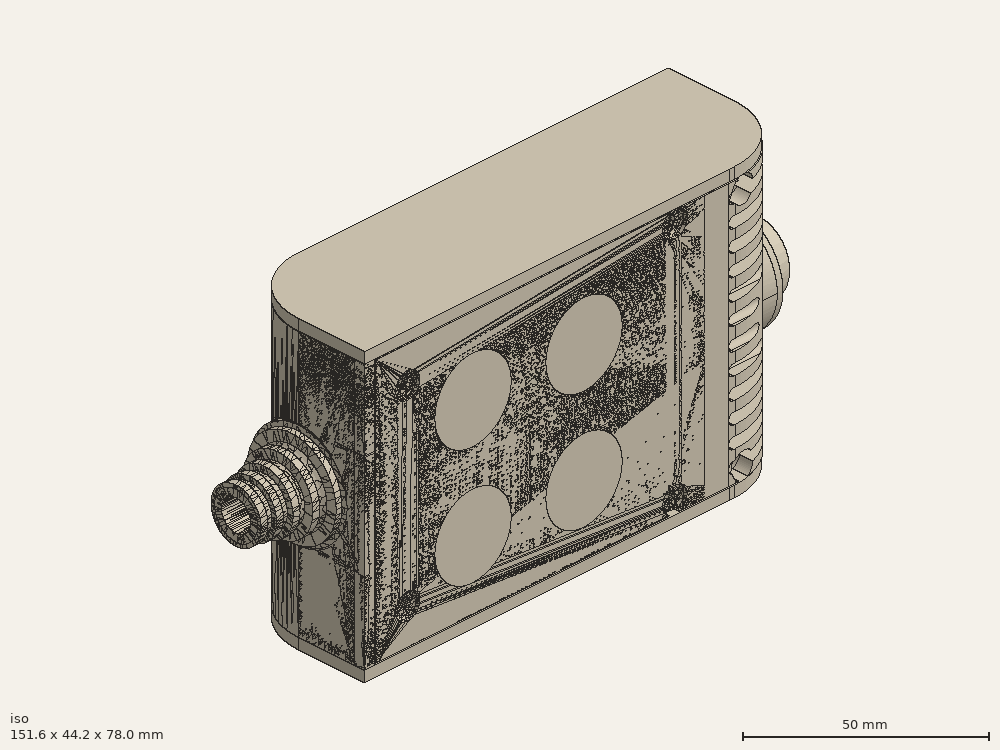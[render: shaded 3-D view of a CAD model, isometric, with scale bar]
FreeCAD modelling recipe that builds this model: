
FCSTD DOCUMENT  (FreeCAD 0.19R0.19.2)
Label: enclosure_201FCStd
License: All rights reserved
LicenseURL: http://en.wikipedia.org/wiki/All_rights_reserved
objects: Part::Revolution×152, Part::MultiFuse×146, Part::Feature×146, Sketcher::SketchObject×84, Part::Cut×70, Part::Cylinder×70, Part::Extrusion×67, Part::Fillet×58, Part::Box×36, App::MeasureDistance×4, PartDesign::Body×2, Image::ImagePlane×1
note: 831 computed .brp shape members not serialized (recipe doc carries the construction recipe); baked Part::Feature solids carry a one-line shape summary decoded from their .brp

FEATURE [Sketcher::SketchObject] Sketch  label="topSketch"
  FullyConstrained = true
  sketch-geometry (20):
    g0: LineSegment StartX=5.21097e-06 StartY=3 StartZ=0 EndX=5.21097e-06 EndY=19 EndZ=0
    g1: ArcOfCircle CenterX=19 CenterY=19 CenterZ=0 NormalX=0 NormalY=0 NormalZ=1 AngleXU=0 Radius=19 StartAngle=1.5708 EndAngle=3.14159
    g2: ArcOfCircle CenterX=19 CenterY=19 CenterZ=0 NormalX=0 NormalY=0 NormalZ=1 AngleXU=0 Radius=16 StartAngle=1.5708 EndAngle=3.14159
    g3: LineSegment StartX=114 StartY=35 StartZ=0 EndX=19 EndY=35 EndZ=0
    g4: LineSegment StartX=5.21097e-06 StartY=3 StartZ=0 EndX=5.21097e-06 EndY=0 EndZ=0
    g5: LineSegment StartX=3 StartY=0 StartZ=0 EndX=5.21097e-06 EndY=0 EndZ=0
    g6: LineSegment StartX=3 StartY=19 StartZ=0 EndX=3 EndY=0 EndZ=0
    g7: LineSegment StartX=19 StartY=38 StartZ=0 EndX=124 EndY=38 EndZ=0
    g8: Circle CenterX=119 CenterY=35 CenterZ=0 NormalX=0 NormalY=0 NormalZ=1 AngleXU=0 Radius=1
    g9: Circle CenterX=121 CenterY=35 CenterZ=0 NormalX=0 NormalY=0 NormalZ=1 AngleXU=0 Radius=1
    g10: Circle CenterX=121 CenterY=33 CenterZ=0 NormalX=0 NormalY=0 NormalZ=1 AngleXU=0 Radius=1
    g11: BSplineCurve PolesCount=3 KnotsCount=2 Degree=2 IsPeriodic=0
    g12: GeomPoint X=119 Y=35 Z=0
    g13: GeomPoint X=121 Y=33 Z=0
    g14: LineSegment StartX=119 StartY=35 StartZ=0 EndX=114 EndY=35 EndZ=0
    g15: ArcOfCircle CenterX=105 CenterY=19 CenterZ=0 NormalX=0 NormalY=0 NormalZ=1 AngleXU=0 Radius=19 StartAngle=5.7297 EndAngle=6.28319
    g16: ArcOfCircle CenterX=105 CenterY=19 CenterZ=0 NormalX=0 NormalY=0 NormalZ=1 AngleXU=0 Radius=16 StartAngle=5.60905 EndAngle=6.28319
    g17: LineSegment StartX=121 StartY=33 StartZ=0 EndX=121 EndY=19 EndZ=0
    g18: LineSegment StartX=124 StartY=38 StartZ=0 EndX=124 EndY=19 EndZ=0
    g19: LineSegment StartX=117.5 StartY=9.01251 StartZ=0 EndX=121.163 EndY=9.0125 EndZ=0
  constraints (46):
    c: Vertical(g0)
    c: Block(g0)
    c: Coincident(g1,g0)
    c: Block(g1)
    c: Coincident(g2,g1)
    c: Block(g2)
    c: Coincident(g3,g2)
    c: Horizontal(g3)
    c: Tangent(g3,g2)
    c: Coincident(g4,g0)
    c: Distance(g4) = 3
    c: Vertical(g4)
    c: Coincident(g5,g4)
    c: Horizontal(g5)
    c: Coincident(g6,g2)
    c: Coincident(g6,g5)
    c: Vertical(g6)
    c: Horizontal(g7)
    c: Distance(g7) = 105
    c: Coincident(g7,g1)
    c: Block(g3)
    c: Weight(g8) = 1
    c: Equal(g8,g9)
    c: Equal(g8,g10)
    c: InternalAlignment(g8,g11)
    c: InternalAlignment(g9,g11)
    c: InternalAlignment(g10,g11)
    c: InternalAlignment(g12,g11)
    c: InternalAlignment(g13,g11)
    c: Block(g11)
    c: Coincident(g14,g11)
    c: Coincident(g14,g3)
    c: Horizontal(g14)
    c: Block(g15)
    c: Coincident(g16,g15)
    c: Block(g16)
    c: Coincident(g17,g11)
    c: Coincident(g17,g16)
    c: Vertical(g17)
    c: Distance(g17) = 14
    c: Coincident(g18,g7)
    c: Coincident(g18,g15)
    c: Vertical(g18)
    c: Distance(g18) = 19
    c: Coincident(g19,g16)
    c: Coincident(g19,g15)
FEATURE [Sketcher::SketchObject] Sketch001  label="bottomSketch"
  FullyConstrained = true
  sketch-geometry (32):
    g0: LineSegment StartX=3.3 StartY=-6.03275e-07 StartZ=0 EndX=98 EndY=-6.03275e-07 EndZ=0
    g1: ArcOfCircle CenterX=98 CenterY=19 CenterZ=0 NormalX=0 NormalY=0 NormalZ=1 AngleXU=0 Radius=19 StartAngle=4.71239 EndAngle=5.71103
    g2: LineSegment StartX=6.3 StartY=8 StartZ=0 EndX=3.3 EndY=8 EndZ=0
    g3: LineSegment StartX=3.3 StartY=8 StartZ=0 EndX=3.3 EndY=-6.03275e-07 EndZ=0
    g4: ArcOfCircle CenterX=8.3 CenterY=5 CenterZ=0 NormalX=0 NormalY=0 NormalZ=1 AngleXU=0 Radius=2 StartAngle=3.14159 EndAngle=4.71239
    g5: LineSegment StartX=6.3 StartY=8 StartZ=0 EndX=6.3 EndY=5 EndZ=0
    g6: ArcOfCircle CenterX=98 CenterY=19 CenterZ=0 NormalX=0 NormalY=0 NormalZ=1 AngleXU=0 Radius=12.7 StartAngle=4.71239 EndAngle=6.28319
    g7: LineSegment StartX=94.7 StartY=3 StartZ=0 EndX=8.3 EndY=3 EndZ=0
    g8-g12: Circle x5 (B-spline internal-alignment scaffolding for g13; pole/knot coordinates omitted)
    g13: BSplineCurve PolesCount=5 KnotsCount=3 Degree=3 IsPeriodic=0
    g14: GeomPoint X=98 Y=6.3 Z=0
    g15: GeomPoint X=96.3938 Y=4.71946 Z=0
    g16: GeomPoint X=94.7 Y=3 Z=0
    g17-g23: Circle x7 (B-spline internal-alignment scaffolding for g24; pole/knot coordinates omitted)
    g24: BSplineCurve PolesCount=7 KnotsCount=5 Degree=3 IsPeriodic=0
    g25-g29: GeomPoint x5 (B-spline internal-alignment scaffolding for g24; pole/knot coordinates omitted)
    g30: ArcOfCircle CenterX=98 CenterY=19 CenterZ=0 NormalX=0 NormalY=0 NormalZ=1 AngleXU=0 Radius=15.7 StartAngle=5.81226 EndAngle=6.28319
    g31: LineSegment StartX=110.7 StartY=19 StartZ=0 EndX=113.7 EndY=19 EndZ=0
  constraints (41):
    c: Horizontal(g0)
    c: Coincident(g1,g0)
    c: Block(g1)
    c: Horizontal(g2)
    c: Distance(g2) = 3
    c: Coincident(g3,g2)
    c: Vertical(g3)
    c: Coincident(g3,g0)
    c: Block(g4)
    c: Block(g2)
    c: Coincident(g5,g2)
    c: Coincident(g5,g4)
    c: Vertical(g5)
    c: Coincident(g6,g1)
    c: Block(g6)
    c: Coincident(g7,g4)
    c: Horizontal(g7)
    c: Block(g0)
    c: Block(g7)
    c: Block(g3)
    c: Coincident(g13,g6)
    c: Weight(g8) = 1
    c: Equal(g8, g9-g12) x4
    c: Coincident(g13,g7)
    c: InternalAlignment(g8-g12 -> g13) x5
    c: InternalAlignment(g14,g13)
    c: InternalAlignment(g15,g13)
    c: InternalAlignment(g16,g13)
    c: Block(g13)
    c: Weight(g17) = 1
    c: Equal(g17, g18-g23) x6
    c: Coincident(g24,g1)
    c: InternalAlignment(g17-g23 -> g24) x7
    c: InternalAlignment(g25-g29 -> g24) x5
    c: Block(g24)
    c: Coincident(g30,g24)
    c: Coincident(g31,g6)
    c: Coincident(g31,g30)
    c: Horizontal(g31)
    c: Block(g31)
    c: Block(g30)
FEATURE [Part::Extrusion] Extrude  label="top"
  Base = -> Sketch
  Dir = (0,0,1)
  DirMode = 2
  FaceMakerClass = Part::FaceMakerBullseye
  LengthFwd = 72
  LengthRev = 0
  Solid = true
  Symmetric = false
FEATURE [Part::Extrusion] Extrude001  label="bottom"
  Base = -> Sketch001
  Dir = (0,0,1)
  DirMode = 2
  FaceMakerClass = Part::FaceMakerBullseye
  LengthFwd = 71.4
  LengthRev = 0
  Placement = pos=(0,0,0.3) rot=(0,0,1;0rad)
  Solid = true
  Symmetric = false
FEATURE [Sketcher::SketchObject] Sketch002  label="topSketch001"
  FullyConstrained = true
  sketch-geometry (8):
    g0: ArcOfCircle CenterX=19 CenterY=19.0975 CenterZ=0 NormalX=0 NormalY=0 NormalZ=1 AngleXU=0 Radius=18.9025 StartAngle=1.5708 EndAngle=3.14674
    g1: LineSegment StartX=0.0977805 StartY=19.0003 StartZ=0 EndX=0.0977805 EndY=0.000251602 EndZ=0
    g2: LineSegment StartX=19 StartY=38 StartZ=0 EndX=124 EndY=38 EndZ=0
    g3: LineSegment StartX=0.0977805 StartY=0.000251602 StartZ=0 EndX=105.098 EndY=0.000251602 EndZ=0
    g4: LineSegment StartX=124 StartY=38 StartZ=0 EndX=125.616 EndY=38 EndZ=0
    g5: LineSegment StartX=105.098 StartY=0.000251602 StartZ=0 EndX=106.713 EndY=0.000251602 EndZ=0
    g6: ArcOfCircle CenterX=106.616 CenterY=19 CenterZ=0 NormalX=0 NormalY=0 NormalZ=1 AngleXU=0 Radius=19 StartAngle=4.71754 EndAngle=6.28319
    g7: LineSegment StartX=125.616 StartY=38 StartZ=0 EndX=125.616 EndY=19 EndZ=0
  constraints (21):
    c: Block(g0)
    c: Coincident(g1,g0)
    c: Vertical(g1)
    c: Horizontal(g2)
    c: Distance(g2) = 105
    c: Coincident(g2,g0)
    c: Distance(g1) = 19
    c: Coincident(g3,g1)
    c: Horizontal(g3)
    c: Distance(g3) = 105
    c: Coincident(g4,g2)
    c: Horizontal(g4)
    c: Distance(g4) = 1.61553
    c: Horizontal(g5)
    c: Equal(g4,g5) = 1.61553
    c: Coincident(g5,g3)
    c: Block(g6)
    c: Coincident(g6,g5)
    c: Coincident(g7,g4)
    c: Coincident(g7,g6)
    c: Vertical(g7)
FEATURE [Part::Extrusion] Extrude002  label="sideA"
  Base = -> Sketch002
  Dir = (0,0,1)
  DirMode = 2
  FaceMakerClass = Part::FaceMakerBullseye
  LengthFwd = 3
  LengthRev = 0
  Placement = pos=(0,0,-3) rot=(0,0,1;0rad)
  Solid = true
  Symmetric = false
FEATURE [Sketcher::SketchObject] Sketch003  label="topSketch002"
  FullyConstrained = true
  sketch-geometry (6):
    g0: LineSegment StartX=19 StartY=38 StartZ=0 EndX=117 EndY=38 EndZ=0
    g1: ArcOfCircle CenterX=19 CenterY=19 CenterZ=0 NormalX=0 NormalY=0 NormalZ=1 AngleXU=0 Radius=19 StartAngle=1.5708 EndAngle=3.14159
    g2: LineSegment StartX=117 StartY=38 StartZ=0 EndX=117 EndY=19 EndZ=0
    g3: LineSegment StartX=98 StartY=1.0161e-12 StartZ=0 EndX=5.22862e-06 EndY=1.0161e-12 EndZ=0
    g4: LineSegment StartX=5.22862e-06 StartY=19 StartZ=0 EndX=5.22862e-06 EndY=1.0161e-12 EndZ=0
    g5: ArcOfCircle CenterX=98 CenterY=19 CenterZ=0 NormalX=0 NormalY=0 NormalZ=1 AngleXU=0 Radius=19 StartAngle=4.71239 EndAngle=6.28319
  constraints (16):
    c: Horizontal(g0)
    c: Distance(g0) = 98
    c: Coincident(g1,g0)
    c: Block(g1)
    c: Coincident(g2,g0)
    c: Vertical(g2)
    c: Distance(g2) = 19
    c: Horizontal(g3)
    c: Coincident(g4,g1)
    c: Vertical(g4)
    c: Coincident(g3,g4)
    c: Block(g3)
    c: Coincident(g5,g2)
    c: Coincident(g5,g3)
    c: Block(g0)
    c: Block(g5)
FEATURE [Sketcher::SketchObject] Sketch004
  FullyConstrained = true
  MapMode = 3
  Placement = pos=(0,0,0) rot=(1,0,0;1.5708rad)
  Support = -> [Extrude]
  sketch-geometry (8):
    g0: Circle CenterX=80.351 CenterY=-67.6202 CenterZ=0 NormalX=0 NormalY=0 NormalZ=1 AngleXU=0 Radius=2
    g1: Circle CenterX=80.351 CenterY=-67.6202 CenterZ=0 NormalX=0 NormalY=0 NormalZ=1 AngleXU=0 Radius=3
    g2: Circle CenterX=80.351 CenterY=-4.92017 CenterZ=0 NormalX=0 NormalY=0 NormalZ=1 AngleXU=0 Radius=2
    g3: Circle CenterX=80.351 CenterY=-4.92017 CenterZ=0 NormalX=0 NormalY=0 NormalZ=1 AngleXU=0 Radius=3
    g4: Circle CenterX=23.851 CenterY=-4.92017 CenterZ=0 NormalX=0 NormalY=0 NormalZ=1 AngleXU=0 Radius=2
    g5: Circle CenterX=23.851 CenterY=-4.92017 CenterZ=0 NormalX=0 NormalY=0 NormalZ=1 AngleXU=0 Radius=3
    g6: Circle CenterX=23.851 CenterY=-67.6202 CenterZ=0 NormalX=0 NormalY=0 NormalZ=1 AngleXU=0 Radius=2
    g7: Circle CenterX=23.851 CenterY=-67.6202 CenterZ=0 NormalX=0 NormalY=0 NormalZ=1 AngleXU=0 Radius=3
  constraints (8):
    c: Block(g3)
    c: Block(g2)
    c: Block(g1)
    c: Block(g0)
    c: Block(g6)
    c: Block(g7)
    c: Block(g4)
    c: Block(g5)
FEATURE [Part::Extrusion] Extrude004
  Base = -> Sketch004
  Dir = (0,-1,2e-16)
  DirMode = 2
  FaceMakerClass = Part::FaceMakerBullseye
  LengthFwd = 6
  LengthRev = 0
  Placement = pos=(0,9,0) rot=(0,0,1;0rad)
  Solid = true
  Symmetric = false
FEATURE [Sketcher::SketchObject] Sketch005
  FullyConstrained = true
  MapMode = 3
  Placement = pos=(0,0,0) rot=(1,0,0;1.5708rad)
  Support = -> [Extrude]
  sketch-geometry (8):
    g0: Circle CenterX=80.351 CenterY=-67.6202 CenterZ=0 NormalX=0 NormalY=0 NormalZ=1 AngleXU=0 Radius=3
    g1: Circle CenterX=80.351 CenterY=-4.92017 CenterZ=0 NormalX=0 NormalY=0 NormalZ=1 AngleXU=0 Radius=3
    g2: Circle CenterX=23.851 CenterY=-4.92017 CenterZ=0 NormalX=0 NormalY=0 NormalZ=1 AngleXU=0 Radius=3
    g3: Circle CenterX=23.851 CenterY=-67.6202 CenterZ=0 NormalX=0 NormalY=0 NormalZ=1 AngleXU=0 Radius=3
    g4: Circle CenterX=23.851 CenterY=-67.6202 CenterZ=0 NormalX=0 NormalY=0 NormalZ=1 AngleXU=0 Radius=5
    g5: Circle CenterX=80.351 CenterY=-67.6202 CenterZ=0 NormalX=0 NormalY=0 NormalZ=1 AngleXU=0 Radius=5
    g6: Circle CenterX=23.851 CenterY=-4.92017 CenterZ=0 NormalX=0 NormalY=0 NormalZ=1 AngleXU=0 Radius=5
    g7: Circle CenterX=80.351 CenterY=-4.92017 CenterZ=0 NormalX=0 NormalY=0 NormalZ=1 AngleXU=0 Radius=5
  constraints (8):
    c: Block(g1)
    c: Block(g0)
    c: Block(g3)
    c: Block(g2)
    c: Block(g5)
    c: Block(g4)
    c: Block(g6)
    c: Block(g7)
FEATURE [Part::Extrusion] Extrude005
  Base = -> Sketch005
  Dir = (0,-1,2e-16)
  DirMode = 2
  FaceMakerClass = Part::FaceMakerBullseye
  LengthFwd = 2
  LengthRev = 0
  Solid = true
  Symmetric = false
FEATURE [Sketcher::SketchObject] Sketch006
  FullyConstrained = true
  MapMode = 3
  Placement = pos=(0,0,0) rot=(1,0,0;1.5708rad)
  sketch-geometry (8):
    g0: Circle CenterX=80.351 CenterY=-67.6202 CenterZ=0 NormalX=0 NormalY=0 NormalZ=1 AngleXU=0 Radius=3
    g1: Circle CenterX=80.351 CenterY=-4.92017 CenterZ=0 NormalX=0 NormalY=0 NormalZ=1 AngleXU=0 Radius=3
    g2: Circle CenterX=23.851 CenterY=-4.92017 CenterZ=0 NormalX=0 NormalY=0 NormalZ=1 AngleXU=0 Radius=3
    g3: Circle CenterX=23.851 CenterY=-67.6202 CenterZ=0 NormalX=0 NormalY=0 NormalZ=1 AngleXU=0 Radius=3
    g4: Circle CenterX=23.851 CenterY=-67.6202 CenterZ=0 NormalX=0 NormalY=0 NormalZ=1 AngleXU=0 Radius=5
    g5: Circle CenterX=80.351 CenterY=-67.6202 CenterZ=0 NormalX=0 NormalY=0 NormalZ=1 AngleXU=0 Radius=5
    g6: Circle CenterX=23.851 CenterY=-4.92017 CenterZ=0 NormalX=0 NormalY=0 NormalZ=1 AngleXU=0 Radius=5
    g7: Circle CenterX=80.351 CenterY=-4.92017 CenterZ=0 NormalX=0 NormalY=0 NormalZ=1 AngleXU=0 Radius=5
  constraints (8):
    c: Block(g1)
    c: Block(g0)
    c: Block(g3)
    c: Block(g2)
    c: Block(g5)
    c: Block(g4)
    c: Block(g6)
    c: Block(g7)
FEATURE [Part::Extrusion] Extrude007
  Base = -> Sketch006
  Dir = (0,-1,2e-16)
  DirMode = 2
  FaceMakerClass = Part::FaceMakerBullseye
  LengthFwd = 2
  LengthRev = 0
  Solid = true
  Symmetric = false
FEATURE [Part::Fillet] Fillet
  Base = -> Extrude007
  Edges = 4 edges r=1.99: [Edge6,Edge12,Edge18,Edge24]
FEATURE [Part::Cut] Cut
  Base = -> Extrude005
  Placement = pos=(0,5,0) rot=(0,0,1;0rad)
  Tool = -> Fillet
FEATURE [Part::MultiFuse] Fusion  label="pCBScrews"
  Placement = pos=(-2.5,0,72.3) rot=(0,0,1;0rad)
  Shapes = -> [Extrude004,Cut]
FEATURE [App::MeasureDistance] Distance  label="Distance: 0.69 mm"
  Distance = 0.685967
  P1 = (24.0138,2.9647,0.3)
  P2 = (23.8901,3,-0.373787)
FEATURE [App::MeasureDistance] Distance001  label="Distance: 0.53 mm"
  Distance = 0.533607
  P1 = (80.2939,3,72.2334)
  P2 = (80.281,2.99661,71.7)
FEATURE [Part::Fillet] Fillet001
  Base = -> Extrude001
  Edges = 1 edges r=2.4: [Edge17]
FEATURE [Part::Fillet] Fillet002  label="bottom001"
  Base = -> Fillet001
  Edges = 1 edges r=2.4: [Edge36]
FEATURE [Part::Fillet] Fillet003  label="top001"
  Base = -> Extrude
  Edges = 1 edges r=2: [Edge1]
FEATURE [Sketcher::SketchObject] Sketch007
  FullyConstrained = true
  sketch-geometry (16):
    g0: LineSegment StartX=4 StartY=0 StartZ=0 EndX=4 EndY=2.4 EndZ=0
    g1: LineSegment StartX=4 StartY=2.4 StartZ=0 EndX=7 EndY=2.4 EndZ=0
    g2: LineSegment StartX=4 StartY=0 StartZ=0 EndX=5.7 EndY=0 EndZ=0
    g3: LineSegment StartX=5.7 StartY=0 StartZ=0 EndX=5.7 EndY=-5.6 EndZ=0
    g4-g8: Circle x5 (B-spline internal-alignment scaffolding for g9; pole/knot coordinates omitted)
    g9: BSplineCurve PolesCount=5 KnotsCount=3 Degree=3 IsPeriodic=0
    g10: GeomPoint X=7 Y=2.4 Z=0
    g11: GeomPoint X=10.4582 Y=-1.55472 Z=0
    g12: GeomPoint X=14 Y=-5.6 Z=0
    g13: LineSegment StartX=14 StartY=-5.6 StartZ=0 EndX=14 EndY=-14.1 EndZ=0
    g14: LineSegment StartX=14 StartY=-14.1 StartZ=0 EndX=6.5 EndY=-14.1 EndZ=0
    g15: LineSegment StartX=5.7 StartY=-5.6 StartZ=0 EndX=6.5 EndY=-14.1 EndZ=0
  constraints (28):
    c: Distance(g0) = 2.4
    c: Vertical(g0)
    c: Block(g0)
    c: Coincident(g1,g0)
    c: Horizontal(g1)
    c: Distance(g1) = 3
    c: Coincident(g2,g0)
    c: Horizontal(g2)
    c: Distance(g2) = 1.7
    c: Coincident(g3,g2)
    c: Vertical(g3)
    c: Distance(g3) = 5.6
    c: Coincident(g9,g1)
    c: Weight(g4) = 1
    c: Equal(g4, g5-g8) x4
    c: InternalAlignment(g4-g8 -> g9) x5
    c: InternalAlignment(g10,g9)
    c: InternalAlignment(g11,g9)
    c: InternalAlignment(g12,g9)
    c: Block(g9)
    c: Coincident(g13,g9)
    c: Vertical(g13)
    c: Distance(g13) = 8.5
    c: Coincident(g14,g13)
    c: Horizontal(g14)
    c: Distance(g14) = 7.5
    c: Coincident(g15,g3)
    c: Coincident(g15,g14)
FEATURE [Part::Feature] Face
  shape: bbox 10 x 16.5 x 2e-07 mm, 1 faces, 0 solids (baked)
FEATURE [Part::Revolution] Revolve  label="plugHousing"
  Angle = 360
  Axis = (0,1,0)
  Base = (0,0,0)
  FaceMakerClass = Part::FaceMakerBullseye
  Placement = pos=(0,0,36.15) rot=(0,0,1;0rad)
  Solid = false
  Source = -> Face
  Symmetric = false
FEATURE [Part::Feature] Face001
  shape: bbox 10 x 16.5 x 2e-07 mm, 1 faces, 0 solids (baked)
FEATURE [Part::Revolution] Revolve001  label="plugHousing001"
  Angle = 360
  Axis = (0,1,0)
  Base = (0,0,0)
  FaceMakerClass = Part::FaceMakerBullseye
  Placement = pos=(0,0,36.15) rot=(0,0,1;0rad)
  Solid = false
  Source = -> Face001
  Symmetric = false
FEATURE [Part::MultiFuse] Fusion001  label="plugHousing002"
  Placement = pos=(0,0,0) rot=(0,0,1;1.5708rad)
  Shapes = -> [Revolve001,Revolve]
FEATURE [Part::Feature] Face002
  shape: bbox 10 x 16.5 x 2e-07 mm, 1 faces, 0 solids (baked)
FEATURE [Part::Revolution] Revolve003  label="plugHousing005"
  Angle = 360
  Axis = (0,1,0)
  Base = (0,0,0)
  FaceMakerClass = Part::FaceMakerBullseye
  Placement = pos=(0,0,36.15) rot=(0,0,1;0rad)
  Solid = false
  Source = -> Face002
  Symmetric = false
FEATURE [Part::Feature] Face003
  shape: bbox 10 x 16.5 x 2e-07 mm, 1 faces, 0 solids (baked)
FEATURE [Part::Revolution] Revolve002  label="plugHousing003"
  Angle = 360
  Axis = (0,1,0)
  Base = (0,0,0)
  FaceMakerClass = Part::FaceMakerBullseye
  Placement = pos=(0,0,36.15) rot=(0,0,1;0rad)
  Solid = false
  Source = -> Face003
  Symmetric = false
FEATURE [Part::MultiFuse] Fusion002  label="plugHousing004"
  Placement = pos=(0,0,0) rot=(0,0,1;1.5708rad)
  Shapes = -> [Revolve002,Revolve003]
FEATURE [Part::MultiFuse] Fusion003  label="plugHousing006"
  Placement = pos=(0,19,0) rot=(0,0,1;3.14159rad)
  Shapes = -> [Fusion002,Fusion001]
FEATURE [Part::Feature] Face004
  shape: bbox 10 x 16.5 x 2e-07 mm, 1 faces, 0 solids (baked)
FEATURE [Part::Revolution] Revolve006  label="plugHousing010"
  Angle = 360
  Axis = (0,1,0)
  Base = (0,0,0)
  FaceMakerClass = Part::FaceMakerBullseye
  Placement = pos=(0,0,36.15) rot=(0,0,1;0rad)
  Solid = false
  Source = -> Face004
  Symmetric = false
FEATURE [Part::Feature] Face005
  shape: bbox 10 x 16.5 x 2e-07 mm, 1 faces, 0 solids (baked)
FEATURE [Part::Revolution] Revolve007  label="plugHousing011"
  Angle = 360
  Axis = (0,1,0)
  Base = (0,0,0)
  FaceMakerClass = Part::FaceMakerBullseye
  Placement = pos=(0,0,36.15) rot=(0,0,1;0rad)
  Solid = false
  Source = -> Face005
  Symmetric = false
FEATURE [Part::Feature] Face006
  shape: bbox 10 x 16.5 x 2e-07 mm, 1 faces, 0 solids (baked)
FEATURE [Part::Revolution] Revolve004  label="plugHousing007"
  Angle = 360
  Axis = (0,1,0)
  Base = (0,0,0)
  FaceMakerClass = Part::FaceMakerBullseye
  Placement = pos=(0,0,36.15) rot=(0,0,1;0rad)
  Solid = false
  Source = -> Face006
  Symmetric = false
FEATURE [Part::MultiFuse] Fusion004  label="plugHousing009"
  Placement = pos=(0,0,0) rot=(0,0,1;1.5708rad)
  Shapes = -> [Revolve004,Revolve007]
FEATURE [Part::Feature] Face007
  shape: bbox 10 x 16.5 x 2e-07 mm, 1 faces, 0 solids (baked)
FEATURE [Part::Revolution] Revolve005  label="plugHousing008"
  Angle = 360
  Axis = (0,1,0)
  Base = (0,0,0)
  FaceMakerClass = Part::FaceMakerBullseye
  Placement = pos=(0,0,36.15) rot=(0,0,1;0rad)
  Solid = false
  Source = -> Face007
  Symmetric = false
FEATURE [Part::MultiFuse] Fusion005  label="plugHousing012"
  Placement = pos=(0,0,0) rot=(0,0,1;1.5708rad)
  Shapes = -> [Revolve006,Revolve005]
FEATURE [Part::MultiFuse] Fusion006  label="plugHousing013"
  Placement = pos=(0,19,0) rot=(0,0,1;3.14159rad)
  Shapes = -> [Fusion005,Fusion004]
FEATURE [Part::MultiFuse] Fusion007  label="plugHousing014"
  Placement = pos=(122.621,0,-0.15) rot=(0,0,1;0rad)
  Shapes = -> [Fusion003,Fusion006]
FEATURE [Part::Cylinder] Cylinder002
  Angle = 360
  AttacherType = Attacher::AttachEngine3D
  Height = 20
  Placement = pos=(0,0,36.15) rot=(0,0,1;0rad)
  Radius = 4
FEATURE [Part::Cylinder] Cylinder003
  Angle = 360
  AttacherType = Attacher::AttachEngine3D
  Height = 10
  Placement = pos=(0,0,36.15) rot=(0,0,1;0rad)
  Radius = 4
FEATURE [Part::MultiFuse] Fusion009  label="removeToCreateHoleForPlugHousing"
  Placement = pos=(70,19,36.15) rot=(0,1,0;1.5708rad)
  Shapes = -> [Cylinder002,Cylinder003]
FEATURE [Part::Cylinder] Cylinder004
  Angle = 360
  AttacherType = Attacher::AttachEngine3D
  Height = 20
  Placement = pos=(0,0,36.15) rot=(0,0,1;0rad)
  Radius = 4
FEATURE [Part::Cylinder] Cylinder005
  Angle = 360
  AttacherType = Attacher::AttachEngine3D
  Height = 10
  Placement = pos=(0,0,36.15) rot=(0,0,1;0rad)
  Radius = 4
FEATURE [Part::MultiFuse] Fusion010  label="removeToCreateHoleForPlugHousing001"
  Placement = pos=(70,19,36.15) rot=(0,1,0;1.5708rad)
  Shapes = -> [Cylinder004,Cylinder005]
FEATURE [Part::Cut] Cut001
  Base = -> Fillet003
  Tool = -> Fusion010
FEATURE [Part::Cut] Cut002  label="Bottom"
  Base = -> Fillet002
  Tool = -> Fusion009
FEATURE [Part::Feature] Face008
  shape: bbox 10 x 16.5 x 2e-07 mm, 1 faces, 0 solids (baked)
FEATURE [Part::Revolution] Revolve011  label="plugHousing021"
  Angle = 360
  Axis = (0,1,0)
  Base = (0,0,0)
  FaceMakerClass = Part::FaceMakerBullseye
  Placement = pos=(0,0,36.15) rot=(0,0,1;0rad)
  Solid = false
  Source = -> Face008
  Symmetric = false
FEATURE [Part::Feature] Face009
  shape: bbox 10 x 16.5 x 2e-07 mm, 1 faces, 0 solids (baked)
FEATURE [Part::Revolution] Revolve012  label="plugHousing022"
  Angle = 360
  Axis = (0,1,0)
  Base = (0,0,0)
  FaceMakerClass = Part::FaceMakerBullseye
  Placement = pos=(0,0,36.15) rot=(0,0,1;0rad)
  Solid = false
  Source = -> Face009
  Symmetric = false
FEATURE [Part::Feature] Face010 .. Face013  x4 (patterned run collapsed; names and placements below)
  shape: bbox 10 x 16.5 x 2e-07 mm, 1 faces, 0 solids (baked)
FEATURE [Part::Revolution] Revolve015  label="plugHousing027"
  Angle = 360
  Axis = (0,1,0)
  Base = (0,0,0)
  FaceMakerClass = Part::FaceMakerBullseye
  Placement = pos=(0,0,36.15) rot=(0,0,1;0rad)
  Solid = false
  Source = -> Face013
  Symmetric = false
FEATURE [Part::Feature] Face014
  shape: bbox 10 x 16.5 x 2e-07 mm, 1 faces, 0 solids (baked)
FEATURE [Part::Feature] Face015
  shape: bbox 10 x 16.5 x 2e-07 mm, 1 faces, 0 solids (baked)
FEATURE [Part::Feature] Face016
  shape: bbox 10 x 16.5 x 2e-07 mm, 1 faces, 0 solids (baked)
FEATURE [Part::Revolution] Revolve019  label="plugHousing033"
  Angle = 360
  Axis = (0,1,0)
  Base = (0,0,0)
  FaceMakerClass = Part::FaceMakerBullseye
  Placement = pos=(0,0,36.15) rot=(0,0,1;0rad)
  Solid = false
  Source = -> Face016
  Symmetric = false
FEATURE [Part::Feature] Face017
  shape: bbox 10 x 16.5 x 2e-07 mm, 1 faces, 0 solids (baked)
FEATURE [Part::Revolution] Revolve020  label="plugHousing034"
  Angle = 360
  Axis = (0,1,0)
  Base = (0,0,0)
  FaceMakerClass = Part::FaceMakerBullseye
  Placement = pos=(0,0,36.15) rot=(0,0,1;0rad)
  Solid = false
  Source = -> Face017
  Symmetric = false
FEATURE [Part::Feature] Face018
  shape: bbox 10 x 16.5 x 2e-07 mm, 1 faces, 0 solids (baked)
FEATURE [Part::Revolution] Revolve016  label="plugHousing030"
  Angle = 360
  Axis = (0,1,0)
  Base = (0,0,0)
  FaceMakerClass = Part::FaceMakerBullseye
  Placement = pos=(0,0,36.15) rot=(0,0,1;0rad)
  Solid = false
  Source = -> Face018
  Symmetric = false
FEATURE [Part::MultiFuse] Fusion020  label="plugHousing038"
  Placement = pos=(0,0,0) rot=(0,0,1;1.5708rad)
  Shapes = -> [Revolve016,Revolve020]
FEATURE [Part::Feature] Face019
  shape: bbox 10 x 16.5 x 2e-07 mm, 1 faces, 0 solids (baked)
FEATURE [Part::Feature] Face020
  shape: bbox 10 x 16.5 x 2e-07 mm, 1 faces, 0 solids (baked)
FEATURE [Part::Revolution] Revolve017  label="plugHousing031"
  Angle = 360
  Axis = (0,1,0)
  Base = (0,0,0)
  FaceMakerClass = Part::FaceMakerBullseye
  Placement = pos=(0,0,36.15) rot=(0,0,1;0rad)
  Solid = false
  Source = -> Face020
  Symmetric = false
FEATURE [Part::MultiFuse] Fusion021  label="plugHousing039"
  Placement = pos=(0,0,0) rot=(0,0,1;1.5708rad)
  Shapes = -> [Revolve019,Revolve017]
FEATURE [Part::MultiFuse] Fusion023  label="plugHousing041"
  Placement = pos=(0,19,0) rot=(0,0,1;3.14159rad)
  Shapes = -> [Fusion021,Fusion020]
FEATURE [Part::Revolution] Revolve022  label="plugHousing043"
  Angle = 360
  Axis = (0,1,0)
  Base = (0,0,0)
  FaceMakerClass = Part::FaceMakerBullseye
  Placement = pos=(0,0,36.15) rot=(0,0,1;0rad)
  Solid = false
  Source = -> Face019
  Symmetric = false
FEATURE [Part::Feature] Face021
  shape: bbox 10 x 16.5 x 2e-07 mm, 1 faces, 0 solids (baked)
FEATURE [Part::Revolution] Revolve023  label="plugHousing044"
  Angle = 360
  Axis = (0,1,0)
  Base = (0,0,0)
  FaceMakerClass = Part::FaceMakerBullseye
  Placement = pos=(0,0,36.15) rot=(0,0,1;0rad)
  Solid = false
  Source = -> Face021
  Symmetric = false
FEATURE [Part::Feature] Face022
  shape: bbox 10 x 16.5 x 2e-07 mm, 1 faces, 0 solids (baked)
FEATURE [Part::Revolution] Revolve018  label="plugHousing032"
  Angle = 360
  Axis = (0,1,0)
  Base = (0,0,0)
  FaceMakerClass = Part::FaceMakerBullseye
  Placement = pos=(0,0,36.15) rot=(0,0,1;0rad)
  Solid = false
  Source = -> Face022
  Symmetric = false
FEATURE [Part::MultiFuse] Fusion022  label="plugHousing040"
  Placement = pos=(0,0,0) rot=(0,0,1;1.5708rad)
  Shapes = -> [Revolve018,Revolve023]
FEATURE [Part::Feature] Face023
  shape: bbox 10 x 16.5 x 2e-07 mm, 1 faces, 0 solids (baked)
FEATURE [Part::Revolution] Revolve021  label="plugHousing035"
  Angle = 360
  Axis = (0,1,0)
  Base = (0,0,0)
  FaceMakerClass = Part::FaceMakerBullseye
  Placement = pos=(0,0,36.15) rot=(0,0,1;0rad)
  Solid = false
  Source = -> Face023
  Symmetric = false
FEATURE [Part::MultiFuse] Fusion018  label="plugHousing036"
  Placement = pos=(0,0,0) rot=(0,0,1;1.5708rad)
  Shapes = -> [Revolve022,Revolve021]
FEATURE [Part::MultiFuse] Fusion019  label="plugHousing037"
  Placement = pos=(0,19,0) rot=(0,0,1;3.14159rad)
  Shapes = -> [Fusion018,Fusion022]
FEATURE [Part::MultiFuse] Fusion024  label="plugHousing042"
  Placement = pos=(122.621,0,-0.15) rot=(0,0,1;0rad)
  Shapes = -> [Fusion023,Fusion019]
FEATURE [Part::Cylinder] Cylinder006
  Angle = 360
  AttacherType = Attacher::AttachEngine3D
  Height = 20
  Placement = pos=(0,0,36.15) rot=(0,0,1;0rad)
  Radius = 14.3
FEATURE [Part::Cylinder] Cylinder007
  Angle = 360
  AttacherType = Attacher::AttachEngine3D
  Height = 10
  Placement = pos=(0,0,36.15) rot=(0,0,1;0rad)
  Radius = 4
FEATURE [Part::MultiFuse] Fusion026  label="removeToCreteHoleForPlugHousing"
  Placement = pos=(70,19,36) rot=(0,1,0;1.5708rad)
  Shapes = -> [Cylinder006,Cylinder007]
FEATURE [Part::Box] Box001  label="Cube001"
  AttacherType = Attacher::AttachEngine3D
  Height = 28
  Length = 3
  Placement = pos=(110.7,19,22) rot=(0,0,1;0rad)
  Width = 15.7
FEATURE [Part::Cut] Cut003  label="top002"
  Base = -> Cut001
  Tool = -> Fusion007
FEATURE [Part::Revolution] Revolve008  label="plugHousing015"
  Angle = 360
  Axis = (0,1,0)
  Base = (0,0,0)
  FaceMakerClass = Part::FaceMakerBullseye
  Placement = pos=(0,0,36.15) rot=(0,0,1;0rad)
  Solid = false
  Source = -> Face010
  Symmetric = false
FEATURE [Part::MultiFuse] Fusion013  label="plugHousing020"
  Placement = pos=(0,0,0) rot=(0,0,1;1.5708rad)
  Shapes = -> [Revolve008,Revolve012]
FEATURE [Part::Cut] Cut004  label="top003"
  Base = -> Cut003
  Placement = pos=(1,0,0) rot=(0,0,1;0rad)
  Tool = -> Fusion026
FEATURE [Part::Cylinder] Cylinder008
  Angle = 360
  AttacherType = Attacher::AttachEngine3D
  Height = 20
  Placement = pos=(0,0,36.15) rot=(0,0,1;0rad)
  Radius = 10.3
FEATURE [Part::Cylinder] Cylinder009
  Angle = 360
  AttacherType = Attacher::AttachEngine3D
  Height = 10
  Placement = pos=(0,0,36.15) rot=(0,0,1;0rad)
  Radius = 4
FEATURE [Part::MultiFuse] Fusion027  label="removeToCreteHoleForPlugHousing001"
  Placement = pos=(70,19,36) rot=(0,1,0;1.5708rad)
  Shapes = -> [Cylinder008,Cylinder009]
FEATURE [Part::Cut] Cut005  label="plugHousingTab"
  Base = -> Box001
  Tool = -> Fusion027
FEATURE [Part::MultiFuse] Fusion028  label="plugHousing045"
  Shapes = -> [Fusion024,Cut005]
FEATURE [Part::Box] Box002  label="Cube002"
  AttacherType = Attacher::AttachEngine3D
  Height = 28.8
  Length = 3
  Placement = pos=(107.3,28,21.6) rot=(0,0,1;0rad)
  Width = 7
FEATURE [Part::Box] Box003  label="Cube003"
  AttacherType = Attacher::AttachEngine3D
  Height = 3
  Length = 6.4
  Placement = pos=(107.3,28,18.6) rot=(0,0,1;0rad)
  Width = 7
FEATURE [Part::Box] Box004  label="Cube004"
  AttacherType = Attacher::AttachEngine3D
  Height = 3
  Length = 6.4
  Placement = pos=(107.3,28,50.4) rot=(0,0,1;0rad)
  Width = 7
FEATURE [Part::MultiFuse] Fusion029  label="plugHousingBracketHolder"
  Shapes = -> [Box004,Box002,Box003]
FEATURE [Part::Cylinder] Cylinder010
  Angle = 360
  AttacherType = Attacher::AttachEngine3D
  Height = 20
  Placement = pos=(0,0,36.15) rot=(0,0,1;0rad)
  Radius = 14.3
FEATURE [Part::Cylinder] Cylinder011
  Angle = 360
  AttacherType = Attacher::AttachEngine3D
  Height = 10
  Placement = pos=(0,0,36.15) rot=(0,0,1;0rad)
  Radius = 4
FEATURE [Part::MultiFuse] Fusion030  label="removeToCreteHoleForPlugHousing002"
  Placement = pos=(70,19,36) rot=(0,1,0;1.5708rad)
  Shapes = -> [Cylinder010,Cylinder011]
FEATURE [Part::Cut] Cut006  label="plugHousingBracketHolder001"
  Base = -> Fusion029
  Tool = -> Fusion030
FEATURE [Part::Cylinder] Cylinder012
  Angle = 360
  AttacherType = Attacher::AttachEngine3D
  Height = 20
  Placement = pos=(0,0,36.15) rot=(0,0,1;0rad)
  Radius = 7
FEATURE [Part::Cylinder] Cylinder013
  Angle = 360
  AttacherType = Attacher::AttachEngine3D
  Height = 10
  Placement = pos=(0,0,36.15) rot=(0,0,1;0rad)
  Radius = 4
FEATURE [Part::MultiFuse] Fusion032  label="removeToCreteHoleForPlugHousing003"
  Placement = pos=(70,19,36) rot=(0,1,0;1.5708rad)
  Shapes = -> [Cylinder012,Cylinder013]
FEATURE [Part::Cut] Cut007  label="bottom002"
  Base = -> Cut002
  Tool = -> Fusion032
FEATURE [Sketcher::SketchObject] Sketch008
  FullyConstrained = true
  sketch-geometry (54):
    g0: LineSegment StartX=-4.2 StartY=0 StartZ=0 EndX=-6.2 EndY=0 EndZ=0
    g1: LineSegment StartX=-14 StartY=-18 StartZ=0 EndX=-14 EndY=-26.5 EndZ=0
    g2: LineSegment StartX=-4.2 StartY=0 StartZ=0 EndX=-4.2 EndY=-13.4877 EndZ=0
    g3: Circle CenterX=-4.2 CenterY=-13.4877 CenterZ=0 NormalX=0 NormalY=0 NormalZ=1 AngleXU=0 Radius=1
    g4: Circle CenterX=-4.2 CenterY=-26.5 CenterZ=0 NormalX=0 NormalY=0 NormalZ=1 AngleXU=0 Radius=1
    g5: Circle CenterX=-8.2 CenterY=-26.5 CenterZ=0 NormalX=0 NormalY=0 NormalZ=1 AngleXU=0 Radius=1
    g6: BSplineCurve PolesCount=3 KnotsCount=2 Degree=2 IsPeriodic=0
    g7: GeomPoint X=-4.2 Y=-13.4877 Z=0
    g8: GeomPoint X=-8.2 Y=-26.5 Z=0
    g9: LineSegment StartX=-14 StartY=-26.5 StartZ=0 EndX=-8.2 EndY=-26.5 EndZ=0
    g10: LineSegment StartX=-10.15 StartY=-12 StartZ=0 EndX=-10.15 EndY=-14 EndZ=0
    g11: LineSegment StartX=-12.8401 StartY=-16 StartZ=0 EndX=-10.1571 EndY=-16 EndZ=0
    g12: LineSegment StartX=-10.15 StartY=-14 StartZ=0 EndX=-8.70761 EndY=-14 EndZ=0
    g13: LineSegment StartX=-12.8401 StartY=-16 StartZ=0 EndX=-12.8401 EndY=-17.6958 EndZ=0
    g14: LineSegment StartX=-10.15 StartY=-12 StartZ=0 EndX=-7.79258 EndY=-12 EndZ=0
    g15: Circle CenterX=-6.2215 CenterY=-2 CenterZ=0 NormalX=0 NormalY=0 NormalZ=1 AngleXU=0 Radius=1
    g16: Circle CenterX=-6.22762 CenterY=-2.58724 CenterZ=0 NormalX=0 NormalY=0 NormalZ=1 AngleXU=0 Radius=1
    g17: Circle CenterX=-6.32538 CenterY=-4 CenterZ=0 NormalX=0 NormalY=0 NormalZ=1 AngleXU=0 Radius=1
    g18: BSplineCurve PolesCount=3 KnotsCount=2 Degree=2 IsPeriodic=0
    g19: GeomPoint X=-6.2215 Y=-2 Z=0
    g20: GeomPoint X=-6.32538 Y=-4 Z=0
    g21: Circle CenterX=-6.48644 CenterY=-5.99526 CenterZ=0 NormalX=0 NormalY=0 NormalZ=1 AngleXU=0 Radius=1
    g22: Circle CenterX=-6.58486 CenterY=-6.99526 CenterZ=0 NormalX=0 NormalY=0 NormalZ=1 AngleXU=0 Radius=1
    g23: Circle CenterX=-6.77343 CenterY=-8 CenterZ=0 NormalX=0 NormalY=0 NormalZ=1 AngleXU=0 Radius=1
    g24: BSplineCurve PolesCount=3 KnotsCount=2 Degree=2 IsPeriodic=0
    g25: GeomPoint X=-6.48644 Y=-5.99526 Z=0
    g26: GeomPoint X=-6.77343 Y=-8 Z=0
    g27: Circle CenterX=-7.19003 CenterY=-10 CenterZ=0 NormalX=0 NormalY=0 NormalZ=1 AngleXU=0 Radius=1
    g28: Circle CenterX=-7.44407 CenterY=-11.0915 CenterZ=0 NormalX=0 NormalY=0 NormalZ=1 AngleXU=0 Radius=1
    g29: Circle CenterX=-7.79258 CenterY=-12 CenterZ=0 NormalX=0 NormalY=0 NormalZ=1 AngleXU=0 Radius=1
    g30: BSplineCurve PolesCount=3 KnotsCount=2 Degree=2 IsPeriodic=0
    g31: GeomPoint X=-7.19003 Y=-10 Z=0
    g32: GeomPoint X=-7.79258 Y=-12 Z=0
    g33: Circle CenterX=-8.70761 CenterY=-14 CenterZ=0 NormalX=0 NormalY=0 NormalZ=1 AngleXU=0 Radius=1
    g34: Circle CenterX=-9.33087 CenterY=-15.1837 CenterZ=0 NormalX=0 NormalY=0 NormalZ=1 AngleXU=0 Radius=1
    g35: Circle CenterX=-10.1571 CenterY=-16 CenterZ=0 NormalX=0 NormalY=0 NormalZ=1 AngleXU=0 Radius=1
    g36: BSplineCurve PolesCount=3 KnotsCount=2 Degree=2 IsPeriodic=0
    g37: GeomPoint X=-8.70761 Y=-14 Z=0
    g38: GeomPoint X=-10.1571 Y=-16 Z=0
    g39: Circle CenterX=-12.8401 CenterY=-17.6958 CenterZ=0 NormalX=0 NormalY=0 NormalZ=1 AngleXU=0 Radius=1
    g40: Circle CenterX=-13.3521 CenterY=-17.9027 CenterZ=0 NormalX=0 NormalY=0 NormalZ=1 AngleXU=0 Radius=1
    g41: Circle CenterX=-14 CenterY=-18 CenterZ=0 NormalX=0 NormalY=0 NormalZ=1 AngleXU=0 Radius=1
    g42: BSplineCurve PolesCount=3 KnotsCount=2 Degree=2 IsPeriodic=0
    g43: GeomPoint X=-12.8401 Y=-17.6958 Z=0
    g44: GeomPoint X=-14 Y=-18 Z=0
    g45: LineSegment StartX=-6.2 StartY=0 StartZ=0 EndX=-7.2 EndY=0 EndZ=0
    g46: LineSegment StartX=-7.2 StartY=0 StartZ=0 EndX=-7.2 EndY=-2 EndZ=0
    g47: LineSegment StartX=-7.2 StartY=-2 StartZ=0 EndX=-6.2215 EndY=-2 EndZ=0
    g48: LineSegment StartX=-6.32538 StartY=-4 StartZ=0 EndX=-7.65538 EndY=-4 EndZ=0
    g49: LineSegment StartX=-7.65538 StartY=-4 StartZ=0 EndX=-7.65538 EndY=-5.99526 EndZ=0
    g50: LineSegment StartX=-7.65538 StartY=-5.99526 StartZ=0 EndX=-6.48644 EndY=-5.99526 EndZ=0
    g51: LineSegment StartX=-6.77343 StartY=-8 StartZ=0 EndX=-8.43343 EndY=-8 EndZ=0
    g52: LineSegment StartX=-8.43343 StartY=-8 StartZ=0 EndX=-8.43343 EndY=-10 EndZ=0
    g53: LineSegment StartX=-8.43343 StartY=-10 StartZ=0 EndX=-7.19003 EndY=-10 EndZ=0
  constraints (112):
    c: Horizontal(g0)
    c: Distance(g0) = 2
    c: Block(g0)
    c: Vertical(g1)
    c: Coincident(g2,g0)
    c: Vertical(g2)
    c: Block(g2)
    c: Coincident(g6,g2)
    c: Weight(g3) = 1
    c: Equal(g3,g4)
    c: Equal(g3,g5)
    c: InternalAlignment(g3,g6)
    c: InternalAlignment(g4,g6)
    c: InternalAlignment(g5,g6)
    c: InternalAlignment(g7,g6)
    c: InternalAlignment(g8,g6)
    c: Block(g6)
    c: Coincident(g9,g1)
    c: Coincident(g9,g6)
    c: Horizontal(g9)
    c: Vertical(g10)
    c: Block(g10)
    c: Horizontal(g11)
    c: Block(g11)
    c: Coincident(g12,g10)
    c: Horizontal(g12)
    c: Block(g12)
    c: Coincident(g13,g11)
    c: Vertical(g13)
    c: Block(g13)
    c: Coincident(g14,g10)
    c: Horizontal(g14)
    c: Block(g14)
    c: Block(g9)
    c: Block(g1)
    c: Weight(g15) = 1
    c: Equal(g15,g16)
    c: Equal(g15,g17)
    c: InternalAlignment(g15,g18)
    c: InternalAlignment(g16,g18)
    c: InternalAlignment(g17,g18)
    c: InternalAlignment(g19,g18)
    c: InternalAlignment(g20,g18)
    c: Weight(g21) = 1
    c: Equal(g21,g22)
    c: Equal(g21,g23)
    c: InternalAlignment(g21,g24)
    c: InternalAlignment(g22,g24)
    c: InternalAlignment(g23,g24)
    c: InternalAlignment(g25,g24)
    c: InternalAlignment(g26,g24)
    c: Weight(g27) = 1
    c: Equal(g27,g28)
    c: Equal(g27,g29)
    c: Coincident(g30,g14)
    c: InternalAlignment(g27,g30)
    c: InternalAlignment(g28,g30)
    c: InternalAlignment(g29,g30)
    c: InternalAlignment(g31,g30)
    c: InternalAlignment(g32,g30)
    c: Coincident(g36,g12)
    c: Weight(g33) = 1
    c: Equal(g33,g34)
    c: Equal(g33,g35)
    c: Coincident(g36,g11)
    c: InternalAlignment(g33,g36)
    c: InternalAlignment(g34,g36)
    c: InternalAlignment(g35,g36)
    c: InternalAlignment(g37,g36)
    c: InternalAlignment(g38,g36)
    c: Coincident(g42,g13)
    c: Weight(g39) = 1
    c: Equal(g39,g40)
    c: Equal(g39,g41)
    c: Coincident(g42,g1)
    c: InternalAlignment(g39,g42)
    c: InternalAlignment(g40,g42)
    c: InternalAlignment(g41,g42)
    c: InternalAlignment(g43,g42)
    c: InternalAlignment(g44,g42)
    c: Block(g18)
    c: Block(g24)
    c: Block(g30)
    c: Block(g36)
    c: Block(g42)
    c: Horizontal(g45)
    c: Coincident(g45,g0)
    c: Vertical(g46)
    c: Coincident(g46,g45)
    c: Coincident(g47,g46)
    c: Coincident(g47,g18)
    c: Horizontal(g47)
    c: Block(g46)
    c: Coincident(g48,g18)
    c: Horizontal(g48)
    c: Distance(g48) = 1.33
    c: Vertical(g49)
    c: Coincident(g49,g48)
    c: Coincident(g50,g49)
    c: Coincident(g50,g24)
    c: Horizontal(g50)
    c: Tangent(g50,g22)
    c: Horizontal(g51)
    c: Coincident(g51,g24)
    c: Block(g51)
    c: Vertical(g52)
    c: Block(g52)
    c: Coincident(g52,g51)
    c: Coincident(g53,g52)
    c: Coincident(g53,g30)
    c: Horizontal(g53)
    c: Distance(g1) = 8.5
FEATURE [Part::Feature] Face024
  shape: bbox 9.8 x 26.5 x 2e-07 mm, 1 faces, 0 solids (baked)
FEATURE [Part::Revolution] Revolve024
  Angle = 360
  Axis = (0,1,0)
  Base = (0,0,0)
  FaceMakerClass = Part::FaceMakerBullseye
  Placement = pos=(0,0,0) rot=(0,0,1;1.5708rad)
  Solid = false
  Source = -> Face024
  Symmetric = false
FEATURE [Part::Feature] Face025
  shape: bbox 9.8 x 26.5 x 2e-07 mm, 1 faces, 0 solids (baked)
FEATURE [Part::Revolution] Revolve025
  Angle = 360
  Axis = (0,1,0)
  Base = (0,0,0)
  FaceMakerClass = Part::FaceMakerBullseye
  Placement = pos=(0,0,0) rot=(0,0,1;1.5708rad)
  Solid = false
  Source = -> Face025
  Symmetric = false
FEATURE [Part::MultiFuse] Fusion033
  Placement = pos=(-18,19,36) rot=(0,0,1;0rad)
  Shapes = -> [Revolve025,Revolve024]
FEATURE [Part::Cylinder] Cylinder014
  Angle = 360
  AttacherType = Attacher::AttachEngine3D
  Height = 20
  Placement = pos=(0,0,36.15) rot=(0,0,1;0rad)
  Radius = 14.3
FEATURE [Part::Cylinder] Cylinder015
  Angle = 360
  AttacherType = Attacher::AttachEngine3D
  Height = 10
  Placement = pos=(0,0,36.15) rot=(0,0,1;0rad)
  Radius = 4
FEATURE [Part::MultiFuse] Fusion034  label="removeToCreteHoleForPlugHousing004"
  Placement = pos=(-42,19,36) rot=(0,1,0;1.5708rad)
  Shapes = -> [Cylinder014,Cylinder015]
FEATURE [Part::Cut] Cut008  label="top004"
  Base = -> Cut004
  Placement = pos=(-1,0,0) rot=(0,0,1;0rad)
  Tool = -> Fusion034
FEATURE [Part::Box] Box005  label="Cube005"
  AttacherType = Attacher::AttachEngine3D
  Height = 28
  Length = 3
  Placement = pos=(110.7,19,22) rot=(0,0,1;0rad)
  Width = 15.7
FEATURE [Part::Cylinder] Cylinder016
  Angle = 360
  AttacherType = Attacher::AttachEngine3D
  Height = 10
  Placement = pos=(0,0,36.15) rot=(0,0,1;0rad)
  Radius = 4
FEATURE [Part::Cylinder] Cylinder017
  Angle = 360
  AttacherType = Attacher::AttachEngine3D
  Height = 20
  Placement = pos=(0,0,36.15) rot=(0,0,1;0rad)
  Radius = 10.3
FEATURE [Part::MultiFuse] Fusion035  label="removeToCreteHoleForPlugHousing005"
  Placement = pos=(70,19,36) rot=(0,1,0;1.5708rad)
  Shapes = -> [Cylinder017,Cylinder016]
FEATURE [Part::Cut] Cut009  label="plugHousingTab001"
  Base = -> Box005
  Placement = pos=(-107.4,-14,0) rot=(0,0,1;0rad)
  Tool = -> Fusion035
FEATURE [Part::Box] Box006  label="Cube006"
  AttacherType = Attacher::AttachEngine3D
  Height = 28
  Length = 3
  Placement = pos=(110.7,19,22) rot=(0,0,1;0rad)
  Width = 15.7
FEATURE [Part::Cylinder] Cylinder018
  Angle = 360
  AttacherType = Attacher::AttachEngine3D
  Height = 10
  Placement = pos=(0,0,36.15) rot=(0,0,1;0rad)
  Radius = 4
FEATURE [Part::Cylinder] Cylinder019
  Angle = 360
  AttacherType = Attacher::AttachEngine3D
  Height = 20
  Placement = pos=(0,0,36.15) rot=(0,0,1;0rad)
  Radius = 10.3
FEATURE [Part::MultiFuse] Fusion036  label="removeToCreteHoleForPlugHousing006"
  Placement = pos=(70,19,36) rot=(0,1,0;1.5708rad)
  Shapes = -> [Cylinder019,Cylinder018]
FEATURE [Part::Cut] Cut010  label="plugHousingTab002"
  Base = -> Box006
  Placement = pos=(-107.4,-14,0) rot=(0,0,1;0rad)
  Tool = -> Fusion036
FEATURE [Part::MultiFuse] Fusion037
  Placement = pos=(9.6,23,0) rot=(0,0,1;3.14159rad)
  Shapes = -> [Cut009,Cut010]
FEATURE [Part::Box] Box  label="Cube"
  AttacherType = Attacher::AttachEngine3D
  Height = 10
  Length = 3
  Placement = pos=(3.3,4,12) rot=(0,0,1;0rad)
  Width = 10
FEATURE [Part::Fillet] Fillet004
  Base = -> Fusion028
  Edges = 1 edges r=2: [Edge25]
FEATURE [Part::Fillet] Fillet005  label="plugHousing046"
  Base = -> Fillet004
  Edges = 1 edges r=2: [Edge8]
FEATURE [Part::Fillet] Fillet006
  Base = -> Box
  Edges = 1 edges r=2: [Edge11]
FEATURE [Part::Box] Box007  label="Cube007"
  AttacherType = Attacher::AttachEngine3D
  Height = 10
  Length = 3
  Placement = pos=(3.3,4,50) rot=(0,0,1;0rad)
  Width = 10
FEATURE [Part::Fillet] Fillet007
  Base = -> Box007
  Edges = 1 edges r=2: [Edge12]
FEATURE [Part::Box] Box008  label="Cube008"
  AttacherType = Attacher::AttachEngine3D
  Height = 28
  Length = 4
  Placement = pos=(5,0,22) rot=(0,0,1;0rad)
  Width = 10
FEATURE [Part::Fillet] Fillet008
  Base = -> Box008
  Edges = 1 edges r=1: [Edge7]
FEATURE [Part::Fillet] Fillet009
  Base = -> Fillet008
  Edges = 1 edges r=2: [Edge5]
FEATURE [Part::Fillet] Fillet010
  Base = -> Fillet009
  Edges = 1 edges r=2: [Edge2]
FEATURE [Sketcher::SketchObject] Sketch009  label="topSketch003"
  FullyConstrained = true
  sketch-geometry (4):
    g0: LineSegment StartX=16.8446 StartY=31.512 StartZ=0 EndX=16.3251 EndY=34.4666 EndZ=0
    g1: ArcOfCircle CenterX=19 CenterY=19.2524 CenterZ=0 NormalX=0 NormalY=0 NormalZ=1 AngleXU=0 Radius=15.4476 StartAngle=1.74483 EndAngle=2.72717
    g2: ArcOfCircle CenterX=19 CenterY=19.2524 CenterZ=0 NormalX=0 NormalY=0 NormalZ=1 AngleXU=0 Radius=12.4476 StartAngle=1.74483 EndAngle=2.73189
    g3: LineSegment StartX=4.86004 StartY=25.4725 StartZ=0 EndX=7.58253 EndY=24.2107 EndZ=0
  constraints (7):
    c: Block(g0)
    c: Coincident(g1,g0)
    c: Coincident(g2,g0)
    c: Coincident(g3,g1)
    c: Coincident(g3,g2)
    c: Block(g1)
    c: Block(g2)
FEATURE [Part::Extrusion] Extrude008
  Base = -> Sketch009
  Dir = (0,0,1)
  DirMode = 2
  FaceMakerClass = Part::FaceMakerBullseye
  LengthFwd = 10
  LengthRev = 0
  Placement = pos=(0,0,31) rot=(0,0,1;0rad)
  Solid = true
  Symmetric = false
FEATURE [Part::Cylinder] Cylinder020
  Angle = 360
  AttacherType = Attacher::AttachEngine3D
  Height = 20
  Placement = pos=(0,0,36.15) rot=(0,0,1;0rad)
  Radius = 8.2
FEATURE [Part::Cylinder] Cylinder021
  Angle = 360
  AttacherType = Attacher::AttachEngine3D
  Height = 10
  Placement = pos=(0,0,36.15) rot=(0,0,1;0rad)
  Radius = 4
FEATURE [Part::MultiFuse] Fusion038  label="removeToCreteHoleForPlugHousing007"
  Placement = pos=(-42,19,36) rot=(0,1,0;1.5708rad)
  Shapes = -> [Cylinder020,Cylinder021]
FEATURE [Part::Cut] Cut011
  Base = -> Extrude008
  Tool = -> Fusion038
FEATURE [Part::Fillet] Fillet011
  Base = -> Cut011
  Edges = 1 edges r=2: [Edge1]
FEATURE [Part::Fillet] Fillet012
  Base = -> Fillet011
  Edges = 1 edges r=2.5: [Edge1]
FEATURE [Part::Fillet] Fillet013
  Base = -> Fillet012
  Edges = 1 edges r=2.5: [Edge2]
FEATURE [Part::Box] Box010  label="Cube010"
  AttacherType = Attacher::AttachEngine3D
  Height = 16
  Length = 8
  Placement = pos=(12.7,31.52,28) rot=(0,0,1;0rad)
  Width = 4
FEATURE [Sketcher::SketchObject] Sketch010  label="topSketch004"
  FullyConstrained = true
  sketch-geometry (4):
    g0: LineSegment StartX=16.8446 StartY=31.512 StartZ=0 EndX=16.3251 EndY=34.4666 EndZ=0
    g1: ArcOfCircle CenterX=19 CenterY=19.2524 CenterZ=0 NormalX=0 NormalY=0 NormalZ=1 AngleXU=0 Radius=15.4476 StartAngle=1.74483 EndAngle=2.72717
    g2: ArcOfCircle CenterX=19 CenterY=19.2524 CenterZ=0 NormalX=0 NormalY=0 NormalZ=1 AngleXU=0 Radius=12.4476 StartAngle=1.74483 EndAngle=2.73189
    g3: LineSegment StartX=4.86004 StartY=25.4725 StartZ=0 EndX=7.58253 EndY=24.2107 EndZ=0
  constraints (7):
    c: Block(g0)
    c: Coincident(g1,g0)
    c: Coincident(g2,g0)
    c: Coincident(g3,g1)
    c: Coincident(g3,g2)
    c: Block(g1)
    c: Block(g2)
FEATURE [Part::Cylinder] Cylinder022
  Angle = 360
  AttacherType = Attacher::AttachEngine3D
  Height = 10
  Placement = pos=(0,0,36.15) rot=(0,0,1;0rad)
  Radius = 4
FEATURE [Sketcher::SketchObject] Sketch011  label="topSketch005"
  FullyConstrained = true
  sketch-geometry (4):
    g0: LineSegment StartX=16.8446 StartY=31.512 StartZ=0 EndX=16.3251 EndY=34.4666 EndZ=0
    g1: ArcOfCircle CenterX=19 CenterY=19.2524 CenterZ=0 NormalX=0 NormalY=0 NormalZ=1 AngleXU=0 Radius=15.4476 StartAngle=1.74483 EndAngle=2.72717
    g2: ArcOfCircle CenterX=19 CenterY=19.2524 CenterZ=0 NormalX=0 NormalY=0 NormalZ=1 AngleXU=0 Radius=12.4476 StartAngle=1.74483 EndAngle=2.73189
    g3: LineSegment StartX=4.86004 StartY=25.4725 StartZ=0 EndX=7.58253 EndY=24.2107 EndZ=0
  constraints (7):
    c: Block(g0)
    c: Coincident(g1,g0)
    c: Coincident(g2,g0)
    c: Coincident(g3,g1)
    c: Coincident(g3,g2)
    c: Block(g1)
    c: Block(g2)
FEATURE [Part::Extrusion] Extrude010
  Base = -> Sketch011
  Dir = (0,0,1)
  DirMode = 2
  FaceMakerClass = Part::FaceMakerBullseye
  LengthFwd = 10.6
  LengthRev = 0
  Placement = pos=(0,0,31) rot=(0,0,1;0rad)
  Solid = true
  Symmetric = false
FEATURE [Part::Cylinder] Cylinder023
  Angle = 360
  AttacherType = Attacher::AttachEngine3D
  Height = 20
  Placement = pos=(0,0,36.15) rot=(0,0,1;0rad)
  Radius = 8.2
FEATURE [Part::MultiFuse] Fusion039  label="removeToCreteHoleForPlugHousing008"
  Placement = pos=(-42,19,36) rot=(0,1,0;1.5708rad)
  Shapes = -> [Cylinder023,Cylinder022]
FEATURE [Part::Cut] Cut012
  Base = -> Extrude010
  Placement = pos=(0,0,-0.3) rot=(0,0,1;0rad)
  Tool = -> Fusion039
FEATURE [Part::Cut] Cut013
  Base = -> Box010
  Tool = -> Cut012
FEATURE [Part::Fillet] Fillet014
  Base = -> Cut013
  Edges = 1 edges r=0.7: [Edge13]
FEATURE [Part::Fillet] Fillet015
  Base = -> Fillet014
  Edges = 1 edges r=0.7: [Edge13]
FEATURE [Part::Fillet] Fillet016
  Base = -> Fillet015
  Edges = 1 edges r=0.7: [Edge16]
FEATURE [Part::Fillet] Fillet017
  Base = -> Fillet016
  Edges = 1 edges r=0.7: [Edge11]
FEATURE [Part::Fillet] Fillet018
  Base = -> Fillet017
  Edges = 1 edges r=0.7: [Edge10]
FEATURE [Part::Fillet] Fillet019
  Base = -> Fillet018
  Edges = 1 edges r=1.2: [Edge5]
FEATURE [Part::Fillet] Fillet020
  Base = -> Fillet019
  Edges = 1 edges r=1.2: [Edge12]
FEATURE [Part::Fillet] Fillet021
  Base = -> Fillet020
  Edges = 1 edges r=2: [Edge1]
  Placement = pos=(0.3,0,0) rot=(0,0,1;0rad)
FEATURE [Part::MultiFuse] Fusion040  label="top005"
  Shapes = -> [Cut008,Fillet021]
FEATURE [Part::MultiFuse] Fusion041  label="wireHolder"
  Shapes = -> [Fusion033,Fillet013]
FEATURE [Part::MultiFuse] Fusion042
  Shapes = -> [Fillet007,Fusion041]
FEATURE [Part::MultiFuse] Fusion043  label="wireHolder001"
  Shapes = -> [Fusion042,Fillet010]
FEATURE [Part::MultiFuse] Fusion044  label="wireHolder002"
  Shapes = -> [Fillet006,Fusion037,Fusion043]
FEATURE [Part::Feature] Face026
  shape: bbox 11 x 6 x 2e-07 mm, 1 faces, 0 solids (baked)
FEATURE [Part::Revolution] Revolve026
  Angle = 360
  Axis = (0,1,0)
  Base = (0,0,0)
  FaceMakerClass = Part::FaceMakerBullseye
  Placement = pos=(30.3,-1,19.7) rot=(0,0,1;0rad)
  Solid = false
  Source = -> Face026
  Symmetric = false
FEATURE [Sketcher::SketchObject] Sketch013  label="topSketch006"
  FullyConstrained = true
  sketch-geometry (13):
    g0: LineSegment StartX=117 StartY=19 StartZ=0 EndX=117 EndY=38 EndZ=0
    g1: ArcOfCircle CenterX=98 CenterY=19 CenterZ=0 NormalX=0 NormalY=0 NormalZ=1 AngleXU=0 Radius=19 StartAngle=5.7297 EndAngle=6.28319
    g2: LineSegment StartX=0 StartY=3 StartZ=0 EndX=0 EndY=19 EndZ=0
    g3: LineSegment StartX=19 StartY=38 StartZ=0 EndX=117 EndY=38 EndZ=0
    g4: ArcOfCircle CenterX=19 CenterY=19 CenterZ=0 NormalX=0 NormalY=0 NormalZ=1 AngleXU=0 Radius=19 StartAngle=1.5708 EndAngle=3.14159
    g5: ArcOfCircle CenterX=19 CenterY=19 CenterZ=0 NormalX=0 NormalY=0 NormalZ=1 AngleXU=0 Radius=16 StartAngle=1.5708 EndAngle=3.14159
    g6: ArcOfCircle CenterX=98 CenterY=19 CenterZ=0 NormalX=0 NormalY=0 NormalZ=1 AngleXU=0 Radius=16 StartAngle=5.60905 EndAngle=6.28319
    g7: LineSegment StartX=114 StartY=19 StartZ=0 EndX=114 EndY=35 EndZ=0
    g8: LineSegment StartX=110.5 StartY=9.01251 StartZ=0 EndX=114.163 EndY=9.01251 EndZ=0
    g9: LineSegment StartX=114 StartY=35 StartZ=0 EndX=19 EndY=35 EndZ=0
    g10: LineSegment StartX=0 StartY=3 StartZ=0 EndX=0 EndY=0 EndZ=0
    g11: LineSegment StartX=3 StartY=0 StartZ=0 EndX=0 EndY=0 EndZ=0
    g12: LineSegment StartX=3 StartY=19 StartZ=0 EndX=3 EndY=0 EndZ=0
  constraints (33):
    c: Vertical(g0)
    c: Distance(g0) = 19
    c: Block(g0)
    c: Coincident(g1,g0)
    c: Block(g1)
    c: Vertical(g2)
    c: Block(g2)
    c: Coincident(g3,g0)
    c: Horizontal(g3)
    c: Distance(g3) = 98
    c: Coincident(g4,g3)
    c: Coincident(g4,g2)
    c: Block(g4)
    c: Coincident(g5,g4)
    c: Coincident(g6,g1)
    c: Block(g6)
    c: Block(g5)
    c: Coincident(g7,g6)
    c: Vertical(g7)
    c: Coincident(g8,g6)
    c: Coincident(g8,g1)
    c: Coincident(g9,g7)
    c: Coincident(g9,g5)
    c: Horizontal(g9)
    c: Tangent(g9,g5)
    c: Coincident(g10,g2)
    c: Distance(g10) = 3
    c: Vertical(g10)
    c: Coincident(g11,g10)
    c: Horizontal(g11)
    c: Coincident(g12,g5)
    c: Coincident(g12,g11)
    c: Vertical(g12)
FEATURE [Part::Extrusion] Extrude011  label="top006"
  Base = -> Sketch013
  Dir = (0,0,1)
  DirMode = 2
  FaceMakerClass = Part::FaceMakerBullseye
  LengthFwd = 72
  LengthRev = 0
  Solid = true
  Symmetric = false
FEATURE [Sketcher::SketchObject] Sketch014
  FullyConstrained = true
  MapMode = 3
  Placement = pos=(0,0,0) rot=(1,0,0;1.5708rad)
  Support = -> [Extrude011]
  sketch-geometry (8):
    g0: Circle CenterX=80.351 CenterY=-67.6202 CenterZ=0 NormalX=0 NormalY=0 NormalZ=1 AngleXU=0 Radius=2
    g1: Circle CenterX=80.351 CenterY=-67.6202 CenterZ=0 NormalX=0 NormalY=0 NormalZ=1 AngleXU=0 Radius=3
    g2: Circle CenterX=80.351 CenterY=-4.92017 CenterZ=0 NormalX=0 NormalY=0 NormalZ=1 AngleXU=0 Radius=2
    g3: Circle CenterX=80.351 CenterY=-4.92017 CenterZ=0 NormalX=0 NormalY=0 NormalZ=1 AngleXU=0 Radius=3
    g4: Circle CenterX=23.851 CenterY=-4.92017 CenterZ=0 NormalX=0 NormalY=0 NormalZ=1 AngleXU=0 Radius=2
    g5: Circle CenterX=23.851 CenterY=-4.92017 CenterZ=0 NormalX=0 NormalY=0 NormalZ=1 AngleXU=0 Radius=3
    g6: Circle CenterX=23.851 CenterY=-67.6202 CenterZ=0 NormalX=0 NormalY=0 NormalZ=1 AngleXU=0 Radius=2
    g7: Circle CenterX=23.851 CenterY=-67.6202 CenterZ=0 NormalX=0 NormalY=0 NormalZ=1 AngleXU=0 Radius=3
  constraints (8):
    c: Block(g3)
    c: Block(g2)
    c: Block(g1)
    c: Block(g0)
    c: Block(g6)
    c: Block(g7)
    c: Block(g4)
    c: Block(g5)
FEATURE [Part::Feature] Face027
  shape: bbox 11 x 6 x 2e-07 mm, 1 faces, 0 solids (baked)
FEATURE [Part::Revolution] Revolve027
  Angle = 360
  Axis = (0,1,0)
  Base = (0,0,0)
  FaceMakerClass = Part::FaceMakerBullseye
  Placement = pos=(30.3,-1,51.7) rot=(0,0,1;0rad)
  Solid = false
  Source = -> Face027
  Symmetric = false
FEATURE [Part::Feature] Face028
  shape: bbox 11 x 6 x 2e-07 mm, 1 faces, 0 solids (baked)
FEATURE [Part::Revolution] Revolve028
  Angle = 360
  Axis = (0,1,0)
  Base = (0,0,0)
  FaceMakerClass = Part::FaceMakerBullseye
  Placement = pos=(62.3,-1,19.7) rot=(0,0,1;0rad)
  Solid = false
  Source = -> Face028
  Symmetric = false
FEATURE [Part::Feature] Face029
  shape: bbox 11 x 6 x 2e-07 mm, 1 faces, 0 solids (baked)
FEATURE [Part::Revolution] Revolve029
  Angle = 360
  Axis = (0,1,0)
  Base = (0,0,0)
  FaceMakerClass = Part::FaceMakerBullseye
  Placement = pos=(62.3,-1,51.7) rot=(0,0,1;0rad)
  Solid = false
  Source = -> Face029
  Symmetric = false
FEATURE [Part::Feature] Wire
  shape: bbox 11 x 5.2 x 2e-07 mm, 0 faces, 0 solids (baked)
FEATURE [Part::Revolution] Revolve030
  Angle = 360
  Axis = (0,1,0)
  Base = (0,0,0)
  FaceMakerClass = Part::FaceMakerBullseye
  Placement = pos=(30.3,38,19.7) rot=(0,0,1;0rad)
  Solid = true
  Source = -> Wire
  Symmetric = false
FEATURE [Part::Feature] Wire001
  shape: bbox 11 x 5.2 x 2e-07 mm, 0 faces, 0 solids (baked)
FEATURE [Part::Revolution] Revolve031
  Angle = 360
  Axis = (0,1,0)
  Base = (0,0,0)
  FaceMakerClass = Part::FaceMakerBullseye
  Placement = pos=(30.3,38,51.7) rot=(0,0,1;0rad)
  Solid = true
  Source = -> Wire001
  Symmetric = false
FEATURE [Part::Feature] Wire002
  shape: bbox 11 x 5.2 x 2e-07 mm, 0 faces, 0 solids (baked)
FEATURE [Part::Revolution] Revolve032
  Angle = 360
  Axis = (0,1,0)
  Base = (0,0,0)
  FaceMakerClass = Part::FaceMakerBullseye
  Placement = pos=(62.3,38,51.7) rot=(0,0,1;0rad)
  Solid = true
  Source = -> Wire002
  Symmetric = false
FEATURE [Part::Feature] Wire003
  shape: bbox 11 x 5.2 x 2e-07 mm, 0 faces, 0 solids (baked)
FEATURE [Part::Revolution] Revolve033
  Angle = 360
  Axis = (0,1,0)
  Base = (0,0,0)
  FaceMakerClass = Part::FaceMakerBullseye
  Placement = pos=(62.3,38,19.7) rot=(0,0,1;0rad)
  Solid = true
  Source = -> Wire003
  Symmetric = false
FEATURE [Part::MultiFuse] Fusion045  label="altRandScrewHousing"
  Shapes = -> [Revolve029,Revolve027,Revolve028,Revolve026]
FEATURE [Part::MultiFuse] Fusion046  label="fanScrewHousing"
  Shapes = -> [Revolve033,Revolve032,Revolve031,Revolve030]
FEATURE [Sketcher::SketchObject] Sketch015
  FullyConstrained = true
  sketch-geometry (17):
    g0: Circle CenterX=-3.5 CenterY=23.5 CenterZ=0 NormalX=0 NormalY=0 NormalZ=1 AngleXU=0 Radius=1
    g1: Circle CenterX=-1 CenterY=15.25 CenterZ=0 NormalX=0 NormalY=0 NormalZ=1 AngleXU=0 Radius=1
    g2: Circle CenterX=-3.5 CenterY=7 CenterZ=0 NormalX=0 NormalY=0 NormalZ=1 AngleXU=0 Radius=1
    g3: BSplineCurve PolesCount=3 KnotsCount=2 Degree=2 IsPeriodic=0
    g4: GeomPoint X=-3.5 Y=23.5 Z=0
    g5: GeomPoint X=-3.5 Y=7 Z=0
    g6: Circle CenterX=-4.8 CenterY=30.5 CenterZ=0 NormalX=0 NormalY=0 NormalZ=1 AngleXU=0 Radius=1
    g7: Circle CenterX=-3.5 CenterY=30.5 CenterZ=0 NormalX=0 NormalY=0 NormalZ=1 AngleXU=0 Radius=1
    g8: Circle CenterX=-3.5 CenterY=29.2 CenterZ=0 NormalX=0 NormalY=0 NormalZ=1 AngleXU=0 Radius=1
    g9: BSplineCurve PolesCount=3 KnotsCount=2 Degree=2 IsPeriodic=0
    g10: GeomPoint X=-4.8 Y=30.5 Z=0
    g11: GeomPoint X=-3.5 Y=29.2 Z=0
    g12: LineSegment StartX=-3.5 StartY=29.2 StartZ=0 EndX=-3.5 EndY=23.5 EndZ=0
    g13: LineSegment StartX=-4.8 StartY=30.5 StartZ=0 EndX=0 EndY=30.5 EndZ=0
    g14: LineSegment StartX=-3.5 StartY=0.3 StartZ=0 EndX=0 EndY=0.3 EndZ=0
    g15: LineSegment StartX=-3.5 StartY=0.3 StartZ=0 EndX=-3.5 EndY=7 EndZ=0
    g16: LineSegment StartX=0 StartY=0.3 StartZ=0 EndX=0 EndY=30.5 EndZ=0
  constraints (33):
    c: Weight(g0) = 1
    c: Equal(g0,g1)
    c: Equal(g0,g2)
    c: InternalAlignment(g0,g3)
    c: InternalAlignment(g1,g3)
    c: InternalAlignment(g2,g3)
    c: InternalAlignment(g4,g3)
    c: InternalAlignment(g5,g3)
    c: Block(g3)
    c: Weight(g6) = 1
    c: Equal(g6,g7)
    c: Equal(g6,g8)
    c: InternalAlignment(g6,g9)
    c: InternalAlignment(g7,g9)
    c: InternalAlignment(g8,g9)
    c: InternalAlignment(g10,g9)
    c: InternalAlignment(g11,g9)
    c: Block(g9)
    c: Coincident(g12,g9)
    c: Coincident(g12,g3)
    c: Vertical(g12)
    c: Coincident(g13,g9)
    c: Horizontal(g13)
    c: Distance(g13) = 4.8
    c: Horizontal(g14)
    c: Block(g14)
    c: Coincident(g15,g14)
    c: Coincident(g15,g3)
    c: Vertical(g15)
    c: Coincident(g16,g14)
    c: Coincident(g16,g13)
    c: Vertical(g16)
    c: Tangent(g16,g1)
FEATURE [Sketcher::SketchObject] Sketch016
  FullyConstrained = true
  sketch-geometry (16):
    g0: Circle CenterX=-3.5 CenterY=23.5 CenterZ=0 NormalX=0 NormalY=0 NormalZ=1 AngleXU=0 Radius=1
    g1: Circle CenterX=-1 CenterY=15.25 CenterZ=0 NormalX=0 NormalY=0 NormalZ=1 AngleXU=0 Radius=1
    g2: Circle CenterX=-3.5 CenterY=7 CenterZ=0 NormalX=0 NormalY=0 NormalZ=1 AngleXU=0 Radius=1
    g3: BSplineCurve PolesCount=3 KnotsCount=2 Degree=2 IsPeriodic=0
    g4: GeomPoint X=-3.5 Y=23.5 Z=0
    g5: GeomPoint X=-3.5 Y=7 Z=0
    g6: LineSegment StartX=-3.5 StartY=28.2 StartZ=0 EndX=-3.5 EndY=23.5 EndZ=0
    g7: LineSegment StartX=0 StartY=29.5 StartZ=0 EndX=0 EndY=30 EndZ=0
    g8: LineSegment StartX=-3.5 StartY=28.2 StartZ=0 EndX=-3.5 EndY=30 EndZ=0
    g9: LineSegment StartX=0 StartY=30 StartZ=0 EndX=0 EndY=30.5 EndZ=0
    g10: LineSegment StartX=0 StartY=30.5 StartZ=0 EndX=-3.5 EndY=30.5 EndZ=0
    g11: LineSegment StartX=-3.5 StartY=30.5 StartZ=0 EndX=-3.5 EndY=30 EndZ=0
    g12: LineSegment StartX=0 StartY=29.5 StartZ=0 EndX=0 EndY=5 EndZ=0
    g13: LineSegment StartX=-3.5 StartY=0.3 StartZ=0 EndX=-3.5 EndY=7 EndZ=0
    g14: LineSegment StartX=-3.5 StartY=0.3 StartZ=0 EndX=0 EndY=0.3 EndZ=0
    g15: LineSegment StartX=0 StartY=5 StartZ=0 EndX=0 EndY=0.3 EndZ=0
  constraints (39):
    c: Weight(g0) = 1
    c: Equal(g0,g1)
    c: Equal(g0,g2)
    c: InternalAlignment(g0,g3)
    c: InternalAlignment(g1,g3)
    c: InternalAlignment(g2,g3)
    c: InternalAlignment(g4,g3)
    c: InternalAlignment(g5,g3)
    c: Block(g3)
    c: Coincident(g6,g3)
    c: Vertical(g6)
    c: Vertical(g7)
    c: Distance(g7) = 0.5
    c: Coincident(g8,g6)
    c: Vertical(g8)
    c: Block(g6)
    c: Block(g7)
    c: Vertical(g9)
    c: Equal(g7,g9) = 0.5
    c: Block(g9)
    c: Coincident(g9,g7)
    c: Horizontal(g10)
    c: Coincident(g10,g9)
    c: Coincident(g11,g10)
    c: Coincident(g11,g8)
    c: Vertical(g11)
    c: Block(g11)
    c: Coincident(g12,g7)
    c: Vertical(g12)
    c: Coincident(g13,g3)
    c: Vertical(g13)
    c: Distance(g13) = 6.7
    c: Coincident(g14,g13)
    c: Horizontal(g14)
    c: Block(g14)
    c: Coincident(g15,g12)
    c: Coincident(g15,g14)
    c: Vertical(g15)
    c: Block(g15)
FEATURE [Sketcher::SketchObject] Sketch017
  FullyConstrained = true
  sketch-geometry (11):
    g0: LineSegment StartX=-3.5 StartY=1e-16 StartZ=0 EndX=-1.6 EndY=1e-16 EndZ=0
    g1: LineSegment StartX=-1.6 StartY=1e-16 StartZ=0 EndX=-1.6 EndY=1.5 EndZ=0
    g2: LineSegment StartX=-3.5 StartY=1.5 StartZ=0 EndX=-1.6 EndY=1.5 EndZ=0
    g3: LineSegment StartX=-3.5 StartY=1e-16 StartZ=0 EndX=-4.8 EndY=1e-16 EndZ=0
    g4: Circle CenterX=-3.5 CenterY=1.3 CenterZ=0 NormalX=0 NormalY=0 NormalZ=1 AngleXU=0 Radius=1
    g5: Circle CenterX=-3.5 CenterY=1e-16 CenterZ=0 NormalX=0 NormalY=0 NormalZ=1 AngleXU=0 Radius=1
    g6: Circle CenterX=-4.8 CenterY=1e-16 CenterZ=0 NormalX=0 NormalY=0 NormalZ=1 AngleXU=0 Radius=1
    g7: BSplineCurve PolesCount=3 KnotsCount=2 Degree=2 IsPeriodic=0
    g8: GeomPoint X=-3.5 Y=1.3 Z=0
    g9: GeomPoint X=-4.8 Y=1e-16 Z=0
    g10: LineSegment StartX=-3.5 StartY=1.3 StartZ=0 EndX=-3.5 EndY=1.5 EndZ=0
  constraints (24):
    c: Horizontal(g0)
    c: Distance(g0) = 1.9
    c: Block(g0)
    c: Coincident(g1,g0)
    c: Vertical(g1)
    c: Coincident(g2,g1)
    c: Horizontal(g2)
    c: Coincident(g3,g0)
    c: Horizontal(g3)
    c: Distance(g3) = 1.3
    c: Weight(g4) = 1
    c: Equal(g4,g5)
    c: Coincident(g5,g0)
    c: Equal(g4,g6)
    c: Coincident(g7,g3)
    c: InternalAlignment(g4,g7)
    c: InternalAlignment(g5,g7)
    c: InternalAlignment(g6,g7)
    c: InternalAlignment(g8,g7)
    c: InternalAlignment(g9,g7)
    c: Coincident(g10,g7)
    c: Coincident(g10,g2)
    c: Vertical(g10)
    c: Block(g10)
FEATURE [Part::Feature] Face035
  shape: bbox 3.2 x 1.5 x 2e-07 mm, 1 faces, 0 solids (baked)
FEATURE [Part::Revolution] Revolve039  label="backCaseScrewRetainer"
  Angle = 360
  Axis = (0,1,0)
  Base = (0,0,0)
  FaceMakerClass = Part::FaceMakerBullseye
  Placement = pos=(12.5,3,62) rot=(0,0,1;0rad)
  Solid = false
  Source = -> Face035
  Symmetric = false
FEATURE [Part::Feature] Face036
  shape: bbox 3.2 x 1.5 x 2e-07 mm, 1 faces, 0 solids (baked)
FEATURE [Part::Feature] Face039
  shape: bbox 4.8 x 30.2 x 2e-07 mm, 1 faces, 0 solids (baked)
FEATURE [Part::Revolution] Revolve043  label="frontCaseScrewPost002"
  Angle = 360
  Axis = (0,1,0)
  Base = (0,0,0)
  FaceMakerClass = Part::FaceMakerBullseye
  Placement = pos=(89.5,4.5,3.5) rot=(0,0,1;0rad)
  Solid = false
  Source = -> Face039
  Symmetric = false
FEATURE [Part::Feature] Face042
  shape: bbox 4.8 x 30.2 x 2e-07 mm, 1 faces, 0 solids (baked)
FEATURE [Part::Revolution] Revolve046  label="frontCaseScrewPost003"
  Angle = 360
  Axis = (0,1,0)
  Base = (0,0,0)
  FaceMakerClass = Part::FaceMakerBullseye
  Placement = pos=(89.5,4.5,68.5) rot=(0,0,1;0rad)
  Solid = false
  Source = -> Face042
  Symmetric = false
FEATURE [Part::Feature] Face043
  shape: bbox 3.2 x 1.5 x 2e-07 mm, 1 faces, 0 solids (baked)
FEATURE [Part::Revolution] Revolve047  label="frontCaseScrewRetainer002"
  Angle = 360
  Axis = (0,1,0)
  Base = (0,0,0)
  FaceMakerClass = Part::FaceMakerBullseye
  Placement = pos=(89.5,3,68.5) rot=(0,0,1;0rad)
  Solid = false
  Source = -> Face043
  Symmetric = false
FEATURE [Part::Feature] Face044
  shape: bbox 3.2 x 1.5 x 2e-07 mm, 1 faces, 0 solids (baked)
FEATURE [Part::Revolution] Revolve048  label="frontCaseScrewRetainer003"
  Angle = 360
  Axis = (0,1,0)
  Base = (0,0,0)
  FaceMakerClass = Part::FaceMakerBullseye
  Placement = pos=(89.5,3,3.5) rot=(0,0,1;0rad)
  Solid = false
  Source = -> Face044
  Symmetric = false
FEATURE [App::MeasureDistance] Distance002  label="Distance: 1.67 mm"
  Distance = 1.66921
  P1 = (99.2361,4.7524,71.7)
  P2 = (99.2347,6.42161,71.7)
FEATURE [Sketcher::SketchObject] Sketch018
  FullyConstrained = true
  sketch-geometry (7):
    g0: LineSegment StartX=0 StartY=0 StartZ=0 EndX=0 EndY=6 EndZ=0
    g1: Circle CenterX=0 CenterY=0 CenterZ=0 NormalX=0 NormalY=0 NormalZ=1 AngleXU=0 Radius=1
    g2: Circle CenterX=8 CenterY=6 CenterZ=0 NormalX=0 NormalY=0 NormalZ=1 AngleXU=0 Radius=1
    g3: BSplineCurve PolesCount=3 KnotsCount=2 Degree=2 IsPeriodic=0
    g4: GeomPoint X=0 Y=0 Z=0
    g5: GeomPoint X=8 Y=6 Z=0
    g6: LineSegment StartX=0 StartY=6 StartZ=0 EndX=8 EndY=6 EndZ=0
  constraints (14):
    c: Coincident(g0,g-1)
    c: Distance(g0) = 6
    c: Vertical(g0)
    c: Coincident(g3,g0)
    c: Weight(g1) = 1
    c: Equal(g1,g2)
    c: InternalAlignment(g1,g3)
    c: InternalAlignment(g2,g3)
    c: InternalAlignment(g4,g3)
    c: InternalAlignment(g5,g3)
    c: Block(g3)
    c: Coincident(g6,g0)
    c: Coincident(g6,g3)
    c: Horizontal(g6)
FEATURE [Part::Extrusion] Extrude012  label="caseScrewPillarBracket"
  Base = -> Sketch018
  Dir = (0,0,1)
  DirMode = 2
  FaceMakerClass = Part::FaceMakerBullseye
  LengthFwd = 2.4
  LengthRev = 0
  Placement = pos=(15.76,29,8.8) rot=(0,1,0;0rad)
  Solid = true
  Symmetric = false
FEATURE [Sketcher::SketchObject] Sketch019
  FullyConstrained = true
  sketch-geometry (7):
    g0: LineSegment StartX=0 StartY=0 StartZ=0 EndX=0 EndY=6 EndZ=0
    g1: Circle CenterX=0 CenterY=0 CenterZ=0 NormalX=0 NormalY=0 NormalZ=1 AngleXU=0 Radius=1
    g2: Circle CenterX=8 CenterY=6 CenterZ=0 NormalX=0 NormalY=0 NormalZ=1 AngleXU=0 Radius=1
    g3: BSplineCurve PolesCount=3 KnotsCount=2 Degree=2 IsPeriodic=0
    g4: GeomPoint X=0 Y=0 Z=0
    g5: GeomPoint X=8 Y=6 Z=0
    g6: LineSegment StartX=0 StartY=6 StartZ=0 EndX=8 EndY=6 EndZ=0
  constraints (14):
    c: Coincident(g0,g-1)
    c: Distance(g0) = 6
    c: Vertical(g0)
    c: Coincident(g3,g0)
    c: Weight(g1) = 1
    c: Equal(g1,g2)
    c: InternalAlignment(g1,g3)
    c: InternalAlignment(g2,g3)
    c: InternalAlignment(g4,g3)
    c: InternalAlignment(g5,g3)
    c: Block(g3)
    c: Coincident(g6,g0)
    c: Coincident(g6,g3)
    c: Horizontal(g6)
FEATURE [Part::Extrusion] Extrude013  label="caseScrewPillarBracket001"
  Base = -> Sketch019
  Dir = (0,0,1)
  DirMode = 2
  FaceMakerClass = Part::FaceMakerBullseye
  LengthFwd = 2.4
  LengthRev = 0
  Placement = pos=(15.76,29,60.8) rot=(0,0,1;0rad)
  Solid = true
  Symmetric = false
FEATURE [Sketcher::SketchObject] Sketch020
  FullyConstrained = true
  sketch-geometry (7):
    g0: LineSegment StartX=0 StartY=0 StartZ=0 EndX=0 EndY=6 EndZ=0
    g1: Circle CenterX=0 CenterY=0 CenterZ=0 NormalX=0 NormalY=0 NormalZ=1 AngleXU=0 Radius=1
    g2: Circle CenterX=8 CenterY=6 CenterZ=0 NormalX=0 NormalY=0 NormalZ=1 AngleXU=0 Radius=1
    g3: BSplineCurve PolesCount=3 KnotsCount=2 Degree=2 IsPeriodic=0
    g4: GeomPoint X=0 Y=0 Z=0
    g5: GeomPoint X=8 Y=6 Z=0
    g6: LineSegment StartX=0 StartY=6 StartZ=0 EndX=8 EndY=6 EndZ=0
  constraints (14):
    c: Coincident(g0,g-1)
    c: Distance(g0) = 6
    c: Vertical(g0)
    c: Coincident(g3,g0)
    c: Weight(g1) = 1
    c: Equal(g1,g2)
    c: InternalAlignment(g1,g3)
    c: InternalAlignment(g2,g3)
    c: InternalAlignment(g4,g3)
    c: InternalAlignment(g5,g3)
    c: Block(g3)
    c: Coincident(g6,g0)
    c: Coincident(g6,g3)
    c: Horizontal(g6)
FEATURE [Part::Extrusion] Extrude014  label="caseScrewPillarBracket002"
  Base = -> Sketch020
  Dir = (0,0,1)
  DirMode = 2
  FaceMakerClass = Part::FaceMakerBullseye
  LengthFwd = 2.4
  LengthRev = 0
  Placement = pos=(13.7,29,13.26) rot=(0,-1,0;1.5708rad)
  Solid = true
  Symmetric = false
FEATURE [Sketcher::SketchObject] Sketch021
  FullyConstrained = true
  sketch-geometry (7):
    g0: LineSegment StartX=0 StartY=0 StartZ=0 EndX=0 EndY=6 EndZ=0
    g1: Circle CenterX=0 CenterY=0 CenterZ=0 NormalX=0 NormalY=0 NormalZ=1 AngleXU=0 Radius=1
    g2: Circle CenterX=8 CenterY=6 CenterZ=0 NormalX=0 NormalY=0 NormalZ=1 AngleXU=0 Radius=1
    g3: BSplineCurve PolesCount=3 KnotsCount=2 Degree=2 IsPeriodic=0
    g4: GeomPoint X=0 Y=0 Z=0
    g5: GeomPoint X=8 Y=6 Z=0
    g6: LineSegment StartX=0 StartY=6 StartZ=0 EndX=8 EndY=6 EndZ=0
  constraints (14):
    c: Coincident(g0,g-1)
    c: Distance(g0) = 6
    c: Vertical(g0)
    c: Coincident(g3,g0)
    c: Weight(g1) = 1
    c: Equal(g1,g2)
    c: InternalAlignment(g1,g3)
    c: InternalAlignment(g2,g3)
    c: InternalAlignment(g4,g3)
    c: InternalAlignment(g5,g3)
    c: Block(g3)
    c: Coincident(g6,g0)
    c: Coincident(g6,g3)
    c: Horizontal(g6)
FEATURE [Part::Extrusion] Extrude015  label="caseScrewPillarBracket003"
  Base = -> Sketch021
  Dir = (0,0,1)
  DirMode = 2
  FaceMakerClass = Part::FaceMakerBullseye
  LengthFwd = 2.4
  LengthRev = 0
  Placement = pos=(11.3,29,58.74) rot=(0,1,0;1.5708rad)
  Solid = true
  Symmetric = false
FEATURE [Sketcher::SketchObject] Sketch022
  FullyConstrained = true
  sketch-geometry (7):
    g0: LineSegment StartX=0 StartY=0 StartZ=0 EndX=0 EndY=6 EndZ=0
    g1: Circle CenterX=0 CenterY=0 CenterZ=0 NormalX=0 NormalY=0 NormalZ=1 AngleXU=0 Radius=1
    g2: Circle CenterX=8 CenterY=6 CenterZ=0 NormalX=0 NormalY=0 NormalZ=1 AngleXU=0 Radius=1
    g3: BSplineCurve PolesCount=3 KnotsCount=2 Degree=2 IsPeriodic=0
    g4: GeomPoint X=0 Y=0 Z=0
    g5: GeomPoint X=8 Y=6 Z=0
    g6: LineSegment StartX=0 StartY=6 StartZ=0 EndX=8 EndY=6 EndZ=0
  constraints (14):
    c: Coincident(g0,g-1)
    c: Distance(g0) = 6
    c: Vertical(g0)
    c: Coincident(g3,g0)
    c: Weight(g1) = 1
    c: Equal(g1,g2)
    c: InternalAlignment(g1,g3)
    c: InternalAlignment(g2,g3)
    c: InternalAlignment(g4,g3)
    c: InternalAlignment(g5,g3)
    c: Block(g3)
    c: Coincident(g6,g0)
    c: Coincident(g6,g3)
    c: Horizontal(g6)
FEATURE [Part::Extrusion] Extrude016  label="caseScrewPillarBracket004"
  Base = -> Sketch022
  Dir = (0,0,1)
  DirMode = 2
  FaceMakerClass = Part::FaceMakerBullseye
  LengthFwd = 2.4
  LengthRev = 0
  Placement = pos=(88.3,29,65.23) rot=(0,1,0;1.5708rad)
  Solid = true
  Symmetric = false
FEATURE [Sketcher::SketchObject] Sketch023
  FullyConstrained = true
  sketch-geometry (7):
    g0: LineSegment StartX=0 StartY=0 StartZ=0 EndX=0 EndY=6 EndZ=0
    g1: Circle CenterX=0 CenterY=0 CenterZ=0 NormalX=0 NormalY=0 NormalZ=1 AngleXU=0 Radius=1
    g2: Circle CenterX=8 CenterY=6 CenterZ=0 NormalX=0 NormalY=0 NormalZ=1 AngleXU=0 Radius=1
    g3: BSplineCurve PolesCount=3 KnotsCount=2 Degree=2 IsPeriodic=0
    g4: GeomPoint X=0 Y=0 Z=0
    g5: GeomPoint X=8 Y=6 Z=0
    g6: LineSegment StartX=0 StartY=6 StartZ=0 EndX=8 EndY=6 EndZ=0
  constraints (14):
    c: Coincident(g0,g-1)
    c: Distance(g0) = 6
    c: Vertical(g0)
    c: Coincident(g3,g0)
    c: Weight(g1) = 1
    c: Equal(g1,g2)
    c: InternalAlignment(g1,g3)
    c: InternalAlignment(g2,g3)
    c: InternalAlignment(g4,g3)
    c: InternalAlignment(g5,g3)
    c: Block(g3)
    c: Coincident(g6,g0)
    c: Coincident(g6,g3)
    c: Horizontal(g6)
FEATURE [Part::Extrusion] Extrude017  label="caseScrewPillarBracket005"
  Base = -> Sketch023
  Dir = (0,0,1)
  DirMode = 2
  FaceMakerClass = Part::FaceMakerBullseye
  LengthFwd = 2.4
  LengthRev = 0
  Placement = pos=(90.7,29,6.77) rot=(0,-1,0;1.5708rad)
  Solid = true
  Symmetric = false
FEATURE [Sketcher::SketchObject] Sketch024
  FullyConstrained = true
  sketch-geometry (7):
    g0: LineSegment StartX=0 StartY=0 StartZ=0 EndX=0 EndY=6 EndZ=0
    g1: Circle CenterX=0 CenterY=0 CenterZ=0 NormalX=0 NormalY=0 NormalZ=1 AngleXU=0 Radius=1
    g2: Circle CenterX=8 CenterY=6 CenterZ=0 NormalX=0 NormalY=0 NormalZ=1 AngleXU=0 Radius=1
    g3: BSplineCurve PolesCount=3 KnotsCount=2 Degree=2 IsPeriodic=0
    g4: GeomPoint X=0 Y=0 Z=0
    g5: GeomPoint X=8 Y=6 Z=0
    g6: LineSegment StartX=0 StartY=6 StartZ=0 EndX=8 EndY=6 EndZ=0
  constraints (14):
    c: Coincident(g0,g-1)
    c: Distance(g0) = 6
    c: Vertical(g0)
    c: Coincident(g3,g0)
    c: Weight(g1) = 1
    c: Equal(g1,g2)
    c: InternalAlignment(g1,g3)
    c: InternalAlignment(g2,g3)
    c: InternalAlignment(g4,g3)
    c: InternalAlignment(g5,g3)
    c: Block(g3)
    c: Coincident(g6,g0)
    c: Coincident(g6,g3)
    c: Horizontal(g6)
FEATURE [Part::Extrusion] Extrude018  label="caseScrewPillarBracket006"
  Base = -> Sketch024
  Dir = (0,0,1)
  DirMode = 2
  FaceMakerClass = Part::FaceMakerBullseye
  LengthFwd = 2.4
  LengthRev = 0
  Placement = pos=(103.7,29,6.77) rot=(0,-1,0;1.5708rad)
  Solid = true
  Symmetric = false
FEATURE [Sketcher::SketchObject] Sketch025
  FullyConstrained = true
  sketch-geometry (7):
    g0: LineSegment StartX=0 StartY=0 StartZ=0 EndX=0 EndY=6 EndZ=0
    g1: Circle CenterX=0 CenterY=0 CenterZ=0 NormalX=0 NormalY=0 NormalZ=1 AngleXU=0 Radius=1
    g2: Circle CenterX=8 CenterY=6 CenterZ=0 NormalX=0 NormalY=0 NormalZ=1 AngleXU=0 Radius=1
    g3: BSplineCurve PolesCount=3 KnotsCount=2 Degree=2 IsPeriodic=0
    g4: GeomPoint X=0 Y=0 Z=0
    g5: GeomPoint X=8 Y=6 Z=0
    g6: LineSegment StartX=0 StartY=6 StartZ=0 EndX=8 EndY=6 EndZ=0
  constraints (14):
    c: Coincident(g0,g-1)
    c: Distance(g0) = 6
    c: Vertical(g0)
    c: Coincident(g3,g0)
    c: Weight(g1) = 1
    c: Equal(g1,g2)
    c: InternalAlignment(g1,g3)
    c: InternalAlignment(g2,g3)
    c: InternalAlignment(g4,g3)
    c: InternalAlignment(g5,g3)
    c: Block(g3)
    c: Coincident(g6,g0)
    c: Coincident(g6,g3)
    c: Horizontal(g6)
FEATURE [Part::Extrusion] Extrude019  label="caseScrewPillarBracket007"
  Base = -> Sketch025
  Dir = (0,0,1)
  DirMode = 2
  FaceMakerClass = Part::FaceMakerBullseye
  LengthFwd = 2.4
  LengthRev = 0
  Placement = pos=(101.3,29,65.23) rot=(0,1,0;1.5708rad)
  Solid = true
  Symmetric = false
FEATURE [Part::Box] Box011  label="frontCaseScrewPillarBracket"
  AttacherType = Attacher::AttachEngine3D
  Height = 2.4
  Length = 16
  Placement = pos=(87,28,2.3) rot=(0,0,1;0rad)
  Width = 7
FEATURE [Part::Box] Box012  label="frontCaseScrewPillarBracket001"
  AttacherType = Attacher::AttachEngine3D
  Height = 2.4
  Length = 16
  Placement = pos=(87,28,67.3) rot=(0,0,1;0rad)
  Width = 7
FEATURE [Sketcher::SketchObject] Sketch026
  FullyConstrained = true
  sketch-geometry (17):
    g0: Circle CenterX=-3.5 CenterY=23.5 CenterZ=0 NormalX=0 NormalY=0 NormalZ=1 AngleXU=0 Radius=1
    g1: Circle CenterX=-1 CenterY=15.25 CenterZ=0 NormalX=0 NormalY=0 NormalZ=1 AngleXU=0 Radius=1
    g2: Circle CenterX=-3.5 CenterY=7 CenterZ=0 NormalX=0 NormalY=0 NormalZ=1 AngleXU=0 Radius=1
    g3: BSplineCurve PolesCount=3 KnotsCount=2 Degree=2 IsPeriodic=0
    g4: GeomPoint X=-3.5 Y=23.5 Z=0
    g5: GeomPoint X=-3.5 Y=7 Z=0
    g6: Circle CenterX=-4.8 CenterY=30.5 CenterZ=0 NormalX=0 NormalY=0 NormalZ=1 AngleXU=0 Radius=1
    g7: Circle CenterX=-3.5 CenterY=30.5 CenterZ=0 NormalX=0 NormalY=0 NormalZ=1 AngleXU=0 Radius=1
    g8: Circle CenterX=-3.5 CenterY=29.2 CenterZ=0 NormalX=0 NormalY=0 NormalZ=1 AngleXU=0 Radius=1
    g9: BSplineCurve PolesCount=3 KnotsCount=2 Degree=2 IsPeriodic=0
    g10: GeomPoint X=-4.8 Y=30.5 Z=0
    g11: GeomPoint X=-3.5 Y=29.2 Z=0
    g12: LineSegment StartX=-3.5 StartY=29.2 StartZ=0 EndX=-3.5 EndY=23.5 EndZ=0
    g13: LineSegment StartX=-4.8 StartY=30.5 StartZ=0 EndX=0 EndY=30.5 EndZ=0
    g14: LineSegment StartX=-3.5 StartY=5 StartZ=0 EndX=-3.5 EndY=7 EndZ=0
    g15: LineSegment StartX=0 StartY=5 StartZ=0 EndX=0 EndY=30.5 EndZ=0
    g16: LineSegment StartX=-3.5 StartY=5 StartZ=0 EndX=0 EndY=5 EndZ=0
  constraints (33):
    c: Weight(g0) = 1
    c: Equal(g0,g1)
    c: Equal(g0,g2)
    c: InternalAlignment(g0,g3)
    c: InternalAlignment(g1,g3)
    c: InternalAlignment(g2,g3)
    c: InternalAlignment(g4,g3)
    c: InternalAlignment(g5,g3)
    c: Block(g3)
    c: Weight(g6) = 1
    c: Equal(g6,g7)
    c: Equal(g6,g8)
    c: InternalAlignment(g6,g9)
    c: InternalAlignment(g7,g9)
    c: InternalAlignment(g8,g9)
    c: InternalAlignment(g10,g9)
    c: InternalAlignment(g11,g9)
    c: Block(g9)
    c: Coincident(g12,g9)
    c: Coincident(g12,g3)
    c: Vertical(g12)
    c: Coincident(g13,g9)
    c: Horizontal(g13)
    c: Distance(g13) = 4.8
    c: Coincident(g14,g3)
    c: Vertical(g14)
    c: Coincident(g15,g13)
    c: Vertical(g15)
    c: Tangent(g15,g1)
    c: Distance(g14) = 2
    c: Coincident(g16,g14)
    c: Horizontal(g16)
    c: Coincident(g15,g16)
FEATURE [Part::Feature] Face050
  shape: bbox 4.8 x 25.5 x 2e-07 mm, 1 faces, 0 solids (baked)
FEATURE [Part::Revolution] Revolve054  label="moreFrontCaseScrewPost001"
  Angle = 360
  Axis = (0,1,0)
  Base = (0,0,0)
  FaceMakerClass = Part::FaceMakerBullseye
  Placement = pos=(102.5,4.5,3.5) rot=(0,0,1;0rad)
  Solid = false
  Source = -> Face050
  Symmetric = false
FEATURE [Part::Feature] Face051
  shape: bbox 4.8 x 25.5 x 2e-07 mm, 1 faces, 0 solids (baked)
FEATURE [Part::Revolution] Revolve055  label="moreFrontCaseScrewPost002"
  Angle = 360
  Axis = (0,1,0)
  Base = (0,0,0)
  FaceMakerClass = Part::FaceMakerBullseye
  Placement = pos=(102.5,4.5,68.5) rot=(0,0,1;0rad)
  Solid = false
  Source = -> Face051
  Symmetric = false
FEATURE [Sketcher::SketchObject] Sketch027
  FullyConstrained = true
  sketch-geometry (10):
    g0: LineSegment StartX=-1.6 StartY=4.7 StartZ=0 EndX=-1.6 EndY=1.7 EndZ=0
    g1: LineSegment StartX=-3.5 StartY=4.7 StartZ=0 EndX=-1.6 EndY=4.7 EndZ=0
    g2: LineSegment StartX=-1.6 StartY=1.7 StartZ=0 EndX=-1.6 EndY=1.5 EndZ=0
    g3: LineSegment StartX=-1.6 StartY=1.5 StartZ=0 EndX=-5.2 EndY=1.5 EndZ=0
    g4: Circle CenterX=-3.5 CenterY=4.7 CenterZ=0 NormalX=0 NormalY=0 NormalZ=1 AngleXU=0 Radius=1
    g5: Circle CenterX=-3.59627 CenterY=2.99743 CenterZ=0 NormalX=0 NormalY=0 NormalZ=1 AngleXU=0 Radius=1
    g6: Circle CenterX=-5.2 CenterY=1.5 CenterZ=0 NormalX=0 NormalY=0 NormalZ=1 AngleXU=0 Radius=1
    g7: BSplineCurve PolesCount=3 KnotsCount=2 Degree=2 IsPeriodic=0
    g8: GeomPoint X=-3.5 Y=4.7 Z=0
    g9: GeomPoint X=-5.2 Y=1.5 Z=0
  constraints (23):
    c: Vertical(g0)
    c: Distance(g0) = 3
    c: Coincident(g1,g0)
    c: Horizontal(g1)
    c: Block(g0)
    c: Block(g1)
    c: Coincident(g2,g0)
    c: Vertical(g2)
    c: Distance(g2) = 0.2
    c: Coincident(g3,g2)
    c: Horizontal(g3)
    c: Block(g3)
    c: Coincident(g7,g1)
    c: Weight(g4) = 1
    c: Equal(g4,g5)
    c: Equal(g4,g6)
    c: Coincident(g7,g3)
    c: InternalAlignment(g4,g7)
    c: InternalAlignment(g5,g7)
    c: InternalAlignment(g6,g7)
    c: InternalAlignment(g8,g7)
    c: InternalAlignment(g9,g7)
    c: Block(g7)
FEATURE [Sketcher::SketchObject] Sketch028
  FullyConstrained = true
  sketch-geometry (18):
    g0: LineSegment StartX=0 StartY=3e-16 StartZ=0 EndX=0 EndY=1.7 EndZ=0
    g1: LineSegment StartX=-3.5 StartY=0 StartZ=0 EndX=-3.5 EndY=0.9 EndZ=0
    g2: Circle CenterX=-2.7 CenterY=1.7 CenterZ=0 NormalX=0 NormalY=0 NormalZ=1 AngleXU=0 Radius=1
    g3: Circle CenterX=-3.5 CenterY=1.7 CenterZ=0 NormalX=0 NormalY=0 NormalZ=1 AngleXU=0 Radius=1
    g4: Circle CenterX=-3.5 CenterY=0.9 CenterZ=0 NormalX=0 NormalY=0 NormalZ=1 AngleXU=0 Radius=1
    g5: BSplineCurve PolesCount=3 KnotsCount=2 Degree=2 IsPeriodic=0
    g6: GeomPoint X=-2.7 Y=1.7 Z=0
    g7: GeomPoint X=-3.5 Y=0.9 Z=0
    g8: LineSegment StartX=-3.5 StartY=0 StartZ=0 EndX=-3.5 EndY=-7 EndZ=0
    g9: LineSegment StartX=0 StartY=3e-16 StartZ=0 EndX=0 EndY=-7 EndZ=0
    g10: LineSegment StartX=-3.5 StartY=-7 StartZ=0 EndX=0 EndY=-7 EndZ=0
    g11: LineSegment StartX=-2.7 StartY=1.7 StartZ=0 EndX=-1.6 EndY=1.7 EndZ=0
    g12: LineSegment StartX=0 StartY=1.7 StartZ=0 EndX=0 EndY=4.5 EndZ=0
    g13: LineSegment StartX=0 StartY=4.5 StartZ=0 EndX=0 EndY=10.8 EndZ=0
    g14: LineSegment StartX=0 StartY=10.8 StartZ=0 EndX=-2 EndY=10.8 EndZ=0
    g15: LineSegment StartX=-1.6 StartY=4.7 StartZ=0 EndX=-1.6 EndY=1.7 EndZ=0
    g16: LineSegment StartX=-1.6 StartY=4.7 StartZ=0 EndX=-2 EndY=4.7 EndZ=0
    g17: LineSegment StartX=-2 StartY=4.7 StartZ=0 EndX=-2 EndY=10.8 EndZ=0
  constraints (44):
    c: Vertical(g0)
    c: Vertical(g1)
    c: Distance(g1) = 0.9
    c: Block(g0)
    c: Distance(g0) = 1.7
    c: Weight(g2) = 1
    c: Equal(g2,g3)
    c: Equal(g2,g4)
    c: Coincident(g5,g1)
    c: InternalAlignment(g2,g5)
    c: InternalAlignment(g3,g5)
    c: InternalAlignment(g4,g5)
    c: InternalAlignment(g6,g5)
    c: InternalAlignment(g7,g5)
    c: Block(g5)
    c: Coincident(g8,g1)
    c: Vertical(g8)
    c: Distance(g8) = 7
    c: Vertical(g9)
    c: Equal(g8,g9) = 7
    c: Coincident(g9,g0)
    c: Coincident(g10,g8)
    c: Coincident(g10,g9)
    c: Horizontal(g10)
    c: Coincident(g11,g5)
    c: Horizontal(g11)
    c: Coincident(g12,g0)
    c: Vertical(g12)
    c: Distance(g12) = 2.8
    c: Coincident(g13,g12)
    c: Vertical(g13)
    c: Distance(g13) = 6.3
    c: Coincident(g14,g13)
    c: Horizontal(g14)
    c: Distance(g14) = 2
    c: Vertical(g15)
    c: Distance(g15) = 3
    c: Block(g11)
    c: Coincident(g15,g11)
    c: Coincident(g16,g15)
    c: Horizontal(g16)
    c: Coincident(g17,g16)
    c: Coincident(g17,g14)
    c: Vertical(g17)
FEATURE [Part::Revolution] Revolve040  label="backCaseScrewRetainer001"
  Angle = 360
  Axis = (0,1,0)
  Base = (0,0,0)
  FaceMakerClass = Part::FaceMakerBullseye
  Placement = pos=(12.5,3,10) rot=(0,0,1;0rad)
  Solid = false
  Source = -> Face036
  Symmetric = false
FEATURE [Part::Feature] Face055
  shape: bbox 3.5 x 30.2 x 2e-07 mm, 1 faces, 0 solids (baked)
FEATURE [Part::Revolution] Revolve059  label="backCaseScrewPost"
  Angle = 360
  Axis = (0,1,0)
  Base = (0,0,0)
  FaceMakerClass = Part::FaceMakerBullseye
  Placement = pos=(12.5,4.5,10) rot=(0,0,1;0rad)
  Solid = false
  Source = -> Face055
  Symmetric = false
FEATURE [Part::Feature] Face056
  shape: bbox 3.5 x 30.2 x 2e-07 mm, 1 faces, 0 solids (baked)
FEATURE [Part::Revolution] Revolve060  label="backCaseScrewPost001"
  Angle = 360
  Axis = (0,1,0)
  Base = (0,0,0)
  FaceMakerClass = Part::FaceMakerBullseye
  Placement = pos=(12.5,4.5,62) rot=(0,0,1;0rad)
  Solid = false
  Source = -> Face056
  Symmetric = false
FEATURE [Part::Feature] Face057
  shape: bbox 3.5 x 17.8 x 2e-07 mm, 1 faces, 0 solids (baked)
FEATURE [Part::Revolution] Revolve061  label="removeToCreateScrewAndThreadedInsertHole"
  Angle = 360
  Axis = (0,1,0)
  Base = (0,0,0)
  FaceMakerClass = Part::FaceMakerBullseye
  Placement = pos=(12.5,0,10) rot=(0,0,1;0rad)
  Solid = false
  Source = -> Face057
  Symmetric = false
FEATURE [Part::Feature] Face058
  shape: bbox 3.5 x 17.8 x 2e-07 mm, 1 faces, 0 solids (baked)
FEATURE [Part::Revolution] Revolve062  label="removeToCreateScrewAndThreadedInsertHole001"
  Angle = 360
  Axis = (0,1,0)
  Base = (0,0,0)
  FaceMakerClass = Part::FaceMakerBullseye
  Placement = pos=(12.5,0,62) rot=(0,0,1;0rad)
  Solid = false
  Source = -> Face058
  Symmetric = false
FEATURE [Part::Feature] Face059
  shape: bbox 3.5 x 17.8 x 2e-07 mm, 1 faces, 0 solids (baked)
FEATURE [Part::Revolution] Revolve063  label="removeToCreateScrewAndThreadedInsertHole002"
  Angle = 360
  Axis = (0,1,0)
  Base = (0,0,0)
  FaceMakerClass = Part::FaceMakerBullseye
  Placement = pos=(89.5,0,68.5) rot=(0,0,1;0rad)
  Solid = false
  Source = -> Face059
  Symmetric = false
FEATURE [Part::Feature] Face060
  shape: bbox 3.5 x 17.8 x 2e-07 mm, 1 faces, 0 solids (baked)
FEATURE [Part::Revolution] Revolve064  label="removeToCreateScrewAndThreadedInsertHole003"
  Angle = 360
  Axis = (0,1,0)
  Base = (0,0,0)
  FaceMakerClass = Part::FaceMakerBullseye
  Placement = pos=(89.5,0,3.5) rot=(0,0,1;0rad)
  Solid = false
  Source = -> Face060
  Symmetric = false
FEATURE [Part::Feature] Face061
  shape: bbox 3.5 x 17.8 x 2e-07 mm, 1 faces, 0 solids (baked)
FEATURE [Part::Revolution] Revolve065  label="removeToCreateScrewAndThreadedInsertHole004"
  Angle = 360
  Axis = (0,1,0)
  Base = (0,0,0)
  FaceMakerClass = Part::FaceMakerBullseye
  Placement = pos=(102.5,4.7,3.5) rot=(0,0,1;0rad)
  Solid = false
  Source = -> Face061
  Symmetric = false
FEATURE [Part::Feature] Face062
  shape: bbox 3.5 x 17.8 x 2e-07 mm, 1 faces, 0 solids (baked)
FEATURE [Part::Revolution] Revolve066  label="removeToCreateScrewAndThreadedInsertHole005"
  Angle = 360
  Axis = (0,1,0)
  Base = (0,0,0)
  FaceMakerClass = Part::FaceMakerBullseye
  Placement = pos=(102.5,4.7,68.5) rot=(0,0,1;0rad)
  Solid = false
  Source = -> Face062
  Symmetric = false
FEATURE [Part::MultiFuse] Fusion047  label="makeHoles"
  Shapes = -> [Revolve066,Revolve065,Revolve064,Revolve063,Revolve062,Revolve061]
FEATURE [Part::Feature] Face063
  shape: bbox 3.6 x 3.2 x 2e-07 mm, 1 faces, 0 solids (baked)
FEATURE [Part::Revolution] Revolve067  label="moreFrontCaseScrewRetainer002"
  Angle = 360
  Axis = (0,1,0)
  Base = (0,0,0)
  FaceMakerClass = Part::FaceMakerBullseye
  Placement = pos=(102.5,4.5,68.5) rot=(0,0,1;0rad)
  Solid = false
  Source = -> Face063
  Symmetric = false
FEATURE [Part::Feature] Face064
  shape: bbox 3.6 x 3.2 x 2e-07 mm, 1 faces, 0 solids (baked)
FEATURE [Part::Revolution] Revolve068  label="moreFrontCaseScrewRetainer003"
  Angle = 360
  Axis = (0,1,0)
  Base = (0,0,0)
  FaceMakerClass = Part::FaceMakerBullseye
  Placement = pos=(102.5,4.5,3.5) rot=(0,0,1;0rad)
  Solid = false
  Source = -> Face064
  Symmetric = false
FEATURE [Part::Feature] Face065
  shape: bbox 3.5 x 17.8 x 2e-07 mm, 1 faces, 0 solids (baked)
FEATURE [Part::Revolution] Revolve069  label="removeToCreateScrewAndThreadedInsertHole006"
  Angle = 360
  Axis = (0,1,0)
  Base = (0,0,0)
  FaceMakerClass = Part::FaceMakerBullseye
  Placement = pos=(12.5,0,10) rot=(0,0,1;0rad)
  Solid = false
  Source = -> Face065
  Symmetric = false
FEATURE [Part::Feature] Face066
  shape: bbox 3.5 x 17.8 x 2e-07 mm, 1 faces, 0 solids (baked)
FEATURE [Part::Revolution] Revolve070  label="removeToCreateScrewAndThreadedInsertHole007"
  Angle = 360
  Axis = (0,1,0)
  Base = (0,0,0)
  FaceMakerClass = Part::FaceMakerBullseye
  Placement = pos=(12.5,0,62) rot=(0,0,1;0rad)
  Solid = false
  Source = -> Face066
  Symmetric = false
FEATURE [Part::Feature] Face067
  shape: bbox 3.5 x 17.8 x 2e-07 mm, 1 faces, 0 solids (baked)
FEATURE [Part::Revolution] Revolve071  label="removeToCreateScrewAndThreadedInsertHole008"
  Angle = 360
  Axis = (0,1,0)
  Base = (0,0,0)
  FaceMakerClass = Part::FaceMakerBullseye
  Placement = pos=(89.5,0,68.5) rot=(0,0,1;0rad)
  Solid = false
  Source = -> Face067
  Symmetric = false
FEATURE [Part::Feature] Face068
  shape: bbox 3.5 x 17.8 x 2e-07 mm, 1 faces, 0 solids (baked)
FEATURE [Part::Revolution] Revolve072  label="removeToCreateScrewAndThreadedInsertHole009"
  Angle = 360
  Axis = (0,1,0)
  Base = (0,0,0)
  FaceMakerClass = Part::FaceMakerBullseye
  Placement = pos=(89.5,0,3.5) rot=(0,0,1;0rad)
  Solid = false
  Source = -> Face068
  Symmetric = false
FEATURE [Part::Feature] Face069
  shape: bbox 3.5 x 17.8 x 2e-07 mm, 1 faces, 0 solids (baked)
FEATURE [Part::Feature] Face070
  shape: bbox 3.5 x 17.8 x 2e-07 mm, 1 faces, 0 solids (baked)
FEATURE [Part::Revolution] Revolve073  label="removeToCreateScrewAndThreadedInsertHole010"
  Angle = 360
  Axis = (0,1,0)
  Base = (0,0,0)
  FaceMakerClass = Part::FaceMakerBullseye
  Placement = pos=(102.5,4.7,3.5) rot=(0,0,1;0rad)
  Solid = false
  Source = -> Face069
  Symmetric = false
FEATURE [Part::Revolution] Revolve074  label="removeToCreateScrewAndThreadedInsertHole011"
  Angle = 360
  Axis = (0,1,0)
  Base = (0,0,0)
  FaceMakerClass = Part::FaceMakerBullseye
  Placement = pos=(102.5,4.7,68.5) rot=(0,0,1;0rad)
  Solid = false
  Source = -> Face070
  Symmetric = false
FEATURE [Part::MultiFuse] Fusion048  label="makeHoles001"
  Shapes = -> [Revolve074,Revolve073,Revolve072,Revolve071,Revolve070,Revolve069]
FEATURE [Part::MultiFuse] Fusion049  label="caseScrewRetainers"
  Shapes = -> [Revolve067,Revolve068,Revolve048,Revolve047,Revolve039,Revolve040]
FEATURE [Part::Cut] Cut015  label="caseScrewRetainers001"
  Base = -> Fusion049
  Tool = -> Fusion048
FEATURE [Part::MultiFuse] Fusion050  label="casePillars"
  Shapes = -> [Revolve055,Revolve054,Revolve043,Revolve046,Revolve059,Revolve060]
FEATURE [Part::Feature] Face071 .. Face076  x6 (patterned run collapsed; names and placements below)
  shape: bbox 3.5 x 17.8 x 2e-07 mm, 1 faces, 0 solids (baked)
FEATURE [Part::Revolution] Revolve075  label="removeToCreateScrewAndThreadedInsertHole012"
  Angle = 360
  Axis = (0,1,0)
  Base = (0,0,0)
  FaceMakerClass = Part::FaceMakerBullseye
  Placement = pos=(12.5,0,10) rot=(0,0,1;0rad)
  Solid = false
  Source = -> Face071
  Symmetric = false
FEATURE [Part::Revolution] Revolve076  label="removeToCreateScrewAndThreadedInsertHole013"
  Angle = 360
  Axis = (0,1,0)
  Base = (0,0,0)
  FaceMakerClass = Part::FaceMakerBullseye
  Placement = pos=(12.5,0,62) rot=(0,0,1;0rad)
  Solid = false
  Source = -> Face072
  Symmetric = false
FEATURE [Part::Revolution] Revolve077  label="removeToCreateScrewAndThreadedInsertHole014"
  Angle = 360
  Axis = (0,1,0)
  Base = (0,0,0)
  FaceMakerClass = Part::FaceMakerBullseye
  Placement = pos=(89.5,0,68.5) rot=(0,0,1;0rad)
  Solid = false
  Source = -> Face073
  Symmetric = false
FEATURE [Part::Revolution] Revolve078  label="removeToCreateScrewAndThreadedInsertHole015"
  Angle = 360
  Axis = (0,1,0)
  Base = (0,0,0)
  FaceMakerClass = Part::FaceMakerBullseye
  Placement = pos=(89.5,0,3.5) rot=(0,0,1;0rad)
  Solid = false
  Source = -> Face074
  Symmetric = false
FEATURE [Part::Revolution] Revolve079  label="removeToCreateScrewAndThreadedInsertHole016"
  Angle = 360
  Axis = (0,1,0)
  Base = (0,0,0)
  FaceMakerClass = Part::FaceMakerBullseye
  Placement = pos=(102.5,4.7,3.5) rot=(0,0,1;0rad)
  Solid = false
  Source = -> Face075
  Symmetric = false
FEATURE [Part::Revolution] Revolve080  label="removeToCreateScrewAndThreadedInsertHole017"
  Angle = 360
  Axis = (0,1,0)
  Base = (0,0,0)
  FaceMakerClass = Part::FaceMakerBullseye
  Placement = pos=(102.5,4.7,68.5) rot=(0,0,1;0rad)
  Solid = false
  Source = -> Face076
  Symmetric = false
FEATURE [Part::MultiFuse] Fusion051  label="makeHoles002"
  Shapes = -> [Revolve080,Revolve079,Revolve078,Revolve077,Revolve076,Revolve075]
FEATURE [Part::Cut] Cut016  label="caesPillars"
  Base = -> Fusion050
  Tool = -> Fusion051
FEATURE [Part::Revolution] Revolve009  label="plugHousing016"
  Angle = 360
  Axis = (0,1,0)
  Base = (0,0,0)
  FaceMakerClass = Part::FaceMakerBullseye
  Placement = pos=(0,0,36.15) rot=(0,0,1;0rad)
  Solid = false
  Source = -> Face012
  Symmetric = false
FEATURE [Part::MultiFuse] Fusion014  label="plugHousing023"
  Placement = pos=(0,0,0) rot=(0,0,1;1.5708rad)
  Shapes = -> [Revolve011,Revolve009]
FEATURE [Part::Revolution] Revolve010  label="plugHousing017"
  Angle = 360
  Axis = (0,1,0)
  Base = (0,0,0)
  FaceMakerClass = Part::FaceMakerBullseye
  Placement = pos=(0,0,36.15) rot=(0,0,1;0rad)
  Solid = false
  Source = -> Face014
  Symmetric = false
FEATURE [Part::MultiFuse] Fusion015  label="plugHousing024"
  Placement = pos=(0,0,0) rot=(0,0,1;1.5708rad)
  Shapes = -> [Revolve010,Revolve015]
FEATURE [Part::Revolution] Revolve014  label="plugHousing026"
  Angle = 360
  Axis = (0,1,0)
  Base = (0,0,0)
  FaceMakerClass = Part::FaceMakerBullseye
  Placement = pos=(0,0,36.15) rot=(0,0,1;0rad)
  Solid = false
  Source = -> Face011
  Symmetric = false
FEATURE [Part::Revolution] Revolve013  label="plugHousing025"
  Angle = 360
  Axis = (0,1,0)
  Base = (0,0,0)
  FaceMakerClass = Part::FaceMakerBullseye
  Placement = pos=(0,0,36.15) rot=(0,0,1;0rad)
  Solid = false
  Source = -> Face015
  Symmetric = false
FEATURE [Part::MultiFuse] Fusion016  label="plugHousing028"
  Placement = pos=(0,19,0) rot=(0,0,1;3.14159rad)
  Shapes = -> [Fusion014,Fusion013]
FEATURE [Part::MultiFuse] Fusion011  label="plugHousing018"
  Placement = pos=(0,0,0) rot=(0,0,1;1.5708rad)
  Shapes = -> [Revolve014,Revolve013]
FEATURE [Part::MultiFuse] Fusion012  label="plugHousing019"
  Placement = pos=(0,19,0) rot=(0,0,1;3.14159rad)
  Shapes = -> [Fusion011,Fusion015]
FEATURE [Part::MultiFuse] Fusion017  label="plugHousing029"
  Placement = pos=(122.621,0,-0.15) rot=(0,0,1;0rad)
  Shapes = -> [Fusion016,Fusion012]
FEATURE [Part::MultiFuse] Fusion052  label="casePillarRetainers"
  Shapes = -> [Extrude012,Extrude013,Extrude014,Extrude015,Extrude016,Extrude017,Extrude018,Extrude019,Box011,Box012]
FEATURE [Part::Feature] Face077
  shape: bbox 3.5 x 17.8 x 2e-07 mm, 1 faces, 0 solids (baked)
FEATURE [Part::Revolution] Revolve081  label="removeToCreateScrewAndThreadedInsertHole018"
  Angle = 360
  Axis = (0,1,0)
  Base = (0,0,0)
  FaceMakerClass = Part::FaceMakerBullseye
  Placement = pos=(62.3,30.3,19.7) rot=(0,0,1;0rad)
  Solid = false
  Source = -> Face077
  Symmetric = false
FEATURE [Part::Feature] Face078
  shape: bbox 3.5 x 17.8 x 2e-07 mm, 1 faces, 0 solids (baked)
FEATURE [Part::Revolution] Revolve082  label="removeToCreateScrewAndThreadedInsertHole019"
  Angle = 360
  Axis = (0,1,0)
  Base = (0,0,0)
  FaceMakerClass = Part::FaceMakerBullseye
  Placement = pos=(62.3,30.3,51.7) rot=(0,0,1;0rad)
  Solid = false
  Source = -> Face078
  Symmetric = false
FEATURE [Part::Feature] Face079
  shape: bbox 3.5 x 17.8 x 2e-07 mm, 1 faces, 0 solids (baked)
FEATURE [Part::Revolution] Revolve083  label="removeToCreateScrewAndThreadedInsertHole020"
  Angle = 360
  Axis = (0,1,0)
  Base = (0,0,0)
  FaceMakerClass = Part::FaceMakerBullseye
  Placement = pos=(30.3,30.3,19.7) rot=(0,0,1;0rad)
  Solid = false
  Source = -> Face079
  Symmetric = false
FEATURE [Part::Feature] Face080
  shape: bbox 3.5 x 17.8 x 2e-07 mm, 1 faces, 0 solids (baked)
FEATURE [Part::Revolution] Revolve084  label="removeToCreateScrewAndThreadedInsertHole021"
  Angle = 360
  Axis = (0,1,0)
  Base = (0,0,0)
  FaceMakerClass = Part::FaceMakerBullseye
  Placement = pos=(30.3,30.3,51.7) rot=(0,0,1;0rad)
  Solid = false
  Source = -> Face080
  Symmetric = false
FEATURE [Part::MultiFuse] Fusion053  label="createThreadedInsertHolesForFan"
  Shapes = -> [Revolve081,Revolve082,Revolve083,Revolve084]
FEATURE [Part::Cut] Cut017  label="fanScrewHousing001"
  Base = -> Fusion046
  Tool = -> Fusion053
FEATURE [Part::Feature] Face081
  shape: bbox 3.5 x 17.8 x 2e-07 mm, 1 faces, 0 solids (baked)
FEATURE [Part::Revolution] Revolve085  label="removeToCreateScrewAndThreadedInsertHole022"
  Angle = 360
  Axis = (0,1,0)
  Base = (0,0,0)
  FaceMakerClass = Part::FaceMakerBullseye
  Placement = pos=(62.3,30.3,19.7) rot=(0,0,1;0rad)
  Solid = false
  Source = -> Face081
  Symmetric = false
FEATURE [Part::Feature] Face082
  shape: bbox 3.5 x 17.8 x 2e-07 mm, 1 faces, 0 solids (baked)
FEATURE [Part::Revolution] Revolve086  label="removeToCreateScrewAndThreadedInsertHole023"
  Angle = 360
  Axis = (0,1,0)
  Base = (0,0,0)
  FaceMakerClass = Part::FaceMakerBullseye
  Placement = pos=(62.3,30.3,51.7) rot=(0,0,1;0rad)
  Solid = false
  Source = -> Face082
  Symmetric = false
FEATURE [Part::Feature] Face083
  shape: bbox 3.5 x 17.8 x 2e-07 mm, 1 faces, 0 solids (baked)
FEATURE [Part::Revolution] Revolve087  label="removeToCreateScrewAndThreadedInsertHole024"
  Angle = 360
  Axis = (0,1,0)
  Base = (0,0,0)
  FaceMakerClass = Part::FaceMakerBullseye
  Placement = pos=(30.3,30.3,19.7) rot=(0,0,1;0rad)
  Solid = false
  Source = -> Face083
  Symmetric = false
FEATURE [Part::Feature] Face084
  shape: bbox 3.5 x 17.8 x 2e-07 mm, 1 faces, 0 solids (baked)
FEATURE [Part::Revolution] Revolve088  label="removeToCreateScrewAndThreadedInsertHole025"
  Angle = 360
  Axis = (0,1,0)
  Base = (0,0,0)
  FaceMakerClass = Part::FaceMakerBullseye
  Placement = pos=(30.3,30.3,51.7) rot=(0,0,1;0rad)
  Solid = false
  Source = -> Face084
  Symmetric = false
FEATURE [Part::MultiFuse] Fusion054  label="createThreadedInsertHolesForFan001"
  Shapes = -> [Revolve085,Revolve086,Revolve087,Revolve088]
FEATURE [Part::Cut] Cut018  label="top007"
  Base = -> Fusion040
  Tool = -> Fusion054
FEATURE [Sketcher::SketchObject] Sketch029
  FullyConstrained = false
  Placement = pos=(0,0,0) rot=(1,0,0;1.5708rad)
  sketch-geometry (24):
    g0: ArcOfCircle CenterX=-4 CenterY=-10.5 CenterZ=0 NormalX=0 NormalY=0 NormalZ=1 AngleXU=0 Radius=1.5 StartAngle=6e-16 EndAngle=3.14159
    g1: ArcOfCircle CenterX=-34.2 CenterY=-10.5 CenterZ=0 NormalX=0 NormalY=0 NormalZ=1 AngleXU=0 Radius=1.5 StartAngle=0 EndAngle=3.14159
    g2: ArcOfCircle CenterX=-34.2 CenterY=-27.7 CenterZ=0 NormalX=0 NormalY=0 NormalZ=1 AngleXU=0 Radius=1.5 StartAngle=3.14159 EndAngle=6.28319
    g3: ArcOfCircle CenterX=-4 CenterY=-27.7 CenterZ=0 NormalX=0 NormalY=0 NormalZ=1 AngleXU=0 Radius=1.5 StartAngle=3.1416 EndAngle=6.28319
    g4: ArcOfCircle CenterX=-10 CenterY=-4.3 CenterZ=0 NormalX=0 NormalY=0 NormalZ=1 AngleXU=0 Radius=1.5 StartAngle=2e-16 EndAngle=3.14159
    g5: ArcOfCircle CenterX=-16.1 CenterY=-1.8 CenterZ=0 NormalX=0 NormalY=0 NormalZ=1 AngleXU=0 Radius=1.5 StartAngle=5e-16 EndAngle=3.14159
    g6: ArcOfCircle CenterX=-22.1 CenterY=-1.8 CenterZ=0 NormalX=0 NormalY=0 NormalZ=1 AngleXU=0 Radius=1.5 StartAngle=5e-16 EndAngle=3.14159
    g7: ArcOfCircle CenterX=-28.2 CenterY=-4.3 CenterZ=0 NormalX=0 NormalY=0 NormalZ=1 AngleXU=0 Radius=1.5 StartAngle=2e-16 EndAngle=3.14159
    g8: ArcOfCircle CenterX=-10 CenterY=-33.9 CenterZ=0 NormalX=0 NormalY=0 NormalZ=1 AngleXU=0 Radius=1.5 StartAngle=3.14159 EndAngle=6.28319
    g9: ArcOfCircle CenterX=-16.1 CenterY=-36.4 CenterZ=0 NormalX=0 NormalY=0 NormalZ=1 AngleXU=0 Radius=1.5 StartAngle=3.14159 EndAngle=6.28319
    g10: ArcOfCircle CenterX=-22.1 CenterY=-36.4 CenterZ=0 NormalX=0 NormalY=0 NormalZ=1 AngleXU=0 Radius=1.5 StartAngle=3.14159 EndAngle=6.28319
    g11: ArcOfCircle CenterX=-28.2 CenterY=-33.9 CenterZ=0 NormalX=0 NormalY=0 NormalZ=1 AngleXU=0 Radius=1.5 StartAngle=3.14159 EndAngle=6.28319
    g12: LineSegment StartX=-35.7 StartY=-10.5 StartZ=0 EndX=-35.7 EndY=-27.7 EndZ=0
    g13: LineSegment StartX=-32.7 StartY=-10.5 StartZ=0 EndX=-32.7 EndY=-27.7 EndZ=0
    g14: LineSegment StartX=-29.7 StartY=-33.9 StartZ=0 EndX=-29.7 EndY=-4.3 EndZ=0
    g15: LineSegment StartX=-26.7 StartY=-33.9 StartZ=0 EndX=-26.7 EndY=-4.3 EndZ=0
    g16: LineSegment StartX=-2.5 StartY=-10.5 StartZ=0 EndX=-2.5 EndY=-27.7 EndZ=0
    g17: LineSegment StartX=-8.5 StartY=-4.3 StartZ=0 EndX=-8.5 EndY=-33.9 EndZ=0
    g18: LineSegment StartX=-5.5 StartY=-10.5 StartZ=0 EndX=-5.5 EndY=-27.7 EndZ=0
    g19: LineSegment StartX=-11.5 StartY=-4.3 StartZ=0 EndX=-11.5 EndY=-33.9 EndZ=0
    g20: LineSegment StartX=-14.6 StartY=-1.8 StartZ=0 EndX=-14.6 EndY=-36.4 EndZ=0
    g21: LineSegment StartX=-17.6 StartY=-1.8 StartZ=0 EndX=-17.6 EndY=-36.4 EndZ=0
    g22: LineSegment StartX=-20.6 StartY=-36.4 StartZ=0 EndX=-20.6 EndY=-1.8 EndZ=0
    g23: LineSegment StartX=-23.6 StartY=-1.8 StartZ=0 EndX=-23.6 EndY=-36.4 EndZ=0
  constraints (48):
    c: Block(g0)
    c: Block(g1)
    c: Block(g2)
    c: Block(g3)
    c: Block(g4)
    c: Block(g5)
    c: Block(g6)
    c: Block(g7)
    c: Block(g8)
    c: Block(g9)
    c: Block(g10)
    c: Block(g11)
    c: Coincident(g12,g1)
    c: Coincident(g12,g2)
    c: Vertical(g12)
    c: Coincident(g13,g1)
    c: Coincident(g13,g2)
    c: Vertical(g13)
    c: Coincident(g14,g11)
    c: Coincident(g14,g7)
    c: Vertical(g14)
    c: Coincident(g15,g11)
    c: Coincident(g15,g7)
    c: Vertical(g15)
    c: Coincident(g16,g0)
    c: Coincident(g16,g3)
    c: Vertical(g16)
    c: Coincident(g17,g4)
    c: Coincident(g17,g8)
    c: Vertical(g17)
    c: Coincident(g18,g0)
    c: Coincident(g18,g3)
    c: Vertical(g18)
    c: Coincident(g19,g4)
    c: Coincident(g19,g8)
    c: Vertical(g19)
    c: Coincident(g20,g5)
    c: Coincident(g20,g9)
    c: Vertical(g20)
    c: Coincident(g21,g5)
    c: Coincident(g21,g9)
    c: Vertical(g21)
    c: Coincident(g22,g10)
    c: Coincident(g22,g6)
    c: Vertical(g22)
    c: Coincident(g23,g6)
    c: Coincident(g23,g10)
    c: Vertical(g23)
FEATURE [Part::Extrusion] Extrude020  label="removeToCreateFanGrillHoles"
  Base = -> Sketch029
  Dir = (0,-1,6e-16)
  DirMode = 2
  FaceMakerClass = Part::FaceMakerBullseye
  LengthFwd = 10
  LengthRev = 0
  Placement = pos=(65.4,44,54.82) rot=(0,0,1;0rad)
  Solid = true
  Symmetric = false
FEATURE [Part::MultiFuse] Fusion055  label="top008"
  Shapes = -> [Cut017,Cut018]
FEATURE [Part::Cut] Cut019  label="top009"
  Base = -> Fusion055
  Tool = -> Extrude020
FEATURE [App::MeasureDistance] Distance003  label="Distance: 71.95 mm"
  Distance = 71.9513
  P1 = (117,38,72)
  P2 = (117,38,0.0487319)
FEATURE [Sketcher::SketchObject] Sketch030
  FullyConstrained = true
  Placement = pos=(117,19,0) rot=(0.57735,0.57735,0.57735;2.0944rad)
  sketch-geometry (48):
    g0: LineSegment StartX=-49.19 StartY=69.25 StartZ=0 EndX=-49.19 EndY=66.25 EndZ=0
    g1: LineSegment StartX=-49.19 StartY=63.5 StartZ=0 EndX=-49.19 EndY=60.5 EndZ=0
    g2: LineSegment StartX=-49.19 StartY=57.75 StartZ=0 EndX=-49.19 EndY=54.75 EndZ=0
    g3: LineSegment StartX=-49.19 StartY=52 StartZ=0 EndX=-49.19 EndY=49 EndZ=0
    g4: LineSegment StartX=-49.19 StartY=46.25 StartZ=0 EndX=-49.19 EndY=43.25 EndZ=0
    g5: LineSegment StartX=-49.19 StartY=40.5 StartZ=0 EndX=-49.19 EndY=37.5 EndZ=0
    g6: LineSegment StartX=-49.19 StartY=34.5 StartZ=0 EndX=-49.19 EndY=31.5 EndZ=0
    g7: LineSegment StartX=-49.19 StartY=28.75 StartZ=0 EndX=-49.19 EndY=25.75 EndZ=0
    g8: LineSegment StartX=-49.19 StartY=23 StartZ=0 EndX=-49.19 EndY=20 EndZ=0
    g9: LineSegment StartX=-49.19 StartY=17.25 StartZ=0 EndX=-49.19 EndY=14.25 EndZ=0
    g10: LineSegment StartX=-49.19 StartY=11.5 StartZ=0 EndX=-49.19 EndY=8.5 EndZ=0
    g11: LineSegment StartX=-49.19 StartY=5.75 StartZ=0 EndX=-49.19 EndY=2.75 EndZ=0
    g12: ArcOfCircle CenterX=-1.5 CenterY=67.75 CenterZ=0 NormalX=0 NormalY=0 NormalZ=1 AngleXU=0 Radius=1.5 StartAngle=4.71239 EndAngle=7.85398
    g13: ArcOfCircle CenterX=-1.5 CenterY=62 CenterZ=0 NormalX=0 NormalY=0 NormalZ=1 AngleXU=0 Radius=1.5 StartAngle=4.71239 EndAngle=7.85398
    g14: ArcOfCircle CenterX=-1.5 CenterY=56.25 CenterZ=0 NormalX=0 NormalY=0 NormalZ=1 AngleXU=0 Radius=1.5 StartAngle=4.71239 EndAngle=7.85398
    g15: ArcOfCircle CenterX=-11.49 CenterY=50.5 CenterZ=0 NormalX=0 NormalY=0 NormalZ=1 AngleXU=0 Radius=1.5 StartAngle=4.71239 EndAngle=7.85398
    g16: ArcOfCircle CenterX=-16.28 CenterY=44.75 CenterZ=0 NormalX=0 NormalY=0 NormalZ=1 AngleXU=0 Radius=1.5 StartAngle=4.71239 EndAngle=7.85398
    g17: ArcOfCircle CenterX=-18.2337 CenterY=39 CenterZ=0 NormalX=0 NormalY=0 NormalZ=1 AngleXU=0 Radius=1.5 StartAngle=4.71485 EndAngle=7.85398
    g18: ArcOfCircle CenterX=-16.2837 CenterY=27.25 CenterZ=0 NormalX=0 NormalY=0 NormalZ=1 AngleXU=0 Radius=1.5 StartAngle=4.71485 EndAngle=7.85398
    g19: ArcOfCircle CenterX=-18.2337 CenterY=33 CenterZ=0 NormalX=0 NormalY=0 NormalZ=1 AngleXU=0 Radius=1.5 StartAngle=4.71485 EndAngle=7.85398
    g20: ArcOfCircle CenterX=-11.49 CenterY=21.5 CenterZ=0 NormalX=0 NormalY=0 NormalZ=1 AngleXU=0 Radius=1.5 StartAngle=4.71239 EndAngle=7.85398
    g21: ArcOfCircle CenterX=-1.5 CenterY=4.25 CenterZ=0 NormalX=0 NormalY=0 NormalZ=1 AngleXU=0 Radius=1.5 StartAngle=4.71239 EndAngle=7.85398
    g22: ArcOfCircle CenterX=-1.5 CenterY=10 CenterZ=0 NormalX=0 NormalY=0 NormalZ=1 AngleXU=0 Radius=1.5 StartAngle=4.71239 EndAngle=7.85398
    g23: ArcOfCircle CenterX=-1.5 CenterY=15.75 CenterZ=0 NormalX=0 NormalY=0 NormalZ=1 AngleXU=0 Radius=1.5 StartAngle=4.71239 EndAngle=7.85398
    g24: LineSegment StartX=-49.19 StartY=69.25 StartZ=0 EndX=-1.5 EndY=69.25 EndZ=0
    g25: LineSegment StartX=-49.19 StartY=66.25 StartZ=0 EndX=-1.5 EndY=66.25 EndZ=0
    g26: LineSegment StartX=-49.19 StartY=63.5 StartZ=0 EndX=-1.5 EndY=63.5 EndZ=0
    g27: LineSegment StartX=-49.19 StartY=60.5 StartZ=0 EndX=-1.5 EndY=60.5 EndZ=0
    g28: LineSegment StartX=-49.19 StartY=57.75 StartZ=0 EndX=-1.5 EndY=57.75 EndZ=0
    g29: LineSegment StartX=-49.19 StartY=54.75 StartZ=0 EndX=-1.5 EndY=54.75 EndZ=0
    g30: LineSegment StartX=-49.19 StartY=52 StartZ=0 EndX=-11.49 EndY=52 EndZ=0
    g31: LineSegment StartX=-49.19 StartY=49 StartZ=0 EndX=-11.49 EndY=49 EndZ=0
    g32: LineSegment StartX=-49.19 StartY=46.25 StartZ=0 EndX=-16.28 EndY=46.25 EndZ=0
    g33: LineSegment StartX=-49.19 StartY=43.25 StartZ=0 EndX=-16.28 EndY=43.25 EndZ=0
    g34: LineSegment StartX=-49.19 StartY=40.5 StartZ=0 EndX=-18.2337 EndY=40.5 EndZ=0
    g35: LineSegment StartX=-49.19 StartY=37.5 StartZ=0 EndX=-18.23 EndY=37.5 EndZ=0
    g36: LineSegment StartX=-49.19 StartY=34.5 StartZ=0 EndX=-18.2337 EndY=34.5 EndZ=0
    g37: LineSegment StartX=-49.19 StartY=31.5 StartZ=0 EndX=-18.23 EndY=31.5 EndZ=0
    g38: LineSegment StartX=-49.19 StartY=28.75 StartZ=0 EndX=-16.2837 EndY=28.75 EndZ=0
    g39: LineSegment StartX=-49.19 StartY=25.75 StartZ=0 EndX=-16.28 EndY=25.75 EndZ=0
    g40: LineSegment StartX=-49.19 StartY=23 StartZ=0 EndX=-11.49 EndY=23 EndZ=0
    g41: LineSegment StartX=-49.19 StartY=20 StartZ=0 EndX=-11.49 EndY=20 EndZ=0
    g42: LineSegment StartX=-49.19 StartY=17.25 StartZ=0 EndX=-1.5 EndY=17.25 EndZ=0
    g43: LineSegment StartX=-49.19 StartY=14.25 StartZ=0 EndX=-1.5 EndY=14.25 EndZ=0
    g44: LineSegment StartX=-49.19 StartY=11.5 StartZ=0 EndX=-1.5 EndY=11.5 EndZ=0
    g45: LineSegment StartX=-49.19 StartY=8.5 StartZ=0 EndX=-1.5 EndY=8.5 EndZ=0
    g46: LineSegment StartX=-49.19 StartY=5.75 StartZ=0 EndX=-1.5 EndY=5.75 EndZ=0
    g47: LineSegment StartX=-49.19 StartY=2.75 StartZ=0 EndX=-1.5 EndY=2.75 EndZ=0
  constraints (120):
    c: Vertical(g0)
    c: Distance(g0) = 3
    c: Block(g0)
    c: Vertical(g1)
    c: Distance(g1) = 3
    c: Vertical(g2)
    c: Equal(g0,g2) = 3
    c: Block(g2)
    c: Vertical(g3)
    c: Equal(g1,g3) = 3
    c: Vertical(g4)
    c: Equal(g0,g4) = 3
    c: Block(g4)
    c: Vertical(g5)
    c: Equal(g1,g5) = 3
    c: Vertical(g6)
    c: Equal(g0,g6) = 3
    c: Block(g6)
    c: Vertical(g7)
    c: Equal(g1,g7) = 3
    c: Vertical(g8)
    c: Equal(g0,g8) = 3
    c: Block(g8)
    c: Vertical(g9)
    c: Equal(g1,g9) = 3
    c: Vertical(g10)
    c: Equal(g0,g10) = 3
    c: Block(g10)
    c: Vertical(g11)
    c: Equal(g1,g11) = 3
    c: Block(g12)
    c: Block(g13)
    c: Block(g14)
    c: Block(g15)
    c: Block(g16)
    c: Block(g17)
    c: Block(g18)
    c: Block(g19)
    c: Block(g20)
    c: Block(g21)
    c: Block(g22)
    c: Block(g23)
    c: Block(g11)
    c: Block(g9)
    c: Block(g7)
    c: Block(g5)
    c: Block(g3)
    c: Block(g1)
    c: Coincident(g24,g0)
    c: Coincident(g24,g12)
    c: Horizontal(g24)
    c: Coincident(g25,g0)
    c: Coincident(g25,g12)
    c: Horizontal(g25)
    c: Coincident(g26,g1)
    c: Coincident(g26,g13)
    c: Horizontal(g26)
    c: Coincident(g27,g1)
    c: Coincident(g27,g13)
    c: Horizontal(g27)
    c: Coincident(g28,g2)
    c: Coincident(g28,g14)
    c: Horizontal(g28)
    c: Coincident(g29,g2)
    c: Coincident(g29,g14)
    c: Horizontal(g29)
    c: Coincident(g30,g3)
    c: Coincident(g30,g15)
    c: Horizontal(g30)
    c: Coincident(g31,g3)
    c: Coincident(g31,g15)
    c: Horizontal(g31)
    c: Coincident(g32,g4)
    c: Coincident(g32,g16)
    c: Horizontal(g32)
    c: Coincident(g33,g4)
    c: Coincident(g33,g16)
    c: Horizontal(g33)
    c: Coincident(g34,g5)
    c: Coincident(g34,g17)
    c: Horizontal(g34)
    c: Coincident(g35,g5)
    c: Coincident(g35,g17)
    c: Horizontal(g35)
    c: Coincident(g36,g6)
    c: Coincident(g36,g19)
    c: Horizontal(g36)
    c: Coincident(g37,g6)
    c: Coincident(g37,g19)
    c: Horizontal(g37)
    c: Coincident(g38,g7)
    c: Coincident(g38,g18)
    c: Horizontal(g38)
    c: Coincident(g39,g7)
    c: Coincident(g39,g18)
    c: Horizontal(g39)
    c: Coincident(g40,g8)
    c: Coincident(g40,g20)
    c: Horizontal(g40)
    c: Coincident(g41,g8)
    c: Coincident(g41,g20)
    c: Horizontal(g41)
    c: Coincident(g42,g9)
    c: Coincident(g42,g23)
    c: Horizontal(g42)
    c: Coincident(g43,g9)
    c: Coincident(g43,g23)
    c: Horizontal(g43)
    c: Coincident(g44,g10)
    c: Coincident(g44,g22)
    c: Horizontal(g44)
    c: Coincident(g45,g10)
    c: Coincident(g45,g22)
    c: Horizontal(g45)
    c: Coincident(g46,g11)
    c: Coincident(g46,g21)
    c: Horizontal(g46)
    c: Coincident(g47,g11)
    c: Coincident(g47,g21)
    c: Horizontal(g47)
FEATURE [Sketcher::SketchObject] Sketch031
  FullyConstrained = true
  Placement = pos=(117,19,0) rot=(0.57735,0.57735,0.57735;2.0944rad)
  sketch-geometry (24):
    g0: ArcOfCircle CenterX=-49.19 CenterY=67.75 CenterZ=0 NormalX=0 NormalY=0 NormalZ=1 AngleXU=0 Radius=1.5 StartAngle=1.5708 EndAngle=4.71239
    g1: ArcOfCircle CenterX=-49.19 CenterY=62 CenterZ=0 NormalX=0 NormalY=0 NormalZ=1 AngleXU=0 Radius=1.5 StartAngle=1.5708 EndAngle=4.71239
    g2: ArcOfCircle CenterX=-49.19 CenterY=56.25 CenterZ=0 NormalX=0 NormalY=0 NormalZ=1 AngleXU=0 Radius=1.5 StartAngle=1.5708 EndAngle=4.71239
    g3: ArcOfCircle CenterX=-49.19 CenterY=50.5 CenterZ=0 NormalX=0 NormalY=0 NormalZ=1 AngleXU=0 Radius=1.5 StartAngle=1.5708 EndAngle=4.71239
    g4: ArcOfCircle CenterX=-49.19 CenterY=44.75 CenterZ=0 NormalX=0 NormalY=0 NormalZ=1 AngleXU=0 Radius=1.5 StartAngle=1.5708 EndAngle=4.71239
    g5: ArcOfCircle CenterX=-49.19 CenterY=39 CenterZ=0 NormalX=0 NormalY=0 NormalZ=1 AngleXU=0 Radius=1.5 StartAngle=1.5708 EndAngle=4.71239
    g6: ArcOfCircle CenterX=-49.19 CenterY=33 CenterZ=0 NormalX=0 NormalY=0 NormalZ=1 AngleXU=0 Radius=1.5 StartAngle=1.5708 EndAngle=4.71239
    g7: ArcOfCircle CenterX=-49.19 CenterY=27.25 CenterZ=0 NormalX=0 NormalY=0 NormalZ=1 AngleXU=0 Radius=1.5 StartAngle=1.5708 EndAngle=4.71239
    g8: ArcOfCircle CenterX=-49.19 CenterY=21.5 CenterZ=0 NormalX=0 NormalY=0 NormalZ=1 AngleXU=0 Radius=1.5 StartAngle=1.5708 EndAngle=4.71239
    g9: ArcOfCircle CenterX=-49.19 CenterY=15.75 CenterZ=0 NormalX=0 NormalY=0 NormalZ=1 AngleXU=0 Radius=1.5 StartAngle=1.5708 EndAngle=4.71239
    g10: ArcOfCircle CenterX=-49.19 CenterY=10 CenterZ=0 NormalX=0 NormalY=0 NormalZ=1 AngleXU=0 Radius=1.5 StartAngle=1.5708 EndAngle=4.71239
    g11: ArcOfCircle CenterX=-49.19 CenterY=4.25 CenterZ=0 NormalX=0 NormalY=0 NormalZ=1 AngleXU=0 Radius=1.5 StartAngle=1.5708 EndAngle=4.71239
    g12: LineSegment StartX=-49.19 StartY=69.25 StartZ=0 EndX=-49.19 EndY=66.25 EndZ=0
    g13: LineSegment StartX=-49.19 StartY=63.5 StartZ=0 EndX=-49.19 EndY=60.5 EndZ=0
    g14: LineSegment StartX=-49.19 StartY=57.75 StartZ=0 EndX=-49.19 EndY=54.75 EndZ=0
    g15: LineSegment StartX=-49.19 StartY=52 StartZ=0 EndX=-49.19 EndY=49 EndZ=0
    g16: LineSegment StartX=-49.19 StartY=46.25 StartZ=0 EndX=-49.19 EndY=43.25 EndZ=0
    g17: LineSegment StartX=-49.19 StartY=40.5 StartZ=0 EndX=-49.19 EndY=37.5 EndZ=0
    g18: LineSegment StartX=-49.19 StartY=34.5 StartZ=0 EndX=-49.19 EndY=31.5 EndZ=0
    g19: LineSegment StartX=-49.19 StartY=28.75 StartZ=0 EndX=-49.19 EndY=25.75 EndZ=0
    g20: LineSegment StartX=-49.19 StartY=23 StartZ=0 EndX=-49.19 EndY=20 EndZ=0
    g21: LineSegment StartX=-49.19 StartY=17.25 StartZ=0 EndX=-49.19 EndY=14.25 EndZ=0
    g22: LineSegment StartX=-49.19 StartY=11.5 StartZ=0 EndX=-49.19 EndY=8.5 EndZ=0
    g23: LineSegment StartX=-49.19 StartY=5.75 StartZ=0 EndX=-49.19 EndY=2.75 EndZ=0
  constraints (48):
    c: Block(g0)
    c: Block(g1)
    c: Block(g2)
    c: Block(g3)
    c: Block(g4)
    c: Block(g5)
    c: Block(g6)
    c: Block(g7)
    c: Block(g8)
    c: Block(g9)
    c: Block(g10)
    c: Block(g11)
    c: Coincident(g12,g0)
    c: Coincident(g12,g0)
    c: Vertical(g12)
    c: Vertical(g13)
    c: Coincident(g13,g1)
    c: Vertical(g14)
    c: Coincident(g14,g2)
    c: Vertical(g15)
    c: Coincident(g15,g3)
    c: Vertical(g16)
    c: Coincident(g16,g4)
    c: Vertical(g17)
    c: Coincident(g17,g5)
    c: Vertical(g18)
    c: Coincident(g18,g6)
    c: Vertical(g19)
    c: Coincident(g19,g7)
    c: Vertical(g20)
    c: Coincident(g20,g8)
    c: Vertical(g21)
    c: Coincident(g21,g9)
    c: Vertical(g22)
    c: Coincident(g22,g10)
    c: Vertical(g23)
    c: Coincident(g23,g11)
    c: Block(g23)
    c: Block(g22)
    c: Block(g21)
    c: Block(g20)
    c: Block(g13)
    c: Block(g14)
    c: Block(g15)
    c: Block(g16)
    c: Block(g17)
    c: Block(g18)
    c: Block(g19)
FEATURE [Part::Extrusion] Extrude022
  Base = -> Sketch030
  Dir = (1,-2e-16,2e-16)
  DirMode = 2
  FaceMakerClass = Part::FaceMakerBullseye
  LengthFwd = 19
  LengthRev = 0
  Placement = pos=(-19,0,0) rot=(0,0,1;0rad)
  Solid = true
  Symmetric = false
FEATURE [Part::Fillet] Fillet022
  Base = -> Extrude022
  Edges = 24 edges r=1.49: [Edge6,Edge11,Edge18,Edge23,Edge30,Edge35,Edge42,Edge47,Edge54,Edge59,Edge66,Edge71,Edge78,Edge83,Edge90,Edge95,Edge102,Edge107,Edge114,Edge119,Edge126,Edge131,Edge138,Edge143]
FEATURE [Part::Cut] Cut020  label="top010"
  Base = -> Cut019
  Tool = -> Fillet022
FEATURE [Sketcher::SketchObject] Sketch032
  FullyConstrained = true
  Placement = pos=(117,19,0) rot=(0.57735,0.57735,0.57735;2.0944rad)
  sketch-geometry (48):
    g0: LineSegment StartX=-49.19 StartY=69.25 StartZ=0 EndX=-49.19 EndY=66.25 EndZ=0
    g1: LineSegment StartX=-49.19 StartY=63.5 StartZ=0 EndX=-49.19 EndY=60.5 EndZ=0
    g2: LineSegment StartX=-49.19 StartY=57.75 StartZ=0 EndX=-49.19 EndY=54.75 EndZ=0
    g3: LineSegment StartX=-49.19 StartY=52 StartZ=0 EndX=-49.19 EndY=49 EndZ=0
    g4: LineSegment StartX=-49.19 StartY=46.25 StartZ=0 EndX=-49.19 EndY=43.25 EndZ=0
    g5: LineSegment StartX=-49.19 StartY=40.5 StartZ=0 EndX=-49.19 EndY=37.5 EndZ=0
    g6: LineSegment StartX=-49.19 StartY=34.5 StartZ=0 EndX=-49.19 EndY=31.5 EndZ=0
    g7: LineSegment StartX=-49.19 StartY=28.75 StartZ=0 EndX=-49.19 EndY=25.75 EndZ=0
    g8: LineSegment StartX=-49.19 StartY=23 StartZ=0 EndX=-49.19 EndY=20 EndZ=0
    g9: LineSegment StartX=-49.19 StartY=17.25 StartZ=0 EndX=-49.19 EndY=14.25 EndZ=0
    g10: LineSegment StartX=-49.19 StartY=11.5 StartZ=0 EndX=-49.19 EndY=8.5 EndZ=0
    g11: LineSegment StartX=-49.19 StartY=5.75 StartZ=0 EndX=-49.19 EndY=2.75 EndZ=0
    g12: ArcOfCircle CenterX=-1.5 CenterY=67.75 CenterZ=0 NormalX=0 NormalY=0 NormalZ=1 AngleXU=0 Radius=1.5 StartAngle=4.71239 EndAngle=7.85398
    g13: ArcOfCircle CenterX=-1.5 CenterY=62 CenterZ=0 NormalX=0 NormalY=0 NormalZ=1 AngleXU=0 Radius=1.5 StartAngle=4.71239 EndAngle=7.85398
    g14: ArcOfCircle CenterX=-1.5 CenterY=56.25 CenterZ=0 NormalX=0 NormalY=0 NormalZ=1 AngleXU=0 Radius=1.5 StartAngle=4.71239 EndAngle=7.85398
    g15: ArcOfCircle CenterX=-11.49 CenterY=50.5 CenterZ=0 NormalX=0 NormalY=0 NormalZ=1 AngleXU=0 Radius=1.5 StartAngle=4.71239 EndAngle=7.85398
    g16: ArcOfCircle CenterX=-16.28 CenterY=44.75 CenterZ=0 NormalX=0 NormalY=0 NormalZ=1 AngleXU=0 Radius=1.5 StartAngle=4.71239 EndAngle=7.85398
    g17: ArcOfCircle CenterX=-18.2337 CenterY=39 CenterZ=0 NormalX=0 NormalY=0 NormalZ=1 AngleXU=0 Radius=1.5 StartAngle=4.71485 EndAngle=7.85398
    g18: ArcOfCircle CenterX=-16.2837 CenterY=27.25 CenterZ=0 NormalX=0 NormalY=0 NormalZ=1 AngleXU=0 Radius=1.5 StartAngle=4.71485 EndAngle=7.85398
    g19: ArcOfCircle CenterX=-18.2337 CenterY=33 CenterZ=0 NormalX=0 NormalY=0 NormalZ=1 AngleXU=0 Radius=1.5 StartAngle=4.71485 EndAngle=7.85398
    g20: ArcOfCircle CenterX=-11.49 CenterY=21.5 CenterZ=0 NormalX=0 NormalY=0 NormalZ=1 AngleXU=0 Radius=1.5 StartAngle=4.71239 EndAngle=7.85398
    g21: ArcOfCircle CenterX=-1.5 CenterY=4.25 CenterZ=0 NormalX=0 NormalY=0 NormalZ=1 AngleXU=0 Radius=1.5 StartAngle=4.71239 EndAngle=7.85398
    g22: ArcOfCircle CenterX=-1.5 CenterY=10 CenterZ=0 NormalX=0 NormalY=0 NormalZ=1 AngleXU=0 Radius=1.5 StartAngle=4.71239 EndAngle=7.85398
    g23: ArcOfCircle CenterX=-1.5 CenterY=15.75 CenterZ=0 NormalX=0 NormalY=0 NormalZ=1 AngleXU=0 Radius=1.5 StartAngle=4.71239 EndAngle=7.85398
    g24: LineSegment StartX=-49.19 StartY=69.25 StartZ=0 EndX=-1.5 EndY=69.25 EndZ=0
    g25: LineSegment StartX=-49.19 StartY=66.25 StartZ=0 EndX=-1.5 EndY=66.25 EndZ=0
    g26: LineSegment StartX=-49.19 StartY=63.5 StartZ=0 EndX=-1.5 EndY=63.5 EndZ=0
    g27: LineSegment StartX=-49.19 StartY=60.5 StartZ=0 EndX=-1.5 EndY=60.5 EndZ=0
    g28: LineSegment StartX=-49.19 StartY=57.75 StartZ=0 EndX=-1.5 EndY=57.75 EndZ=0
    g29: LineSegment StartX=-49.19 StartY=54.75 StartZ=0 EndX=-1.5 EndY=54.75 EndZ=0
    g30: LineSegment StartX=-49.19 StartY=52 StartZ=0 EndX=-11.49 EndY=52 EndZ=0
    g31: LineSegment StartX=-49.19 StartY=49 StartZ=0 EndX=-11.49 EndY=49 EndZ=0
    g32: LineSegment StartX=-49.19 StartY=46.25 StartZ=0 EndX=-16.28 EndY=46.25 EndZ=0
    g33: LineSegment StartX=-49.19 StartY=43.25 StartZ=0 EndX=-16.28 EndY=43.25 EndZ=0
    g34: LineSegment StartX=-49.19 StartY=40.5 StartZ=0 EndX=-18.2337 EndY=40.5 EndZ=0
    g35: LineSegment StartX=-49.19 StartY=37.5 StartZ=0 EndX=-18.23 EndY=37.5 EndZ=0
    g36: LineSegment StartX=-49.19 StartY=34.5 StartZ=0 EndX=-18.2337 EndY=34.5 EndZ=0
    g37: LineSegment StartX=-49.19 StartY=31.5 StartZ=0 EndX=-18.23 EndY=31.5 EndZ=0
    g38: LineSegment StartX=-49.19 StartY=28.75 StartZ=0 EndX=-16.2837 EndY=28.75 EndZ=0
    g39: LineSegment StartX=-49.19 StartY=25.75 StartZ=0 EndX=-16.28 EndY=25.75 EndZ=0
    g40: LineSegment StartX=-49.19 StartY=23 StartZ=0 EndX=-11.49 EndY=23 EndZ=0
    g41: LineSegment StartX=-49.19 StartY=20 StartZ=0 EndX=-11.49 EndY=20 EndZ=0
    g42: LineSegment StartX=-49.19 StartY=17.25 StartZ=0 EndX=-1.5 EndY=17.25 EndZ=0
    g43: LineSegment StartX=-49.19 StartY=14.25 StartZ=0 EndX=-1.5 EndY=14.25 EndZ=0
    g44: LineSegment StartX=-49.19 StartY=11.5 StartZ=0 EndX=-1.5 EndY=11.5 EndZ=0
    g45: LineSegment StartX=-49.19 StartY=8.5 StartZ=0 EndX=-1.5 EndY=8.5 EndZ=0
    g46: LineSegment StartX=-49.19 StartY=5.75 StartZ=0 EndX=-1.5 EndY=5.75 EndZ=0
    g47: LineSegment StartX=-49.19 StartY=2.75 StartZ=0 EndX=-1.5 EndY=2.75 EndZ=0
  constraints (120):
    c: Vertical(g0)
    c: Distance(g0) = 3
    c: Block(g0)
    c: Vertical(g1)
    c: Distance(g1) = 3
    c: Vertical(g2)
    c: Equal(g0,g2) = 3
    c: Block(g2)
    c: Vertical(g3)
    c: Equal(g1,g3) = 3
    c: Vertical(g4)
    c: Equal(g0,g4) = 3
    c: Block(g4)
    c: Vertical(g5)
    c: Equal(g1,g5) = 3
    c: Vertical(g6)
    c: Equal(g0,g6) = 3
    c: Block(g6)
    c: Vertical(g7)
    c: Equal(g1,g7) = 3
    c: Vertical(g8)
    c: Equal(g0,g8) = 3
    c: Block(g8)
    c: Vertical(g9)
    c: Equal(g1,g9) = 3
    c: Vertical(g10)
    c: Equal(g0,g10) = 3
    c: Block(g10)
    c: Vertical(g11)
    c: Equal(g1,g11) = 3
    c: Block(g12)
    c: Block(g13)
    c: Block(g14)
    c: Block(g15)
    c: Block(g16)
    c: Block(g17)
    c: Block(g18)
    c: Block(g19)
    c: Block(g20)
    c: Block(g21)
    c: Block(g22)
    c: Block(g23)
    c: Block(g11)
    c: Block(g9)
    c: Block(g7)
    c: Block(g5)
    c: Block(g3)
    c: Block(g1)
    c: Coincident(g24,g0)
    c: Coincident(g24,g12)
    c: Horizontal(g24)
    c: Coincident(g25,g0)
    c: Coincident(g25,g12)
    c: Horizontal(g25)
    c: Coincident(g26,g1)
    c: Coincident(g26,g13)
    c: Horizontal(g26)
    c: Coincident(g27,g1)
    c: Coincident(g27,g13)
    c: Horizontal(g27)
    c: Coincident(g28,g2)
    c: Coincident(g28,g14)
    c: Horizontal(g28)
    c: Coincident(g29,g2)
    c: Coincident(g29,g14)
    c: Horizontal(g29)
    c: Coincident(g30,g3)
    c: Coincident(g30,g15)
    c: Horizontal(g30)
    c: Coincident(g31,g3)
    c: Coincident(g31,g15)
    c: Horizontal(g31)
    c: Coincident(g32,g4)
    c: Coincident(g32,g16)
    c: Horizontal(g32)
    c: Coincident(g33,g4)
    c: Coincident(g33,g16)
    c: Horizontal(g33)
    c: Coincident(g34,g5)
    c: Coincident(g34,g17)
    c: Horizontal(g34)
    c: Coincident(g35,g5)
    c: Coincident(g35,g17)
    c: Horizontal(g35)
    c: Coincident(g36,g6)
    c: Coincident(g36,g19)
    c: Horizontal(g36)
    c: Coincident(g37,g6)
    c: Coincident(g37,g19)
    c: Horizontal(g37)
    c: Coincident(g38,g7)
    c: Coincident(g38,g18)
    c: Horizontal(g38)
    c: Coincident(g39,g7)
    c: Coincident(g39,g18)
    c: Horizontal(g39)
    c: Coincident(g40,g8)
    c: Coincident(g40,g20)
    c: Horizontal(g40)
    c: Coincident(g41,g8)
    c: Coincident(g41,g20)
    c: Horizontal(g41)
    c: Coincident(g42,g9)
    c: Coincident(g42,g23)
    c: Horizontal(g42)
    c: Coincident(g43,g9)
    c: Coincident(g43,g23)
    c: Horizontal(g43)
    c: Coincident(g44,g10)
    c: Coincident(g44,g22)
    c: Horizontal(g44)
    c: Coincident(g45,g10)
    c: Coincident(g45,g22)
    c: Horizontal(g45)
    c: Coincident(g46,g11)
    c: Coincident(g46,g21)
    c: Horizontal(g46)
    c: Coincident(g47,g11)
    c: Coincident(g47,g21)
    c: Horizontal(g47)
FEATURE [Part::Extrusion] Extrude023
  Base = -> Sketch032
  Dir = (1,-2e-16,2e-16)
  DirMode = 2
  FaceMakerClass = Part::FaceMakerBullseye
  LengthFwd = 19
  LengthRev = 0
  Placement = pos=(-19,0,0) rot=(0,0,1;0rad)
  Solid = true
  Symmetric = false
FEATURE [Part::Fillet] Fillet023
  Base = -> Extrude023
  Edges = <same value as first occurrence — deduplicated (x6 in doc)>
  Placement = pos=(0,0.05,0) rot=(0,0,1;0rad)
FEATURE [Part::Cut] Cut014  label="bottom003"
  Base = -> Cut007
  Tool = -> Fusion047
FEATURE [Part::Cut] Cut021  label="bottom004"
  Base = -> Cut014
  Tool = -> Fillet023
FEATURE [Sketcher::SketchObject] Sketch033
  FullyConstrained = true
  Placement = pos=(117,19,0) rot=(0.57735,0.57735,0.57735;2.0944rad)
  sketch-geometry (8):
    g0: LineSegment StartX=-49.19 StartY=69.25 StartZ=0 EndX=-49.19 EndY=66.25 EndZ=0
    g1: LineSegment StartX=-49.19 StartY=5.75 StartZ=0 EndX=-49.19 EndY=2.75 EndZ=0
    g2: ArcOfCircle CenterX=-1.5 CenterY=67.75 CenterZ=0 NormalX=0 NormalY=0 NormalZ=1 AngleXU=0 Radius=1.5 StartAngle=4.71239 EndAngle=7.85398
    g3: ArcOfCircle CenterX=-1.5 CenterY=4.25 CenterZ=0 NormalX=0 NormalY=0 NormalZ=1 AngleXU=0 Radius=1.5 StartAngle=4.71239 EndAngle=7.85398
    g4: LineSegment StartX=-49.19 StartY=69.25 StartZ=0 EndX=-1.5 EndY=69.25 EndZ=0
    g5: LineSegment StartX=-49.19 StartY=66.25 StartZ=0 EndX=-1.5 EndY=66.25 EndZ=0
    g6: LineSegment StartX=-49.19 StartY=5.75 StartZ=0 EndX=-1.5 EndY=5.75 EndZ=0
    g7: LineSegment StartX=-49.19 StartY=2.75 StartZ=0 EndX=-1.5 EndY=2.75 EndZ=0
  constraints (19):
    c: Vertical(g0)
    c: Distance(g0) = 3
    c: Block(g0)
    c: Vertical(g1)
    c: Block(g2)
    c: Block(g3)
    c: Block(g1)
    c: Coincident(g4,g0)
    c: Coincident(g4,g2)
    c: Horizontal(g4)
    c: Coincident(g5,g0)
    c: Coincident(g5,g2)
    c: Horizontal(g5)
    c: Coincident(g6,g1)
    c: Coincident(g6,g3)
    c: Horizontal(g6)
    c: Coincident(g7,g1)
    c: Coincident(g7,g3)
    c: Horizontal(g7)
FEATURE [Sketcher::SketchObject] Sketch034
  FullyConstrained = true
  Placement = pos=(117,19,0) rot=(0.57735,0.57735,0.57735;2.0944rad)
  sketch-geometry (8):
    g0: LineSegment StartX=-49.19 StartY=63.5 StartZ=0 EndX=-49.19 EndY=60.5 EndZ=0
    g1: LineSegment StartX=-49.19 StartY=11.5 StartZ=0 EndX=-49.19 EndY=8.5 EndZ=0
    g2: ArcOfCircle CenterX=-1.5 CenterY=62 CenterZ=0 NormalX=0 NormalY=0 NormalZ=1 AngleXU=0 Radius=1.5 StartAngle=4.71239 EndAngle=7.85398
    g3: ArcOfCircle CenterX=-1.5 CenterY=10 CenterZ=0 NormalX=0 NormalY=0 NormalZ=1 AngleXU=0 Radius=1.5 StartAngle=4.71239 EndAngle=7.85398
    g4: LineSegment StartX=-49.19 StartY=63.5 StartZ=0 EndX=-1.5 EndY=63.5 EndZ=0
    g5: LineSegment StartX=-49.19 StartY=60.5 StartZ=0 EndX=-1.5 EndY=60.5 EndZ=0
    g6: LineSegment StartX=-49.19 StartY=11.5 StartZ=0 EndX=-1.5 EndY=11.5 EndZ=0
    g7: LineSegment StartX=-49.19 StartY=8.5 StartZ=0 EndX=-1.5 EndY=8.5 EndZ=0
  constraints (19):
    c: Vertical(g0)
    c: Distance(g0) = 3
    c: Vertical(g1)
    c: Block(g1)
    c: Block(g2)
    c: Block(g3)
    c: Block(g0)
    c: Coincident(g4,g0)
    c: Coincident(g4,g2)
    c: Horizontal(g4)
    c: Coincident(g5,g0)
    c: Coincident(g5,g2)
    c: Horizontal(g5)
    c: Coincident(g6,g1)
    c: Coincident(g6,g3)
    c: Horizontal(g6)
    c: Coincident(g7,g1)
    c: Coincident(g7,g3)
    c: Horizontal(g7)
FEATURE [Part::Extrusion] Extrude024
  Base = -> Sketch033
  Dir = (1,0,0)
  DirMode = 2
  FaceMakerClass = Part::FaceMakerBullseye
  LengthFwd = 10
  LengthRev = 0
  Solid = true
  Symmetric = false
FEATURE [Part::Extrusion] Extrude025
  Base = -> Sketch034
  Dir = (1,0,0)
  DirMode = 2
  FaceMakerClass = Part::FaceMakerBullseye
  LengthFwd = 10
  LengthRev = 0
  Solid = true
  Symmetric = false
FEATURE [Part::Fillet] Fillet024  label="removeFromtMoreFrontCaseScrewRetainers"
  Base = -> Extrude024
  Edges = 4 edges r=1.49: [Edge6,Edge11,Edge18,Edge23]
  Placement = pos=(-11,0,0) rot=(0,0,1;0rad)
FEATURE [Part::Fillet] Fillet025  label="removeFromtMoreFrontCaseScrewRetainers001"
  Base = -> Extrude025
  Edges = 4 edges r=1.49: [Edge6,Edge11,Edge18,Edge23]
  Placement = pos=(-19,0,0) rot=(0,0,1;0rad)
FEATURE [Part::Cut] Cut022
  Base = -> Cut015
  Tool = -> Fillet025
FEATURE [Part::Cut] Cut023  label="screwRetainers"
  Base = -> Cut022
  Tool = -> Fillet024
FEATURE [Part::MultiFuse] Fusion056  label="bottom005"
  Shapes = -> [Fusion044,Cut021]
FEATURE [Part::MultiFuse] Fusion057  label="casePillars001"
  Shapes = -> [Cut016,Fusion052]
FEATURE [Part::MultiFuse] Fusion058  label="bottom006"
  Shapes = -> [Fusion056,Cut023]
FEATURE [Part::MultiFuse] Fusion059  label="bottom007"
  Shapes = -> [Fusion058,Fillet005]
FEATURE [Part::MultiFuse] Fusion060  label="bottom008"
  Shapes = -> [Fusion059,Fusion]
FEATURE [Part::MultiFuse] Fusion061  label="top011"
  Shapes = -> [Cut006,Cut020]
FEATURE [Part::MultiFuse] Fusion062  label="top012"
  Shapes = -> [Fusion057,Fusion061]
FEATURE [Sketcher::SketchObject] Sketch035  label="topSketch007"
  FullyConstrained = true
  sketch-geometry (6):
    g0: LineSegment StartX=19 StartY=38 StartZ=0 EndX=117 EndY=38 EndZ=0
    g1: ArcOfCircle CenterX=19 CenterY=19 CenterZ=0 NormalX=0 NormalY=0 NormalZ=1 AngleXU=0 Radius=19 StartAngle=1.5708 EndAngle=3.14159
    g2: LineSegment StartX=117 StartY=38 StartZ=0 EndX=117 EndY=19 EndZ=0
    g3: LineSegment StartX=98 StartY=1.0161e-12 StartZ=0 EndX=5.22862e-06 EndY=1.0161e-12 EndZ=0
    g4: LineSegment StartX=5.22862e-06 StartY=19 StartZ=0 EndX=5.22862e-06 EndY=1.0161e-12 EndZ=0
    g5: ArcOfCircle CenterX=98 CenterY=19 CenterZ=0 NormalX=0 NormalY=0 NormalZ=1 AngleXU=0 Radius=19 StartAngle=4.71239 EndAngle=6.28319
  constraints (16):
    c: Horizontal(g0)
    c: Distance(g0) = 98
    c: Coincident(g1,g0)
    c: Block(g1)
    c: Coincident(g2,g0)
    c: Vertical(g2)
    c: Distance(g2) = 19
    c: Horizontal(g3)
    c: Coincident(g4,g1)
    c: Vertical(g4)
    c: Coincident(g3,g4)
    c: Block(g3)
    c: Coincident(g5,g2)
    c: Coincident(g5,g3)
    c: Block(g0)
    c: Block(g5)
FEATURE [Part::Extrusion] Extrude026  label="sideA001"
  Base = -> Sketch035
  Dir = (0,0,1)
  DirMode = 2
  FaceMakerClass = Part::FaceMakerBullseye
  LengthFwd = 3
  LengthRev = 0
  Placement = pos=(0,0,-2.7) rot=(0,0,1;0rad)
  Solid = true
  Symmetric = false
FEATURE [Sketcher::SketchObject] Sketch036  label="topSketch008"
  FullyConstrained = true
  sketch-geometry (6):
    g0: LineSegment StartX=19 StartY=38 StartZ=0 EndX=117 EndY=38 EndZ=0
    g1: ArcOfCircle CenterX=19 CenterY=19 CenterZ=0 NormalX=0 NormalY=0 NormalZ=1 AngleXU=0 Radius=19 StartAngle=1.5708 EndAngle=3.14159
    g2: LineSegment StartX=117 StartY=38 StartZ=0 EndX=117 EndY=19 EndZ=0
    g3: LineSegment StartX=98 StartY=1.0161e-12 StartZ=0 EndX=5.22862e-06 EndY=1.0161e-12 EndZ=0
    g4: LineSegment StartX=5.22862e-06 StartY=19 StartZ=0 EndX=5.22862e-06 EndY=1.0161e-12 EndZ=0
    g5: ArcOfCircle CenterX=98 CenterY=19 CenterZ=0 NormalX=0 NormalY=0 NormalZ=1 AngleXU=0 Radius=19 StartAngle=4.71239 EndAngle=6.28319
  constraints (16):
    c: Horizontal(g0)
    c: Distance(g0) = 98
    c: Coincident(g1,g0)
    c: Block(g1)
    c: Coincident(g2,g0)
    c: Vertical(g2)
    c: Distance(g2) = 19
    c: Horizontal(g3)
    c: Coincident(g4,g1)
    c: Vertical(g4)
    c: Coincident(g3,g4)
    c: Block(g3)
    c: Coincident(g5,g2)
    c: Coincident(g5,g3)
    c: Block(g0)
    c: Block(g5)
FEATURE [Part::Extrusion] Extrude027  label="sideB001"
  Base = -> Sketch036
  Dir = (0,0,1)
  DirMode = 2
  FaceMakerClass = Part::FaceMakerBullseye
  LengthFwd = 3
  LengthRev = 0
  Placement = pos=(0,0,71.7) rot=(0,0,1;0rad)
  Solid = true
  Symmetric = false
FEATURE [Part::MultiFuse] Fusion064  label="removeFromBottom"
  Shapes = -> [Extrude026,Extrude027]
FEATURE [Part::Cut] Cut024  label="bottom009"
  Base = -> Fusion060
  Tool = -> Fusion064
FEATURE [Sketcher::SketchObject] Sketch037  label="topSketch009"
  FullyConstrained = true
  sketch-geometry (8):
    g0: ArcOfCircle CenterX=19 CenterY=19.1201 CenterZ=0 NormalX=0 NormalY=0 NormalZ=1 AngleXU=0 Radius=18.8799 StartAngle=1.5708 EndAngle=3.14793
    g1: LineSegment StartX=0.120501 StartY=19.0004 StartZ=0 EndX=0.120501 EndY=0.000382114 EndZ=0
    g2: LineSegment StartX=19 StartY=38 StartZ=0 EndX=124 EndY=38 EndZ=0
    g3: LineSegment StartX=0.120501 StartY=0.000382114 StartZ=0 EndX=105.121 EndY=0.000382114 EndZ=0
    g4: LineSegment StartX=124 StartY=38 StartZ=0 EndX=125.616 EndY=38 EndZ=0
    g5: LineSegment StartX=105.121 StartY=0.000382114 StartZ=0 EndX=106.736 EndY=0.000382114 EndZ=0
    g6: ArcOfCircle CenterX=106.616 CenterY=19 CenterZ=0 NormalX=0 NormalY=0 NormalZ=1 AngleXU=0 Radius=19 StartAngle=4.71873 EndAngle=6.28319
    g7: LineSegment StartX=125.616 StartY=38 StartZ=0 EndX=125.616 EndY=19 EndZ=0
  constraints (21):
    c: Block(g0)
    c: Coincident(g1,g0)
    c: Vertical(g1)
    c: Horizontal(g2)
    c: Distance(g2) = 105
    c: Coincident(g2,g0)
    c: Distance(g1) = 19
    c: Coincident(g3,g1)
    c: Horizontal(g3)
    c: Distance(g3) = 105
    c: Coincident(g4,g2)
    c: Horizontal(g4)
    c: Distance(g4) = 1.61553
    c: Horizontal(g5)
    c: Equal(g4,g5) = 1.61553
    c: Coincident(g5,g3)
    c: Block(g6)
    c: Coincident(g6,g5)
    c: Coincident(g7,g4)
    c: Coincident(g7,g6)
    c: Vertical(g7)
FEATURE [Part::Extrusion] Extrude028  label="sideB"
  Base = -> Sketch037
  Dir = (0,0,1)
  DirMode = 2
  FaceMakerClass = Part::FaceMakerBullseye
  LengthFwd = 3
  LengthRev = 0
  Placement = pos=(0,0,72) rot=(0,0,1;0rad)
  Solid = true
  Symmetric = false
FEATURE [Sketcher::SketchObject] Sketch038  label="topSketch010"
  FullyConstrained = true
  sketch-geometry (22):
    g0: LineSegment StartX=5.21097e-06 StartY=3 StartZ=0 EndX=5.21097e-06 EndY=19 EndZ=0
    g1: ArcOfCircle CenterX=19 CenterY=19 CenterZ=0 NormalX=0 NormalY=0 NormalZ=1 AngleXU=0 Radius=19 StartAngle=1.5708 EndAngle=3.14159
    g2: ArcOfCircle CenterX=19 CenterY=19 CenterZ=0 NormalX=0 NormalY=0 NormalZ=1 AngleXU=0 Radius=16 StartAngle=1.5708 EndAngle=3.14159
    g3: LineSegment StartX=114 StartY=35 StartZ=0 EndX=19 EndY=35 EndZ=0
    g4: LineSegment StartX=5.21097e-06 StartY=3 StartZ=0 EndX=5.21097e-06 EndY=0 EndZ=0
    g5: LineSegment StartX=3 StartY=0 StartZ=0 EndX=5.21097e-06 EndY=0 EndZ=0
    g6: LineSegment StartX=3 StartY=19 StartZ=0 EndX=3 EndY=0 EndZ=0
    g7: LineSegment StartX=19 StartY=38 StartZ=0 EndX=124 EndY=38 EndZ=0
    g8: Circle CenterX=119 CenterY=35 CenterZ=0 NormalX=0 NormalY=0 NormalZ=1 AngleXU=0 Radius=1
    g9: Circle CenterX=121 CenterY=35 CenterZ=0 NormalX=0 NormalY=0 NormalZ=1 AngleXU=0 Radius=1
    g10: Circle CenterX=121 CenterY=33 CenterZ=0 NormalX=0 NormalY=0 NormalZ=1 AngleXU=0 Radius=1
    g11: BSplineCurve PolesCount=3 KnotsCount=2 Degree=2 IsPeriodic=0
    g12: GeomPoint X=119 Y=35 Z=0
    g13: GeomPoint X=121 Y=33 Z=0
    g14: LineSegment StartX=119 StartY=35 StartZ=0 EndX=114 EndY=35 EndZ=0
    g15: ArcOfCircle CenterX=105 CenterY=19 CenterZ=0 NormalX=0 NormalY=0 NormalZ=1 AngleXU=0 Radius=16 StartAngle=5.60905 EndAngle=6.28319
    g16: LineSegment StartX=121 StartY=33 StartZ=0 EndX=121 EndY=19 EndZ=0
    g17: LineSegment StartX=117.5 StartY=9.01251 StartZ=0 EndX=121.163 EndY=9.0125 EndZ=0
    g18: ArcOfCircle CenterX=105 CenterY=19 CenterZ=0 NormalX=0 NormalY=0 NormalZ=1 AngleXU=0 Radius=20.6155 StartAngle=5.7297 EndAngle=6.28319
    g19: LineSegment StartX=121.163 StartY=9.0125 StartZ=0 EndX=122.538 EndY=8.16329 EndZ=0
    g20: LineSegment StartX=124 StartY=38 StartZ=0 EndX=125.616 EndY=38 EndZ=0
    g21: LineSegment StartX=125.616 StartY=19 StartZ=0 EndX=125.616 EndY=38 EndZ=0
  constraints (49):
    c: Vertical(g0)
    c: Block(g0)
    c: Coincident(g1,g0)
    c: Block(g1)
    c: Coincident(g2,g1)
    c: Block(g2)
    c: Coincident(g3,g2)
    c: Horizontal(g3)
    c: Tangent(g3,g2)
    c: Coincident(g4,g0)
    c: Distance(g4) = 3
    c: Vertical(g4)
    c: Coincident(g5,g4)
    c: Horizontal(g5)
    c: Coincident(g6,g2)
    c: Coincident(g6,g5)
    c: Vertical(g6)
    c: Horizontal(g7)
    c: Distance(g7) = 105
    c: Coincident(g7,g1)
    c: Block(g3)
    c: Weight(g8) = 1
    c: Equal(g8,g9)
    c: Equal(g8,g10)
    c: InternalAlignment(g8,g11)
    c: InternalAlignment(g9,g11)
    c: InternalAlignment(g10,g11)
    c: InternalAlignment(g12,g11)
    c: InternalAlignment(g13,g11)
    c: Block(g11)
    c: Coincident(g14,g11)
    c: Coincident(g14,g3)
    c: Horizontal(g14)
    c: Block(g15)
    c: Coincident(g16,g11)
    c: Coincident(g16,g15)
    c: Vertical(g16)
    c: Distance(g16) = 14
    c: Coincident(g17,g15)
    c: Block(g18)
    c: Coincident(g19,g18)
    c: Coincident(g20,g7)
    c: Horizontal(g20)
    c: Vertical(g21)
    c: Coincident(g20,g21)
    c: Block(g20)
    c: Block(g21)
    c: Block(g19)
    c: Block(g17)
FEATURE [Part::Extrusion] Extrude029
  Base = -> Sketch038
  Dir = (0,0,1)
  DirMode = 2
  FaceMakerClass = Part::FaceMakerBullseye
  LengthFwd = 72
  LengthRev = 0
  Solid = true
  Symmetric = false
FEATURE [Part::Feature] Face085
  shape: bbox 4.8 x 25.5 x 2e-07 mm, 1 faces, 0 solids (baked)
FEATURE [Part::Revolution] Revolve089  label="moreFrontCaseScrewPost003"
  Angle = 360
  Axis = (0,1,0)
  Base = (0,0,0)
  FaceMakerClass = Part::FaceMakerBullseye
  Placement = pos=(109.5,4.5,3.5) rot=(0,0,1;0rad)
  Solid = false
  Source = -> Face085
  Symmetric = false
FEATURE [Part::Feature] Face086
  shape: bbox 4.8 x 25.5 x 2e-07 mm, 1 faces, 0 solids (baked)
FEATURE [Part::Revolution] Revolve090  label="moreFrontCaseScrewPost004"
  Angle = 360
  Axis = (0,1,0)
  Base = (0,0,0)
  FaceMakerClass = Part::FaceMakerBullseye
  Placement = pos=(109.5,4.5,68.5) rot=(0,0,1;0rad)
  Solid = false
  Source = -> Face086
  Symmetric = false
FEATURE [Part::Fillet] Fillet026  label="top013"
  Base = -> Extrude029
  Edges = 1 edges r=2: [Edge35]
FEATURE [Sketcher::SketchObject] Sketch039
  FullyConstrained = true
  sketch-geometry (7):
    g0: LineSegment StartX=0 StartY=0 StartZ=0 EndX=0 EndY=6 EndZ=0
    g1: Circle CenterX=0 CenterY=0 CenterZ=0 NormalX=0 NormalY=0 NormalZ=1 AngleXU=0 Radius=1
    g2: Circle CenterX=8 CenterY=6 CenterZ=0 NormalX=0 NormalY=0 NormalZ=1 AngleXU=0 Radius=1
    g3: BSplineCurve PolesCount=3 KnotsCount=2 Degree=2 IsPeriodic=0
    g4: GeomPoint X=0 Y=0 Z=0
    g5: GeomPoint X=8 Y=6 Z=0
    g6: LineSegment StartX=0 StartY=6 StartZ=0 EndX=8 EndY=6 EndZ=0
  constraints (14):
    c: Coincident(g0,g-1)
    c: Distance(g0) = 6
    c: Vertical(g0)
    c: Coincident(g3,g0)
    c: Weight(g1) = 1
    c: Equal(g1,g2)
    c: InternalAlignment(g1,g3)
    c: InternalAlignment(g2,g3)
    c: InternalAlignment(g4,g3)
    c: InternalAlignment(g5,g3)
    c: Block(g3)
    c: Coincident(g6,g0)
    c: Coincident(g6,g3)
    c: Horizontal(g6)
FEATURE [Sketcher::SketchObject] Sketch040
  FullyConstrained = true
  sketch-geometry (7):
    g0: LineSegment StartX=0 StartY=0 StartZ=0 EndX=0 EndY=6 EndZ=0
    g1: Circle CenterX=0 CenterY=0 CenterZ=0 NormalX=0 NormalY=0 NormalZ=1 AngleXU=0 Radius=1
    g2: Circle CenterX=8 CenterY=6 CenterZ=0 NormalX=0 NormalY=0 NormalZ=1 AngleXU=0 Radius=1
    g3: BSplineCurve PolesCount=3 KnotsCount=2 Degree=2 IsPeriodic=0
    g4: GeomPoint X=0 Y=0 Z=0
    g5: GeomPoint X=8 Y=6 Z=0
    g6: LineSegment StartX=0 StartY=6 StartZ=0 EndX=8 EndY=6 EndZ=0
  constraints (14):
    c: Coincident(g0,g-1)
    c: Distance(g0) = 6
    c: Vertical(g0)
    c: Coincident(g3,g0)
    c: Weight(g1) = 1
    c: Equal(g1,g2)
    c: InternalAlignment(g1,g3)
    c: InternalAlignment(g2,g3)
    c: InternalAlignment(g4,g3)
    c: InternalAlignment(g5,g3)
    c: Block(g3)
    c: Coincident(g6,g0)
    c: Coincident(g6,g3)
    c: Horizontal(g6)
FEATURE [Sketcher::SketchObject] Sketch041
  FullyConstrained = true
  sketch-geometry (7):
    g0: LineSegment StartX=0 StartY=0 StartZ=0 EndX=0 EndY=6 EndZ=0
    g1: Circle CenterX=0 CenterY=0 CenterZ=0 NormalX=0 NormalY=0 NormalZ=1 AngleXU=0 Radius=1
    g2: Circle CenterX=8 CenterY=6 CenterZ=0 NormalX=0 NormalY=0 NormalZ=1 AngleXU=0 Radius=1
    g3: BSplineCurve PolesCount=3 KnotsCount=2 Degree=2 IsPeriodic=0
    g4: GeomPoint X=0 Y=0 Z=0
    g5: GeomPoint X=8 Y=6 Z=0
    g6: LineSegment StartX=0 StartY=6 StartZ=0 EndX=8 EndY=6 EndZ=0
  constraints (14):
    c: Coincident(g0,g-1)
    c: Distance(g0) = 6
    c: Vertical(g0)
    c: Coincident(g3,g0)
    c: Weight(g1) = 1
    c: Equal(g1,g2)
    c: InternalAlignment(g1,g3)
    c: InternalAlignment(g2,g3)
    c: InternalAlignment(g4,g3)
    c: InternalAlignment(g5,g3)
    c: Block(g3)
    c: Coincident(g6,g0)
    c: Coincident(g6,g3)
    c: Horizontal(g6)
FEATURE [Sketcher::SketchObject] Sketch042
  FullyConstrained = true
  sketch-geometry (7):
    g0: LineSegment StartX=0 StartY=0 StartZ=0 EndX=0 EndY=6 EndZ=0
    g1: Circle CenterX=0 CenterY=0 CenterZ=0 NormalX=0 NormalY=0 NormalZ=1 AngleXU=0 Radius=1
    g2: Circle CenterX=8 CenterY=6 CenterZ=0 NormalX=0 NormalY=0 NormalZ=1 AngleXU=0 Radius=1
    g3: BSplineCurve PolesCount=3 KnotsCount=2 Degree=2 IsPeriodic=0
    g4: GeomPoint X=0 Y=0 Z=0
    g5: GeomPoint X=8 Y=6 Z=0
    g6: LineSegment StartX=0 StartY=6 StartZ=0 EndX=8 EndY=6 EndZ=0
  constraints (14):
    c: Coincident(g0,g-1)
    c: Distance(g0) = 6
    c: Vertical(g0)
    c: Coincident(g3,g0)
    c: Weight(g1) = 1
    c: Equal(g1,g2)
    c: InternalAlignment(g1,g3)
    c: InternalAlignment(g2,g3)
    c: InternalAlignment(g4,g3)
    c: InternalAlignment(g5,g3)
    c: Block(g3)
    c: Coincident(g6,g0)
    c: Coincident(g6,g3)
    c: Horizontal(g6)
FEATURE [Part::Extrusion] Extrude030  label="caseScrewPillarBracket008"
  Base = -> Sketch039
  Dir = (0,0,1)
  DirMode = 2
  FaceMakerClass = Part::FaceMakerBullseye
  LengthFwd = 2.4
  LengthRev = 0
  Placement = pos=(15.76,29,8.8) rot=(0,1,0;0rad)
  Solid = true
  Symmetric = false
FEATURE [Part::Extrusion] Extrude031  label="caseScrewPillarBracket009"
  Base = -> Sketch040
  Dir = (0,0,1)
  DirMode = 2
  FaceMakerClass = Part::FaceMakerBullseye
  LengthFwd = 2.4
  LengthRev = 0
  Placement = pos=(15.76,29,60.8) rot=(0,0,1;0rad)
  Solid = true
  Symmetric = false
FEATURE [Part::Extrusion] Extrude032  label="caseScrewPillarBracket010"
  Base = -> Sketch041
  Dir = (0,0,1)
  DirMode = 2
  FaceMakerClass = Part::FaceMakerBullseye
  LengthFwd = 2.4
  LengthRev = 0
  Placement = pos=(13.7,29,13.26) rot=(0,-1,0;1.5708rad)
  Solid = true
  Symmetric = false
FEATURE [Part::Extrusion] Extrude033  label="caseScrewPillarBracket011"
  Base = -> Sketch042
  Dir = (0,0,1)
  DirMode = 2
  FaceMakerClass = Part::FaceMakerBullseye
  LengthFwd = 2.4
  LengthRev = 0
  Placement = pos=(11.3,29,58.74) rot=(0,1,0;1.5708rad)
  Solid = true
  Symmetric = false
FEATURE [Sketcher::SketchObject] Sketch043
  FullyConstrained = true
  sketch-geometry (7):
    g0: LineSegment StartX=0 StartY=0 StartZ=0 EndX=0 EndY=6 EndZ=0
    g1: Circle CenterX=0 CenterY=0 CenterZ=0 NormalX=0 NormalY=0 NormalZ=1 AngleXU=0 Radius=1
    g2: Circle CenterX=8 CenterY=6 CenterZ=0 NormalX=0 NormalY=0 NormalZ=1 AngleXU=0 Radius=1
    g3: BSplineCurve PolesCount=3 KnotsCount=2 Degree=2 IsPeriodic=0
    g4: GeomPoint X=0 Y=0 Z=0
    g5: GeomPoint X=8 Y=6 Z=0
    g6: LineSegment StartX=0 StartY=6 StartZ=0 EndX=8 EndY=6 EndZ=0
  constraints (14):
    c: Coincident(g0,g-1)
    c: Distance(g0) = 6
    c: Vertical(g0)
    c: Coincident(g3,g0)
    c: Weight(g1) = 1
    c: Equal(g1,g2)
    c: InternalAlignment(g1,g3)
    c: InternalAlignment(g2,g3)
    c: InternalAlignment(g4,g3)
    c: InternalAlignment(g5,g3)
    c: Block(g3)
    c: Coincident(g6,g0)
    c: Coincident(g6,g3)
    c: Horizontal(g6)
FEATURE [Part::Extrusion] Extrude034  label="caseScrewPillarBracket012"
  Base = -> Sketch043
  Dir = (0,0,1)
  DirMode = 2
  FaceMakerClass = Part::FaceMakerBullseye
  LengthFwd = 2.4
  LengthRev = 0
  Placement = pos=(88.3,29,65.23) rot=(0,1,0;1.5708rad)
  Solid = true
  Symmetric = false
FEATURE [Sketcher::SketchObject] Sketch044
  FullyConstrained = true
  sketch-geometry (7):
    g0: LineSegment StartX=0 StartY=0 StartZ=0 EndX=0 EndY=6 EndZ=0
    g1: Circle CenterX=0 CenterY=0 CenterZ=0 NormalX=0 NormalY=0 NormalZ=1 AngleXU=0 Radius=1
    g2: Circle CenterX=8 CenterY=6 CenterZ=0 NormalX=0 NormalY=0 NormalZ=1 AngleXU=0 Radius=1
    g3: BSplineCurve PolesCount=3 KnotsCount=2 Degree=2 IsPeriodic=0
    g4: GeomPoint X=0 Y=0 Z=0
    g5: GeomPoint X=8 Y=6 Z=0
    g6: LineSegment StartX=0 StartY=6 StartZ=0 EndX=8 EndY=6 EndZ=0
  constraints (14):
    c: Coincident(g0,g-1)
    c: Distance(g0) = 6
    c: Vertical(g0)
    c: Coincident(g3,g0)
    c: Weight(g1) = 1
    c: Equal(g1,g2)
    c: InternalAlignment(g1,g3)
    c: InternalAlignment(g2,g3)
    c: InternalAlignment(g4,g3)
    c: InternalAlignment(g5,g3)
    c: Block(g3)
    c: Coincident(g6,g0)
    c: Coincident(g6,g3)
    c: Horizontal(g6)
FEATURE [Part::Extrusion] Extrude035  label="caseScrewPillarBracket013"
  Base = -> Sketch044
  Dir = (0,0,1)
  DirMode = 2
  FaceMakerClass = Part::FaceMakerBullseye
  LengthFwd = 2.4
  LengthRev = 0
  Placement = pos=(90.7,29,6.77) rot=(0,-1,0;1.5708rad)
  Solid = true
  Symmetric = false
FEATURE [Sketcher::SketchObject] Sketch045
  FullyConstrained = true
  sketch-geometry (7):
    g0: LineSegment StartX=0 StartY=0 StartZ=0 EndX=0 EndY=6 EndZ=0
    g1: Circle CenterX=0 CenterY=0 CenterZ=0 NormalX=0 NormalY=0 NormalZ=1 AngleXU=0 Radius=1
    g2: Circle CenterX=8 CenterY=6 CenterZ=0 NormalX=0 NormalY=0 NormalZ=1 AngleXU=0 Radius=1
    g3: BSplineCurve PolesCount=3 KnotsCount=2 Degree=2 IsPeriodic=0
    g4: GeomPoint X=0 Y=0 Z=0
    g5: GeomPoint X=8 Y=6 Z=0
    g6: LineSegment StartX=0 StartY=6 StartZ=0 EndX=8 EndY=6 EndZ=0
  constraints (14):
    c: Coincident(g0,g-1)
    c: Distance(g0) = 6
    c: Vertical(g0)
    c: Coincident(g3,g0)
    c: Weight(g1) = 1
    c: Equal(g1,g2)
    c: InternalAlignment(g1,g3)
    c: InternalAlignment(g2,g3)
    c: InternalAlignment(g4,g3)
    c: InternalAlignment(g5,g3)
    c: Block(g3)
    c: Coincident(g6,g0)
    c: Coincident(g6,g3)
    c: Horizontal(g6)
FEATURE [Sketcher::SketchObject] Sketch046
  FullyConstrained = true
  sketch-geometry (7):
    g0: LineSegment StartX=0 StartY=0 StartZ=0 EndX=0 EndY=6 EndZ=0
    g1: Circle CenterX=0 CenterY=0 CenterZ=0 NormalX=0 NormalY=0 NormalZ=1 AngleXU=0 Radius=1
    g2: Circle CenterX=8 CenterY=6 CenterZ=0 NormalX=0 NormalY=0 NormalZ=1 AngleXU=0 Radius=1
    g3: BSplineCurve PolesCount=3 KnotsCount=2 Degree=2 IsPeriodic=0
    g4: GeomPoint X=0 Y=0 Z=0
    g5: GeomPoint X=8 Y=6 Z=0
    g6: LineSegment StartX=0 StartY=6 StartZ=0 EndX=8 EndY=6 EndZ=0
  constraints (14):
    c: Coincident(g0,g-1)
    c: Distance(g0) = 6
    c: Vertical(g0)
    c: Coincident(g3,g0)
    c: Weight(g1) = 1
    c: Equal(g1,g2)
    c: InternalAlignment(g1,g3)
    c: InternalAlignment(g2,g3)
    c: InternalAlignment(g4,g3)
    c: InternalAlignment(g5,g3)
    c: Block(g3)
    c: Coincident(g6,g0)
    c: Coincident(g6,g3)
    c: Horizontal(g6)
FEATURE [Part::Extrusion] Extrude036  label="caseScrewPillarBracket014"
  Base = -> Sketch045
  Dir = (0,0,1)
  DirMode = 2
  FaceMakerClass = Part::FaceMakerBullseye
  LengthFwd = 2.4
  LengthRev = 0
  Placement = pos=(110.7,29,6.77) rot=(0,-1,0;1.5708rad)
  Solid = true
  Symmetric = false
FEATURE [Part::Extrusion] Extrude037  label="caseScrewPillarBracket015"
  Base = -> Sketch046
  Dir = (0,0,1)
  DirMode = 2
  FaceMakerClass = Part::FaceMakerBullseye
  LengthFwd = 2.4
  LengthRev = 0
  Placement = pos=(108.3,29,65.23) rot=(0,1,0;1.5708rad)
  Solid = true
  Symmetric = false
FEATURE [Part::Box] Box013  label="frontCaseScrewPillarBracket002"
  AttacherType = Attacher::AttachEngine3D
  Height = 2.4
  Length = 22
  Placement = pos=(87,28,2.3) rot=(0,0,1;0rad)
  Width = 7
FEATURE [Part::Box] Box014  label="frontCaseScrewPillarBracket003"
  AttacherType = Attacher::AttachEngine3D
  Height = 2.4
  Length = 22
  Placement = pos=(87,28,67.3) rot=(0,0,1;0rad)
  Width = 7
FEATURE [Part::Feature] Face087
  shape: bbox 4.8 x 30.2 x 2e-07 mm, 1 faces, 0 solids (baked)
FEATURE [Part::Revolution] Revolve091  label="frontCaseScrewPost004"
  Angle = 360
  Axis = (0,1,0)
  Base = (0,0,0)
  FaceMakerClass = Part::FaceMakerBullseye
  Placement = pos=(89.5,4.5,3.5) rot=(0,0,1;0rad)
  Solid = false
  Source = -> Face087
  Symmetric = false
FEATURE [Part::Feature] Face088
  shape: bbox 4.8 x 30.2 x 2e-07 mm, 1 faces, 0 solids (baked)
FEATURE [Part::Revolution] Revolve092  label="frontCaseScrewPost005"
  Angle = 360
  Axis = (0,1,0)
  Base = (0,0,0)
  FaceMakerClass = Part::FaceMakerBullseye
  Placement = pos=(89.5,4.5,68.5) rot=(0,0,1;0rad)
  Solid = false
  Source = -> Face088
  Symmetric = false
FEATURE [Part::Feature] Face089
  shape: bbox 3.5 x 30.2 x 2e-07 mm, 1 faces, 0 solids (baked)
FEATURE [Part::Revolution] Revolve093  label="backCaseScrewPost002"
  Angle = 360
  Axis = (0,1,0)
  Base = (0,0,0)
  FaceMakerClass = Part::FaceMakerBullseye
  Placement = pos=(12.5,4.5,10) rot=(0,0,1;0rad)
  Solid = false
  Source = -> Face089
  Symmetric = false
FEATURE [Part::Feature] Face090
  shape: bbox 3.5 x 30.2 x 2e-07 mm, 1 faces, 0 solids (baked)
FEATURE [Part::Revolution] Revolve094  label="backCaseScrewPost003"
  Angle = 360
  Axis = (0,1,0)
  Base = (0,0,0)
  FaceMakerClass = Part::FaceMakerBullseye
  Placement = pos=(12.5,4.5,62) rot=(0,0,1;0rad)
  Solid = false
  Source = -> Face090
  Symmetric = false
FEATURE [Part::Box] Box015  label="Cube011"
  AttacherType = Attacher::AttachEngine3D
  Height = 28.8
  Length = 3
  Placement = pos=(107.3,28,21.6) rot=(0,0,1;0rad)
  Width = 7
FEATURE [Part::Box] Box016  label="Cube012"
  AttacherType = Attacher::AttachEngine3D
  Height = 3
  Length = 7.4
  Placement = pos=(107.3,28,18.6) rot=(0,0,1;0rad)
  Width = 7
FEATURE [Part::Box] Box017  label="Cube013"
  AttacherType = Attacher::AttachEngine3D
  Height = 3
  Length = 7.4
  Placement = pos=(107.3,28,50.4) rot=(0,0,1;0rad)
  Width = 7
FEATURE [Part::Cylinder] Cylinder024
  Angle = 360
  AttacherType = Attacher::AttachEngine3D
  Height = 20
  Placement = pos=(0,0,36.15) rot=(0,0,1;0rad)
  Radius = 14.3
FEATURE [Part::Cylinder] Cylinder025
  Angle = 360
  AttacherType = Attacher::AttachEngine3D
  Height = 10
  Placement = pos=(0,0,36.15) rot=(0,0,1;0rad)
  Radius = 4
FEATURE [Part::MultiFuse] Fusion066  label="removeToCreteHoleForPlugHousing009"
  Placement = pos=(70,19,36) rot=(0,1,0;1.5708rad)
  Shapes = -> [Cylinder024,Cylinder025]
FEATURE [Part::MultiFuse] Fusion065  label="plugHousingBracketHolder002"
  Shapes = -> [Box017,Box015,Box016]
FEATURE [Part::Cut] Cut025  label="plugHousingBracketHolder003"
  Base = -> Fusion065
  Placement = pos=(7,0,0) rot=(0,0,1;0rad)
  Tool = -> Fusion066
FEATURE [Sketcher::SketchObject] Sketch047
  FullyConstrained = false
  Placement = pos=(0,0,0) rot=(1,0,0;1.5708rad)
  sketch-geometry (24):
    g0: ArcOfCircle CenterX=-4 CenterY=-10.5 CenterZ=0 NormalX=0 NormalY=0 NormalZ=1 AngleXU=0 Radius=1.5 StartAngle=6e-16 EndAngle=3.14159
    g1: ArcOfCircle CenterX=-34.2 CenterY=-10.5 CenterZ=0 NormalX=0 NormalY=0 NormalZ=1 AngleXU=0 Radius=1.5 StartAngle=0 EndAngle=3.14159
    g2: ArcOfCircle CenterX=-34.2 CenterY=-27.7 CenterZ=0 NormalX=0 NormalY=0 NormalZ=1 AngleXU=0 Radius=1.5 StartAngle=3.14159 EndAngle=6.28319
    g3: ArcOfCircle CenterX=-4 CenterY=-27.7 CenterZ=0 NormalX=0 NormalY=0 NormalZ=1 AngleXU=0 Radius=1.5 StartAngle=3.1416 EndAngle=6.28319
    g4: ArcOfCircle CenterX=-10 CenterY=-4.3 CenterZ=0 NormalX=0 NormalY=0 NormalZ=1 AngleXU=0 Radius=1.5 StartAngle=2e-16 EndAngle=3.14159
    g5: ArcOfCircle CenterX=-16.1 CenterY=-1.8 CenterZ=0 NormalX=0 NormalY=0 NormalZ=1 AngleXU=0 Radius=1.5 StartAngle=5e-16 EndAngle=3.14159
    g6: ArcOfCircle CenterX=-22.1 CenterY=-1.8 CenterZ=0 NormalX=0 NormalY=0 NormalZ=1 AngleXU=0 Radius=1.5 StartAngle=5e-16 EndAngle=3.14159
    g7: ArcOfCircle CenterX=-28.2 CenterY=-4.3 CenterZ=0 NormalX=0 NormalY=0 NormalZ=1 AngleXU=0 Radius=1.5 StartAngle=2e-16 EndAngle=3.14159
    g8: ArcOfCircle CenterX=-10 CenterY=-33.9 CenterZ=0 NormalX=0 NormalY=0 NormalZ=1 AngleXU=0 Radius=1.5 StartAngle=3.14159 EndAngle=6.28319
    g9: ArcOfCircle CenterX=-16.1 CenterY=-36.4 CenterZ=0 NormalX=0 NormalY=0 NormalZ=1 AngleXU=0 Radius=1.5 StartAngle=3.14159 EndAngle=6.28319
    g10: ArcOfCircle CenterX=-22.1 CenterY=-36.4 CenterZ=0 NormalX=0 NormalY=0 NormalZ=1 AngleXU=0 Radius=1.5 StartAngle=3.14159 EndAngle=6.28319
    g11: ArcOfCircle CenterX=-28.2 CenterY=-33.9 CenterZ=0 NormalX=0 NormalY=0 NormalZ=1 AngleXU=0 Radius=1.5 StartAngle=3.14159 EndAngle=6.28319
    g12: LineSegment StartX=-35.7 StartY=-10.5 StartZ=0 EndX=-35.7 EndY=-27.7 EndZ=0
    g13: LineSegment StartX=-32.7 StartY=-10.5 StartZ=0 EndX=-32.7 EndY=-27.7 EndZ=0
    g14: LineSegment StartX=-29.7 StartY=-33.9 StartZ=0 EndX=-29.7 EndY=-4.3 EndZ=0
    g15: LineSegment StartX=-26.7 StartY=-33.9 StartZ=0 EndX=-26.7 EndY=-4.3 EndZ=0
    g16: LineSegment StartX=-2.5 StartY=-10.5 StartZ=0 EndX=-2.5 EndY=-27.7 EndZ=0
    g17: LineSegment StartX=-8.5 StartY=-4.3 StartZ=0 EndX=-8.5 EndY=-33.9 EndZ=0
    g18: LineSegment StartX=-5.5 StartY=-10.5 StartZ=0 EndX=-5.5 EndY=-27.7 EndZ=0
    g19: LineSegment StartX=-11.5 StartY=-4.3 StartZ=0 EndX=-11.5 EndY=-33.9 EndZ=0
    g20: LineSegment StartX=-14.6 StartY=-1.8 StartZ=0 EndX=-14.6 EndY=-36.4 EndZ=0
    g21: LineSegment StartX=-17.6 StartY=-1.8 StartZ=0 EndX=-17.6 EndY=-36.4 EndZ=0
    g22: LineSegment StartX=-20.6 StartY=-36.4 StartZ=0 EndX=-20.6 EndY=-1.8 EndZ=0
    g23: LineSegment StartX=-23.6 StartY=-1.8 StartZ=0 EndX=-23.6 EndY=-36.4 EndZ=0
  constraints (48):
    c: Block(g0)
    c: Block(g1)
    c: Block(g2)
    c: Block(g3)
    c: Block(g4)
    c: Block(g5)
    c: Block(g6)
    c: Block(g7)
    c: Block(g8)
    c: Block(g9)
    c: Block(g10)
    c: Block(g11)
    c: Coincident(g12,g1)
    c: Coincident(g12,g2)
    c: Vertical(g12)
    c: Coincident(g13,g1)
    c: Coincident(g13,g2)
    c: Vertical(g13)
    c: Coincident(g14,g11)
    c: Coincident(g14,g7)
    c: Vertical(g14)
    c: Coincident(g15,g11)
    c: Coincident(g15,g7)
    c: Vertical(g15)
    c: Coincident(g16,g0)
    c: Coincident(g16,g3)
    c: Vertical(g16)
    c: Coincident(g17,g4)
    c: Coincident(g17,g8)
    c: Vertical(g17)
    c: Coincident(g18,g0)
    c: Coincident(g18,g3)
    c: Vertical(g18)
    c: Coincident(g19,g4)
    c: Coincident(g19,g8)
    c: Vertical(g19)
    c: Coincident(g20,g5)
    c: Coincident(g20,g9)
    c: Vertical(g20)
    c: Coincident(g21,g5)
    c: Coincident(g21,g9)
    c: Vertical(g21)
    c: Coincident(g22,g10)
    c: Coincident(g22,g6)
    c: Vertical(g22)
    c: Coincident(g23,g6)
    c: Coincident(g23,g10)
    c: Vertical(g23)
FEATURE [Part::Extrusion] Extrude038  label="removeToCreateFanGrillHoles001"
  Base = -> Sketch047
  Dir = (0,-1,6e-16)
  DirMode = 2
  FaceMakerClass = Part::FaceMakerBullseye
  LengthFwd = 10
  LengthRev = 0
  Placement = pos=(65.4,44,54.82) rot=(0,0,1;0rad)
  Solid = true
  Symmetric = false
FEATURE [Part::Feature] Wire004
  shape: bbox 11 x 5.2 x 2e-07 mm, 0 faces, 0 solids (baked)
FEATURE [Part::Revolution] Revolve095
  Angle = 360
  Axis = (0,1,0)
  Base = (0,0,0)
  FaceMakerClass = Part::FaceMakerBullseye
  Placement = pos=(30.3,38,19.7) rot=(0,0,1;0rad)
  Solid = true
  Source = -> Wire004
  Symmetric = false
FEATURE [Part::Feature] Wire005
  shape: bbox 11 x 5.2 x 2e-07 mm, 0 faces, 0 solids (baked)
FEATURE [Part::Revolution] Revolve096
  Angle = 360
  Axis = (0,1,0)
  Base = (0,0,0)
  FaceMakerClass = Part::FaceMakerBullseye
  Placement = pos=(30.3,38,51.7) rot=(0,0,1;0rad)
  Solid = true
  Source = -> Wire005
  Symmetric = false
FEATURE [Part::Feature] Wire006
  shape: bbox 11 x 5.2 x 2e-07 mm, 0 faces, 0 solids (baked)
FEATURE [Part::Revolution] Revolve097
  Angle = 360
  Axis = (0,1,0)
  Base = (0,0,0)
  FaceMakerClass = Part::FaceMakerBullseye
  Placement = pos=(62.3,38,51.7) rot=(0,0,1;0rad)
  Solid = true
  Source = -> Wire006
  Symmetric = false
FEATURE [Part::Feature] Wire007
  shape: bbox 11 x 5.2 x 2e-07 mm, 0 faces, 0 solids (baked)
FEATURE [Part::Revolution] Revolve098
  Angle = 360
  Axis = (0,1,0)
  Base = (0,0,0)
  FaceMakerClass = Part::FaceMakerBullseye
  Placement = pos=(62.3,38,19.7) rot=(0,0,1;0rad)
  Solid = true
  Source = -> Wire007
  Symmetric = false
FEATURE [Part::MultiFuse] Fusion067  label="fanScrewHousing002"
  Shapes = -> [Revolve098,Revolve097,Revolve096,Revolve095]
FEATURE [Part::Feature] Face091 .. Face094  x4 (patterned run collapsed; names and placements below)
  shape: bbox 3.5 x 17.8 x 2e-07 mm, 1 faces, 0 solids (baked)
FEATURE [Part::Revolution] Revolve099  label="removeToCreateScrewAndThreadedInsertHole026"
  Angle = 360
  Axis = (0,1,0)
  Base = (0,0,0)
  FaceMakerClass = Part::FaceMakerBullseye
  Placement = pos=(62.3,30.3,19.7) rot=(0,0,1;0rad)
  Solid = false
  Source = -> Face091
  Symmetric = false
FEATURE [Part::Revolution] Revolve100  label="removeToCreateScrewAndThreadedInsertHole027"
  Angle = 360
  Axis = (0,1,0)
  Base = (0,0,0)
  FaceMakerClass = Part::FaceMakerBullseye
  Placement = pos=(62.3,30.3,51.7) rot=(0,0,1;0rad)
  Solid = false
  Source = -> Face092
  Symmetric = false
FEATURE [Part::Revolution] Revolve101  label="removeToCreateScrewAndThreadedInsertHole028"
  Angle = 360
  Axis = (0,1,0)
  Base = (0,0,0)
  FaceMakerClass = Part::FaceMakerBullseye
  Placement = pos=(30.3,30.3,19.7) rot=(0,0,1;0rad)
  Solid = false
  Source = -> Face093
  Symmetric = false
FEATURE [Part::Revolution] Revolve102  label="removeToCreateScrewAndThreadedInsertHole029"
  Angle = 360
  Axis = (0,1,0)
  Base = (0,0,0)
  FaceMakerClass = Part::FaceMakerBullseye
  Placement = pos=(30.3,30.3,51.7) rot=(0,0,1;0rad)
  Solid = false
  Source = -> Face094
  Symmetric = false
FEATURE [Part::MultiFuse] Fusion068  label="createThreadedInsertHolesForFan002"
  Shapes = -> [Revolve099,Revolve100,Revolve101,Revolve102]
FEATURE [Part::Cut] Cut026  label="fanScrewHousing003"
  Base = -> Fusion067
  Tool = -> Fusion068
FEATURE [Sketcher::SketchObject] Sketch048
  FullyConstrained = false
  Placement = pos=(0,0,0) rot=(1,0,0;1.5708rad)
  sketch-geometry (24):
    g0: ArcOfCircle CenterX=-4 CenterY=-10.5 CenterZ=0 NormalX=0 NormalY=0 NormalZ=1 AngleXU=0 Radius=1.5 StartAngle=6e-16 EndAngle=3.14159
    g1: ArcOfCircle CenterX=-34.2 CenterY=-10.5 CenterZ=0 NormalX=0 NormalY=0 NormalZ=1 AngleXU=0 Radius=1.5 StartAngle=0 EndAngle=3.14159
    g2: ArcOfCircle CenterX=-34.2 CenterY=-27.7 CenterZ=0 NormalX=0 NormalY=0 NormalZ=1 AngleXU=0 Radius=1.5 StartAngle=3.14159 EndAngle=6.28319
    g3: ArcOfCircle CenterX=-4 CenterY=-27.7 CenterZ=0 NormalX=0 NormalY=0 NormalZ=1 AngleXU=0 Radius=1.5 StartAngle=3.1416 EndAngle=6.28319
    g4: ArcOfCircle CenterX=-10 CenterY=-4.3 CenterZ=0 NormalX=0 NormalY=0 NormalZ=1 AngleXU=0 Radius=1.5 StartAngle=2e-16 EndAngle=3.14159
    g5: ArcOfCircle CenterX=-16.1 CenterY=-1.8 CenterZ=0 NormalX=0 NormalY=0 NormalZ=1 AngleXU=0 Radius=1.5 StartAngle=5e-16 EndAngle=3.14159
    g6: ArcOfCircle CenterX=-22.1 CenterY=-1.8 CenterZ=0 NormalX=0 NormalY=0 NormalZ=1 AngleXU=0 Radius=1.5 StartAngle=5e-16 EndAngle=3.14159
    g7: ArcOfCircle CenterX=-28.2 CenterY=-4.3 CenterZ=0 NormalX=0 NormalY=0 NormalZ=1 AngleXU=0 Radius=1.5 StartAngle=2e-16 EndAngle=3.14159
    g8: ArcOfCircle CenterX=-10 CenterY=-33.9 CenterZ=0 NormalX=0 NormalY=0 NormalZ=1 AngleXU=0 Radius=1.5 StartAngle=3.14159 EndAngle=6.28319
    g9: ArcOfCircle CenterX=-16.1 CenterY=-36.4 CenterZ=0 NormalX=0 NormalY=0 NormalZ=1 AngleXU=0 Radius=1.5 StartAngle=3.14159 EndAngle=6.28319
    g10: ArcOfCircle CenterX=-22.1 CenterY=-36.4 CenterZ=0 NormalX=0 NormalY=0 NormalZ=1 AngleXU=0 Radius=1.5 StartAngle=3.14159 EndAngle=6.28319
    g11: ArcOfCircle CenterX=-28.2 CenterY=-33.9 CenterZ=0 NormalX=0 NormalY=0 NormalZ=1 AngleXU=0 Radius=1.5 StartAngle=3.14159 EndAngle=6.28319
    g12: LineSegment StartX=-35.7 StartY=-10.5 StartZ=0 EndX=-35.7 EndY=-27.7 EndZ=0
    g13: LineSegment StartX=-32.7 StartY=-10.5 StartZ=0 EndX=-32.7 EndY=-27.7 EndZ=0
    g14: LineSegment StartX=-29.7 StartY=-33.9 StartZ=0 EndX=-29.7 EndY=-4.3 EndZ=0
    g15: LineSegment StartX=-26.7 StartY=-33.9 StartZ=0 EndX=-26.7 EndY=-4.3 EndZ=0
    g16: LineSegment StartX=-2.5 StartY=-10.5 StartZ=0 EndX=-2.5 EndY=-27.7 EndZ=0
    g17: LineSegment StartX=-8.5 StartY=-4.3 StartZ=0 EndX=-8.5 EndY=-33.9 EndZ=0
    g18: LineSegment StartX=-5.5 StartY=-10.5 StartZ=0 EndX=-5.5 EndY=-27.7 EndZ=0
    g19: LineSegment StartX=-11.5 StartY=-4.3 StartZ=0 EndX=-11.5 EndY=-33.9 EndZ=0
    g20: LineSegment StartX=-14.6 StartY=-1.8 StartZ=0 EndX=-14.6 EndY=-36.4 EndZ=0
    g21: LineSegment StartX=-17.6 StartY=-1.8 StartZ=0 EndX=-17.6 EndY=-36.4 EndZ=0
    g22: LineSegment StartX=-20.6 StartY=-36.4 StartZ=0 EndX=-20.6 EndY=-1.8 EndZ=0
    g23: LineSegment StartX=-23.6 StartY=-1.8 StartZ=0 EndX=-23.6 EndY=-36.4 EndZ=0
  constraints (48):
    c: Block(g0)
    c: Block(g1)
    c: Block(g2)
    c: Block(g3)
    c: Block(g4)
    c: Block(g5)
    c: Block(g6)
    c: Block(g7)
    c: Block(g8)
    c: Block(g9)
    c: Block(g10)
    c: Block(g11)
    c: Coincident(g12,g1)
    c: Coincident(g12,g2)
    c: Vertical(g12)
    c: Coincident(g13,g1)
    c: Coincident(g13,g2)
    c: Vertical(g13)
    c: Coincident(g14,g11)
    c: Coincident(g14,g7)
    c: Vertical(g14)
    c: Coincident(g15,g11)
    c: Coincident(g15,g7)
    c: Vertical(g15)
    c: Coincident(g16,g0)
    c: Coincident(g16,g3)
    c: Vertical(g16)
    c: Coincident(g17,g4)
    c: Coincident(g17,g8)
    c: Vertical(g17)
    c: Coincident(g18,g0)
    c: Coincident(g18,g3)
    c: Vertical(g18)
    c: Coincident(g19,g4)
    c: Coincident(g19,g8)
    c: Vertical(g19)
    c: Coincident(g20,g5)
    c: Coincident(g20,g9)
    c: Vertical(g20)
    c: Coincident(g21,g5)
    c: Coincident(g21,g9)
    c: Vertical(g21)
    c: Coincident(g22,g10)
    c: Coincident(g22,g6)
    c: Vertical(g22)
    c: Coincident(g23,g6)
    c: Coincident(g23,g10)
    c: Vertical(g23)
FEATURE [Part::Extrusion] Extrude039  label="removeToCreateFanGrillHoles002"
  Base = -> Sketch048
  Dir = (0,-1,6e-16)
  DirMode = 2
  FaceMakerClass = Part::FaceMakerBullseye
  LengthFwd = 10
  LengthRev = 0
  Placement = pos=(65.4,44,54.82) rot=(0,0,1;0rad)
  Solid = true
  Symmetric = false
FEATURE [Part::Cut] Cut027  label="fanScrewHousing004"
  Base = -> Cut026
  Tool = -> Extrude038
FEATURE [Part::Cut] Cut028  label="top014"
  Base = -> Fillet026
  Tool = -> Extrude039
FEATURE [Part::Feature] Face095 .. Face098  x4 (patterned run collapsed; names and placements below)
  shape: bbox 3.5 x 17.8 x 2e-07 mm, 1 faces, 0 solids (baked)
FEATURE [Part::Revolution] Revolve103  label="removeToCreateScrewAndThreadedInsertHole030"
  Angle = 360
  Axis = (0,1,0)
  Base = (0,0,0)
  FaceMakerClass = Part::FaceMakerBullseye
  Placement = pos=(62.3,30.3,19.7) rot=(0,0,1;0rad)
  Solid = false
  Source = -> Face095
  Symmetric = false
FEATURE [Part::Revolution] Revolve104  label="removeToCreateScrewAndThreadedInsertHole031"
  Angle = 360
  Axis = (0,1,0)
  Base = (0,0,0)
  FaceMakerClass = Part::FaceMakerBullseye
  Placement = pos=(62.3,30.3,51.7) rot=(0,0,1;0rad)
  Solid = false
  Source = -> Face096
  Symmetric = false
FEATURE [Part::Revolution] Revolve105  label="removeToCreateScrewAndThreadedInsertHole032"
  Angle = 360
  Axis = (0,1,0)
  Base = (0,0,0)
  FaceMakerClass = Part::FaceMakerBullseye
  Placement = pos=(30.3,30.3,19.7) rot=(0,0,1;0rad)
  Solid = false
  Source = -> Face097
  Symmetric = false
FEATURE [Part::Revolution] Revolve106  label="removeToCreateScrewAndThreadedInsertHole033"
  Angle = 360
  Axis = (0,1,0)
  Base = (0,0,0)
  FaceMakerClass = Part::FaceMakerBullseye
  Placement = pos=(30.3,30.3,51.7) rot=(0,0,1;0rad)
  Solid = false
  Source = -> Face098
  Symmetric = false
FEATURE [Part::MultiFuse] Fusion069  label="createThreadedInsertHolesForFan003"
  Shapes = -> [Revolve103,Revolve104,Revolve105,Revolve106]
FEATURE [Part::Cut] Cut029  label="top015"
  Base = -> Cut028
  Tool = -> Fusion054
FEATURE [Part::Cut] Cut030  label="fanScrewHousing005"
  Base = -> Cut027
  Tool = -> Fusion069
FEATURE [Part::Cylinder] Cylinder026  label="removeToCreteHoleForPlugHousing010"
  Angle = 360
  AttacherType = Attacher::AttachEngine3D
  Height = 20
  Placement = pos=(-2,19,36) rot=(0,1,0;1.5708rad)
  Radius = 14.3
FEATURE [Part::Box] Box018  label="removeToCreteHoleForPlugHousing011"
  AttacherType = Attacher::AttachEngine3D
  Height = 28.6
  Length = 10
  Placement = pos=(-2,0,21.7) rot=(0,0,1;0rad)
  Width = 19
FEATURE [Part::Box] Box019  label="wireHolderBottomCaseBit"
  AttacherType = Attacher::AttachEngine3D
  Height = 28
  Length = 3
  Placement = pos=(0,0,22) rot=(0,0,1;0rad)
  Width = 21
FEATURE [Part::Cylinder] Cylinder027  label="removeToCreteHoleForPlugHousing012"
  Angle = 360
  AttacherType = Attacher::AttachEngine3D
  Height = 20
  Placement = pos=(-2,19,36) rot=(0,1,0;1.5708rad)
  Radius = 14.3
FEATURE [Part::Cut] Cut031  label="wireHolderBottomCaseBit001"
  Base = -> Box019
  Tool = -> Cylinder027
FEATURE [Part::MultiFuse] Fusion070  label="removeToCreteHoleForPlugHousing013"
  Shapes = -> [Box018,Cylinder026]
FEATURE [Part::Cut] Cut032  label="top016"
  Base = -> Cut029
  Tool = -> Fusion070
FEATURE [Part::Cylinder] Cylinder028
  Angle = 360
  AttacherType = Attacher::AttachEngine3D
  Height = 20
  Placement = pos=(0,0,36.15) rot=(0,0,1;0rad)
  Radius = 14.3
FEATURE [Part::Cylinder] Cylinder029
  Angle = 360
  AttacherType = Attacher::AttachEngine3D
  Height = 10
  Placement = pos=(0,0,36.15) rot=(0,0,1;0rad)
  Radius = 4
FEATURE [Part::MultiFuse] Fusion071  label="removeToCreteHoleForPlugHousing014"
  Placement = pos=(70,19,36) rot=(0,1,0;1.5708rad)
  Shapes = -> [Cylinder028,Cylinder029]
FEATURE [Sketcher::SketchObject] Sketch049  label="topSketch011"
  FullyConstrained = true
  sketch-geometry (4):
    g0: ArcOfCircle CenterX=105 CenterY=19 CenterZ=0 NormalX=0 NormalY=0 NormalZ=1 AngleXU=0 Radius=20.6155 StartAngle=5.54125 EndAngle=6.28319
    g1: ArcOfCircle CenterX=105 CenterY=19 CenterZ=0 NormalX=0 NormalY=0 NormalZ=1 AngleXU=0 Radius=13 StartAngle=5.54125 EndAngle=6.28319
    g2: LineSegment StartX=118 StartY=19 StartZ=0 EndX=125.616 EndY=19 EndZ=0
    g3: LineSegment StartX=114.583 StartY=10.2157 StartZ=0 EndX=120.197 EndY=5.06982 EndZ=0
  constraints (7):
    c: Block(g0)
    c: Block(g1)
    c: Coincident(g2,g1)
    c: Coincident(g2,g0)
    c: Horizontal(g2)
    c: Coincident(g3,g1)
    c: Coincident(g3,g0)
FEATURE [Part::Box] Box020  label="removeToCreteHoleForPlugHousing015"
  AttacherType = Attacher::AttachEngine3D
  Height = 28.6
  Length = 20
  Placement = pos=(106.15,0,21.7) rot=(0,0,1;0rad)
  Width = 19
FEATURE [Part::MultiFuse] Fusion072  label="removeToCreteHoleForPlugHousing016"
  Shapes = -> [Box020,Fusion071]
FEATURE [Part::Cut] Cut033  label="removeToCreteHoleForPlugHousing017"
  Base = -> Cut032
  Tool = -> Fusion072
FEATURE [Part::Cylinder] Cylinder030
  Angle = 360
  AttacherType = Attacher::AttachEngine3D
  Height = 20
  Placement = pos=(0,0,36.15) rot=(0,0,1;0rad)
  Radius = 14.3
FEATURE [Part::Cylinder] Cylinder031
  Angle = 360
  AttacherType = Attacher::AttachEngine3D
  Height = 10
  Placement = pos=(0,0,36.15) rot=(0,0,1;0rad)
  Radius = 4
FEATURE [Part::Box] Box021  label="removeToCreteHoleForPlugHousing019"
  AttacherType = Attacher::AttachEngine3D
  Height = 28.6
  Length = 20
  Placement = pos=(106.15,0,21.7) rot=(0,0,1;0rad)
  Width = 19
FEATURE [Part::MultiFuse] Fusion074  label="removeToCreteHoleForPlugHousing020"
  Placement = pos=(70,19,36) rot=(0,1,0;1.5708rad)
  Shapes = -> [Cylinder030,Cylinder031]
FEATURE [Part::MultiFuse] Fusion073  label="removeToCreteHoleForPlugHousing018"
  Placement = pos=(0,0,28.3) rot=(0,0,1;0rad)
  Shapes = -> [Box021,Fusion074]
FEATURE [Part::Cylinder] Cylinder032
  Angle = 360
  AttacherType = Attacher::AttachEngine3D
  Height = 20
  Placement = pos=(0,0,36.15) rot=(0,0,1;0rad)
  Radius = 14.3
FEATURE [Part::Cylinder] Cylinder033
  Angle = 360
  AttacherType = Attacher::AttachEngine3D
  Height = 10
  Placement = pos=(0,0,36.15) rot=(0,0,1;0rad)
  Radius = 4
FEATURE [Part::Box] Box022  label="removeToCreteHoleForPlugHousing021"
  AttacherType = Attacher::AttachEngine3D
  Height = 28.6
  Length = 20
  Placement = pos=(106.15,0,21.7) rot=(0,0,1;0rad)
  Width = 19
FEATURE [Part::MultiFuse] Fusion076  label="removeToCreteHoleForPlugHousing023"
  Placement = pos=(70,19,36) rot=(0,1,0;1.5708rad)
  Shapes = -> [Cylinder032,Cylinder033]
FEATURE [Part::MultiFuse] Fusion075  label="removeToCreteHoleForPlugHousing022"
  Placement = pos=(0,0,-28.3) rot=(0,0,1;0rad)
  Shapes = -> [Box022,Fusion076]
FEATURE [Part::MultiFuse] Fusion077  label="removeToCreatePlugHousingBottomBit"
  Shapes = -> [Fusion075,Fusion073]
FEATURE [Part::Cylinder] Cylinder034
  Angle = 360
  AttacherType = Attacher::AttachEngine3D
  Height = 20
  Placement = pos=(0,0,36.15) rot=(0,0,1;0rad)
  Radius = 14
FEATURE [Part::Cylinder] Cylinder035
  Angle = 360
  AttacherType = Attacher::AttachEngine3D
  Height = 10
  Placement = pos=(0,0,36.15) rot=(0,0,1;0rad)
  Radius = 4
FEATURE [Part::MultiFuse] Fusion078  label="removeToCreteHoleForPlugHousing024"
  Placement = pos=(70,19,36) rot=(0,1,0;1.5708rad)
  Shapes = -> [Cylinder034,Cylinder035]
FEATURE [Part::MultiFuse] Fusion079  label="removeToCreatePlugHousingBottomBit001"
  Shapes = -> [Fusion078,Fusion077]
FEATURE [Part::Extrusion] Extrude040  label="bottomPlugHousingBit"
  Base = -> Sketch049
  Dir = (0,0,1)
  DirMode = 2
  FaceMakerClass = Part::FaceMakerBullseye
  LengthFwd = 72
  LengthRev = 0
  Solid = true
  Symmetric = false
FEATURE [Part::Cut] Cut034  label="bottomPlugHousingBit001"
  Base = -> Extrude040
  Placement = pos=(-0.09,0,0) rot=(0,0,1;0rad)
  Tool = -> Fusion079
FEATURE [Part::Box] Box023  label="Cube014"
  AttacherType = Attacher::AttachEngine3D
  Height = 16
  Length = 8
  Placement = pos=(12.7,31.52,28) rot=(0,0,1;0rad)
  Width = 4
FEATURE [Part::Cylinder] Cylinder036
  Angle = 360
  AttacherType = Attacher::AttachEngine3D
  Height = 10
  Placement = pos=(0,0,36.15) rot=(0,0,1;0rad)
  Radius = 4
FEATURE [Part::Cylinder] Cylinder037
  Angle = 360
  AttacherType = Attacher::AttachEngine3D
  Height = 20
  Placement = pos=(0,0,36.15) rot=(0,0,1;0rad)
  Radius = 8.2
FEATURE [Part::MultiFuse] Fusion080  label="removeToCreteHoleForPlugHousing025"
  Placement = pos=(-42,19,36) rot=(0,1,0;1.5708rad)
  Shapes = -> [Cylinder037,Cylinder036]
FEATURE [Sketcher::SketchObject] Sketch050  label="topSketch012"
  FullyConstrained = true
  sketch-geometry (4):
    g0: LineSegment StartX=16.8446 StartY=31.512 StartZ=0 EndX=16.3251 EndY=34.4666 EndZ=0
    g1: ArcOfCircle CenterX=19 CenterY=19.2524 CenterZ=0 NormalX=0 NormalY=0 NormalZ=1 AngleXU=0 Radius=15.4476 StartAngle=1.74483 EndAngle=2.72717
    g2: ArcOfCircle CenterX=19 CenterY=19.2524 CenterZ=0 NormalX=0 NormalY=0 NormalZ=1 AngleXU=0 Radius=12.4476 StartAngle=1.74483 EndAngle=2.73189
    g3: LineSegment StartX=4.86004 StartY=25.4725 StartZ=0 EndX=7.58253 EndY=24.2107 EndZ=0
  constraints (7):
    c: Block(g0)
    c: Coincident(g1,g0)
    c: Coincident(g2,g0)
    c: Coincident(g3,g1)
    c: Coincident(g3,g2)
    c: Block(g1)
    c: Block(g2)
FEATURE [Part::Extrusion] Extrude041
  Base = -> Sketch050
  Dir = (0,0,1)
  DirMode = 2
  FaceMakerClass = Part::FaceMakerBullseye
  LengthFwd = 10.6
  LengthRev = 0
  Placement = pos=(0,0,31) rot=(0,0,1;0rad)
  Solid = true
  Symmetric = false
FEATURE [Part::Cut] Cut035
  Base = -> Extrude041
  Placement = pos=(0,0,-0.3) rot=(0,0,1;0rad)
  Tool = -> Fusion080
FEATURE [Part::Cut] Cut036
  Base = -> Box023
  Tool = -> Cut035
FEATURE [Part::Fillet] Fillet027
  Base = -> Cut036
  Edges = 1 edges r=0.7: [Edge13]
FEATURE [Part::Fillet] Fillet028
  Base = -> Fillet027
  Edges = 1 edges r=0.7: [Edge13]
FEATURE [Part::Fillet] Fillet029
  Base = -> Fillet028
  Edges = 1 edges r=0.7: [Edge16]
FEATURE [Part::Fillet] Fillet030
  Base = -> Fillet029
  Edges = 1 edges r=0.7: [Edge11]
FEATURE [Part::Fillet] Fillet031
  Base = -> Fillet030
  Edges = 1 edges r=0.7: [Edge10]
FEATURE [Part::Fillet] Fillet032
  Base = -> Fillet031
  Edges = 1 edges r=1.2: [Edge5]
FEATURE [Part::Fillet] Fillet033
  Base = -> Fillet032
  Edges = 1 edges r=1.2: [Edge12]
FEATURE [Part::Fillet] Fillet034  label="wireHousingRetainer"
  Base = -> Fillet033
  Edges = 1 edges r=2: [Edge1]
  Placement = pos=(0.3,0,0) rot=(0,0,1;0rad)
FEATURE [Part::Feature] Face099
  shape: bbox 3.5 x 17.8 x 2e-07 mm, 1 faces, 0 solids (baked)
FEATURE [Part::Revolution] Revolve107  label="removeToCreateScrewAndThreadedInsertHole034"
  Angle = 360
  Axis = (0,1,0)
  Base = (0,0,0)
  FaceMakerClass = Part::FaceMakerBullseye
  Placement = pos=(12.5,0,10) rot=(0,0,1;0rad)
  Solid = false
  Source = -> Face099
  Symmetric = false
FEATURE [Part::Feature] Face100
  shape: bbox 3.5 x 17.8 x 2e-07 mm, 1 faces, 0 solids (baked)
FEATURE [Part::Revolution] Revolve108  label="removeToCreateScrewAndThreadedInsertHole035"
  Angle = 360
  Axis = (0,1,0)
  Base = (0,0,0)
  FaceMakerClass = Part::FaceMakerBullseye
  Placement = pos=(12.5,0,62) rot=(0,0,1;0rad)
  Solid = false
  Source = -> Face100
  Symmetric = false
FEATURE [Part::Feature] Face101
  shape: bbox 3.5 x 17.8 x 2e-07 mm, 1 faces, 0 solids (baked)
FEATURE [Part::Revolution] Revolve109  label="removeToCreateScrewAndThreadedInsertHole036"
  Angle = 360
  Axis = (0,1,0)
  Base = (0,0,0)
  FaceMakerClass = Part::FaceMakerBullseye
  Placement = pos=(89.5,0,68.5) rot=(0,0,1;0rad)
  Solid = false
  Source = -> Face101
  Symmetric = false
FEATURE [Part::Feature] Face102
  shape: bbox 3.5 x 17.8 x 2e-07 mm, 1 faces, 0 solids (baked)
FEATURE [Part::Revolution] Revolve110  label="removeToCreateScrewAndThreadedInsertHole037"
  Angle = 360
  Axis = (0,1,0)
  Base = (0,0,0)
  FaceMakerClass = Part::FaceMakerBullseye
  Placement = pos=(89.5,0,3.5) rot=(0,0,1;0rad)
  Solid = false
  Source = -> Face102
  Symmetric = false
FEATURE [Part::Feature] Face103
  shape: bbox 3.5 x 17.8 x 2e-07 mm, 1 faces, 0 solids (baked)
FEATURE [Part::Revolution] Revolve111  label="removeToCreateScrewAndThreadedInsertHole038"
  Angle = 360
  Axis = (0,1,0)
  Base = (0,0,0)
  FaceMakerClass = Part::FaceMakerBullseye
  Placement = pos=(109.5,4.7,3.5) rot=(0,0,1;0rad)
  Solid = false
  Source = -> Face103
  Symmetric = false
FEATURE [Part::Feature] Face104
  shape: bbox 3.5 x 17.8 x 2e-07 mm, 1 faces, 0 solids (baked)
FEATURE [Part::Revolution] Revolve112  label="removeToCreateScrewAndThreadedInsertHole039"
  Angle = 360
  Axis = (0,1,0)
  Base = (0,0,0)
  FaceMakerClass = Part::FaceMakerBullseye
  Placement = pos=(109.5,4.7,68.5) rot=(0,0,1;0rad)
  Solid = false
  Source = -> Face104
  Symmetric = false
FEATURE [Part::MultiFuse] Fusion081  label="removeToCreateScrewAndThreadedInsertHole040"
  Shapes = -> [Revolve107,Revolve108,Revolve109,Revolve110,Revolve111,Revolve112]
FEATURE [Part::MultiFuse] Fusion082  label="casePillars002"
  Shapes = -> [Revolve094,Revolve092,Revolve090,Revolve089,Revolve091,Revolve093]
FEATURE [Part::Cut] Cut037  label="casePillars003"
  Base = -> Fusion082
  Tool = -> Fusion081
FEATURE [Sketcher::SketchObject] Sketch051
  FullyConstrained = true
  Placement = pos=(117,19,0) rot=(0.57735,0.57735,0.57735;2.0944rad)
  sketch-geometry (48):
    g0: LineSegment StartX=-49.19 StartY=69.25 StartZ=0 EndX=-49.19 EndY=66.25 EndZ=0
    g1: LineSegment StartX=-49.19 StartY=63.5 StartZ=0 EndX=-49.19 EndY=60.5 EndZ=0
    g2: LineSegment StartX=-49.19 StartY=57.75 StartZ=0 EndX=-49.19 EndY=54.75 EndZ=0
    g3: LineSegment StartX=-49.19 StartY=52 StartZ=0 EndX=-49.19 EndY=49 EndZ=0
    g4: LineSegment StartX=-49.19 StartY=46.25 StartZ=0 EndX=-49.19 EndY=43.25 EndZ=0
    g5: LineSegment StartX=-49.19 StartY=40.5 StartZ=0 EndX=-49.19 EndY=37.5 EndZ=0
    g6: LineSegment StartX=-49.19 StartY=34.5 StartZ=0 EndX=-49.19 EndY=31.5 EndZ=0
    g7: LineSegment StartX=-49.19 StartY=28.75 StartZ=0 EndX=-49.19 EndY=25.75 EndZ=0
    g8: LineSegment StartX=-49.19 StartY=23 StartZ=0 EndX=-49.19 EndY=20 EndZ=0
    g9: LineSegment StartX=-49.19 StartY=17.25 StartZ=0 EndX=-49.19 EndY=14.25 EndZ=0
    g10: LineSegment StartX=-49.19 StartY=11.5 StartZ=0 EndX=-49.19 EndY=8.5 EndZ=0
    g11: LineSegment StartX=-49.19 StartY=5.75 StartZ=0 EndX=-49.19 EndY=2.75 EndZ=0
    g12: ArcOfCircle CenterX=-1.5 CenterY=67.75 CenterZ=0 NormalX=0 NormalY=0 NormalZ=1 AngleXU=0 Radius=1.5 StartAngle=4.71239 EndAngle=7.85398
    g13: ArcOfCircle CenterX=-1.5 CenterY=62 CenterZ=0 NormalX=0 NormalY=0 NormalZ=1 AngleXU=0 Radius=1.5 StartAngle=4.71239 EndAngle=7.85398
    g14: ArcOfCircle CenterX=-1.5 CenterY=56.25 CenterZ=0 NormalX=0 NormalY=0 NormalZ=1 AngleXU=0 Radius=1.5 StartAngle=4.71239 EndAngle=7.85398
    g15: ArcOfCircle CenterX=-11.49 CenterY=50.5 CenterZ=0 NormalX=0 NormalY=0 NormalZ=1 AngleXU=0 Radius=1.5 StartAngle=4.71239 EndAngle=7.85398
    g16: ArcOfCircle CenterX=-16.28 CenterY=44.75 CenterZ=0 NormalX=0 NormalY=0 NormalZ=1 AngleXU=0 Radius=1.5 StartAngle=4.71239 EndAngle=7.85398
    g17: ArcOfCircle CenterX=-18.2337 CenterY=39 CenterZ=0 NormalX=0 NormalY=0 NormalZ=1 AngleXU=0 Radius=1.5 StartAngle=4.71485 EndAngle=7.85398
    g18: ArcOfCircle CenterX=-16.2837 CenterY=27.25 CenterZ=0 NormalX=0 NormalY=0 NormalZ=1 AngleXU=0 Radius=1.5 StartAngle=4.71485 EndAngle=7.85398
    g19: ArcOfCircle CenterX=-18.2337 CenterY=33 CenterZ=0 NormalX=0 NormalY=0 NormalZ=1 AngleXU=0 Radius=1.5 StartAngle=4.71485 EndAngle=7.85398
    g20: ArcOfCircle CenterX=-11.49 CenterY=21.5 CenterZ=0 NormalX=0 NormalY=0 NormalZ=1 AngleXU=0 Radius=1.5 StartAngle=4.71239 EndAngle=7.85398
    g21: ArcOfCircle CenterX=-1.5 CenterY=4.25 CenterZ=0 NormalX=0 NormalY=0 NormalZ=1 AngleXU=0 Radius=1.5 StartAngle=4.71239 EndAngle=7.85398
    g22: ArcOfCircle CenterX=-1.5 CenterY=10 CenterZ=0 NormalX=0 NormalY=0 NormalZ=1 AngleXU=0 Radius=1.5 StartAngle=4.71239 EndAngle=7.85398
    g23: ArcOfCircle CenterX=-1.5 CenterY=15.75 CenterZ=0 NormalX=0 NormalY=0 NormalZ=1 AngleXU=0 Radius=1.5 StartAngle=4.71239 EndAngle=7.85398
    g24: LineSegment StartX=-49.19 StartY=69.25 StartZ=0 EndX=-1.5 EndY=69.25 EndZ=0
    g25: LineSegment StartX=-49.19 StartY=66.25 StartZ=0 EndX=-1.5 EndY=66.25 EndZ=0
    g26: LineSegment StartX=-49.19 StartY=63.5 StartZ=0 EndX=-1.5 EndY=63.5 EndZ=0
    g27: LineSegment StartX=-49.19 StartY=60.5 StartZ=0 EndX=-1.5 EndY=60.5 EndZ=0
    g28: LineSegment StartX=-49.19 StartY=57.75 StartZ=0 EndX=-1.5 EndY=57.75 EndZ=0
    g29: LineSegment StartX=-49.19 StartY=54.75 StartZ=0 EndX=-1.5 EndY=54.75 EndZ=0
    g30: LineSegment StartX=-49.19 StartY=52 StartZ=0 EndX=-11.49 EndY=52 EndZ=0
    g31: LineSegment StartX=-49.19 StartY=49 StartZ=0 EndX=-11.49 EndY=49 EndZ=0
    g32: LineSegment StartX=-49.19 StartY=46.25 StartZ=0 EndX=-16.28 EndY=46.25 EndZ=0
    g33: LineSegment StartX=-49.19 StartY=43.25 StartZ=0 EndX=-16.28 EndY=43.25 EndZ=0
    g34: LineSegment StartX=-49.19 StartY=40.5 StartZ=0 EndX=-18.2337 EndY=40.5 EndZ=0
    g35: LineSegment StartX=-49.19 StartY=37.5 StartZ=0 EndX=-18.23 EndY=37.5 EndZ=0
    g36: LineSegment StartX=-49.19 StartY=34.5 StartZ=0 EndX=-18.2337 EndY=34.5 EndZ=0
    g37: LineSegment StartX=-49.19 StartY=31.5 StartZ=0 EndX=-18.23 EndY=31.5 EndZ=0
    g38: LineSegment StartX=-49.19 StartY=28.75 StartZ=0 EndX=-16.2837 EndY=28.75 EndZ=0
    g39: LineSegment StartX=-49.19 StartY=25.75 StartZ=0 EndX=-16.28 EndY=25.75 EndZ=0
    g40: LineSegment StartX=-49.19 StartY=23 StartZ=0 EndX=-11.49 EndY=23 EndZ=0
    g41: LineSegment StartX=-49.19 StartY=20 StartZ=0 EndX=-11.49 EndY=20 EndZ=0
    g42: LineSegment StartX=-49.19 StartY=17.25 StartZ=0 EndX=-1.5 EndY=17.25 EndZ=0
    g43: LineSegment StartX=-49.19 StartY=14.25 StartZ=0 EndX=-1.5 EndY=14.25 EndZ=0
    g44: LineSegment StartX=-49.19 StartY=11.5 StartZ=0 EndX=-1.5 EndY=11.5 EndZ=0
    g45: LineSegment StartX=-49.19 StartY=8.5 StartZ=0 EndX=-1.5 EndY=8.5 EndZ=0
    g46: LineSegment StartX=-49.19 StartY=5.75 StartZ=0 EndX=-1.5 EndY=5.75 EndZ=0
    g47: LineSegment StartX=-49.19 StartY=2.75 StartZ=0 EndX=-1.5 EndY=2.75 EndZ=0
  constraints (120):
    c: Vertical(g0)
    c: Distance(g0) = 3
    c: Block(g0)
    c: Vertical(g1)
    c: Distance(g1) = 3
    c: Vertical(g2)
    c: Equal(g0,g2) = 3
    c: Block(g2)
    c: Vertical(g3)
    c: Equal(g1,g3) = 3
    c: Vertical(g4)
    c: Equal(g0,g4) = 3
    c: Block(g4)
    c: Vertical(g5)
    c: Equal(g1,g5) = 3
    c: Vertical(g6)
    c: Equal(g0,g6) = 3
    c: Block(g6)
    c: Vertical(g7)
    c: Equal(g1,g7) = 3
    c: Vertical(g8)
    c: Equal(g0,g8) = 3
    c: Block(g8)
    c: Vertical(g9)
    c: Equal(g1,g9) = 3
    c: Vertical(g10)
    c: Equal(g0,g10) = 3
    c: Block(g10)
    c: Vertical(g11)
    c: Equal(g1,g11) = 3
    c: Block(g12)
    c: Block(g13)
    c: Block(g14)
    c: Block(g15)
    c: Block(g16)
    c: Block(g17)
    c: Block(g18)
    c: Block(g19)
    c: Block(g20)
    c: Block(g21)
    c: Block(g22)
    c: Block(g23)
    c: Block(g11)
    c: Block(g9)
    c: Block(g7)
    c: Block(g5)
    c: Block(g3)
    c: Block(g1)
    c: Coincident(g24,g0)
    c: Coincident(g24,g12)
    c: Horizontal(g24)
    c: Coincident(g25,g0)
    c: Coincident(g25,g12)
    c: Horizontal(g25)
    c: Coincident(g26,g1)
    c: Coincident(g26,g13)
    c: Horizontal(g26)
    c: Coincident(g27,g1)
    c: Coincident(g27,g13)
    c: Horizontal(g27)
    c: Coincident(g28,g2)
    c: Coincident(g28,g14)
    c: Horizontal(g28)
    c: Coincident(g29,g2)
    c: Coincident(g29,g14)
    c: Horizontal(g29)
    c: Coincident(g30,g3)
    c: Coincident(g30,g15)
    c: Horizontal(g30)
    c: Coincident(g31,g3)
    c: Coincident(g31,g15)
    c: Horizontal(g31)
    c: Coincident(g32,g4)
    c: Coincident(g32,g16)
    c: Horizontal(g32)
    c: Coincident(g33,g4)
    c: Coincident(g33,g16)
    c: Horizontal(g33)
    c: Coincident(g34,g5)
    c: Coincident(g34,g17)
    c: Horizontal(g34)
    c: Coincident(g35,g5)
    c: Coincident(g35,g17)
    c: Horizontal(g35)
    c: Coincident(g36,g6)
    c: Coincident(g36,g19)
    c: Horizontal(g36)
    c: Coincident(g37,g6)
    c: Coincident(g37,g19)
    c: Horizontal(g37)
    c: Coincident(g38,g7)
    c: Coincident(g38,g18)
    c: Horizontal(g38)
    c: Coincident(g39,g7)
    c: Coincident(g39,g18)
    c: Horizontal(g39)
    c: Coincident(g40,g8)
    c: Coincident(g40,g20)
    c: Horizontal(g40)
    c: Coincident(g41,g8)
    c: Coincident(g41,g20)
    c: Horizontal(g41)
    c: Coincident(g42,g9)
    c: Coincident(g42,g23)
    c: Horizontal(g42)
    c: Coincident(g43,g9)
    c: Coincident(g43,g23)
    c: Horizontal(g43)
    c: Coincident(g44,g10)
    c: Coincident(g44,g22)
    c: Horizontal(g44)
    c: Coincident(g45,g10)
    c: Coincident(g45,g22)
    c: Horizontal(g45)
    c: Coincident(g46,g11)
    c: Coincident(g46,g21)
    c: Horizontal(g46)
    c: Coincident(g47,g11)
    c: Coincident(g47,g21)
    c: Horizontal(g47)
FEATURE [Part::Extrusion] Extrude042
  Base = -> Sketch051
  Dir = (1,-2e-16,2e-16)
  DirMode = 2
  FaceMakerClass = Part::FaceMakerBullseye
  LengthFwd = 19
  LengthRev = 0
  Placement = pos=(-19,0,0) rot=(0,0,1;0rad)
  Solid = true
  Symmetric = false
FEATURE [Part::Fillet] Fillet035  label="removeToCreateVentalationHoles"
  Base = -> Extrude042
  Edges = <same value as first occurrence — deduplicated (x6 in doc)>
  Placement = pos=(7,0,0) rot=(0,0,1;0rad)
FEATURE [Part::Cut] Cut038  label="top017"
  Base = -> Cut033
  Tool = -> Fillet035
FEATURE [Sketcher::SketchObject] Sketch052  label="bottomSketch001"
  FullyConstrained = true
  sketch-geometry (45):
    g0: LineSegment StartX=6.29999 StartY=8 StartZ=0 EndX=3.29999 EndY=8 EndZ=0
    g1: LineSegment StartX=3.29999 StartY=8 StartZ=0 EndX=3.29999 EndY=-6.03275e-07 EndZ=0
    g2: ArcOfCircle CenterX=8.29999 CenterY=5 CenterZ=0 NormalX=0 NormalY=0 NormalZ=1 AngleXU=0 Radius=2 StartAngle=3.14159 EndAngle=4.71239
    g3: LineSegment StartX=6.29999 StartY=8 StartZ=0 EndX=6.29999 EndY=5 EndZ=0
    g4: ArcOfCircle CenterX=105 CenterY=19 CenterZ=0 NormalX=0 NormalY=0 NormalZ=1 AngleXU=0 Radius=12.7 StartAngle=4.71239 EndAngle=5.94289
    g5-g11: Circle x7 (B-spline internal-alignment scaffolding for g12; pole/knot coordinates omitted)
    g12: BSplineCurve PolesCount=7 KnotsCount=5 Degree=3 IsPeriodic=0
    g13-g17: GeomPoint x5 (B-spline internal-alignment scaffolding for g12; pole/knot coordinates omitted)
    g18: ArcOfCircle CenterX=105 CenterY=19 CenterZ=0 NormalX=0 NormalY=0 NormalZ=1 AngleXU=0 Radius=15.7 StartAngle=5.81226 EndAngle=6.28319
    g19: BSplineCurve PolesCount=5 KnotsCount=3 Degree=3 IsPeriodic=0
    g20: LineSegment StartX=8.29999 StartY=3 StartZ=0 EndX=101.7 EndY=3 EndZ=0
    g21: LineSegment StartX=3.29999 StartY=-6.03275e-07 StartZ=0 EndX=105 EndY=-6.03275e-07 EndZ=0
    g22: LineSegment StartX=120.974 StartY=8.71251 StartZ=0 EndX=122.332 EndY=7.83778 EndZ=0
    g23: LineSegment StartX=105 StartY=-6.03274e-07 StartZ=0 EndX=113 EndY=-6.03274e-07 EndZ=0
    g24: ArcOfCircle CenterX=105 CenterY=19 CenterZ=0 NormalX=0 NormalY=0 NormalZ=1 AngleXU=0 Radius=20.6155 StartAngle=5.11091 EndAngle=5.71103
    g25: ArcOfCircle CenterX=117.7 CenterY=19 CenterZ=0 NormalX=0 NormalY=0 NormalZ=1 AngleXU=0 Radius=3 StartAngle=1.2e-15 EndAngle=2.10468
    g26: Circle CenterX=116.345 CenterY=16.3232 CenterZ=0 NormalX=0 NormalY=0 NormalZ=1 AngleXU=0 Radius=1
    g27: Circle CenterX=117.24 CenterY=15.7584 CenterZ=0 NormalX=0 NormalY=0 NormalZ=1 AngleXU=0 Radius=1
    g28: Circle CenterX=116.972 CenterY=14.7612 CenterZ=0 NormalX=0 NormalY=0 NormalZ=1 AngleXU=0 Radius=1
    g29: BSplineCurve PolesCount=3 KnotsCount=2 Degree=2 IsPeriodic=0
    g30: GeomPoint X=116.345 Y=16.3232 Z=0
    g31: GeomPoint X=116.972 Y=14.7612 Z=0
    g32: Circle CenterX=115.828 CenterY=17.157 CenterZ=0 NormalX=0 NormalY=0 NormalZ=1 AngleXU=0 Radius=1
    g33: Circle CenterX=115.841 CenterY=16.639 CenterZ=0 NormalX=0 NormalY=0 NormalZ=1 AngleXU=0 Radius=1
    g34: Circle CenterX=116.345 CenterY=16.3232 CenterZ=0 NormalX=0 NormalY=0 NormalZ=1 AngleXU=0 Radius=1
    g35: BSplineCurve PolesCount=3 KnotsCount=2 Degree=2 IsPeriodic=0
    g36: GeomPoint X=115.828 Y=17.157 Z=0
    g37: GeomPoint X=116.345 Y=16.3232 Z=0
    g38: LineSegment StartX=115.828 StartY=17.157 StartZ=0 EndX=115.828 EndY=20.8307 EndZ=0
    g39: Circle CenterX=115.828 CenterY=20.8307 CenterZ=0 NormalX=0 NormalY=0 NormalZ=1 AngleXU=0 Radius=1
    g40: Circle CenterX=115.831 CenterY=21.3396 CenterZ=0 NormalX=0 NormalY=0 NormalZ=1 AngleXU=0 Radius=1
    g41: Circle CenterX=116.173 CenterY=21.5825 CenterZ=0 NormalX=0 NormalY=0 NormalZ=1 AngleXU=0 Radius=1
    g42: BSplineCurve PolesCount=3 KnotsCount=2 Degree=2 IsPeriodic=0
    g43: GeomPoint X=115.828 Y=20.8307 Z=0
    g44: GeomPoint X=116.173 Y=21.5825 Z=0
  constraints (70):
    c: Horizontal(g0)
    c: Distance(g0) = 3
    c: Coincident(g1,g0)
    c: Vertical(g1)
    c: Block(g2)
    c: Block(g0)
    c: Coincident(g3,g0)
    c: Coincident(g3,g2)
    c: Vertical(g3)
    c: Block(g1)
    c: Block(g4)
    c: Coincident(g19,g4)
    c: Block(g19)
    c: Equal(g5, g6-g11) x6
    c: InternalAlignment(g5-g11 -> g12) x7
    c: InternalAlignment(g13-g17 -> g12) x5
    c: Block(g12)
    c: Coincident(g18,g12)
    c: Block(g18)
    c: Coincident(g20,g2)
    c: Coincident(g20,g19)
    c: Horizontal(g20)
    c: Distance(g20) = 93.4
    c: Coincident(g21,g1)
    c: Horizontal(g21)
    c: Distance(g21) = 101.7
    c: Horizontal(g23)
    c: Distance(g23) = 8
    c: Coincident(g24,g23)
    c: Block(g23)
    c: Coincident(g22,g24)
    c: Block(g24)
    c: Block(g22)
    c: Distance(g22) = 1.61553
    c: Coincident(g25,g18)
    c: Block(g25)
    c: Weight(g26) = 1
    c: Equal(g26,g27)
    c: Equal(g26,g28)
    c: Coincident(g29,g4)
    c: InternalAlignment(g26,g29)
    c: InternalAlignment(g27,g29)
    c: InternalAlignment(g28,g29)
    c: InternalAlignment(g30,g29)
    c: InternalAlignment(g31,g29)
    c: Block(g29)
    c: Weight(g32) = 1
    c: Equal(g32,g33)
    c: Equal(g32,g34)
    c: Coincident(g35,g29)
    c: InternalAlignment(g32,g35)
    c: InternalAlignment(g33,g35)
    c: InternalAlignment(g34,g35)
    c: InternalAlignment(g36,g35)
    c: InternalAlignment(g37,g35)
    c: Block(g35)
    c: Coincident(g38,g35)
    c: Vertical(g38)
    c: Block(g38)
    c: Coincident(g42,g38)
    c: Weight(g39) = 1
    c: Equal(g39,g40)
    c: Equal(g39,g41)
    c: Coincident(g42,g25)
    c: InternalAlignment(g39,g42)
    c: InternalAlignment(g40,g42)
    c: InternalAlignment(g41,g42)
    c: InternalAlignment(g43,g42)
    c: InternalAlignment(g44,g42)
    c: Block(g42)
FEATURE [Part::Extrusion] Extrude043  label="bottom010"
  Base = -> Sketch052
  Dir = (0,0,1)
  DirMode = 2
  FaceMakerClass = Part::FaceMakerBullseye
  LengthFwd = 71.4
  LengthRev = 0
  Placement = pos=(0,0,0.3) rot=(0,0,1;0rad)
  Solid = true
  Symmetric = false
FEATURE [Sketcher::SketchObject] Sketch053  label="topSketch013"
  FullyConstrained = true
  sketch-geometry (22):
    g0: LineSegment StartX=5.21097e-06 StartY=3 StartZ=0 EndX=5.21097e-06 EndY=19 EndZ=0
    g1: ArcOfCircle CenterX=19 CenterY=19 CenterZ=0 NormalX=0 NormalY=0 NormalZ=1 AngleXU=0 Radius=19 StartAngle=1.5708 EndAngle=3.14159
    g2: ArcOfCircle CenterX=19 CenterY=19 CenterZ=0 NormalX=0 NormalY=0 NormalZ=1 AngleXU=0 Radius=16 StartAngle=1.5708 EndAngle=3.14159
    g3: LineSegment StartX=114 StartY=35 StartZ=0 EndX=19 EndY=35 EndZ=0
    g4: LineSegment StartX=5.21097e-06 StartY=3 StartZ=0 EndX=5.21097e-06 EndY=0 EndZ=0
    g5: LineSegment StartX=3 StartY=0 StartZ=0 EndX=5.21097e-06 EndY=0 EndZ=0
    g6: LineSegment StartX=3 StartY=19 StartZ=0 EndX=3 EndY=0 EndZ=0
    g7: LineSegment StartX=19 StartY=38 StartZ=0 EndX=124 EndY=38 EndZ=0
    g8: Circle CenterX=119 CenterY=35 CenterZ=0 NormalX=0 NormalY=0 NormalZ=1 AngleXU=0 Radius=1
    g9: Circle CenterX=121 CenterY=35 CenterZ=0 NormalX=0 NormalY=0 NormalZ=1 AngleXU=0 Radius=1
    g10: Circle CenterX=121 CenterY=33 CenterZ=0 NormalX=0 NormalY=0 NormalZ=1 AngleXU=0 Radius=1
    g11: BSplineCurve PolesCount=3 KnotsCount=2 Degree=2 IsPeriodic=0
    g12: GeomPoint X=119 Y=35 Z=0
    g13: GeomPoint X=121 Y=33 Z=0
    g14: LineSegment StartX=119 StartY=35 StartZ=0 EndX=114 EndY=35 EndZ=0
    g15: ArcOfCircle CenterX=105 CenterY=19 CenterZ=0 NormalX=0 NormalY=0 NormalZ=1 AngleXU=0 Radius=16 StartAngle=5.60905 EndAngle=6.28319
    g16: LineSegment StartX=121 StartY=33 StartZ=0 EndX=121 EndY=19 EndZ=0
    g17: LineSegment StartX=117.5 StartY=9.01251 StartZ=0 EndX=121.163 EndY=9.0125 EndZ=0
    g18: ArcOfCircle CenterX=105 CenterY=19 CenterZ=0 NormalX=0 NormalY=0 NormalZ=1 AngleXU=0 Radius=20.6155 StartAngle=5.7297 EndAngle=6.28319
    g19: LineSegment StartX=121.163 StartY=9.0125 StartZ=0 EndX=122.538 EndY=8.16329 EndZ=0
    g20: LineSegment StartX=124 StartY=38 StartZ=0 EndX=125.616 EndY=38 EndZ=0
    g21: LineSegment StartX=125.616 StartY=19 StartZ=0 EndX=125.616 EndY=38 EndZ=0
  constraints (50):
    c: Vertical(g0)
    c: Block(g0)
    c: Coincident(g1,g0)
    c: Block(g1)
    c: Coincident(g2,g1)
    c: Block(g2)
    c: Coincident(g3,g2)
    c: Horizontal(g3)
    c: Tangent(g3,g2)
    c: Coincident(g4,g0)
    c: Distance(g4) = 3
    c: Vertical(g4)
    c: Coincident(g5,g4)
    c: Horizontal(g5)
    c: Coincident(g6,g2)
    c: Coincident(g6,g5)
    c: Vertical(g6)
    c: Horizontal(g7)
    c: Distance(g7) = 105
    c: Coincident(g7,g1)
    c: Block(g3)
    c: Weight(g8) = 1
    c: Equal(g8,g9)
    c: Equal(g8,g10)
    c: InternalAlignment(g8,g11)
    c: InternalAlignment(g9,g11)
    c: InternalAlignment(g10,g11)
    c: InternalAlignment(g12,g11)
    c: InternalAlignment(g13,g11)
    c: Block(g11)
    c: Coincident(g14,g11)
    c: Coincident(g14,g3)
    c: Horizontal(g14)
    c: Block(g15)
    c: Coincident(g16,g11)
    c: Coincident(g16,g15)
    c: Vertical(g16)
    c: Distance(g16) = 14
    c: Coincident(g17,g15)
    c: Block(g18)
    c: Coincident(g19,g18)
    c: Coincident(g20,g7)
    c: Horizontal(g20)
    c: Vertical(g21)
    c: Coincident(g20,g21)
    c: Block(g20)
    c: Block(g21)
    c: Block(g19)
    c: Block(g17)
    c: Distance(g20) = 1.61553
FEATURE [Part::Extrusion] Extrude044
  Base = -> Sketch053
  Dir = (0,0,1)
  DirMode = 2
  FaceMakerClass = Part::FaceMakerBullseye
  LengthFwd = 72
  LengthRev = 0
  Solid = true
  Symmetric = false
FEATURE [Part::Fillet] Fillet036  label="top018"
  Base = -> Extrude044
  Edges = 1 edges r=2: [Edge41]
FEATURE [Sketcher::SketchObject] Sketch054
  FullyConstrained = false
  Placement = pos=(0,0,0) rot=(1,0,0;1.5708rad)
  sketch-geometry (24):
    g0: ArcOfCircle CenterX=-4 CenterY=-10.5 CenterZ=0 NormalX=0 NormalY=0 NormalZ=1 AngleXU=0 Radius=1.5 StartAngle=6e-16 EndAngle=3.14159
    g1: ArcOfCircle CenterX=-34.2 CenterY=-10.5 CenterZ=0 NormalX=0 NormalY=0 NormalZ=1 AngleXU=0 Radius=1.5 StartAngle=0 EndAngle=3.14159
    g2: ArcOfCircle CenterX=-34.2 CenterY=-27.7 CenterZ=0 NormalX=0 NormalY=0 NormalZ=1 AngleXU=0 Radius=1.5 StartAngle=3.14159 EndAngle=6.28319
    g3: ArcOfCircle CenterX=-4 CenterY=-27.7 CenterZ=0 NormalX=0 NormalY=0 NormalZ=1 AngleXU=0 Radius=1.5 StartAngle=3.1416 EndAngle=6.28319
    g4: ArcOfCircle CenterX=-10 CenterY=-4.3 CenterZ=0 NormalX=0 NormalY=0 NormalZ=1 AngleXU=0 Radius=1.5 StartAngle=2e-16 EndAngle=3.14159
    g5: ArcOfCircle CenterX=-16.1 CenterY=-1.8 CenterZ=0 NormalX=0 NormalY=0 NormalZ=1 AngleXU=0 Radius=1.5 StartAngle=5e-16 EndAngle=3.14159
    g6: ArcOfCircle CenterX=-22.1 CenterY=-1.8 CenterZ=0 NormalX=0 NormalY=0 NormalZ=1 AngleXU=0 Radius=1.5 StartAngle=5e-16 EndAngle=3.14159
    g7: ArcOfCircle CenterX=-28.2 CenterY=-4.3 CenterZ=0 NormalX=0 NormalY=0 NormalZ=1 AngleXU=0 Radius=1.5 StartAngle=2e-16 EndAngle=3.14159
    g8: ArcOfCircle CenterX=-10 CenterY=-33.9 CenterZ=0 NormalX=0 NormalY=0 NormalZ=1 AngleXU=0 Radius=1.5 StartAngle=3.14159 EndAngle=6.28319
    g9: ArcOfCircle CenterX=-16.1 CenterY=-36.4 CenterZ=0 NormalX=0 NormalY=0 NormalZ=1 AngleXU=0 Radius=1.5 StartAngle=3.14159 EndAngle=6.28319
    g10: ArcOfCircle CenterX=-22.1 CenterY=-36.4 CenterZ=0 NormalX=0 NormalY=0 NormalZ=1 AngleXU=0 Radius=1.5 StartAngle=3.14159 EndAngle=6.28319
    g11: ArcOfCircle CenterX=-28.2 CenterY=-33.9 CenterZ=0 NormalX=0 NormalY=0 NormalZ=1 AngleXU=0 Radius=1.5 StartAngle=3.14159 EndAngle=6.28319
    g12: LineSegment StartX=-35.7 StartY=-10.5 StartZ=0 EndX=-35.7 EndY=-27.7 EndZ=0
    g13: LineSegment StartX=-32.7 StartY=-10.5 StartZ=0 EndX=-32.7 EndY=-27.7 EndZ=0
    g14: LineSegment StartX=-29.7 StartY=-33.9 StartZ=0 EndX=-29.7 EndY=-4.3 EndZ=0
    g15: LineSegment StartX=-26.7 StartY=-33.9 StartZ=0 EndX=-26.7 EndY=-4.3 EndZ=0
    g16: LineSegment StartX=-2.5 StartY=-10.5 StartZ=0 EndX=-2.5 EndY=-27.7 EndZ=0
    g17: LineSegment StartX=-8.5 StartY=-4.3 StartZ=0 EndX=-8.5 EndY=-33.9 EndZ=0
    g18: LineSegment StartX=-5.5 StartY=-10.5 StartZ=0 EndX=-5.5 EndY=-27.7 EndZ=0
    g19: LineSegment StartX=-11.5 StartY=-4.3 StartZ=0 EndX=-11.5 EndY=-33.9 EndZ=0
    g20: LineSegment StartX=-14.6 StartY=-1.8 StartZ=0 EndX=-14.6 EndY=-36.4 EndZ=0
    g21: LineSegment StartX=-17.6 StartY=-1.8 StartZ=0 EndX=-17.6 EndY=-36.4 EndZ=0
    g22: LineSegment StartX=-20.6 StartY=-36.4 StartZ=0 EndX=-20.6 EndY=-1.8 EndZ=0
    g23: LineSegment StartX=-23.6 StartY=-1.8 StartZ=0 EndX=-23.6 EndY=-36.4 EndZ=0
  constraints (48):
    c: Block(g0)
    c: Block(g1)
    c: Block(g2)
    c: Block(g3)
    c: Block(g4)
    c: Block(g5)
    c: Block(g6)
    c: Block(g7)
    c: Block(g8)
    c: Block(g9)
    c: Block(g10)
    c: Block(g11)
    c: Coincident(g12,g1)
    c: Coincident(g12,g2)
    c: Vertical(g12)
    c: Coincident(g13,g1)
    c: Coincident(g13,g2)
    c: Vertical(g13)
    c: Coincident(g14,g11)
    c: Coincident(g14,g7)
    c: Vertical(g14)
    c: Coincident(g15,g11)
    c: Coincident(g15,g7)
    c: Vertical(g15)
    c: Coincident(g16,g0)
    c: Coincident(g16,g3)
    c: Vertical(g16)
    c: Coincident(g17,g4)
    c: Coincident(g17,g8)
    c: Vertical(g17)
    c: Coincident(g18,g0)
    c: Coincident(g18,g3)
    c: Vertical(g18)
    c: Coincident(g19,g4)
    c: Coincident(g19,g8)
    c: Vertical(g19)
    c: Coincident(g20,g5)
    c: Coincident(g20,g9)
    c: Vertical(g20)
    c: Coincident(g21,g5)
    c: Coincident(g21,g9)
    c: Vertical(g21)
    c: Coincident(g22,g10)
    c: Coincident(g22,g6)
    c: Vertical(g22)
    c: Coincident(g23,g6)
    c: Coincident(g23,g10)
    c: Vertical(g23)
FEATURE [Part::Extrusion] Extrude045  label="removeToCreateFanGrillHoles003"
  Base = -> Sketch054
  Dir = (0,-1,6e-16)
  DirMode = 2
  FaceMakerClass = Part::FaceMakerBullseye
  LengthFwd = 10
  LengthRev = 0
  Placement = pos=(65.4,44,54.82) rot=(0,0,1;0rad)
  Solid = true
  Symmetric = false
FEATURE [Part::Feature] Face105 .. Face108  x4 (patterned run collapsed; names and placements below)
  shape: bbox 3.5 x 17.8 x 2e-07 mm, 1 faces, 0 solids (baked)
FEATURE [Part::Revolution] Revolve113  label="removeToCreateScrewAndThreadedInsertHole041"
  Angle = 360
  Axis = (0,1,0)
  Base = (0,0,0)
  FaceMakerClass = Part::FaceMakerBullseye
  Placement = pos=(62.3,30.3,19.7) rot=(0,0,1;0rad)
  Solid = false
  Source = -> Face105
  Symmetric = false
FEATURE [Part::Revolution] Revolve114  label="removeToCreateScrewAndThreadedInsertHole042"
  Angle = 360
  Axis = (0,1,0)
  Base = (0,0,0)
  FaceMakerClass = Part::FaceMakerBullseye
  Placement = pos=(62.3,30.3,51.7) rot=(0,0,1;0rad)
  Solid = false
  Source = -> Face106
  Symmetric = false
FEATURE [Part::Revolution] Revolve115  label="removeToCreateScrewAndThreadedInsertHole043"
  Angle = 360
  Axis = (0,1,0)
  Base = (0,0,0)
  FaceMakerClass = Part::FaceMakerBullseye
  Placement = pos=(30.3,30.3,19.7) rot=(0,0,1;0rad)
  Solid = false
  Source = -> Face107
  Symmetric = false
FEATURE [Part::Revolution] Revolve116  label="removeToCreateScrewAndThreadedInsertHole044"
  Angle = 360
  Axis = (0,1,0)
  Base = (0,0,0)
  FaceMakerClass = Part::FaceMakerBullseye
  Placement = pos=(30.3,30.3,51.7) rot=(0,0,1;0rad)
  Solid = false
  Source = -> Face108
  Symmetric = false
FEATURE [Part::MultiFuse] Fusion083  label="createThreadedInsertHolesForFan004"
  Shapes = -> [Revolve113,Revolve114,Revolve115,Revolve116]
FEATURE [Part::Box] Box024  label="removeToCreteHoleForPlugHousing026"
  AttacherType = Attacher::AttachEngine3D
  Height = 28.6
  Length = 10
  Placement = pos=(-2,0,21.7) rot=(0,0,1;0rad)
  Width = 19
FEATURE [Part::Cylinder] Cylinder038  label="removeToCreteHoleForPlugHousing027"
  Angle = 360
  AttacherType = Attacher::AttachEngine3D
  Height = 20
  Placement = pos=(-2,19,36) rot=(0,1,0;1.5708rad)
  Radius = 14.3
FEATURE [Part::MultiFuse] Fusion084  label="removeToCreteHoleForPlugHousing028"
  Shapes = -> [Box024,Cylinder038]
FEATURE [Part::Cylinder] Cylinder039
  Angle = 360
  AttacherType = Attacher::AttachEngine3D
  Height = 20
  Placement = pos=(0,0,36.15) rot=(0,0,1;0rad)
  Radius = 14.3
FEATURE [Part::Cylinder] Cylinder040
  Angle = 360
  AttacherType = Attacher::AttachEngine3D
  Height = 10
  Placement = pos=(0,0,36.15) rot=(0,0,1;0rad)
  Radius = 4
FEATURE [Part::Box] Box025  label="removeToCreteHoleForPlugHousing030"
  AttacherType = Attacher::AttachEngine3D
  Height = 28.6
  Length = 20
  Placement = pos=(106.15,0,21.7) rot=(0,0,1;0rad)
  Width = 19
FEATURE [Part::MultiFuse] Fusion086  label="removeToCreteHoleForPlugHousing031"
  Placement = pos=(70,19,36) rot=(0,1,0;1.5708rad)
  Shapes = -> [Cylinder039,Cylinder040]
FEATURE [Part::MultiFuse] Fusion085  label="removeToCreteHoleForPlugHousing029"
  Shapes = -> [Box025,Fusion086]
FEATURE [Sketcher::SketchObject] Sketch055
  FullyConstrained = true
  Placement = pos=(117,19,0) rot=(0.57735,0.57735,0.57735;2.0944rad)
  sketch-geometry (48):
    g0: LineSegment StartX=-49.19 StartY=69.25 StartZ=0 EndX=-49.19 EndY=66.25 EndZ=0
    g1: LineSegment StartX=-49.19 StartY=63.5 StartZ=0 EndX=-49.19 EndY=60.5 EndZ=0
    g2: LineSegment StartX=-49.19 StartY=57.75 StartZ=0 EndX=-49.19 EndY=54.75 EndZ=0
    g3: LineSegment StartX=-49.19 StartY=52 StartZ=0 EndX=-49.19 EndY=49 EndZ=0
    g4: LineSegment StartX=-49.19 StartY=46.25 StartZ=0 EndX=-49.19 EndY=43.25 EndZ=0
    g5: LineSegment StartX=-49.19 StartY=40.5 StartZ=0 EndX=-49.19 EndY=37.5 EndZ=0
    g6: LineSegment StartX=-49.19 StartY=34.5 StartZ=0 EndX=-49.19 EndY=31.5 EndZ=0
    g7: LineSegment StartX=-49.19 StartY=28.75 StartZ=0 EndX=-49.19 EndY=25.75 EndZ=0
    g8: LineSegment StartX=-49.19 StartY=23 StartZ=0 EndX=-49.19 EndY=20 EndZ=0
    g9: LineSegment StartX=-49.19 StartY=17.25 StartZ=0 EndX=-49.19 EndY=14.25 EndZ=0
    g10: LineSegment StartX=-49.19 StartY=11.5 StartZ=0 EndX=-49.19 EndY=8.5 EndZ=0
    g11: LineSegment StartX=-49.19 StartY=5.75 StartZ=0 EndX=-49.19 EndY=2.75 EndZ=0
    g12: ArcOfCircle CenterX=-1.5 CenterY=67.75 CenterZ=0 NormalX=0 NormalY=0 NormalZ=1 AngleXU=0 Radius=1.5 StartAngle=4.71239 EndAngle=7.85398
    g13: ArcOfCircle CenterX=-1.5 CenterY=62 CenterZ=0 NormalX=0 NormalY=0 NormalZ=1 AngleXU=0 Radius=1.5 StartAngle=4.71239 EndAngle=7.85398
    g14: ArcOfCircle CenterX=-1.5 CenterY=56.25 CenterZ=0 NormalX=0 NormalY=0 NormalZ=1 AngleXU=0 Radius=1.5 StartAngle=4.71239 EndAngle=7.85398
    g15: ArcOfCircle CenterX=-11.49 CenterY=50.5 CenterZ=0 NormalX=0 NormalY=0 NormalZ=1 AngleXU=0 Radius=1.5 StartAngle=4.71239 EndAngle=7.85398
    g16: ArcOfCircle CenterX=-16.28 CenterY=44.75 CenterZ=0 NormalX=0 NormalY=0 NormalZ=1 AngleXU=0 Radius=1.5 StartAngle=4.71239 EndAngle=7.85398
    g17: ArcOfCircle CenterX=-18.2337 CenterY=39 CenterZ=0 NormalX=0 NormalY=0 NormalZ=1 AngleXU=0 Radius=1.5 StartAngle=4.71485 EndAngle=7.85398
    g18: ArcOfCircle CenterX=-16.2837 CenterY=27.25 CenterZ=0 NormalX=0 NormalY=0 NormalZ=1 AngleXU=0 Radius=1.5 StartAngle=4.71485 EndAngle=7.85398
    g19: ArcOfCircle CenterX=-18.2337 CenterY=33 CenterZ=0 NormalX=0 NormalY=0 NormalZ=1 AngleXU=0 Radius=1.5 StartAngle=4.71485 EndAngle=7.85398
    g20: ArcOfCircle CenterX=-11.49 CenterY=21.5 CenterZ=0 NormalX=0 NormalY=0 NormalZ=1 AngleXU=0 Radius=1.5 StartAngle=4.71239 EndAngle=7.85398
    g21: ArcOfCircle CenterX=-1.5 CenterY=4.25 CenterZ=0 NormalX=0 NormalY=0 NormalZ=1 AngleXU=0 Radius=1.5 StartAngle=4.71239 EndAngle=7.85398
    g22: ArcOfCircle CenterX=-1.5 CenterY=10 CenterZ=0 NormalX=0 NormalY=0 NormalZ=1 AngleXU=0 Radius=1.5 StartAngle=4.71239 EndAngle=7.85398
    g23: ArcOfCircle CenterX=-1.5 CenterY=15.75 CenterZ=0 NormalX=0 NormalY=0 NormalZ=1 AngleXU=0 Radius=1.5 StartAngle=4.71239 EndAngle=7.85398
    g24: LineSegment StartX=-49.19 StartY=69.25 StartZ=0 EndX=-1.5 EndY=69.25 EndZ=0
    g25: LineSegment StartX=-49.19 StartY=66.25 StartZ=0 EndX=-1.5 EndY=66.25 EndZ=0
    g26: LineSegment StartX=-49.19 StartY=63.5 StartZ=0 EndX=-1.5 EndY=63.5 EndZ=0
    g27: LineSegment StartX=-49.19 StartY=60.5 StartZ=0 EndX=-1.5 EndY=60.5 EndZ=0
    g28: LineSegment StartX=-49.19 StartY=57.75 StartZ=0 EndX=-1.5 EndY=57.75 EndZ=0
    g29: LineSegment StartX=-49.19 StartY=54.75 StartZ=0 EndX=-1.5 EndY=54.75 EndZ=0
    g30: LineSegment StartX=-49.19 StartY=52 StartZ=0 EndX=-11.49 EndY=52 EndZ=0
    g31: LineSegment StartX=-49.19 StartY=49 StartZ=0 EndX=-11.49 EndY=49 EndZ=0
    g32: LineSegment StartX=-49.19 StartY=46.25 StartZ=0 EndX=-16.28 EndY=46.25 EndZ=0
    g33: LineSegment StartX=-49.19 StartY=43.25 StartZ=0 EndX=-16.28 EndY=43.25 EndZ=0
    g34: LineSegment StartX=-49.19 StartY=40.5 StartZ=0 EndX=-18.2337 EndY=40.5 EndZ=0
    g35: LineSegment StartX=-49.19 StartY=37.5 StartZ=0 EndX=-18.23 EndY=37.5 EndZ=0
    g36: LineSegment StartX=-49.19 StartY=34.5 StartZ=0 EndX=-18.2337 EndY=34.5 EndZ=0
    g37: LineSegment StartX=-49.19 StartY=31.5 StartZ=0 EndX=-18.23 EndY=31.5 EndZ=0
    g38: LineSegment StartX=-49.19 StartY=28.75 StartZ=0 EndX=-16.2837 EndY=28.75 EndZ=0
    g39: LineSegment StartX=-49.19 StartY=25.75 StartZ=0 EndX=-16.28 EndY=25.75 EndZ=0
    g40: LineSegment StartX=-49.19 StartY=23 StartZ=0 EndX=-11.49 EndY=23 EndZ=0
    g41: LineSegment StartX=-49.19 StartY=20 StartZ=0 EndX=-11.49 EndY=20 EndZ=0
    g42: LineSegment StartX=-49.19 StartY=17.25 StartZ=0 EndX=-1.5 EndY=17.25 EndZ=0
    g43: LineSegment StartX=-49.19 StartY=14.25 StartZ=0 EndX=-1.5 EndY=14.25 EndZ=0
    g44: LineSegment StartX=-49.19 StartY=11.5 StartZ=0 EndX=-1.5 EndY=11.5 EndZ=0
    g45: LineSegment StartX=-49.19 StartY=8.5 StartZ=0 EndX=-1.5 EndY=8.5 EndZ=0
    g46: LineSegment StartX=-49.19 StartY=5.75 StartZ=0 EndX=-1.5 EndY=5.75 EndZ=0
    g47: LineSegment StartX=-49.19 StartY=2.75 StartZ=0 EndX=-1.5 EndY=2.75 EndZ=0
  constraints (120):
    c: Vertical(g0)
    c: Distance(g0) = 3
    c: Block(g0)
    c: Vertical(g1)
    c: Distance(g1) = 3
    c: Vertical(g2)
    c: Equal(g0,g2) = 3
    c: Block(g2)
    c: Vertical(g3)
    c: Equal(g1,g3) = 3
    c: Vertical(g4)
    c: Equal(g0,g4) = 3
    c: Block(g4)
    c: Vertical(g5)
    c: Equal(g1,g5) = 3
    c: Vertical(g6)
    c: Equal(g0,g6) = 3
    c: Block(g6)
    c: Vertical(g7)
    c: Equal(g1,g7) = 3
    c: Vertical(g8)
    c: Equal(g0,g8) = 3
    c: Block(g8)
    c: Vertical(g9)
    c: Equal(g1,g9) = 3
    c: Vertical(g10)
    c: Equal(g0,g10) = 3
    c: Block(g10)
    c: Vertical(g11)
    c: Equal(g1,g11) = 3
    c: Block(g12)
    c: Block(g13)
    c: Block(g14)
    c: Block(g15)
    c: Block(g16)
    c: Block(g17)
    c: Block(g18)
    c: Block(g19)
    c: Block(g20)
    c: Block(g21)
    c: Block(g22)
    c: Block(g23)
    c: Block(g11)
    c: Block(g9)
    c: Block(g7)
    c: Block(g5)
    c: Block(g3)
    c: Block(g1)
    c: Coincident(g24,g0)
    c: Coincident(g24,g12)
    c: Horizontal(g24)
    c: Coincident(g25,g0)
    c: Coincident(g25,g12)
    c: Horizontal(g25)
    c: Coincident(g26,g1)
    c: Coincident(g26,g13)
    c: Horizontal(g26)
    c: Coincident(g27,g1)
    c: Coincident(g27,g13)
    c: Horizontal(g27)
    c: Coincident(g28,g2)
    c: Coincident(g28,g14)
    c: Horizontal(g28)
    c: Coincident(g29,g2)
    c: Coincident(g29,g14)
    c: Horizontal(g29)
    c: Coincident(g30,g3)
    c: Coincident(g30,g15)
    c: Horizontal(g30)
    c: Coincident(g31,g3)
    c: Coincident(g31,g15)
    c: Horizontal(g31)
    c: Coincident(g32,g4)
    c: Coincident(g32,g16)
    c: Horizontal(g32)
    c: Coincident(g33,g4)
    c: Coincident(g33,g16)
    c: Horizontal(g33)
    c: Coincident(g34,g5)
    c: Coincident(g34,g17)
    c: Horizontal(g34)
    c: Coincident(g35,g5)
    c: Coincident(g35,g17)
    c: Horizontal(g35)
    c: Coincident(g36,g6)
    c: Coincident(g36,g19)
    c: Horizontal(g36)
    c: Coincident(g37,g6)
    c: Coincident(g37,g19)
    c: Horizontal(g37)
    c: Coincident(g38,g7)
    c: Coincident(g38,g18)
    c: Horizontal(g38)
    c: Coincident(g39,g7)
    c: Coincident(g39,g18)
    c: Horizontal(g39)
    c: Coincident(g40,g8)
    c: Coincident(g40,g20)
    c: Horizontal(g40)
    c: Coincident(g41,g8)
    c: Coincident(g41,g20)
    c: Horizontal(g41)
    c: Coincident(g42,g9)
    c: Coincident(g42,g23)
    c: Horizontal(g42)
    c: Coincident(g43,g9)
    c: Coincident(g43,g23)
    c: Horizontal(g43)
    c: Coincident(g44,g10)
    c: Coincident(g44,g22)
    c: Horizontal(g44)
    c: Coincident(g45,g10)
    c: Coincident(g45,g22)
    c: Horizontal(g45)
    c: Coincident(g46,g11)
    c: Coincident(g46,g21)
    c: Horizontal(g46)
    c: Coincident(g47,g11)
    c: Coincident(g47,g21)
    c: Horizontal(g47)
FEATURE [Part::Extrusion] Extrude046
  Base = -> Sketch055
  Dir = (1,0,0)
  DirMode = 2
  FaceMakerClass = Part::FaceMakerBullseye
  LengthFwd = 23
  LengthRev = 0
  Placement = pos=(-19,0,0) rot=(0,0,1;0rad)
  Solid = true
  Symmetric = false
FEATURE [Part::Fillet] Fillet038  label="removeToCreateVentalationHoles001"
  Base = -> Extrude046
  Edges = <same value as first occurrence — deduplicated (x6 in doc)>
  Placement = pos=(7,0,0) rot=(0,0,1;0rad)
FEATURE [Sketcher::SketchObject] Sketch056  label="topSketch014"
  FullyConstrained = true
  sketch-geometry (22):
    g0: LineSegment StartX=5.21097e-06 StartY=3 StartZ=0 EndX=5.21097e-06 EndY=19 EndZ=0
    g1: ArcOfCircle CenterX=19 CenterY=19 CenterZ=0 NormalX=0 NormalY=0 NormalZ=1 AngleXU=0 Radius=19 StartAngle=1.5708 EndAngle=3.14159
    g2: ArcOfCircle CenterX=19 CenterY=19 CenterZ=0 NormalX=0 NormalY=0 NormalZ=1 AngleXU=0 Radius=16 StartAngle=1.5708 EndAngle=3.14159
    g3: LineSegment StartX=114 StartY=35 StartZ=0 EndX=19 EndY=35 EndZ=0
    g4: LineSegment StartX=5.21097e-06 StartY=3 StartZ=0 EndX=5.21097e-06 EndY=0 EndZ=0
    g5: LineSegment StartX=3 StartY=0 StartZ=0 EndX=5.21097e-06 EndY=0 EndZ=0
    g6: LineSegment StartX=3 StartY=19 StartZ=0 EndX=3 EndY=0 EndZ=0
    g7: LineSegment StartX=19 StartY=38 StartZ=0 EndX=124 EndY=38 EndZ=0
    g8: Circle CenterX=119 CenterY=35 CenterZ=0 NormalX=0 NormalY=0 NormalZ=1 AngleXU=0 Radius=1
    g9: Circle CenterX=121 CenterY=35 CenterZ=0 NormalX=0 NormalY=0 NormalZ=1 AngleXU=0 Radius=1
    g10: Circle CenterX=121 CenterY=33 CenterZ=0 NormalX=0 NormalY=0 NormalZ=1 AngleXU=0 Radius=1
    g11: BSplineCurve PolesCount=3 KnotsCount=2 Degree=2 IsPeriodic=0
    g12: GeomPoint X=119 Y=35 Z=0
    g13: GeomPoint X=121 Y=33 Z=0
    g14: LineSegment StartX=119 StartY=35 StartZ=0 EndX=114 EndY=35 EndZ=0
    g15: ArcOfCircle CenterX=105 CenterY=19 CenterZ=0 NormalX=0 NormalY=0 NormalZ=1 AngleXU=0 Radius=16 StartAngle=5.60905 EndAngle=6.28319
    g16: LineSegment StartX=121 StartY=33 StartZ=0 EndX=121 EndY=19 EndZ=0
    g17: LineSegment StartX=117.5 StartY=9.01251 StartZ=0 EndX=121.163 EndY=9.0125 EndZ=0
    g18: ArcOfCircle CenterX=105 CenterY=19 CenterZ=0 NormalX=0 NormalY=0 NormalZ=1 AngleXU=0 Radius=20.6155 StartAngle=5.7297 EndAngle=6.28319
    g19: LineSegment StartX=121.163 StartY=9.0125 StartZ=0 EndX=122.538 EndY=8.16329 EndZ=0
    g20: LineSegment StartX=124 StartY=38 StartZ=0 EndX=125.616 EndY=38 EndZ=0
    g21: LineSegment StartX=125.616 StartY=19 StartZ=0 EndX=125.616 EndY=38 EndZ=0
  constraints (49):
    c: Vertical(g0)
    c: Block(g0)
    c: Coincident(g1,g0)
    c: Block(g1)
    c: Coincident(g2,g1)
    c: Block(g2)
    c: Coincident(g3,g2)
    c: Horizontal(g3)
    c: Tangent(g3,g2)
    c: Coincident(g4,g0)
    c: Distance(g4) = 3
    c: Vertical(g4)
    c: Coincident(g5,g4)
    c: Horizontal(g5)
    c: Coincident(g6,g2)
    c: Coincident(g6,g5)
    c: Vertical(g6)
    c: Horizontal(g7)
    c: Distance(g7) = 105
    c: Coincident(g7,g1)
    c: Block(g3)
    c: Weight(g8) = 1
    c: Equal(g8,g9)
    c: Equal(g8,g10)
    c: InternalAlignment(g8,g11)
    c: InternalAlignment(g9,g11)
    c: InternalAlignment(g10,g11)
    c: InternalAlignment(g12,g11)
    c: InternalAlignment(g13,g11)
    c: Block(g11)
    c: Coincident(g14,g11)
    c: Coincident(g14,g3)
    c: Horizontal(g14)
    c: Block(g15)
    c: Coincident(g16,g11)
    c: Coincident(g16,g15)
    c: Vertical(g16)
    c: Distance(g16) = 14
    c: Coincident(g17,g15)
    c: Block(g18)
    c: Coincident(g19,g18)
    c: Coincident(g20,g7)
    c: Horizontal(g20)
    c: Vertical(g21)
    c: Coincident(g20,g21)
    c: Block(g20)
    c: Block(g21)
    c: Block(g19)
    c: Block(g17)
FEATURE [Part::Box] Box026  label="removeToCreteHoleForPlugHousing032"
  AttacherType = Attacher::AttachEngine3D
  Height = 28.6
  Length = 10
  Placement = pos=(-2,0,21.7) rot=(0,0,1;0rad)
  Width = 19
FEATURE [Part::Feature] Face109 .. Face112  x4 (patterned run collapsed; names and placements below)
  shape: bbox 3.5 x 17.8 x 2e-07 mm, 1 faces, 0 solids (baked)
FEATURE [Part::Revolution] Revolve117  label="removeToCreateScrewAndThreadedInsertHole045"
  Angle = 360
  Axis = (0,1,0)
  Base = (0,0,0)
  FaceMakerClass = Part::FaceMakerBullseye
  Placement = pos=(62.3,30.3,19.7) rot=(0,0,1;0rad)
  Solid = false
  Source = -> Face109
  Symmetric = false
FEATURE [Part::Revolution] Revolve118  label="removeToCreateScrewAndThreadedInsertHole046"
  Angle = 360
  Axis = (0,1,0)
  Base = (0,0,0)
  FaceMakerClass = Part::FaceMakerBullseye
  Placement = pos=(62.3,30.3,51.7) rot=(0,0,1;0rad)
  Solid = false
  Source = -> Face110
  Symmetric = false
FEATURE [Part::Revolution] Revolve119  label="removeToCreateScrewAndThreadedInsertHole047"
  Angle = 360
  Axis = (0,1,0)
  Base = (0,0,0)
  FaceMakerClass = Part::FaceMakerBullseye
  Placement = pos=(30.3,30.3,19.7) rot=(0,0,1;0rad)
  Solid = false
  Source = -> Face111
  Symmetric = false
FEATURE [Part::Revolution] Revolve120  label="removeToCreateScrewAndThreadedInsertHole048"
  Angle = 360
  Axis = (0,1,0)
  Base = (0,0,0)
  FaceMakerClass = Part::FaceMakerBullseye
  Placement = pos=(30.3,30.3,51.7) rot=(0,0,1;0rad)
  Solid = false
  Source = -> Face112
  Symmetric = false
FEATURE [Part::MultiFuse] Fusion087  label="createThreadedInsertHolesForFan005"
  Shapes = -> [Revolve117,Revolve118,Revolve119,Revolve120]
FEATURE [Part::Extrusion] Extrude047
  Base = -> Sketch056
  Dir = (0,0,1)
  DirMode = 2
  FaceMakerClass = Part::FaceMakerBullseye
  LengthFwd = 72
  LengthRev = 0
  Solid = true
  Symmetric = false
FEATURE [Part::Fillet] Fillet039  label="top019"
  Base = -> Extrude047
  Edges = 1 edges r=2: [Edge35]
FEATURE [Sketcher::SketchObject] Sketch057
  FullyConstrained = false
  Placement = pos=(0,0,0) rot=(1,0,0;1.5708rad)
  sketch-geometry (24):
    g0: ArcOfCircle CenterX=-4 CenterY=-10.5 CenterZ=0 NormalX=0 NormalY=0 NormalZ=1 AngleXU=0 Radius=1.5 StartAngle=6e-16 EndAngle=3.14159
    g1: ArcOfCircle CenterX=-34.2 CenterY=-10.5 CenterZ=0 NormalX=0 NormalY=0 NormalZ=1 AngleXU=0 Radius=1.5 StartAngle=0 EndAngle=3.14159
    g2: ArcOfCircle CenterX=-34.2 CenterY=-27.7 CenterZ=0 NormalX=0 NormalY=0 NormalZ=1 AngleXU=0 Radius=1.5 StartAngle=3.14159 EndAngle=6.28319
    g3: ArcOfCircle CenterX=-4 CenterY=-27.7 CenterZ=0 NormalX=0 NormalY=0 NormalZ=1 AngleXU=0 Radius=1.5 StartAngle=3.1416 EndAngle=6.28319
    g4: ArcOfCircle CenterX=-10 CenterY=-4.3 CenterZ=0 NormalX=0 NormalY=0 NormalZ=1 AngleXU=0 Radius=1.5 StartAngle=2e-16 EndAngle=3.14159
    g5: ArcOfCircle CenterX=-16.1 CenterY=-1.8 CenterZ=0 NormalX=0 NormalY=0 NormalZ=1 AngleXU=0 Radius=1.5 StartAngle=5e-16 EndAngle=3.14159
    g6: ArcOfCircle CenterX=-22.1 CenterY=-1.8 CenterZ=0 NormalX=0 NormalY=0 NormalZ=1 AngleXU=0 Radius=1.5 StartAngle=5e-16 EndAngle=3.14159
    g7: ArcOfCircle CenterX=-28.2 CenterY=-4.3 CenterZ=0 NormalX=0 NormalY=0 NormalZ=1 AngleXU=0 Radius=1.5 StartAngle=2e-16 EndAngle=3.14159
    g8: ArcOfCircle CenterX=-10 CenterY=-33.9 CenterZ=0 NormalX=0 NormalY=0 NormalZ=1 AngleXU=0 Radius=1.5 StartAngle=3.14159 EndAngle=6.28319
    g9: ArcOfCircle CenterX=-16.1 CenterY=-36.4 CenterZ=0 NormalX=0 NormalY=0 NormalZ=1 AngleXU=0 Radius=1.5 StartAngle=3.14159 EndAngle=6.28319
    g10: ArcOfCircle CenterX=-22.1 CenterY=-36.4 CenterZ=0 NormalX=0 NormalY=0 NormalZ=1 AngleXU=0 Radius=1.5 StartAngle=3.14159 EndAngle=6.28319
    g11: ArcOfCircle CenterX=-28.2 CenterY=-33.9 CenterZ=0 NormalX=0 NormalY=0 NormalZ=1 AngleXU=0 Radius=1.5 StartAngle=3.14159 EndAngle=6.28319
    g12: LineSegment StartX=-35.7 StartY=-10.5 StartZ=0 EndX=-35.7 EndY=-27.7 EndZ=0
    g13: LineSegment StartX=-32.7 StartY=-10.5 StartZ=0 EndX=-32.7 EndY=-27.7 EndZ=0
    g14: LineSegment StartX=-29.7 StartY=-33.9 StartZ=0 EndX=-29.7 EndY=-4.3 EndZ=0
    g15: LineSegment StartX=-26.7 StartY=-33.9 StartZ=0 EndX=-26.7 EndY=-4.3 EndZ=0
    g16: LineSegment StartX=-2.5 StartY=-10.5 StartZ=0 EndX=-2.5 EndY=-27.7 EndZ=0
    g17: LineSegment StartX=-8.5 StartY=-4.3 StartZ=0 EndX=-8.5 EndY=-33.9 EndZ=0
    g18: LineSegment StartX=-5.5 StartY=-10.5 StartZ=0 EndX=-5.5 EndY=-27.7 EndZ=0
    g19: LineSegment StartX=-11.5 StartY=-4.3 StartZ=0 EndX=-11.5 EndY=-33.9 EndZ=0
    g20: LineSegment StartX=-14.6 StartY=-1.8 StartZ=0 EndX=-14.6 EndY=-36.4 EndZ=0
    g21: LineSegment StartX=-17.6 StartY=-1.8 StartZ=0 EndX=-17.6 EndY=-36.4 EndZ=0
    g22: LineSegment StartX=-20.6 StartY=-36.4 StartZ=0 EndX=-20.6 EndY=-1.8 EndZ=0
    g23: LineSegment StartX=-23.6 StartY=-1.8 StartZ=0 EndX=-23.6 EndY=-36.4 EndZ=0
  constraints (48):
    c: Block(g0)
    c: Block(g1)
    c: Block(g2)
    c: Block(g3)
    c: Block(g4)
    c: Block(g5)
    c: Block(g6)
    c: Block(g7)
    c: Block(g8)
    c: Block(g9)
    c: Block(g10)
    c: Block(g11)
    c: Coincident(g12,g1)
    c: Coincident(g12,g2)
    c: Vertical(g12)
    c: Coincident(g13,g1)
    c: Coincident(g13,g2)
    c: Vertical(g13)
    c: Coincident(g14,g11)
    c: Coincident(g14,g7)
    c: Vertical(g14)
    c: Coincident(g15,g11)
    c: Coincident(g15,g7)
    c: Vertical(g15)
    c: Coincident(g16,g0)
    c: Coincident(g16,g3)
    c: Vertical(g16)
    c: Coincident(g17,g4)
    c: Coincident(g17,g8)
    c: Vertical(g17)
    c: Coincident(g18,g0)
    c: Coincident(g18,g3)
    c: Vertical(g18)
    c: Coincident(g19,g4)
    c: Coincident(g19,g8)
    c: Vertical(g19)
    c: Coincident(g20,g5)
    c: Coincident(g20,g9)
    c: Vertical(g20)
    c: Coincident(g21,g5)
    c: Coincident(g21,g9)
    c: Vertical(g21)
    c: Coincident(g22,g10)
    c: Coincident(g22,g6)
    c: Vertical(g22)
    c: Coincident(g23,g6)
    c: Coincident(g23,g10)
    c: Vertical(g23)
FEATURE [Part::Extrusion] Extrude048  label="removeToCreateFanGrillHoles004"
  Base = -> Sketch057
  Dir = (0,-1,6e-16)
  DirMode = 2
  FaceMakerClass = Part::FaceMakerBullseye
  LengthFwd = 10
  LengthRev = 0
  Placement = pos=(65.4,44,54.82) rot=(0,0,1;0rad)
  Solid = true
  Symmetric = false
FEATURE [Part::Cut] Cut040  label="top021"
  Base = -> Fillet039
  Tool = -> Extrude048
FEATURE [Part::Cylinder] Cylinder041  label="removeToCreteHoleForPlugHousing034"
  Angle = 360
  AttacherType = Attacher::AttachEngine3D
  Height = 20
  Placement = pos=(-2,19,36) rot=(0,1,0;1.5708rad)
  Radius = 14.3
FEATURE [Part::MultiFuse] Fusion089  label="removeToCreteHoleForPlugHousing035"
  Shapes = -> [Box026,Cylinder041]
FEATURE [Part::Cylinder] Cylinder042
  Angle = 360
  AttacherType = Attacher::AttachEngine3D
  Height = 20
  Placement = pos=(0,0,36.15) rot=(0,0,1;0rad)
  Radius = 14.3
FEATURE [Part::Cylinder] Cylinder043
  Angle = 360
  AttacherType = Attacher::AttachEngine3D
  Height = 10
  Placement = pos=(0,0,36.15) rot=(0,0,1;0rad)
  Radius = 4
FEATURE [Part::Box] Box027  label="removeToCreteHoleForPlugHousing036"
  AttacherType = Attacher::AttachEngine3D
  Height = 28.6
  Length = 20
  Placement = pos=(106.15,0,21.7) rot=(0,0,1;0rad)
  Width = 19
FEATURE [Part::Cut] Cut041  label="top022"
  Base = -> Cut040
  Tool = -> Fusion087
FEATURE [Part::Cut] Cut039  label="top020"
  Base = -> Cut041
  Tool = -> Fusion089
FEATURE [Part::MultiFuse] Fusion090  label="removeToCreteHoleForPlugHousing037"
  Placement = pos=(70,19,36) rot=(0,1,0;1.5708rad)
  Shapes = -> [Cylinder042,Cylinder043]
FEATURE [Part::MultiFuse] Fusion088  label="removeToCreteHoleForPlugHousing033"
  Shapes = -> [Box027,Fusion090]
FEATURE [Part::Cut] Cut042  label="removeToCreteHoleForPlugHousing038"
  Base = -> Cut039
  Tool = -> Fusion088
FEATURE [Part::MultiFuse] Fusion091  label="removeFromTop"
  Shapes = -> [Fillet038,Fusion085,Fusion084,Fusion083,Extrude045]
FEATURE [Part::Cut] Cut043  label="REAL TOP ====="
  Base = -> Fillet036
  Tool = -> Fusion091
FEATURE [Part::MultiFuse] Fusion092  label="caseScrewPillarBracket016"
  Shapes = -> [Extrude030,Extrude031,Extrude032,Extrude033,Extrude034,Extrude035,Extrude036,Extrude037,Box013,Box014]
FEATURE [Sketcher::SketchObject] Sketch058  label="topSketch015"
  FullyConstrained = true
  sketch-geometry (20):
    g0: LineSegment StartX=5.21097e-06 StartY=3 StartZ=0 EndX=5.21097e-06 EndY=19 EndZ=0
    g1: ArcOfCircle CenterX=19 CenterY=19 CenterZ=0 NormalX=0 NormalY=0 NormalZ=1 AngleXU=0 Radius=19 StartAngle=1.5708 EndAngle=3.14159
    g2: ArcOfCircle CenterX=19 CenterY=19 CenterZ=0 NormalX=0 NormalY=0 NormalZ=1 AngleXU=0 Radius=16 StartAngle=1.5708 EndAngle=3.14159
    g3: LineSegment StartX=114 StartY=35 StartZ=0 EndX=19 EndY=35 EndZ=0
    g4: LineSegment StartX=5.21097e-06 StartY=3 StartZ=0 EndX=5.21097e-06 EndY=0 EndZ=0
    g5: LineSegment StartX=3 StartY=0 StartZ=0 EndX=5.21097e-06 EndY=0 EndZ=0
    g6: LineSegment StartX=3 StartY=19 StartZ=0 EndX=3 EndY=0 EndZ=0
    g7: LineSegment StartX=19 StartY=38 StartZ=0 EndX=124 EndY=38 EndZ=0
    g8: Circle CenterX=119 CenterY=35 CenterZ=0 NormalX=0 NormalY=0 NormalZ=1 AngleXU=0 Radius=1
    g9: Circle CenterX=121 CenterY=35 CenterZ=0 NormalX=0 NormalY=0 NormalZ=1 AngleXU=0 Radius=1
    g10: Circle CenterX=121 CenterY=33 CenterZ=0 NormalX=0 NormalY=0 NormalZ=1 AngleXU=0 Radius=1
    g11: BSplineCurve PolesCount=3 KnotsCount=2 Degree=2 IsPeriodic=0
    g12: GeomPoint X=119 Y=35 Z=0
    g13: GeomPoint X=121 Y=33 Z=0
    g14: LineSegment StartX=119 StartY=35 StartZ=0 EndX=114 EndY=35 EndZ=0
    g15: ArcOfCircle CenterX=105 CenterY=19 CenterZ=0 NormalX=0 NormalY=0 NormalZ=1 AngleXU=0 Radius=19 StartAngle=5.7297 EndAngle=6.28319
    g16: ArcOfCircle CenterX=105 CenterY=19 CenterZ=0 NormalX=0 NormalY=0 NormalZ=1 AngleXU=0 Radius=16 StartAngle=5.60905 EndAngle=6.28319
    g17: LineSegment StartX=121 StartY=33 StartZ=0 EndX=121 EndY=19 EndZ=0
    g18: LineSegment StartX=124 StartY=38 StartZ=0 EndX=124 EndY=19 EndZ=0
    g19: LineSegment StartX=117.5 StartY=9.01251 StartZ=0 EndX=121.163 EndY=9.0125 EndZ=0
  constraints (46):
    c: Vertical(g0)
    c: Block(g0)
    c: Coincident(g1,g0)
    c: Block(g1)
    c: Coincident(g2,g1)
    c: Block(g2)
    c: Coincident(g3,g2)
    c: Horizontal(g3)
    c: Tangent(g3,g2)
    c: Coincident(g4,g0)
    c: Distance(g4) = 3
    c: Vertical(g4)
    c: Coincident(g5,g4)
    c: Horizontal(g5)
    c: Coincident(g6,g2)
    c: Coincident(g6,g5)
    c: Vertical(g6)
    c: Horizontal(g7)
    c: Distance(g7) = 105
    c: Coincident(g7,g1)
    c: Block(g3)
    c: Weight(g8) = 1
    c: Equal(g8,g9)
    c: Equal(g8,g10)
    c: InternalAlignment(g8,g11)
    c: InternalAlignment(g9,g11)
    c: InternalAlignment(g10,g11)
    c: InternalAlignment(g12,g11)
    c: InternalAlignment(g13,g11)
    c: Block(g11)
    c: Coincident(g14,g11)
    c: Coincident(g14,g3)
    c: Horizontal(g14)
    c: Block(g15)
    c: Coincident(g16,g15)
    c: Block(g16)
    c: Coincident(g17,g11)
    c: Coincident(g17,g16)
    c: Vertical(g17)
    c: Distance(g17) = 14
    c: Coincident(g18,g7)
    c: Coincident(g18,g15)
    c: Vertical(g18)
    c: Distance(g18) = 19
    c: Coincident(g19,g16)
    c: Coincident(g19,g15)
FEATURE [Part::Extrusion] Extrude049  label="top023"
  Base = -> Sketch058
  Dir = (0,0,1)
  DirMode = 2
  FaceMakerClass = Part::FaceMakerBullseye
  LengthFwd = 72
  LengthRev = 0
  Solid = true
  Symmetric = false
FEATURE [Sketcher::SketchObject] Sketch059
  FullyConstrained = true
  MapMode = 3
  Placement = pos=(0,0,0) rot=(1,0,0;1.5708rad)
  Support = -> [Extrude049]
  sketch-geometry (8):
    g0: Circle CenterX=80.351 CenterY=-67.6202 CenterZ=0 NormalX=0 NormalY=0 NormalZ=1 AngleXU=0 Radius=2
    g1: Circle CenterX=80.351 CenterY=-67.6202 CenterZ=0 NormalX=0 NormalY=0 NormalZ=1 AngleXU=0 Radius=3
    g2: Circle CenterX=80.351 CenterY=-4.92017 CenterZ=0 NormalX=0 NormalY=0 NormalZ=1 AngleXU=0 Radius=2
    g3: Circle CenterX=80.351 CenterY=-4.92017 CenterZ=0 NormalX=0 NormalY=0 NormalZ=1 AngleXU=0 Radius=3
    g4: Circle CenterX=23.851 CenterY=-4.92017 CenterZ=0 NormalX=0 NormalY=0 NormalZ=1 AngleXU=0 Radius=2
    g5: Circle CenterX=23.851 CenterY=-4.92017 CenterZ=0 NormalX=0 NormalY=0 NormalZ=1 AngleXU=0 Radius=3
    g6: Circle CenterX=23.851 CenterY=-67.6202 CenterZ=0 NormalX=0 NormalY=0 NormalZ=1 AngleXU=0 Radius=2
    g7: Circle CenterX=23.851 CenterY=-67.6202 CenterZ=0 NormalX=0 NormalY=0 NormalZ=1 AngleXU=0 Radius=3
  constraints (8):
    c: Block(g3)
    c: Block(g2)
    c: Block(g1)
    c: Block(g0)
    c: Block(g6)
    c: Block(g7)
    c: Block(g4)
    c: Block(g5)
FEATURE [Sketcher::SketchObject] Sketch060
  FullyConstrained = true
  MapMode = 3
  Placement = pos=(0,0,0) rot=(1,0,0;1.5708rad)
  Support = -> [Extrude049]
  sketch-geometry (8):
    g0: Circle CenterX=80.351 CenterY=-67.6202 CenterZ=0 NormalX=0 NormalY=0 NormalZ=1 AngleXU=0 Radius=3
    g1: Circle CenterX=80.351 CenterY=-4.92017 CenterZ=0 NormalX=0 NormalY=0 NormalZ=1 AngleXU=0 Radius=3
    g2: Circle CenterX=23.851 CenterY=-4.92017 CenterZ=0 NormalX=0 NormalY=0 NormalZ=1 AngleXU=0 Radius=3
    g3: Circle CenterX=23.851 CenterY=-67.6202 CenterZ=0 NormalX=0 NormalY=0 NormalZ=1 AngleXU=0 Radius=3
    g4: Circle CenterX=23.851 CenterY=-67.6202 CenterZ=0 NormalX=0 NormalY=0 NormalZ=1 AngleXU=0 Radius=5
    g5: Circle CenterX=80.351 CenterY=-67.6202 CenterZ=0 NormalX=0 NormalY=0 NormalZ=1 AngleXU=0 Radius=5
    g6: Circle CenterX=23.851 CenterY=-4.92017 CenterZ=0 NormalX=0 NormalY=0 NormalZ=1 AngleXU=0 Radius=5
    g7: Circle CenterX=80.351 CenterY=-4.92017 CenterZ=0 NormalX=0 NormalY=0 NormalZ=1 AngleXU=0 Radius=5
  constraints (8):
    c: Block(g1)
    c: Block(g0)
    c: Block(g3)
    c: Block(g2)
    c: Block(g5)
    c: Block(g4)
    c: Block(g6)
    c: Block(g7)
FEATURE [Sketcher::SketchObject] Sketch061
  FullyConstrained = true
  MapMode = 3
  Placement = pos=(0,0,0) rot=(1,0,0;1.5708rad)
  sketch-geometry (8):
    g0: Circle CenterX=80.351 CenterY=-67.6202 CenterZ=0 NormalX=0 NormalY=0 NormalZ=1 AngleXU=0 Radius=3
    g1: Circle CenterX=80.351 CenterY=-4.92017 CenterZ=0 NormalX=0 NormalY=0 NormalZ=1 AngleXU=0 Radius=3
    g2: Circle CenterX=23.851 CenterY=-4.92017 CenterZ=0 NormalX=0 NormalY=0 NormalZ=1 AngleXU=0 Radius=3
    g3: Circle CenterX=23.851 CenterY=-67.6202 CenterZ=0 NormalX=0 NormalY=0 NormalZ=1 AngleXU=0 Radius=3
    g4: Circle CenterX=23.851 CenterY=-67.6202 CenterZ=0 NormalX=0 NormalY=0 NormalZ=1 AngleXU=0 Radius=5
    g5: Circle CenterX=80.351 CenterY=-67.6202 CenterZ=0 NormalX=0 NormalY=0 NormalZ=1 AngleXU=0 Radius=5
    g6: Circle CenterX=23.851 CenterY=-4.92017 CenterZ=0 NormalX=0 NormalY=0 NormalZ=1 AngleXU=0 Radius=5
    g7: Circle CenterX=80.351 CenterY=-4.92017 CenterZ=0 NormalX=0 NormalY=0 NormalZ=1 AngleXU=0 Radius=5
  constraints (8):
    c: Block(g1)
    c: Block(g0)
    c: Block(g3)
    c: Block(g2)
    c: Block(g5)
    c: Block(g4)
    c: Block(g6)
    c: Block(g7)
FEATURE [Sketcher::SketchObject] Sketch062  label="topSketch016"
  FullyConstrained = true
  sketch-geometry (20):
    g0: LineSegment StartX=5.21097e-06 StartY=3 StartZ=0 EndX=5.21097e-06 EndY=19 EndZ=0
    g1: ArcOfCircle CenterX=19 CenterY=19 CenterZ=0 NormalX=0 NormalY=0 NormalZ=1 AngleXU=0 Radius=19 StartAngle=1.5708 EndAngle=3.14159
    g2: ArcOfCircle CenterX=19 CenterY=19 CenterZ=0 NormalX=0 NormalY=0 NormalZ=1 AngleXU=0 Radius=16 StartAngle=1.5708 EndAngle=3.14159
    g3: LineSegment StartX=114 StartY=35 StartZ=0 EndX=19 EndY=35 EndZ=0
    g4: LineSegment StartX=5.21097e-06 StartY=3 StartZ=0 EndX=5.21097e-06 EndY=0 EndZ=0
    g5: LineSegment StartX=3 StartY=0 StartZ=0 EndX=5.21097e-06 EndY=0 EndZ=0
    g6: LineSegment StartX=3 StartY=19 StartZ=0 EndX=3 EndY=0 EndZ=0
    g7: LineSegment StartX=19 StartY=38 StartZ=0 EndX=124 EndY=38 EndZ=0
    g8: Circle CenterX=119 CenterY=35 CenterZ=0 NormalX=0 NormalY=0 NormalZ=1 AngleXU=0 Radius=1
    g9: Circle CenterX=121 CenterY=35 CenterZ=0 NormalX=0 NormalY=0 NormalZ=1 AngleXU=0 Radius=1
    g10: Circle CenterX=121 CenterY=33 CenterZ=0 NormalX=0 NormalY=0 NormalZ=1 AngleXU=0 Radius=1
    g11: BSplineCurve PolesCount=3 KnotsCount=2 Degree=2 IsPeriodic=0
    g12: GeomPoint X=119 Y=35 Z=0
    g13: GeomPoint X=121 Y=33 Z=0
    g14: LineSegment StartX=119 StartY=35 StartZ=0 EndX=114 EndY=35 EndZ=0
    g15: ArcOfCircle CenterX=105 CenterY=19 CenterZ=0 NormalX=0 NormalY=0 NormalZ=1 AngleXU=0 Radius=19 StartAngle=5.7297 EndAngle=6.28319
    g16: ArcOfCircle CenterX=105 CenterY=19 CenterZ=0 NormalX=0 NormalY=0 NormalZ=1 AngleXU=0 Radius=16 StartAngle=5.60905 EndAngle=6.28319
    g17: LineSegment StartX=121 StartY=33 StartZ=0 EndX=121 EndY=19 EndZ=0
    g18: LineSegment StartX=124 StartY=38 StartZ=0 EndX=124 EndY=19 EndZ=0
    g19: LineSegment StartX=117.5 StartY=9.01251 StartZ=0 EndX=121.163 EndY=9.0125 EndZ=0
  constraints (46):
    c: Vertical(g0)
    c: Block(g0)
    c: Coincident(g1,g0)
    c: Block(g1)
    c: Coincident(g2,g1)
    c: Block(g2)
    c: Coincident(g3,g2)
    c: Horizontal(g3)
    c: Tangent(g3,g2)
    c: Coincident(g4,g0)
    c: Distance(g4) = 3
    c: Vertical(g4)
    c: Coincident(g5,g4)
    c: Horizontal(g5)
    c: Coincident(g6,g2)
    c: Coincident(g6,g5)
    c: Vertical(g6)
    c: Horizontal(g7)
    c: Distance(g7) = 105
    c: Coincident(g7,g1)
    c: Block(g3)
    c: Weight(g8) = 1
    c: Equal(g8,g9)
    c: Equal(g8,g10)
    c: InternalAlignment(g8,g11)
    c: InternalAlignment(g9,g11)
    c: InternalAlignment(g10,g11)
    c: InternalAlignment(g12,g11)
    c: InternalAlignment(g13,g11)
    c: Block(g11)
    c: Coincident(g14,g11)
    c: Coincident(g14,g3)
    c: Horizontal(g14)
    c: Block(g15)
    c: Coincident(g16,g15)
    c: Block(g16)
    c: Coincident(g17,g11)
    c: Coincident(g17,g16)
    c: Vertical(g17)
    c: Distance(g17) = 14
    c: Coincident(g18,g7)
    c: Coincident(g18,g15)
    c: Vertical(g18)
    c: Distance(g18) = 19
    c: Coincident(g19,g16)
    c: Coincident(g19,g15)
FEATURE [Part::Extrusion] Extrude053  label="top024"
  Base = -> Sketch062
  Dir = (0,0,1)
  DirMode = 2
  FaceMakerClass = Part::FaceMakerBullseye
  LengthFwd = 72
  LengthRev = 0
  Solid = true
  Symmetric = false
FEATURE [Sketcher::SketchObject] Sketch063
  FullyConstrained = true
  MapMode = 3
  Placement = pos=(0,0,0) rot=(1,0,0;1.5708rad)
  Support = -> [Extrude053]
  sketch-geometry (8):
    g0: Circle CenterX=80.351 CenterY=-67.6202 CenterZ=0 NormalX=0 NormalY=0 NormalZ=1 AngleXU=0 Radius=2
    g1: Circle CenterX=80.351 CenterY=-67.6202 CenterZ=0 NormalX=0 NormalY=0 NormalZ=1 AngleXU=0 Radius=3
    g2: Circle CenterX=80.351 CenterY=-4.92017 CenterZ=0 NormalX=0 NormalY=0 NormalZ=1 AngleXU=0 Radius=2
    g3: Circle CenterX=80.351 CenterY=-4.92017 CenterZ=0 NormalX=0 NormalY=0 NormalZ=1 AngleXU=0 Radius=3
    g4: Circle CenterX=23.851 CenterY=-4.92017 CenterZ=0 NormalX=0 NormalY=0 NormalZ=1 AngleXU=0 Radius=2
    g5: Circle CenterX=23.851 CenterY=-4.92017 CenterZ=0 NormalX=0 NormalY=0 NormalZ=1 AngleXU=0 Radius=3
    g6: Circle CenterX=23.851 CenterY=-67.6202 CenterZ=0 NormalX=0 NormalY=0 NormalZ=1 AngleXU=0 Radius=2
    g7: Circle CenterX=23.851 CenterY=-67.6202 CenterZ=0 NormalX=0 NormalY=0 NormalZ=1 AngleXU=0 Radius=3
  constraints (8):
    c: Block(g3)
    c: Block(g2)
    c: Block(g1)
    c: Block(g0)
    c: Block(g6)
    c: Block(g7)
    c: Block(g4)
    c: Block(g5)
FEATURE [Part::Extrusion] Extrude054
  Base = -> Sketch063
  Dir = (0,-1,2e-16)
  DirMode = 2
  FaceMakerClass = Part::FaceMakerBullseye
  LengthFwd = 6
  LengthRev = 0
  Placement = pos=(0,9,0) rot=(0,0,1;0rad)
  Solid = true
  Symmetric = false
FEATURE [Sketcher::SketchObject] Sketch064  label="topSketch017"
  FullyConstrained = true
  sketch-geometry (20):
    g0: LineSegment StartX=5.21097e-06 StartY=3 StartZ=0 EndX=5.21097e-06 EndY=19 EndZ=0
    g1: ArcOfCircle CenterX=19 CenterY=19 CenterZ=0 NormalX=0 NormalY=0 NormalZ=1 AngleXU=0 Radius=19 StartAngle=1.5708 EndAngle=3.14159
    g2: ArcOfCircle CenterX=19 CenterY=19 CenterZ=0 NormalX=0 NormalY=0 NormalZ=1 AngleXU=0 Radius=16 StartAngle=1.5708 EndAngle=3.14159
    g3: LineSegment StartX=114 StartY=35 StartZ=0 EndX=19 EndY=35 EndZ=0
    g4: LineSegment StartX=5.21097e-06 StartY=3 StartZ=0 EndX=5.21097e-06 EndY=0 EndZ=0
    g5: LineSegment StartX=3 StartY=0 StartZ=0 EndX=5.21097e-06 EndY=0 EndZ=0
    g6: LineSegment StartX=3 StartY=19 StartZ=0 EndX=3 EndY=0 EndZ=0
    g7: LineSegment StartX=19 StartY=38 StartZ=0 EndX=124 EndY=38 EndZ=0
    g8: Circle CenterX=119 CenterY=35 CenterZ=0 NormalX=0 NormalY=0 NormalZ=1 AngleXU=0 Radius=1
    g9: Circle CenterX=121 CenterY=35 CenterZ=0 NormalX=0 NormalY=0 NormalZ=1 AngleXU=0 Radius=1
    g10: Circle CenterX=121 CenterY=33 CenterZ=0 NormalX=0 NormalY=0 NormalZ=1 AngleXU=0 Radius=1
    g11: BSplineCurve PolesCount=3 KnotsCount=2 Degree=2 IsPeriodic=0
    g12: GeomPoint X=119 Y=35 Z=0
    g13: GeomPoint X=121 Y=33 Z=0
    g14: LineSegment StartX=119 StartY=35 StartZ=0 EndX=114 EndY=35 EndZ=0
    g15: ArcOfCircle CenterX=105 CenterY=19 CenterZ=0 NormalX=0 NormalY=0 NormalZ=1 AngleXU=0 Radius=19 StartAngle=5.7297 EndAngle=6.28319
    g16: ArcOfCircle CenterX=105 CenterY=19 CenterZ=0 NormalX=0 NormalY=0 NormalZ=1 AngleXU=0 Radius=16 StartAngle=5.60905 EndAngle=6.28319
    g17: LineSegment StartX=121 StartY=33 StartZ=0 EndX=121 EndY=19 EndZ=0
    g18: LineSegment StartX=124 StartY=38 StartZ=0 EndX=124 EndY=19 EndZ=0
    g19: LineSegment StartX=117.5 StartY=9.01251 StartZ=0 EndX=121.163 EndY=9.0125 EndZ=0
  constraints (46):
    c: Vertical(g0)
    c: Block(g0)
    c: Coincident(g1,g0)
    c: Block(g1)
    c: Coincident(g2,g1)
    c: Block(g2)
    c: Coincident(g3,g2)
    c: Horizontal(g3)
    c: Tangent(g3,g2)
    c: Coincident(g4,g0)
    c: Distance(g4) = 3
    c: Vertical(g4)
    c: Coincident(g5,g4)
    c: Horizontal(g5)
    c: Coincident(g6,g2)
    c: Coincident(g6,g5)
    c: Vertical(g6)
    c: Horizontal(g7)
    c: Distance(g7) = 105
    c: Coincident(g7,g1)
    c: Block(g3)
    c: Weight(g8) = 1
    c: Equal(g8,g9)
    c: Equal(g8,g10)
    c: InternalAlignment(g8,g11)
    c: InternalAlignment(g9,g11)
    c: InternalAlignment(g10,g11)
    c: InternalAlignment(g12,g11)
    c: InternalAlignment(g13,g11)
    c: Block(g11)
    c: Coincident(g14,g11)
    c: Coincident(g14,g3)
    c: Horizontal(g14)
    c: Block(g15)
    c: Coincident(g16,g15)
    c: Block(g16)
    c: Coincident(g17,g11)
    c: Coincident(g17,g16)
    c: Vertical(g17)
    c: Distance(g17) = 14
    c: Coincident(g18,g7)
    c: Coincident(g18,g15)
    c: Vertical(g18)
    c: Distance(g18) = 19
    c: Coincident(g19,g16)
    c: Coincident(g19,g15)
FEATURE [Sketcher::SketchObject] Sketch065
  FullyConstrained = true
  MapMode = 3
  Placement = pos=(0,0,0) rot=(1,0,0;1.5708rad)
  sketch-geometry (8):
    g0: Circle CenterX=80.351 CenterY=-67.6202 CenterZ=0 NormalX=0 NormalY=0 NormalZ=1 AngleXU=0 Radius=3
    g1: Circle CenterX=80.351 CenterY=-4.92017 CenterZ=0 NormalX=0 NormalY=0 NormalZ=1 AngleXU=0 Radius=3
    g2: Circle CenterX=23.851 CenterY=-4.92017 CenterZ=0 NormalX=0 NormalY=0 NormalZ=1 AngleXU=0 Radius=3
    g3: Circle CenterX=23.851 CenterY=-67.6202 CenterZ=0 NormalX=0 NormalY=0 NormalZ=1 AngleXU=0 Radius=3
    g4: Circle CenterX=23.851 CenterY=-67.6202 CenterZ=0 NormalX=0 NormalY=0 NormalZ=1 AngleXU=0 Radius=5
    g5: Circle CenterX=80.351 CenterY=-67.6202 CenterZ=0 NormalX=0 NormalY=0 NormalZ=1 AngleXU=0 Radius=5
    g6: Circle CenterX=23.851 CenterY=-4.92017 CenterZ=0 NormalX=0 NormalY=0 NormalZ=1 AngleXU=0 Radius=5
    g7: Circle CenterX=80.351 CenterY=-4.92017 CenterZ=0 NormalX=0 NormalY=0 NormalZ=1 AngleXU=0 Radius=5
  constraints (8):
    c: Block(g1)
    c: Block(g0)
    c: Block(g3)
    c: Block(g2)
    c: Block(g5)
    c: Block(g4)
    c: Block(g6)
    c: Block(g7)
FEATURE [Part::Extrusion] Extrude056
  Base = -> Sketch065
  Dir = (0,-1,2e-16)
  DirMode = 2
  FaceMakerClass = Part::FaceMakerBullseye
  LengthFwd = 2
  LengthRev = 0
  Solid = true
  Symmetric = false
FEATURE [Part::Extrusion] Extrude057  label="top025"
  Base = -> Sketch064
  Dir = (0,0,1)
  DirMode = 2
  FaceMakerClass = Part::FaceMakerBullseye
  LengthFwd = 72
  LengthRev = 0
  Solid = true
  Symmetric = false
FEATURE [Sketcher::SketchObject] Sketch066
  FullyConstrained = true
  MapMode = 3
  Placement = pos=(0,0,0) rot=(1,0,0;1.5708rad)
  Support = -> [Extrude057]
  sketch-geometry (8):
    g0: Circle CenterX=80.351 CenterY=-67.6202 CenterZ=0 NormalX=0 NormalY=0 NormalZ=1 AngleXU=0 Radius=3
    g1: Circle CenterX=80.351 CenterY=-4.92017 CenterZ=0 NormalX=0 NormalY=0 NormalZ=1 AngleXU=0 Radius=3
    g2: Circle CenterX=23.851 CenterY=-4.92017 CenterZ=0 NormalX=0 NormalY=0 NormalZ=1 AngleXU=0 Radius=3
    g3: Circle CenterX=23.851 CenterY=-67.6202 CenterZ=0 NormalX=0 NormalY=0 NormalZ=1 AngleXU=0 Radius=3
    g4: Circle CenterX=23.851 CenterY=-67.6202 CenterZ=0 NormalX=0 NormalY=0 NormalZ=1 AngleXU=0 Radius=5
    g5: Circle CenterX=80.351 CenterY=-67.6202 CenterZ=0 NormalX=0 NormalY=0 NormalZ=1 AngleXU=0 Radius=5
    g6: Circle CenterX=23.851 CenterY=-4.92017 CenterZ=0 NormalX=0 NormalY=0 NormalZ=1 AngleXU=0 Radius=5
    g7: Circle CenterX=80.351 CenterY=-4.92017 CenterZ=0 NormalX=0 NormalY=0 NormalZ=1 AngleXU=0 Radius=5
  constraints (8):
    c: Block(g1)
    c: Block(g0)
    c: Block(g3)
    c: Block(g2)
    c: Block(g5)
    c: Block(g4)
    c: Block(g6)
    c: Block(g7)
FEATURE [Part::Extrusion] Extrude055
  Base = -> Sketch066
  Dir = (0,-1,2e-16)
  DirMode = 2
  FaceMakerClass = Part::FaceMakerBullseye
  LengthFwd = 2
  LengthRev = 0
  Solid = true
  Symmetric = false
FEATURE [Part::Fillet] Fillet041
  Base = -> Extrude056
  Edges = 4 edges r=1.99: [Edge6,Edge12,Edge18,Edge24]
FEATURE [Part::Cut] Cut045
  Base = -> Extrude055
  Placement = pos=(0,6,0) rot=(0,0,1;0rad)
  Tool = -> Fillet041
FEATURE [Part::MultiFuse] Fusion095  label="pcbScrewPillars"
  Placement = pos=(-3.2,-1,72.3) rot=(0,0,1;0rad)
  Shapes = -> [Cut045,Extrude054]
FEATURE [Part::Feature] Face113
  shape: bbox 3.2 x 1.5 x 2e-07 mm, 1 faces, 0 solids (baked)
FEATURE [Part::Revolution] Revolve121  label="backCaseScrewRetainer002"
  Angle = 360
  Axis = (0,1,0)
  Base = (0,0,0)
  FaceMakerClass = Part::FaceMakerBullseye
  Placement = pos=(12.5,3,62) rot=(0,0,1;0rad)
  Solid = false
  Source = -> Face113
  Symmetric = false
FEATURE [Part::Feature] Face114
  shape: bbox 3.2 x 1.5 x 2e-07 mm, 1 faces, 0 solids (baked)
FEATURE [Part::Feature] Face115
  shape: bbox 3.2 x 1.5 x 2e-07 mm, 1 faces, 0 solids (baked)
FEATURE [Part::Feature] Face116
  shape: bbox 3.2 x 1.5 x 2e-07 mm, 1 faces, 0 solids (baked)
FEATURE [Part::Revolution] Revolve122  label="frontCaseScrewRetainer004"
  Angle = 360
  Axis = (0,1,0)
  Base = (0,0,0)
  FaceMakerClass = Part::FaceMakerBullseye
  Placement = pos=(89.5,3,68.5) rot=(0,0,1;0rad)
  Solid = false
  Source = -> Face115
  Symmetric = false
FEATURE [Part::Revolution] Revolve123  label="frontCaseScrewRetainer005"
  Angle = 360
  Axis = (0,1,0)
  Base = (0,0,0)
  FaceMakerClass = Part::FaceMakerBullseye
  Placement = pos=(89.5,3,3.5) rot=(0,0,1;0rad)
  Solid = false
  Source = -> Face116
  Symmetric = false
FEATURE [Part::Revolution] Revolve124  label="backCaseScrewRetainer003"
  Angle = 360
  Axis = (0,1,0)
  Base = (0,0,0)
  FaceMakerClass = Part::FaceMakerBullseye
  Placement = pos=(12.5,3,10) rot=(0,0,1;0rad)
  Solid = false
  Source = -> Face114
  Symmetric = false
FEATURE [Part::Feature] Face117
  shape: bbox 3.6 x 3.2 x 2e-07 mm, 1 faces, 0 solids (baked)
FEATURE [Part::Revolution] Revolve125  label="moreFrontCaseScrewRetainer004"
  Angle = 360
  Axis = (0,1,0)
  Base = (0,0,0)
  FaceMakerClass = Part::FaceMakerBullseye
  Placement = pos=(109.5,4.5,68.5) rot=(0,0,1;0rad)
  Solid = false
  Source = -> Face117
  Symmetric = false
FEATURE [Part::Feature] Face118
  shape: bbox 3.6 x 3.2 x 2e-07 mm, 1 faces, 0 solids (baked)
FEATURE [Part::Revolution] Revolve126  label="moreFrontCaseScrewRetainer005"
  Angle = 360
  Axis = (0,1,0)
  Base = (0,0,0)
  FaceMakerClass = Part::FaceMakerBullseye
  Placement = pos=(109.5,4.5,3.5) rot=(0,0,1;0rad)
  Solid = false
  Source = -> Face118
  Symmetric = false
FEATURE [Part::MultiFuse] Fusion096  label="screwRetainers001"
  Shapes = -> [Revolve126,Revolve125,Revolve124,Revolve123,Revolve122,Revolve121]
FEATURE [Part::Feature] Face119
  shape: bbox 10 x 16.5 x 2e-07 mm, 1 faces, 0 solids (baked)
FEATURE [Part::Revolution] Revolve130  label="plugHousing050"
  Angle = 360
  Axis = (0,1,0)
  Base = (0,0,0)
  FaceMakerClass = Part::FaceMakerBullseye
  Placement = pos=(0,0,36.15) rot=(0,0,1;0rad)
  Solid = false
  Source = -> Face119
  Symmetric = false
FEATURE [Part::Feature] Face120
  shape: bbox 10 x 16.5 x 2e-07 mm, 1 faces, 0 solids (baked)
FEATURE [Part::Feature] Face121
  shape: bbox 10 x 16.5 x 2e-07 mm, 1 faces, 0 solids (baked)
FEATURE [Part::Revolution] Revolve127  label="plugHousing047"
  Angle = 360
  Axis = (0,1,0)
  Base = (0,0,0)
  FaceMakerClass = Part::FaceMakerBullseye
  Placement = pos=(0,0,36.15) rot=(0,0,1;0rad)
  Solid = false
  Source = -> Face121
  Symmetric = false
FEATURE [Part::Feature] Face122
  shape: bbox 10 x 16.5 x 2e-07 mm, 1 faces, 0 solids (baked)
FEATURE [Part::Feature] Face123
  shape: bbox 10 x 16.5 x 2e-07 mm, 1 faces, 0 solids (baked)
FEATURE [Part::Revolution] Revolve128  label="plugHousing048"
  Angle = 360
  Axis = (0,1,0)
  Base = (0,0,0)
  FaceMakerClass = Part::FaceMakerBullseye
  Placement = pos=(0,0,36.15) rot=(0,0,1;0rad)
  Solid = false
  Source = -> Face123
  Symmetric = false
FEATURE [Part::MultiFuse] Fusion100  label="plugHousing054"
  Placement = pos=(0,0,0) rot=(0,0,1;1.5708rad)
  Shapes = -> [Revolve130,Revolve128]
FEATURE [Part::Feature] Face124
  shape: bbox 10 x 16.5 x 2e-07 mm, 1 faces, 0 solids (baked)
FEATURE [Part::Feature] Face125
  shape: bbox 10 x 16.5 x 2e-07 mm, 1 faces, 0 solids (baked)
FEATURE [Part::Revolution] Revolve129  label="plugHousing049"
  Angle = 360
  Axis = (0,1,0)
  Base = (0,0,0)
  FaceMakerClass = Part::FaceMakerBullseye
  Placement = pos=(0,0,36.15) rot=(0,0,1;0rad)
  Solid = false
  Source = -> Face125
  Symmetric = false
FEATURE [Part::Feature] Face126
  shape: bbox 10 x 16.5 x 2e-07 mm, 1 faces, 0 solids (baked)
FEATURE [Part::Revolution] Revolve131  label="plugHousing058"
  Angle = 360
  Axis = (0,1,0)
  Base = (0,0,0)
  FaceMakerClass = Part::FaceMakerBullseye
  Placement = pos=(0,0,36.15) rot=(0,0,1;0rad)
  Solid = false
  Source = -> Face120
  Symmetric = false
FEATURE [Part::MultiFuse] Fusion099  label="plugHousing053"
  Placement = pos=(0,0,0) rot=(0,0,1;1.5708rad)
  Shapes = -> [Revolve127,Revolve131]
FEATURE [Part::MultiFuse] Fusion102  label="plugHousing056"
  Placement = pos=(0,19,0) rot=(0,0,1;3.14159rad)
  Shapes = -> [Fusion100,Fusion099]
FEATURE [Part::Revolution] Revolve132  label="plugHousing059"
  Angle = 360
  Axis = (0,1,0)
  Base = (0,0,0)
  FaceMakerClass = Part::FaceMakerBullseye
  Placement = pos=(0,0,36.15) rot=(0,0,1;0rad)
  Solid = false
  Source = -> Face126
  Symmetric = false
FEATURE [Part::Revolution] Revolve133  label="plugHousing060"
  Angle = 360
  Axis = (0,1,0)
  Base = (0,0,0)
  FaceMakerClass = Part::FaceMakerBullseye
  Placement = pos=(0,0,36.15) rot=(0,0,1;0rad)
  Solid = false
  Source = -> Face122
  Symmetric = false
FEATURE [Part::MultiFuse] Fusion097  label="plugHousing051"
  Placement = pos=(0,0,0) rot=(0,0,1;1.5708rad)
  Shapes = -> [Revolve133,Revolve132]
FEATURE [Part::Revolution] Revolve134  label="plugHousing061"
  Angle = 360
  Axis = (0,1,0)
  Base = (0,0,0)
  FaceMakerClass = Part::FaceMakerBullseye
  Placement = pos=(0,0,36.15) rot=(0,0,1;0rad)
  Solid = false
  Source = -> Face124
  Symmetric = false
FEATURE [Part::MultiFuse] Fusion101  label="plugHousing055"
  Placement = pos=(0,0,0) rot=(0,0,1;1.5708rad)
  Shapes = -> [Revolve129,Revolve134]
FEATURE [Part::MultiFuse] Fusion098  label="plugHousing052"
  Placement = pos=(0,19,0) rot=(0,0,1;3.14159rad)
  Shapes = -> [Fusion097,Fusion101]
FEATURE [Part::MultiFuse] Fusion103  label="plugHousing057"
  Placement = pos=(122.621,0,-0.15) rot=(0,0,1;0rad)
  Shapes = -> [Fusion102,Fusion098]
FEATURE [Part::Box] Box028  label="Cube015"
  AttacherType = Attacher::AttachEngine3D
  Height = 28
  Length = 3
  Placement = pos=(110.7,19,22) rot=(0,0,1;0rad)
  Width = 15.7
FEATURE [Part::Cylinder] Cylinder044
  Angle = 360
  AttacherType = Attacher::AttachEngine3D
  Height = 20
  Placement = pos=(0,0,36.15) rot=(0,0,1;0rad)
  Radius = 10.3
FEATURE [Part::Cylinder] Cylinder045
  Angle = 360
  AttacherType = Attacher::AttachEngine3D
  Height = 10
  Placement = pos=(0,0,36.15) rot=(0,0,1;0rad)
  Radius = 4
FEATURE [Part::MultiFuse] Fusion104  label="removeToCreteHoleForPlugHousing040"
  Placement = pos=(70,19,36) rot=(0,1,0;1.5708rad)
  Shapes = -> [Cylinder044,Cylinder045]
FEATURE [Part::Cut] Cut046  label="plugHousingTab003"
  Base = -> Box028
  Tool = -> Fusion104
FEATURE [Part::MultiFuse] Fusion105  label="plugHousing062"
  Shapes = -> [Fusion103,Cut046]
FEATURE [Part::Fillet] Fillet042
  Base = -> Fusion105
  Edges = 1 edges r=2: [Edge25]
FEATURE [Part::Fillet] Fillet043  label="plugHousing063"
  Base = -> Fillet042
  Edges = 1 edges r=2: [Edge8]
  Placement = pos=(7,0,0) rot=(0,0,1;0rad)
FEATURE [Part::Feature] Face127
  shape: bbox 10 x 16.5 x 2e-07 mm, 1 faces, 0 solids (baked)
FEATURE [Part::Feature] Face128
  shape: bbox 10 x 16.5 x 2e-07 mm, 1 faces, 0 solids (baked)
FEATURE [Part::Revolution] Revolve137  label="plugHousing070"
  Angle = 360
  Axis = (0,1,0)
  Base = (0,0,0)
  FaceMakerClass = Part::FaceMakerBullseye
  Placement = pos=(0,0,36.15) rot=(0,0,1;0rad)
  Solid = false
  Source = -> Face127
  Symmetric = false
FEATURE [Part::Revolution] Revolve140  label="plugHousing073"
  Angle = 360
  Axis = (0,1,0)
  Base = (0,0,0)
  FaceMakerClass = Part::FaceMakerBullseye
  Placement = pos=(0,0,36.15) rot=(0,0,1;0rad)
  Solid = false
  Source = -> Face128
  Symmetric = false
FEATURE [Part::Feature] Face129
  shape: bbox 10 x 16.5 x 2e-07 mm, 1 faces, 0 solids (baked)
FEATURE [Part::Revolution] Revolve138  label="plugHousing071"
  Angle = 360
  Axis = (0,1,0)
  Base = (0,0,0)
  FaceMakerClass = Part::FaceMakerBullseye
  Placement = pos=(0,0,36.15) rot=(0,0,1;0rad)
  Solid = false
  Source = -> Face129
  Symmetric = false
FEATURE [Part::Feature] Face130
  shape: bbox 10 x 16.5 x 2e-07 mm, 1 faces, 0 solids (baked)
FEATURE [Part::Revolution] Revolve139  label="plugHousing072"
  Angle = 360
  Axis = (0,1,0)
  Base = (0,0,0)
  FaceMakerClass = Part::FaceMakerBullseye
  Placement = pos=(0,0,36.15) rot=(0,0,1;0rad)
  Solid = false
  Source = -> Face130
  Symmetric = false
FEATURE [Part::Feature] Face131
  shape: bbox 10 x 16.5 x 2e-07 mm, 1 faces, 0 solids (baked)
FEATURE [Part::Revolution] Revolve135  label="plugHousing068"
  Angle = 360
  Axis = (0,1,0)
  Base = (0,0,0)
  FaceMakerClass = Part::FaceMakerBullseye
  Placement = pos=(0,0,36.15) rot=(0,0,1;0rad)
  Solid = false
  Source = -> Face131
  Symmetric = false
FEATURE [Part::MultiFuse] Fusion112  label="plugHousing078"
  Placement = pos=(0,0,0) rot=(0,0,1;1.5708rad)
  Shapes = -> [Revolve135,Revolve139]
FEATURE [Part::Feature] Face132
  shape: bbox 10 x 16.5 x 2e-07 mm, 1 faces, 0 solids (baked)
FEATURE [Part::Revolution] Revolve141  label="plugHousing074"
  Angle = 360
  Axis = (0,1,0)
  Base = (0,0,0)
  FaceMakerClass = Part::FaceMakerBullseye
  Placement = pos=(0,0,36.15) rot=(0,0,1;0rad)
  Solid = false
  Source = -> Face132
  Symmetric = false
FEATURE [Part::MultiFuse] Fusion110  label="plugHousing076"
  Placement = pos=(0,0,0) rot=(0,0,1;1.5708rad)
  Shapes = -> [Revolve141,Revolve140]
FEATURE [Part::Feature] Face133
  shape: bbox 10 x 16.5 x 2e-07 mm, 1 faces, 0 solids (baked)
FEATURE [Part::Revolution] Revolve136  label="plugHousing069"
  Angle = 360
  Axis = (0,1,0)
  Base = (0,0,0)
  FaceMakerClass = Part::FaceMakerBullseye
  Placement = pos=(0,0,36.15) rot=(0,0,1;0rad)
  Solid = false
  Source = -> Face133
  Symmetric = false
FEATURE [Part::MultiFuse] Fusion106  label="plugHousing064"
  Placement = pos=(0,0,0) rot=(0,0,1;1.5708rad)
  Shapes = -> [Revolve138,Revolve136]
FEATURE [Part::MultiFuse] Fusion108  label="plugHousing066"
  Placement = pos=(0,19,0) rot=(0,0,1;3.14159rad)
  Shapes = -> [Fusion106,Fusion112]
FEATURE [Part::Feature] Face134
  shape: bbox 10 x 16.5 x 2e-07 mm, 1 faces, 0 solids (baked)
FEATURE [Part::Revolution] Revolve142  label="plugHousing075"
  Angle = 360
  Axis = (0,1,0)
  Base = (0,0,0)
  FaceMakerClass = Part::FaceMakerBullseye
  Placement = pos=(0,0,36.15) rot=(0,0,1;0rad)
  Solid = false
  Source = -> Face134
  Symmetric = false
FEATURE [Part::MultiFuse] Fusion107  label="plugHousing065"
  Placement = pos=(0,0,0) rot=(0,0,1;1.5708rad)
  Shapes = -> [Revolve137,Revolve142]
FEATURE [Part::MultiFuse] Fusion111  label="plugHousing077"
  Placement = pos=(0,19,0) rot=(0,0,1;3.14159rad)
  Shapes = -> [Fusion110,Fusion107]
FEATURE [Part::MultiFuse] Fusion109  label="plugHousing067"
  Placement = pos=(131.236,0,-0.15) rot=(0,0,1;0rad)
  Shapes = -> [Fusion108,Fusion111]
FEATURE [Part::MultiFuse] Fusion113  label="plugHousing079"
  Shapes = -> [Fillet043,Fusion109]
FEATURE [Part::Feature] Face135
  shape: bbox 3.5 x 17.8 x 2e-07 mm, 1 faces, 0 solids (baked)
FEATURE [Part::Revolution] Revolve143  label="removeToCreateScrewAndThreadedInsertHole049"
  Angle = 360
  Axis = (0,1,0)
  Base = (0,0,0)
  FaceMakerClass = Part::FaceMakerBullseye
  Placement = pos=(12.5,0,10) rot=(0,0,1;0rad)
  Solid = false
  Source = -> Face135
  Symmetric = false
FEATURE [Part::Feature] Face136
  shape: bbox 3.5 x 17.8 x 2e-07 mm, 1 faces, 0 solids (baked)
FEATURE [Part::Revolution] Revolve144  label="removeToCreateScrewAndThreadedInsertHole050"
  Angle = 360
  Axis = (0,1,0)
  Base = (0,0,0)
  FaceMakerClass = Part::FaceMakerBullseye
  Placement = pos=(12.5,0,62) rot=(0,0,1;0rad)
  Solid = false
  Source = -> Face136
  Symmetric = false
FEATURE [Part::Feature] Face137
  shape: bbox 3.5 x 17.8 x 2e-07 mm, 1 faces, 0 solids (baked)
FEATURE [Part::Revolution] Revolve145  label="removeToCreateScrewAndThreadedInsertHole051"
  Angle = 360
  Axis = (0,1,0)
  Base = (0,0,0)
  FaceMakerClass = Part::FaceMakerBullseye
  Placement = pos=(89.5,0,68.5) rot=(0,0,1;0rad)
  Solid = false
  Source = -> Face137
  Symmetric = false
FEATURE [Part::Feature] Face138
  shape: bbox 3.5 x 17.8 x 2e-07 mm, 1 faces, 0 solids (baked)
FEATURE [Part::Revolution] Revolve146  label="removeToCreateScrewAndThreadedInsertHole052"
  Angle = 360
  Axis = (0,1,0)
  Base = (0,0,0)
  FaceMakerClass = Part::FaceMakerBullseye
  Placement = pos=(89.5,0,3.5) rot=(0,0,1;0rad)
  Solid = false
  Source = -> Face138
  Symmetric = false
FEATURE [Part::Feature] Face139
  shape: bbox 3.5 x 17.8 x 2e-07 mm, 1 faces, 0 solids (baked)
FEATURE [Part::Revolution] Revolve147  label="removeToCreateScrewAndThreadedInsertHole053"
  Angle = 360
  Axis = (0,1,0)
  Base = (0,0,0)
  FaceMakerClass = Part::FaceMakerBullseye
  Placement = pos=(109.5,4.7,3.5) rot=(0,0,1;0rad)
  Solid = false
  Source = -> Face139
  Symmetric = false
FEATURE [Part::Feature] Face140
  shape: bbox 3.5 x 17.8 x 2e-07 mm, 1 faces, 0 solids (baked)
FEATURE [Part::Revolution] Revolve148  label="removeToCreateScrewAndThreadedInsertHole054"
  Angle = 360
  Axis = (0,1,0)
  Base = (0,0,0)
  FaceMakerClass = Part::FaceMakerBullseye
  Placement = pos=(109.5,4.7,68.5) rot=(0,0,1;0rad)
  Solid = false
  Source = -> Face140
  Symmetric = false
FEATURE [Part::MultiFuse] Fusion114  label="removeToCreateScrewAndThreadedInsertHole055"
  Shapes = -> [Revolve148,Revolve147,Revolve146,Revolve145,Revolve144,Revolve143]
FEATURE [Part::Cut] Cut047  label="casePillars004"
  Base = -> Cut037
  Tool = -> Fusion114
FEATURE [Part::Feature] Face141
  shape: bbox 3.5 x 17.8 x 2e-07 mm, 1 faces, 0 solids (baked)
FEATURE [Part::Feature] Face142
  shape: bbox 3.5 x 17.8 x 2e-07 mm, 1 faces, 0 solids (baked)
FEATURE [Part::Feature] Face143
  shape: bbox 3.5 x 17.8 x 2e-07 mm, 1 faces, 0 solids (baked)
FEATURE [Part::Revolution] Revolve149  label="removeToCreateScrewAndThreadedInsertHole057"
  Angle = 360
  Axis = (0,1,0)
  Base = (0,0,0)
  FaceMakerClass = Part::FaceMakerBullseye
  Placement = pos=(12.5,0,10) rot=(0,0,1;0rad)
  Solid = false
  Source = -> Face141
  Symmetric = false
FEATURE [Part::Feature] Face144
  shape: bbox 3.5 x 17.8 x 2e-07 mm, 1 faces, 0 solids (baked)
FEATURE [Part::Feature] Face145
  shape: bbox 3.5 x 17.8 x 2e-07 mm, 1 faces, 0 solids (baked)
FEATURE [Part::Feature] Face146
  shape: bbox 3.5 x 17.8 x 2e-07 mm, 1 faces, 0 solids (baked)
FEATURE [Part::Revolution] Revolve150  label="removeToCreateScrewAndThreadedInsertHole058"
  Angle = 360
  Axis = (0,1,0)
  Base = (0,0,0)
  FaceMakerClass = Part::FaceMakerBullseye
  Placement = pos=(12.5,0,62) rot=(0,0,1;0rad)
  Solid = false
  Source = -> Face146
  Symmetric = false
FEATURE [Part::Revolution] Revolve151  label="removeToCreateScrewAndThreadedInsertHole059"
  Angle = 360
  Axis = (0,1,0)
  Base = (0,0,0)
  FaceMakerClass = Part::FaceMakerBullseye
  Placement = pos=(89.5,0,68.5) rot=(0,0,1;0rad)
  Solid = false
  Source = -> Face143
  Symmetric = false
FEATURE [Part::Revolution] Revolve152  label="removeToCreateScrewAndThreadedInsertHole060"
  Angle = 360
  Axis = (0,1,0)
  Base = (0,0,0)
  FaceMakerClass = Part::FaceMakerBullseye
  Placement = pos=(89.5,0,3.5) rot=(0,0,1;0rad)
  Solid = false
  Source = -> Face142
  Symmetric = false
FEATURE [Part::Revolution] Revolve153  label="removeToCreateScrewAndThreadedInsertHole061"
  Angle = 360
  Axis = (0,1,0)
  Base = (0,0,0)
  FaceMakerClass = Part::FaceMakerBullseye
  Placement = pos=(109.5,4.7,3.5) rot=(0,0,1;0rad)
  Solid = false
  Source = -> Face145
  Symmetric = false
FEATURE [Part::Revolution] Revolve154  label="removeToCreateScrewAndThreadedInsertHole062"
  Angle = 360
  Axis = (0,1,0)
  Base = (0,0,0)
  FaceMakerClass = Part::FaceMakerBullseye
  Placement = pos=(109.5,4.7,68.5) rot=(0,0,1;0rad)
  Solid = false
  Source = -> Face144
  Symmetric = false
FEATURE [Part::MultiFuse] Fusion115  label="removeToCreateScrewAndThreadedInsertHole056"
  Shapes = -> [Revolve154,Revolve153,Revolve152,Revolve151,Revolve150,Revolve149]
FEATURE [Part::Feature] Face147
  shape: bbox 9.8 x 26.5 x 2e-07 mm, 1 faces, 0 solids (baked)
FEATURE [Part::Revolution] Revolve155
  Angle = 360
  Axis = (0,1,0)
  Base = (0,0,0)
  FaceMakerClass = Part::FaceMakerBullseye
  Placement = pos=(0,0,0) rot=(0,0,1;1.5708rad)
  Solid = false
  Source = -> Face147
  Symmetric = false
FEATURE [Part::Feature] Face148
  shape: bbox 9.8 x 26.5 x 2e-07 mm, 1 faces, 0 solids (baked)
FEATURE [Part::Revolution] Revolve156
  Angle = 360
  Axis = (0,1,0)
  Base = (0,0,0)
  FaceMakerClass = Part::FaceMakerBullseye
  Placement = pos=(0,0,0) rot=(0,0,1;1.5708rad)
  Solid = false
  Source = -> Face148
  Symmetric = false
FEATURE [Part::MultiFuse] Fusion116
  Placement = pos=(-18,19,36) rot=(0,0,1;0rad)
  Shapes = -> [Revolve156,Revolve155]
FEATURE [Part::Box] Box029  label="Cube016"
  AttacherType = Attacher::AttachEngine3D
  Height = 28
  Length = 3
  Placement = pos=(110.7,19,22) rot=(0,0,1;0rad)
  Width = 15.7
FEATURE [Part::Cylinder] Cylinder046
  Angle = 360
  AttacherType = Attacher::AttachEngine3D
  Height = 10
  Placement = pos=(0,0,36.15) rot=(0,0,1;0rad)
  Radius = 4
FEATURE [Part::Cylinder] Cylinder047
  Angle = 360
  AttacherType = Attacher::AttachEngine3D
  Height = 20
  Placement = pos=(0,0,36.15) rot=(0,0,1;0rad)
  Radius = 10.3
FEATURE [Part::MultiFuse] Fusion117  label="removeToCreteHoleForPlugHousing041"
  Placement = pos=(70,19,36) rot=(0,1,0;1.5708rad)
  Shapes = -> [Cylinder047,Cylinder046]
FEATURE [Part::Cut] Cut049  label="plugHousingTab004"
  Base = -> Box029
  Placement = pos=(-107.4,-14,0) rot=(0,0,1;0rad)
  Tool = -> Fusion117
FEATURE [Part::Box] Box030  label="Cube017"
  AttacherType = Attacher::AttachEngine3D
  Height = 28
  Length = 3
  Placement = pos=(110.7,19,22) rot=(0,0,1;0rad)
  Width = 15.7
FEATURE [Part::Cylinder] Cylinder048
  Angle = 360
  AttacherType = Attacher::AttachEngine3D
  Height = 10
  Placement = pos=(0,0,36.15) rot=(0,0,1;0rad)
  Radius = 4
FEATURE [Part::Cylinder] Cylinder049
  Angle = 360
  AttacherType = Attacher::AttachEngine3D
  Height = 20
  Placement = pos=(0,0,36.15) rot=(0,0,1;0rad)
  Radius = 10.3
FEATURE [Part::MultiFuse] Fusion118  label="removeToCreteHoleForPlugHousing042"
  Placement = pos=(70,19,36) rot=(0,1,0;1.5708rad)
  Shapes = -> [Cylinder049,Cylinder048]
FEATURE [Part::Cut] Cut050  label="plugHousingTab005"
  Base = -> Box030
  Placement = pos=(-107.4,-14,0) rot=(0,0,1;0rad)
  Tool = -> Fusion118
FEATURE [Part::MultiFuse] Fusion119
  Placement = pos=(9.6,23,0) rot=(0,0,1;3.14159rad)
  Shapes = -> [Cut049,Cut050]
FEATURE [Part::Box] Box031  label="Cube018"
  AttacherType = Attacher::AttachEngine3D
  Height = 10
  Length = 3
  Placement = pos=(3.3,4,12) rot=(0,0,1;0rad)
  Width = 10
FEATURE [Part::Fillet] Fillet044
  Base = -> Box031
  Edges = 1 edges r=2: [Edge11]
FEATURE [Part::Box] Box032  label="Cube019"
  AttacherType = Attacher::AttachEngine3D
  Height = 10
  Length = 3
  Placement = pos=(3.3,4,50) rot=(0,0,1;0rad)
  Width = 10
FEATURE [Part::Fillet] Fillet045
  Base = -> Box032
  Edges = 1 edges r=2: [Edge12]
FEATURE [Part::Box] Box033  label="Cube020"
  AttacherType = Attacher::AttachEngine3D
  Height = 28
  Length = 4
  Placement = pos=(5,0,22) rot=(0,0,1;0rad)
  Width = 10
FEATURE [Part::Fillet] Fillet046
  Base = -> Box033
  Edges = 1 edges r=1: [Edge7]
FEATURE [Part::Fillet] Fillet047
  Base = -> Fillet046
  Edges = 1 edges r=2: [Edge5]
FEATURE [Part::Fillet] Fillet048
  Base = -> Fillet047
  Edges = 1 edges r=2: [Edge2]
FEATURE [Part::Cylinder] Cylinder050
  Angle = 360
  AttacherType = Attacher::AttachEngine3D
  Height = 20
  Placement = pos=(0,0,36.15) rot=(0,0,1;0rad)
  Radius = 8.2
FEATURE [Part::Cylinder] Cylinder051
  Angle = 360
  AttacherType = Attacher::AttachEngine3D
  Height = 10
  Placement = pos=(0,0,36.15) rot=(0,0,1;0rad)
  Radius = 4
FEATURE [Part::MultiFuse] Fusion120  label="removeToCreteHoleForPlugHousing043"
  Placement = pos=(-42,19,36) rot=(0,1,0;1.5708rad)
  Shapes = -> [Cylinder050,Cylinder051]
FEATURE [Sketcher::SketchObject] Sketch067  label="topSketch018"
  FullyConstrained = true
  sketch-geometry (4):
    g0: LineSegment StartX=16.8446 StartY=31.512 StartZ=0 EndX=16.3251 EndY=34.4666 EndZ=0
    g1: ArcOfCircle CenterX=19 CenterY=19.2524 CenterZ=0 NormalX=0 NormalY=0 NormalZ=1 AngleXU=0 Radius=15.4476 StartAngle=1.74483 EndAngle=2.72717
    g2: ArcOfCircle CenterX=19 CenterY=19.2524 CenterZ=0 NormalX=0 NormalY=0 NormalZ=1 AngleXU=0 Radius=12.4476 StartAngle=1.74483 EndAngle=2.73189
    g3: LineSegment StartX=4.86004 StartY=25.4725 StartZ=0 EndX=7.58253 EndY=24.2107 EndZ=0
  constraints (7):
    c: Block(g0)
    c: Coincident(g1,g0)
    c: Coincident(g2,g0)
    c: Coincident(g3,g1)
    c: Coincident(g3,g2)
    c: Block(g1)
    c: Block(g2)
FEATURE [Part::Extrusion] Extrude058
  Base = -> Sketch067
  Dir = (0,0,1)
  DirMode = 2
  FaceMakerClass = Part::FaceMakerBullseye
  LengthFwd = 10
  LengthRev = 0
  Placement = pos=(0,0,31) rot=(0,0,1;0rad)
  Solid = true
  Symmetric = false
FEATURE [Part::Cut] Cut051
  Base = -> Extrude058
  Tool = -> Fusion120
FEATURE [Part::Fillet] Fillet049
  Base = -> Cut051
  Edges = 1 edges r=2: [Edge1]
FEATURE [Part::Fillet] Fillet050
  Base = -> Fillet049
  Edges = 1 edges r=2.5: [Edge1]
FEATURE [Part::Fillet] Fillet051
  Base = -> Fillet050
  Edges = 1 edges r=2.5: [Edge2]
FEATURE [Part::MultiFuse] Fusion121  label="wireHolder003"
  Shapes = -> [Fusion116,Fillet051]
FEATURE [Part::MultiFuse] Fusion122
  Shapes = -> [Fillet045,Fusion121]
FEATURE [Part::MultiFuse] Fusion123  label="wireHolder004"
  Shapes = -> [Fusion122,Fillet048]
FEATURE [Part::MultiFuse] Fusion124  label="wireHolder005"
  Shapes = -> [Fillet044,Fusion119,Fusion123]
FEATURE [Sketcher::SketchObject] Sketch068  label="topSketch019"
  FullyConstrained = true
  sketch-geometry (6):
    g0: LineSegment StartX=19 StartY=38 StartZ=0 EndX=117 EndY=38 EndZ=0
    g1: ArcOfCircle CenterX=19 CenterY=19 CenterZ=0 NormalX=0 NormalY=0 NormalZ=1 AngleXU=0 Radius=19 StartAngle=1.5708 EndAngle=3.14159
    g2: LineSegment StartX=117 StartY=38 StartZ=0 EndX=117 EndY=19 EndZ=0
    g3: LineSegment StartX=98 StartY=1.0161e-12 StartZ=0 EndX=5.22862e-06 EndY=1.0161e-12 EndZ=0
    g4: LineSegment StartX=5.22862e-06 StartY=19 StartZ=0 EndX=5.22862e-06 EndY=1.0161e-12 EndZ=0
    g5: ArcOfCircle CenterX=98 CenterY=19 CenterZ=0 NormalX=0 NormalY=0 NormalZ=1 AngleXU=0 Radius=19 StartAngle=4.71239 EndAngle=6.28319
  constraints (16):
    c: Horizontal(g0)
    c: Distance(g0) = 98
    c: Coincident(g1,g0)
    c: Block(g1)
    c: Coincident(g2,g0)
    c: Vertical(g2)
    c: Distance(g2) = 19
    c: Horizontal(g3)
    c: Coincident(g4,g1)
    c: Vertical(g4)
    c: Coincident(g3,g4)
    c: Block(g3)
    c: Coincident(g5,g2)
    c: Coincident(g5,g3)
    c: Block(g0)
    c: Block(g5)
FEATURE [Part::Extrusion] Extrude059  label="sideA002"
  Base = -> Sketch068
  Dir = (0,0,1)
  DirMode = 2
  FaceMakerClass = Part::FaceMakerBullseye
  LengthFwd = 3
  LengthRev = 0
  Placement = pos=(0,0,-2.7) rot=(0,0,1;0rad)
  Solid = true
  Symmetric = false
FEATURE [Sketcher::SketchObject] Sketch069  label="topSketch020"
  FullyConstrained = true
  sketch-geometry (6):
    g0: LineSegment StartX=19 StartY=38 StartZ=0 EndX=117 EndY=38 EndZ=0
    g1: ArcOfCircle CenterX=19 CenterY=19 CenterZ=0 NormalX=0 NormalY=0 NormalZ=1 AngleXU=0 Radius=19 StartAngle=1.5708 EndAngle=3.14159
    g2: LineSegment StartX=117 StartY=38 StartZ=0 EndX=117 EndY=19 EndZ=0
    g3: LineSegment StartX=98 StartY=1.0161e-12 StartZ=0 EndX=5.22862e-06 EndY=1.0161e-12 EndZ=0
    g4: LineSegment StartX=5.22862e-06 StartY=19 StartZ=0 EndX=5.22862e-06 EndY=1.0161e-12 EndZ=0
    g5: ArcOfCircle CenterX=98 CenterY=19 CenterZ=0 NormalX=0 NormalY=0 NormalZ=1 AngleXU=0 Radius=19 StartAngle=4.71239 EndAngle=6.28319
  constraints (16):
    c: Horizontal(g0)
    c: Distance(g0) = 98
    c: Coincident(g1,g0)
    c: Block(g1)
    c: Coincident(g2,g0)
    c: Vertical(g2)
    c: Distance(g2) = 19
    c: Horizontal(g3)
    c: Coincident(g4,g1)
    c: Vertical(g4)
    c: Coincident(g3,g4)
    c: Block(g3)
    c: Coincident(g5,g2)
    c: Coincident(g5,g3)
    c: Block(g0)
    c: Block(g5)
FEATURE [Part::Extrusion] Extrude060  label="sideB002"
  Base = -> Sketch069
  Dir = (0,0,1)
  DirMode = 2
  FaceMakerClass = Part::FaceMakerBullseye
  LengthFwd = 3
  LengthRev = 0
  Placement = pos=(0,0,71.7) rot=(0,0,1;0rad)
  Solid = true
  Symmetric = false
FEATURE [Part::MultiFuse] Fusion127  label="removeFromBottom001"
  Placement = pos=(2,0,0) rot=(0,0,1;0rad)
  Shapes = -> [Extrude059,Extrude060]
FEATURE [Part::Cylinder] Cylinder052
  Angle = 360
  AttacherType = Attacher::AttachEngine3D
  Height = 20
  Placement = pos=(0,0,36.15) rot=(0,0,1;0rad)
  Radius = 14
FEATURE [Part::Cylinder] Cylinder053
  Angle = 360
  AttacherType = Attacher::AttachEngine3D
  Height = 10
  Placement = pos=(0,0,36.15) rot=(0,0,1;0rad)
  Radius = 4
FEATURE [Part::MultiFuse] Fusion128  label="removeToCreteHoleForPlugHousing044"
  Placement = pos=(70,19,36) rot=(0,1,0;1.5708rad)
  Shapes = -> [Cylinder052,Cylinder053]
FEATURE [Part::Cut] Cut052  label="bottom011"
  Base = -> Extrude043
  Tool = -> Fusion128
FEATURE [Part::Cut] Cut054  label="bottom012"
  Base = -> Cut052
  Tool = -> Fusion115
FEATURE [Sketcher::SketchObject] Sketch070
  FullyConstrained = true
  Placement = pos=(117,19,0) rot=(0.57735,0.57735,0.57735;2.0944rad)
  sketch-geometry (48):
    g0: LineSegment StartX=-49.19 StartY=69.25 StartZ=0 EndX=-49.19 EndY=66.25 EndZ=0
    g1: LineSegment StartX=-49.19 StartY=63.5 StartZ=0 EndX=-49.19 EndY=60.5 EndZ=0
    g2: LineSegment StartX=-49.19 StartY=57.75 StartZ=0 EndX=-49.19 EndY=54.75 EndZ=0
    g3: LineSegment StartX=-49.19 StartY=52 StartZ=0 EndX=-49.19 EndY=49 EndZ=0
    g4: LineSegment StartX=-49.19 StartY=46.25 StartZ=0 EndX=-49.19 EndY=43.25 EndZ=0
    g5: LineSegment StartX=-49.19 StartY=40.5 StartZ=0 EndX=-49.19 EndY=37.5 EndZ=0
    g6: LineSegment StartX=-49.19 StartY=34.5 StartZ=0 EndX=-49.19 EndY=31.5 EndZ=0
    g7: LineSegment StartX=-49.19 StartY=28.75 StartZ=0 EndX=-49.19 EndY=25.75 EndZ=0
    g8: LineSegment StartX=-49.19 StartY=23 StartZ=0 EndX=-49.19 EndY=20 EndZ=0
    g9: LineSegment StartX=-49.19 StartY=17.25 StartZ=0 EndX=-49.19 EndY=14.25 EndZ=0
    g10: LineSegment StartX=-49.19 StartY=11.5 StartZ=0 EndX=-49.19 EndY=8.5 EndZ=0
    g11: LineSegment StartX=-49.19 StartY=5.75 StartZ=0 EndX=-49.19 EndY=2.75 EndZ=0
    g12: ArcOfCircle CenterX=-1.5 CenterY=67.75 CenterZ=0 NormalX=0 NormalY=0 NormalZ=1 AngleXU=0 Radius=1.5 StartAngle=4.71239 EndAngle=7.85398
    g13: ArcOfCircle CenterX=-1.5 CenterY=62 CenterZ=0 NormalX=0 NormalY=0 NormalZ=1 AngleXU=0 Radius=1.5 StartAngle=4.71239 EndAngle=7.85398
    g14: ArcOfCircle CenterX=-1.5 CenterY=56.25 CenterZ=0 NormalX=0 NormalY=0 NormalZ=1 AngleXU=0 Radius=1.5 StartAngle=4.71239 EndAngle=7.85398
    g15: ArcOfCircle CenterX=-11.49 CenterY=50.5 CenterZ=0 NormalX=0 NormalY=0 NormalZ=1 AngleXU=0 Radius=1.5 StartAngle=4.71239 EndAngle=7.85398
    g16: ArcOfCircle CenterX=-16.28 CenterY=44.75 CenterZ=0 NormalX=0 NormalY=0 NormalZ=1 AngleXU=0 Radius=1.5 StartAngle=4.71239 EndAngle=7.85398
    g17: ArcOfCircle CenterX=-18.2337 CenterY=39 CenterZ=0 NormalX=0 NormalY=0 NormalZ=1 AngleXU=0 Radius=1.5 StartAngle=4.71485 EndAngle=7.85398
    g18: ArcOfCircle CenterX=-16.2837 CenterY=27.25 CenterZ=0 NormalX=0 NormalY=0 NormalZ=1 AngleXU=0 Radius=1.5 StartAngle=4.71485 EndAngle=7.85398
    g19: ArcOfCircle CenterX=-18.2337 CenterY=33 CenterZ=0 NormalX=0 NormalY=0 NormalZ=1 AngleXU=0 Radius=1.5 StartAngle=4.71485 EndAngle=7.85398
    g20: ArcOfCircle CenterX=-11.49 CenterY=21.5 CenterZ=0 NormalX=0 NormalY=0 NormalZ=1 AngleXU=0 Radius=1.5 StartAngle=4.71239 EndAngle=7.85398
    g21: ArcOfCircle CenterX=-1.5 CenterY=4.25 CenterZ=0 NormalX=0 NormalY=0 NormalZ=1 AngleXU=0 Radius=1.5 StartAngle=4.71239 EndAngle=7.85398
    g22: ArcOfCircle CenterX=-1.5 CenterY=10 CenterZ=0 NormalX=0 NormalY=0 NormalZ=1 AngleXU=0 Radius=1.5 StartAngle=4.71239 EndAngle=7.85398
    g23: ArcOfCircle CenterX=-1.5 CenterY=15.75 CenterZ=0 NormalX=0 NormalY=0 NormalZ=1 AngleXU=0 Radius=1.5 StartAngle=4.71239 EndAngle=7.85398
    g24: LineSegment StartX=-49.19 StartY=69.25 StartZ=0 EndX=-1.5 EndY=69.25 EndZ=0
    g25: LineSegment StartX=-49.19 StartY=66.25 StartZ=0 EndX=-1.5 EndY=66.25 EndZ=0
    g26: LineSegment StartX=-49.19 StartY=63.5 StartZ=0 EndX=-1.5 EndY=63.5 EndZ=0
    g27: LineSegment StartX=-49.19 StartY=60.5 StartZ=0 EndX=-1.5 EndY=60.5 EndZ=0
    g28: LineSegment StartX=-49.19 StartY=57.75 StartZ=0 EndX=-1.5 EndY=57.75 EndZ=0
    g29: LineSegment StartX=-49.19 StartY=54.75 StartZ=0 EndX=-1.5 EndY=54.75 EndZ=0
    g30: LineSegment StartX=-49.19 StartY=52 StartZ=0 EndX=-11.49 EndY=52 EndZ=0
    g31: LineSegment StartX=-49.19 StartY=49 StartZ=0 EndX=-11.49 EndY=49 EndZ=0
    g32: LineSegment StartX=-49.19 StartY=46.25 StartZ=0 EndX=-16.28 EndY=46.25 EndZ=0
    g33: LineSegment StartX=-49.19 StartY=43.25 StartZ=0 EndX=-16.28 EndY=43.25 EndZ=0
    g34: LineSegment StartX=-49.19 StartY=40.5 StartZ=0 EndX=-18.2337 EndY=40.5 EndZ=0
    g35: LineSegment StartX=-49.19 StartY=37.5 StartZ=0 EndX=-18.23 EndY=37.5 EndZ=0
    g36: LineSegment StartX=-49.19 StartY=34.5 StartZ=0 EndX=-18.2337 EndY=34.5 EndZ=0
    g37: LineSegment StartX=-49.19 StartY=31.5 StartZ=0 EndX=-18.23 EndY=31.5 EndZ=0
    g38: LineSegment StartX=-49.19 StartY=28.75 StartZ=0 EndX=-16.2837 EndY=28.75 EndZ=0
    g39: LineSegment StartX=-49.19 StartY=25.75 StartZ=0 EndX=-16.28 EndY=25.75 EndZ=0
    g40: LineSegment StartX=-49.19 StartY=23 StartZ=0 EndX=-11.49 EndY=23 EndZ=0
    g41: LineSegment StartX=-49.19 StartY=20 StartZ=0 EndX=-11.49 EndY=20 EndZ=0
    g42: LineSegment StartX=-49.19 StartY=17.25 StartZ=0 EndX=-1.5 EndY=17.25 EndZ=0
    g43: LineSegment StartX=-49.19 StartY=14.25 StartZ=0 EndX=-1.5 EndY=14.25 EndZ=0
    g44: LineSegment StartX=-49.19 StartY=11.5 StartZ=0 EndX=-1.5 EndY=11.5 EndZ=0
    g45: LineSegment StartX=-49.19 StartY=8.5 StartZ=0 EndX=-1.5 EndY=8.5 EndZ=0
    g46: LineSegment StartX=-49.19 StartY=5.75 StartZ=0 EndX=-1.5 EndY=5.75 EndZ=0
    g47: LineSegment StartX=-49.19 StartY=2.75 StartZ=0 EndX=-1.5 EndY=2.75 EndZ=0
  constraints (120):
    c: Vertical(g0)
    c: Distance(g0) = 3
    c: Block(g0)
    c: Vertical(g1)
    c: Distance(g1) = 3
    c: Vertical(g2)
    c: Equal(g0,g2) = 3
    c: Block(g2)
    c: Vertical(g3)
    c: Equal(g1,g3) = 3
    c: Vertical(g4)
    c: Equal(g0,g4) = 3
    c: Block(g4)
    c: Vertical(g5)
    c: Equal(g1,g5) = 3
    c: Vertical(g6)
    c: Equal(g0,g6) = 3
    c: Block(g6)
    c: Vertical(g7)
    c: Equal(g1,g7) = 3
    c: Vertical(g8)
    c: Equal(g0,g8) = 3
    c: Block(g8)
    c: Vertical(g9)
    c: Equal(g1,g9) = 3
    c: Vertical(g10)
    c: Equal(g0,g10) = 3
    c: Block(g10)
    c: Vertical(g11)
    c: Equal(g1,g11) = 3
    c: Block(g12)
    c: Block(g13)
    c: Block(g14)
    c: Block(g15)
    c: Block(g16)
    c: Block(g17)
    c: Block(g18)
    c: Block(g19)
    c: Block(g20)
    c: Block(g21)
    c: Block(g22)
    c: Block(g23)
    c: Block(g11)
    c: Block(g9)
    c: Block(g7)
    c: Block(g5)
    c: Block(g3)
    c: Block(g1)
    c: Coincident(g24,g0)
    c: Coincident(g24,g12)
    c: Horizontal(g24)
    c: Coincident(g25,g0)
    c: Coincident(g25,g12)
    c: Horizontal(g25)
    c: Coincident(g26,g1)
    c: Coincident(g26,g13)
    c: Horizontal(g26)
    c: Coincident(g27,g1)
    c: Coincident(g27,g13)
    c: Horizontal(g27)
    c: Coincident(g28,g2)
    c: Coincident(g28,g14)
    c: Horizontal(g28)
    c: Coincident(g29,g2)
    c: Coincident(g29,g14)
    c: Horizontal(g29)
    c: Coincident(g30,g3)
    c: Coincident(g30,g15)
    c: Horizontal(g30)
    c: Coincident(g31,g3)
    c: Coincident(g31,g15)
    c: Horizontal(g31)
    c: Coincident(g32,g4)
    c: Coincident(g32,g16)
    c: Horizontal(g32)
    c: Coincident(g33,g4)
    c: Coincident(g33,g16)
    c: Horizontal(g33)
    c: Coincident(g34,g5)
    c: Coincident(g34,g17)
    c: Horizontal(g34)
    c: Coincident(g35,g5)
    c: Coincident(g35,g17)
    c: Horizontal(g35)
    c: Coincident(g36,g6)
    c: Coincident(g36,g19)
    c: Horizontal(g36)
    c: Coincident(g37,g6)
    c: Coincident(g37,g19)
    c: Horizontal(g37)
    c: Coincident(g38,g7)
    c: Coincident(g38,g18)
    c: Horizontal(g38)
    c: Coincident(g39,g7)
    c: Coincident(g39,g18)
    c: Horizontal(g39)
    c: Coincident(g40,g8)
    c: Coincident(g40,g20)
    c: Horizontal(g40)
    c: Coincident(g41,g8)
    c: Coincident(g41,g20)
    c: Horizontal(g41)
    c: Coincident(g42,g9)
    c: Coincident(g42,g23)
    c: Horizontal(g42)
    c: Coincident(g43,g9)
    c: Coincident(g43,g23)
    c: Horizontal(g43)
    c: Coincident(g44,g10)
    c: Coincident(g44,g22)
    c: Horizontal(g44)
    c: Coincident(g45,g10)
    c: Coincident(g45,g22)
    c: Horizontal(g45)
    c: Coincident(g46,g11)
    c: Coincident(g46,g21)
    c: Horizontal(g46)
    c: Coincident(g47,g11)
    c: Coincident(g47,g21)
    c: Horizontal(g47)
FEATURE [Part::Extrusion] Extrude061
  Base = -> Sketch070
  Dir = (1,0,0)
  DirMode = 2
  FaceMakerClass = Part::FaceMakerBullseye
  LengthFwd = 23
  LengthRev = 0
  Placement = pos=(-19,0,0) rot=(0,0,1;0rad)
  Solid = true
  Symmetric = false
FEATURE [Part::Fillet] Fillet052  label="removeToCreateVentalationHoles002"
  Base = -> Extrude061
  Edges = <same value as first occurrence — deduplicated (x6 in doc)>
  Placement = pos=(7,0.02,0) rot=(0,0,1;0rad)
FEATURE [Part::MultiFuse] Fusion130  label="bottom013"
  Shapes = -> [Cut054,Cut034]
FEATURE [Part::Cut] Cut055
  Base = -> Fusion130
  Tool = -> Fillet052
FEATURE [Part::Cylinder] Cylinder054
  Angle = 360
  AttacherType = Attacher::AttachEngine3D
  Height = 20
  Placement = pos=(0,0,36.15) rot=(0,0,1;0rad)
  Radius = 4
FEATURE [Sketcher::SketchObject] Sketch071  label="bottomSketch002"
  FullyConstrained = true
  sketch-geometry (32):
    g0: LineSegment StartX=3.3 StartY=-6.03275e-07 StartZ=0 EndX=98 EndY=-6.03275e-07 EndZ=0
    g1: ArcOfCircle CenterX=98 CenterY=19 CenterZ=0 NormalX=0 NormalY=0 NormalZ=1 AngleXU=0 Radius=19 StartAngle=4.71239 EndAngle=5.71103
    g2: LineSegment StartX=6.3 StartY=8 StartZ=0 EndX=3.3 EndY=8 EndZ=0
    g3: LineSegment StartX=3.3 StartY=8 StartZ=0 EndX=3.3 EndY=-6.03275e-07 EndZ=0
    g4: ArcOfCircle CenterX=8.3 CenterY=5 CenterZ=0 NormalX=0 NormalY=0 NormalZ=1 AngleXU=0 Radius=2 StartAngle=3.14159 EndAngle=4.71239
    g5: LineSegment StartX=6.3 StartY=8 StartZ=0 EndX=6.3 EndY=5 EndZ=0
    g6: ArcOfCircle CenterX=98 CenterY=19 CenterZ=0 NormalX=0 NormalY=0 NormalZ=1 AngleXU=0 Radius=12.7 StartAngle=4.71239 EndAngle=6.28319
    g7: LineSegment StartX=94.7 StartY=3 StartZ=0 EndX=8.3 EndY=3 EndZ=0
    g8-g12: Circle x5 (B-spline internal-alignment scaffolding for g13; pole/knot coordinates omitted)
    g13: BSplineCurve PolesCount=5 KnotsCount=3 Degree=3 IsPeriodic=0
    g14: GeomPoint X=98 Y=6.3 Z=0
    g15: GeomPoint X=96.3938 Y=4.71946 Z=0
    g16: GeomPoint X=94.7 Y=3 Z=0
    g17-g23: Circle x7 (B-spline internal-alignment scaffolding for g24; pole/knot coordinates omitted)
    g24: BSplineCurve PolesCount=7 KnotsCount=5 Degree=3 IsPeriodic=0
    g25-g29: GeomPoint x5 (B-spline internal-alignment scaffolding for g24; pole/knot coordinates omitted)
    g30: ArcOfCircle CenterX=98 CenterY=19 CenterZ=0 NormalX=0 NormalY=0 NormalZ=1 AngleXU=0 Radius=15.7 StartAngle=5.81226 EndAngle=6.28319
    g31: LineSegment StartX=110.7 StartY=19 StartZ=0 EndX=113.7 EndY=19 EndZ=0
  constraints (41):
    c: Horizontal(g0)
    c: Coincident(g1,g0)
    c: Block(g1)
    c: Horizontal(g2)
    c: Distance(g2) = 3
    c: Coincident(g3,g2)
    c: Vertical(g3)
    c: Coincident(g3,g0)
    c: Block(g4)
    c: Block(g2)
    c: Coincident(g5,g2)
    c: Coincident(g5,g4)
    c: Vertical(g5)
    c: Coincident(g6,g1)
    c: Block(g6)
    c: Coincident(g7,g4)
    c: Horizontal(g7)
    c: Block(g0)
    c: Block(g7)
    c: Block(g3)
    c: Coincident(g13,g6)
    c: Weight(g8) = 1
    c: Equal(g8, g9-g12) x4
    c: Coincident(g13,g7)
    c: InternalAlignment(g8-g12 -> g13) x5
    c: InternalAlignment(g14,g13)
    c: InternalAlignment(g15,g13)
    c: InternalAlignment(g16,g13)
    c: Block(g13)
    c: Weight(g17) = 1
    c: Equal(g17, g18-g23) x6
    c: Coincident(g24,g1)
    c: InternalAlignment(g17-g23 -> g24) x7
    c: InternalAlignment(g25-g29 -> g24) x5
    c: Block(g24)
    c: Coincident(g30,g24)
    c: Coincident(g31,g6)
    c: Coincident(g31,g30)
    c: Horizontal(g31)
    c: Block(g31)
    c: Block(g30)
FEATURE [Part::Extrusion] Extrude062  label="bottom014"
  Base = -> Sketch071
  Dir = (0,0,1)
  DirMode = 2
  FaceMakerClass = Part::FaceMakerBullseye
  LengthFwd = 71.4
  LengthRev = 0
  Placement = pos=(0,0,0.3) rot=(0,0,1;0rad)
  Solid = true
  Symmetric = false
FEATURE [Part::Fillet] Fillet054
  Base = -> Extrude062
  Edges = 1 edges r=2.4: [Edge17]
FEATURE [Part::Fillet] Fillet055  label="bottom015"
  Base = -> Fillet054
  Edges = 1 edges r=2.4: [Edge36]
FEATURE [Part::Cylinder] Cylinder055
  Angle = 360
  AttacherType = Attacher::AttachEngine3D
  Height = 10
  Placement = pos=(0,0,36.15) rot=(0,0,1;0rad)
  Radius = 4
FEATURE [Part::MultiFuse] Fusion131  label="removeToCreateHoleForPlugHousing002"
  Placement = pos=(70,19,36.15) rot=(0,1,0;1.5708rad)
  Shapes = -> [Cylinder054,Cylinder055]
FEATURE [Part::Cut] Cut056  label="Bottom001"
  Base = -> Fillet055
  Placement = pos=(9,0,0) rot=(0,0,1;0rad)
  Tool = -> Fusion131
FEATURE [Part::Cut] Cut057
  Base = -> Cut055
  Tool = -> Cut056
FEATURE [Sketcher::SketchObject] Sketch072  label="topSketch021"
  FullyConstrained = true
  sketch-geometry (4):
    g0: ArcOfCircle CenterX=105 CenterY=19 CenterZ=0 NormalX=0 NormalY=0 NormalZ=1 AngleXU=0 Radius=20.6155 StartAngle=5.54125 EndAngle=6.28319
    g1: ArcOfCircle CenterX=105 CenterY=19 CenterZ=0 NormalX=0 NormalY=0 NormalZ=1 AngleXU=0 Radius=13 StartAngle=5.54125 EndAngle=6.28319
    g2: LineSegment StartX=118 StartY=19 StartZ=0 EndX=125.616 EndY=19 EndZ=0
    g3: LineSegment StartX=114.583 StartY=10.2157 StartZ=0 EndX=120.197 EndY=5.06982 EndZ=0
  constraints (7):
    c: Block(g0)
    c: Block(g1)
    c: Coincident(g2,g1)
    c: Coincident(g2,g0)
    c: Horizontal(g2)
    c: Coincident(g3,g1)
    c: Coincident(g3,g0)
FEATURE [Part::Extrusion] Extrude063  label="bottomPlugHousingBit003"
  Base = -> Sketch072
  Dir = (0,0,1)
  DirMode = 2
  FaceMakerClass = Part::FaceMakerBullseye
  LengthFwd = 72
  LengthRev = 0
  Solid = true
  Symmetric = false
FEATURE [Part::Cylinder] Cylinder056
  Angle = 360
  AttacherType = Attacher::AttachEngine3D
  Height = 20
  Placement = pos=(0,0,36.15) rot=(0,0,1;0rad)
  Radius = 14.3
FEATURE [Part::Cylinder] Cylinder057
  Angle = 360
  AttacherType = Attacher::AttachEngine3D
  Height = 10
  Placement = pos=(0,0,36.15) rot=(0,0,1;0rad)
  Radius = 4
FEATURE [Part::Box] Box034  label="removeToCreteHoleForPlugHousing047"
  AttacherType = Attacher::AttachEngine3D
  Height = 28.6
  Length = 20
  Placement = pos=(106.15,0,21.7) rot=(0,0,1;0rad)
  Width = 19
FEATURE [Part::Cylinder] Cylinder058
  Angle = 360
  AttacherType = Attacher::AttachEngine3D
  Height = 20
  Placement = pos=(0,0,36.15) rot=(0,0,1;0rad)
  Radius = 14.3
FEATURE [Part::Cylinder] Cylinder059
  Angle = 360
  AttacherType = Attacher::AttachEngine3D
  Height = 10
  Placement = pos=(0,0,36.15) rot=(0,0,1;0rad)
  Radius = 4
FEATURE [Part::MultiFuse] Fusion134  label="removeToCreteHoleForPlugHousing046"
  Placement = pos=(70,19,36) rot=(0,1,0;1.5708rad)
  Shapes = -> [Cylinder058,Cylinder059]
FEATURE [Part::Cylinder] Cylinder060
  Angle = 360
  AttacherType = Attacher::AttachEngine3D
  Height = 20
  Placement = pos=(0,0,36.15) rot=(0,0,1;0rad)
  Radius = 14
FEATURE [Part::Cylinder] Cylinder061
  Angle = 360
  AttacherType = Attacher::AttachEngine3D
  Height = 10
  Placement = pos=(0,0,36.15) rot=(0,0,1;0rad)
  Radius = 4
FEATURE [Part::MultiFuse] Fusion135  label="removeToCreteHoleForPlugHousing048"
  Placement = pos=(70,19,36) rot=(0,1,0;1.5708rad)
  Shapes = -> [Cylinder060,Cylinder061]
FEATURE [Part::Box] Box035  label="removeToCreteHoleForPlugHousing049"
  AttacherType = Attacher::AttachEngine3D
  Height = 28.6
  Length = 20
  Placement = pos=(106.15,0,21.7) rot=(0,0,1;0rad)
  Width = 19
FEATURE [Part::MultiFuse] Fusion133  label="removeToCreteHoleForPlugHousing045"
  Placement = pos=(0,0,-28.3) rot=(0,0,1;0rad)
  Shapes = -> [Box035,Fusion134]
FEATURE [Part::MultiFuse] Fusion138  label="removeToCreteHoleForPlugHousing051"
  Placement = pos=(70,19,36) rot=(0,1,0;1.5708rad)
  Shapes = -> [Cylinder056,Cylinder057]
FEATURE [Part::MultiFuse] Fusion137  label="removeToCreteHoleForPlugHousing050"
  Placement = pos=(0,0,28.3) rot=(0,0,1;0rad)
  Shapes = -> [Box034,Fusion138]
FEATURE [Part::MultiFuse] Fusion132  label="removeToCreatePlugHousingBottomBit002"
  Shapes = -> [Fusion133,Fusion137]
FEATURE [Part::MultiFuse] Fusion136  label="removeToCreatePlugHousingBottomBit003"
  Shapes = -> [Fusion135,Fusion132]
FEATURE [Part::Cut] Cut058  label="bottomPlugHousingBit002"
  Base = -> Extrude063
  Placement = pos=(-0.09,0,0) rot=(0,0,1;0rad)
  Tool = -> Fusion136
FEATURE [Sketcher::SketchObject] Sketch073  label="bottomSketch003"
  FullyConstrained = true
  sketch-geometry (45):
    g0: LineSegment StartX=6.29999 StartY=8 StartZ=0 EndX=3.29999 EndY=8 EndZ=0
    g1: LineSegment StartX=3.29999 StartY=8 StartZ=0 EndX=3.29999 EndY=-6.03275e-07 EndZ=0
    g2: ArcOfCircle CenterX=8.29999 CenterY=5 CenterZ=0 NormalX=0 NormalY=0 NormalZ=1 AngleXU=0 Radius=2 StartAngle=3.14159 EndAngle=4.71239
    g3: LineSegment StartX=6.29999 StartY=8 StartZ=0 EndX=6.29999 EndY=5 EndZ=0
    g4: ArcOfCircle CenterX=105 CenterY=19 CenterZ=0 NormalX=0 NormalY=0 NormalZ=1 AngleXU=0 Radius=12.7 StartAngle=4.71239 EndAngle=5.94289
    g5-g11: Circle x7 (B-spline internal-alignment scaffolding for g12; pole/knot coordinates omitted)
    g12: BSplineCurve PolesCount=7 KnotsCount=5 Degree=3 IsPeriodic=0
    g13-g17: GeomPoint x5 (B-spline internal-alignment scaffolding for g12; pole/knot coordinates omitted)
    g18: ArcOfCircle CenterX=105 CenterY=19 CenterZ=0 NormalX=0 NormalY=0 NormalZ=1 AngleXU=0 Radius=15.7 StartAngle=5.81226 EndAngle=6.28319
    g19: BSplineCurve PolesCount=5 KnotsCount=3 Degree=3 IsPeriodic=0
    g20: LineSegment StartX=8.29999 StartY=3 StartZ=0 EndX=101.7 EndY=3 EndZ=0
    g21: LineSegment StartX=3.29999 StartY=-6.03275e-07 StartZ=0 EndX=105 EndY=-6.03275e-07 EndZ=0
    g22: LineSegment StartX=120.974 StartY=8.71251 StartZ=0 EndX=122.332 EndY=7.83778 EndZ=0
    g23: LineSegment StartX=105 StartY=-6.03274e-07 StartZ=0 EndX=113 EndY=-6.03274e-07 EndZ=0
    g24: ArcOfCircle CenterX=105 CenterY=19 CenterZ=0 NormalX=0 NormalY=0 NormalZ=1 AngleXU=0 Radius=20.6155 StartAngle=5.11091 EndAngle=5.71103
    g25: ArcOfCircle CenterX=117.7 CenterY=19 CenterZ=0 NormalX=0 NormalY=0 NormalZ=1 AngleXU=0 Radius=3 StartAngle=1.2e-15 EndAngle=2.10468
    g26: Circle CenterX=116.345 CenterY=16.3232 CenterZ=0 NormalX=0 NormalY=0 NormalZ=1 AngleXU=0 Radius=1
    g27: Circle CenterX=117.24 CenterY=15.7584 CenterZ=0 NormalX=0 NormalY=0 NormalZ=1 AngleXU=0 Radius=1
    g28: Circle CenterX=116.972 CenterY=14.7612 CenterZ=0 NormalX=0 NormalY=0 NormalZ=1 AngleXU=0 Radius=1
    g29: BSplineCurve PolesCount=3 KnotsCount=2 Degree=2 IsPeriodic=0
    g30: GeomPoint X=116.345 Y=16.3232 Z=0
    g31: GeomPoint X=116.972 Y=14.7612 Z=0
    g32: Circle CenterX=115.828 CenterY=17.157 CenterZ=0 NormalX=0 NormalY=0 NormalZ=1 AngleXU=0 Radius=1
    g33: Circle CenterX=115.841 CenterY=16.639 CenterZ=0 NormalX=0 NormalY=0 NormalZ=1 AngleXU=0 Radius=1
    g34: Circle CenterX=116.345 CenterY=16.3232 CenterZ=0 NormalX=0 NormalY=0 NormalZ=1 AngleXU=0 Radius=1
    g35: BSplineCurve PolesCount=3 KnotsCount=2 Degree=2 IsPeriodic=0
    g36: GeomPoint X=115.828 Y=17.157 Z=0
    g37: GeomPoint X=116.345 Y=16.3232 Z=0
    g38: LineSegment StartX=115.828 StartY=17.157 StartZ=0 EndX=115.828 EndY=20.8307 EndZ=0
    g39: Circle CenterX=115.828 CenterY=20.8307 CenterZ=0 NormalX=0 NormalY=0 NormalZ=1 AngleXU=0 Radius=1
    g40: Circle CenterX=115.831 CenterY=21.3396 CenterZ=0 NormalX=0 NormalY=0 NormalZ=1 AngleXU=0 Radius=1
    g41: Circle CenterX=116.173 CenterY=21.5825 CenterZ=0 NormalX=0 NormalY=0 NormalZ=1 AngleXU=0 Radius=1
    g42: BSplineCurve PolesCount=3 KnotsCount=2 Degree=2 IsPeriodic=0
    g43: GeomPoint X=115.828 Y=20.8307 Z=0
    g44: GeomPoint X=116.173 Y=21.5825 Z=0
  constraints (70):
    c: Horizontal(g0)
    c: Distance(g0) = 3
    c: Coincident(g1,g0)
    c: Vertical(g1)
    c: Block(g2)
    c: Block(g0)
    c: Coincident(g3,g0)
    c: Coincident(g3,g2)
    c: Vertical(g3)
    c: Block(g1)
    c: Block(g4)
    c: Coincident(g19,g4)
    c: Block(g19)
    c: Equal(g5, g6-g11) x6
    c: InternalAlignment(g5-g11 -> g12) x7
    c: InternalAlignment(g13-g17 -> g12) x5
    c: Block(g12)
    c: Coincident(g18,g12)
    c: Block(g18)
    c: Coincident(g20,g2)
    c: Coincident(g20,g19)
    c: Horizontal(g20)
    c: Distance(g20) = 93.4
    c: Coincident(g21,g1)
    c: Horizontal(g21)
    c: Distance(g21) = 101.7
    c: Horizontal(g23)
    c: Distance(g23) = 8
    c: Coincident(g24,g23)
    c: Block(g23)
    c: Coincident(g22,g24)
    c: Block(g24)
    c: Block(g22)
    c: Distance(g22) = 1.61553
    c: Coincident(g25,g18)
    c: Block(g25)
    c: Weight(g26) = 1
    c: Equal(g26,g27)
    c: Equal(g26,g28)
    c: Coincident(g29,g4)
    c: InternalAlignment(g26,g29)
    c: InternalAlignment(g27,g29)
    c: InternalAlignment(g28,g29)
    c: InternalAlignment(g30,g29)
    c: InternalAlignment(g31,g29)
    c: Block(g29)
    c: Weight(g32) = 1
    c: Equal(g32,g33)
    c: Equal(g32,g34)
    c: Coincident(g35,g29)
    c: InternalAlignment(g32,g35)
    c: InternalAlignment(g33,g35)
    c: InternalAlignment(g34,g35)
    c: InternalAlignment(g36,g35)
    c: InternalAlignment(g37,g35)
    c: Block(g35)
    c: Coincident(g38,g35)
    c: Vertical(g38)
    c: Block(g38)
    c: Coincident(g42,g38)
    c: Weight(g39) = 1
    c: Equal(g39,g40)
    c: Equal(g39,g41)
    c: Coincident(g42,g25)
    c: InternalAlignment(g39,g42)
    c: InternalAlignment(g40,g42)
    c: InternalAlignment(g41,g42)
    c: InternalAlignment(g43,g42)
    c: InternalAlignment(g44,g42)
    c: Block(g42)
FEATURE [Part::Extrusion] Extrude064  label="bottom016"
  Base = -> Sketch073
  Dir = (0,0,1)
  DirMode = 2
  FaceMakerClass = Part::FaceMakerBullseye
  LengthFwd = 71.4
  LengthRev = 0
  Placement = pos=(0,0,0.3) rot=(0,0,1;0rad)
  Solid = true
  Symmetric = false
FEATURE [Part::Revolution] Revolve157  label="removeToCreateScrewAndThreadedInsertHole063"
  Angle = 360
  Axis = (0,1,0)
  Base = (0,0,0)
  FaceMakerClass = Part::FaceMakerBullseye
  Placement = pos=(12.5,0,10) rot=(0,0,1;0rad)
  Solid = false
  Source = -> Face141
  Symmetric = false
FEATURE [Sketcher::SketchObject] Sketch074
  FullyConstrained = true
  Placement = pos=(117,19,0) rot=(0.57735,0.57735,0.57735;2.0944rad)
  sketch-geometry (48):
    g0: LineSegment StartX=-49.19 StartY=69.25 StartZ=0 EndX=-49.19 EndY=66.25 EndZ=0
    g1: LineSegment StartX=-49.19 StartY=63.5 StartZ=0 EndX=-49.19 EndY=60.5 EndZ=0
    g2: LineSegment StartX=-49.19 StartY=57.75 StartZ=0 EndX=-49.19 EndY=54.75 EndZ=0
    g3: LineSegment StartX=-49.19 StartY=52 StartZ=0 EndX=-49.19 EndY=49 EndZ=0
    g4: LineSegment StartX=-49.19 StartY=46.25 StartZ=0 EndX=-49.19 EndY=43.25 EndZ=0
    g5: LineSegment StartX=-49.19 StartY=40.5 StartZ=0 EndX=-49.19 EndY=37.5 EndZ=0
    g6: LineSegment StartX=-49.19 StartY=34.5 StartZ=0 EndX=-49.19 EndY=31.5 EndZ=0
    g7: LineSegment StartX=-49.19 StartY=28.75 StartZ=0 EndX=-49.19 EndY=25.75 EndZ=0
    g8: LineSegment StartX=-49.19 StartY=23 StartZ=0 EndX=-49.19 EndY=20 EndZ=0
    g9: LineSegment StartX=-49.19 StartY=17.25 StartZ=0 EndX=-49.19 EndY=14.25 EndZ=0
    g10: LineSegment StartX=-49.19 StartY=11.5 StartZ=0 EndX=-49.19 EndY=8.5 EndZ=0
    g11: LineSegment StartX=-49.19 StartY=5.75 StartZ=0 EndX=-49.19 EndY=2.75 EndZ=0
    g12: ArcOfCircle CenterX=-1.5 CenterY=67.75 CenterZ=0 NormalX=0 NormalY=0 NormalZ=1 AngleXU=0 Radius=1.5 StartAngle=4.71239 EndAngle=7.85398
    g13: ArcOfCircle CenterX=-1.5 CenterY=62 CenterZ=0 NormalX=0 NormalY=0 NormalZ=1 AngleXU=0 Radius=1.5 StartAngle=4.71239 EndAngle=7.85398
    g14: ArcOfCircle CenterX=-1.5 CenterY=56.25 CenterZ=0 NormalX=0 NormalY=0 NormalZ=1 AngleXU=0 Radius=1.5 StartAngle=4.71239 EndAngle=7.85398
    g15: ArcOfCircle CenterX=-11.49 CenterY=50.5 CenterZ=0 NormalX=0 NormalY=0 NormalZ=1 AngleXU=0 Radius=1.5 StartAngle=4.71239 EndAngle=7.85398
    g16: ArcOfCircle CenterX=-16.28 CenterY=44.75 CenterZ=0 NormalX=0 NormalY=0 NormalZ=1 AngleXU=0 Radius=1.5 StartAngle=4.71239 EndAngle=7.85398
    g17: ArcOfCircle CenterX=-18.2337 CenterY=39 CenterZ=0 NormalX=0 NormalY=0 NormalZ=1 AngleXU=0 Radius=1.5 StartAngle=4.71485 EndAngle=7.85398
    g18: ArcOfCircle CenterX=-16.2837 CenterY=27.25 CenterZ=0 NormalX=0 NormalY=0 NormalZ=1 AngleXU=0 Radius=1.5 StartAngle=4.71485 EndAngle=7.85398
    g19: ArcOfCircle CenterX=-18.2337 CenterY=33 CenterZ=0 NormalX=0 NormalY=0 NormalZ=1 AngleXU=0 Radius=1.5 StartAngle=4.71485 EndAngle=7.85398
    g20: ArcOfCircle CenterX=-11.49 CenterY=21.5 CenterZ=0 NormalX=0 NormalY=0 NormalZ=1 AngleXU=0 Radius=1.5 StartAngle=4.71239 EndAngle=7.85398
    g21: ArcOfCircle CenterX=-1.5 CenterY=4.25 CenterZ=0 NormalX=0 NormalY=0 NormalZ=1 AngleXU=0 Radius=1.5 StartAngle=4.71239 EndAngle=7.85398
    g22: ArcOfCircle CenterX=-1.5 CenterY=10 CenterZ=0 NormalX=0 NormalY=0 NormalZ=1 AngleXU=0 Radius=1.5 StartAngle=4.71239 EndAngle=7.85398
    g23: ArcOfCircle CenterX=-1.5 CenterY=15.75 CenterZ=0 NormalX=0 NormalY=0 NormalZ=1 AngleXU=0 Radius=1.5 StartAngle=4.71239 EndAngle=7.85398
    g24: LineSegment StartX=-49.19 StartY=69.25 StartZ=0 EndX=-1.5 EndY=69.25 EndZ=0
    g25: LineSegment StartX=-49.19 StartY=66.25 StartZ=0 EndX=-1.5 EndY=66.25 EndZ=0
    g26: LineSegment StartX=-49.19 StartY=63.5 StartZ=0 EndX=-1.5 EndY=63.5 EndZ=0
    g27: LineSegment StartX=-49.19 StartY=60.5 StartZ=0 EndX=-1.5 EndY=60.5 EndZ=0
    g28: LineSegment StartX=-49.19 StartY=57.75 StartZ=0 EndX=-1.5 EndY=57.75 EndZ=0
    g29: LineSegment StartX=-49.19 StartY=54.75 StartZ=0 EndX=-1.5 EndY=54.75 EndZ=0
    g30: LineSegment StartX=-49.19 StartY=52 StartZ=0 EndX=-11.49 EndY=52 EndZ=0
    g31: LineSegment StartX=-49.19 StartY=49 StartZ=0 EndX=-11.49 EndY=49 EndZ=0
    g32: LineSegment StartX=-49.19 StartY=46.25 StartZ=0 EndX=-16.28 EndY=46.25 EndZ=0
    g33: LineSegment StartX=-49.19 StartY=43.25 StartZ=0 EndX=-16.28 EndY=43.25 EndZ=0
    g34: LineSegment StartX=-49.19 StartY=40.5 StartZ=0 EndX=-18.2337 EndY=40.5 EndZ=0
    g35: LineSegment StartX=-49.19 StartY=37.5 StartZ=0 EndX=-18.23 EndY=37.5 EndZ=0
    g36: LineSegment StartX=-49.19 StartY=34.5 StartZ=0 EndX=-18.2337 EndY=34.5 EndZ=0
    g37: LineSegment StartX=-49.19 StartY=31.5 StartZ=0 EndX=-18.23 EndY=31.5 EndZ=0
    g38: LineSegment StartX=-49.19 StartY=28.75 StartZ=0 EndX=-16.2837 EndY=28.75 EndZ=0
    g39: LineSegment StartX=-49.19 StartY=25.75 StartZ=0 EndX=-16.28 EndY=25.75 EndZ=0
    g40: LineSegment StartX=-49.19 StartY=23 StartZ=0 EndX=-11.49 EndY=23 EndZ=0
    g41: LineSegment StartX=-49.19 StartY=20 StartZ=0 EndX=-11.49 EndY=20 EndZ=0
    g42: LineSegment StartX=-49.19 StartY=17.25 StartZ=0 EndX=-1.5 EndY=17.25 EndZ=0
    g43: LineSegment StartX=-49.19 StartY=14.25 StartZ=0 EndX=-1.5 EndY=14.25 EndZ=0
    g44: LineSegment StartX=-49.19 StartY=11.5 StartZ=0 EndX=-1.5 EndY=11.5 EndZ=0
    g45: LineSegment StartX=-49.19 StartY=8.5 StartZ=0 EndX=-1.5 EndY=8.5 EndZ=0
    g46: LineSegment StartX=-49.19 StartY=5.75 StartZ=0 EndX=-1.5 EndY=5.75 EndZ=0
    g47: LineSegment StartX=-49.19 StartY=2.75 StartZ=0 EndX=-1.5 EndY=2.75 EndZ=0
  constraints (120):
    c: Vertical(g0)
    c: Distance(g0) = 3
    c: Block(g0)
    c: Vertical(g1)
    c: Distance(g1) = 3
    c: Vertical(g2)
    c: Equal(g0,g2) = 3
    c: Block(g2)
    c: Vertical(g3)
    c: Equal(g1,g3) = 3
    c: Vertical(g4)
    c: Equal(g0,g4) = 3
    c: Block(g4)
    c: Vertical(g5)
    c: Equal(g1,g5) = 3
    c: Vertical(g6)
    c: Equal(g0,g6) = 3
    c: Block(g6)
    c: Vertical(g7)
    c: Equal(g1,g7) = 3
    c: Vertical(g8)
    c: Equal(g0,g8) = 3
    c: Block(g8)
    c: Vertical(g9)
    c: Equal(g1,g9) = 3
    c: Vertical(g10)
    c: Equal(g0,g10) = 3
    c: Block(g10)
    c: Vertical(g11)
    c: Equal(g1,g11) = 3
    c: Block(g12)
    c: Block(g13)
    c: Block(g14)
    c: Block(g15)
    c: Block(g16)
    c: Block(g17)
    c: Block(g18)
    c: Block(g19)
    c: Block(g20)
    c: Block(g21)
    c: Block(g22)
    c: Block(g23)
    c: Block(g11)
    c: Block(g9)
    c: Block(g7)
    c: Block(g5)
    c: Block(g3)
    c: Block(g1)
    c: Coincident(g24,g0)
    c: Coincident(g24,g12)
    c: Horizontal(g24)
    c: Coincident(g25,g0)
    c: Coincident(g25,g12)
    c: Horizontal(g25)
    c: Coincident(g26,g1)
    c: Coincident(g26,g13)
    c: Horizontal(g26)
    c: Coincident(g27,g1)
    c: Coincident(g27,g13)
    c: Horizontal(g27)
    c: Coincident(g28,g2)
    c: Coincident(g28,g14)
    c: Horizontal(g28)
    c: Coincident(g29,g2)
    c: Coincident(g29,g14)
    c: Horizontal(g29)
    c: Coincident(g30,g3)
    c: Coincident(g30,g15)
    c: Horizontal(g30)
    c: Coincident(g31,g3)
    c: Coincident(g31,g15)
    c: Horizontal(g31)
    c: Coincident(g32,g4)
    c: Coincident(g32,g16)
    c: Horizontal(g32)
    c: Coincident(g33,g4)
    c: Coincident(g33,g16)
    c: Horizontal(g33)
    c: Coincident(g34,g5)
    c: Coincident(g34,g17)
    c: Horizontal(g34)
    c: Coincident(g35,g5)
    c: Coincident(g35,g17)
    c: Horizontal(g35)
    c: Coincident(g36,g6)
    c: Coincident(g36,g19)
    c: Horizontal(g36)
    c: Coincident(g37,g6)
    c: Coincident(g37,g19)
    c: Horizontal(g37)
    c: Coincident(g38,g7)
    c: Coincident(g38,g18)
    c: Horizontal(g38)
    c: Coincident(g39,g7)
    c: Coincident(g39,g18)
    c: Horizontal(g39)
    c: Coincident(g40,g8)
    c: Coincident(g40,g20)
    c: Horizontal(g40)
    c: Coincident(g41,g8)
    c: Coincident(g41,g20)
    c: Horizontal(g41)
    c: Coincident(g42,g9)
    c: Coincident(g42,g23)
    c: Horizontal(g42)
    c: Coincident(g43,g9)
    c: Coincident(g43,g23)
    c: Horizontal(g43)
    c: Coincident(g44,g10)
    c: Coincident(g44,g22)
    c: Horizontal(g44)
    c: Coincident(g45,g10)
    c: Coincident(g45,g22)
    c: Horizontal(g45)
    c: Coincident(g46,g11)
    c: Coincident(g46,g21)
    c: Horizontal(g46)
    c: Coincident(g47,g11)
    c: Coincident(g47,g21)
    c: Horizontal(g47)
FEATURE [Part::Extrusion] Extrude065
  Base = -> Sketch074
  Dir = (1,0,0)
  DirMode = 2
  FaceMakerClass = Part::FaceMakerBullseye
  LengthFwd = 23
  LengthRev = 0
  Placement = pos=(-19,0,0) rot=(0,0,1;0rad)
  Solid = true
  Symmetric = false
FEATURE [Part::Fillet] Fillet056  label="removeToCreateVentalationHoles003"
  Base = -> Extrude065
  Edges = <same value as first occurrence — deduplicated (x6 in doc)>
  Placement = pos=(7,0.02,0) rot=(0,0,1;0rad)
FEATURE [Part::Revolution] Revolve158  label="removeToCreateScrewAndThreadedInsertHole065"
  Angle = 360
  Axis = (0,1,0)
  Base = (0,0,0)
  FaceMakerClass = Part::FaceMakerBullseye
  Placement = pos=(12.5,0,62) rot=(0,0,1;0rad)
  Solid = false
  Source = -> Face146
  Symmetric = false
FEATURE [Part::Revolution] Revolve159  label="removeToCreateScrewAndThreadedInsertHole066"
  Angle = 360
  Axis = (0,1,0)
  Base = (0,0,0)
  FaceMakerClass = Part::FaceMakerBullseye
  Placement = pos=(89.5,0,68.5) rot=(0,0,1;0rad)
  Solid = false
  Source = -> Face143
  Symmetric = false
FEATURE [Part::Revolution] Revolve160  label="removeToCreateScrewAndThreadedInsertHole067"
  Angle = 360
  Axis = (0,1,0)
  Base = (0,0,0)
  FaceMakerClass = Part::FaceMakerBullseye
  Placement = pos=(89.5,0,3.5) rot=(0,0,1;0rad)
  Solid = false
  Source = -> Face142
  Symmetric = false
FEATURE [Part::Revolution] Revolve161  label="removeToCreateScrewAndThreadedInsertHole068"
  Angle = 360
  Axis = (0,1,0)
  Base = (0,0,0)
  FaceMakerClass = Part::FaceMakerBullseye
  Placement = pos=(109.5,4.7,3.5) rot=(0,0,1;0rad)
  Solid = false
  Source = -> Face145
  Symmetric = false
FEATURE [Part::Revolution] Revolve162  label="removeToCreateScrewAndThreadedInsertHole069"
  Angle = 360
  Axis = (0,1,0)
  Base = (0,0,0)
  FaceMakerClass = Part::FaceMakerBullseye
  Placement = pos=(109.5,4.7,68.5) rot=(0,0,1;0rad)
  Solid = false
  Source = -> Face144
  Symmetric = false
FEATURE [Part::MultiFuse] Fusion141  label="removeToCreateScrewAndThreadedInsertHole064"
  Shapes = -> [Revolve162,Revolve161,Revolve160,Revolve159,Revolve158,Revolve157]
FEATURE [Part::Cylinder] Cylinder062
  Angle = 360
  AttacherType = Attacher::AttachEngine3D
  Height = 20
  Placement = pos=(0,0,36.15) rot=(0,0,1;0rad)
  Radius = 14
FEATURE [Part::Cylinder] Cylinder063
  Angle = 360
  AttacherType = Attacher::AttachEngine3D
  Height = 10
  Placement = pos=(0,0,36.15) rot=(0,0,1;0rad)
  Radius = 4
FEATURE [Part::MultiFuse] Fusion139  label="removeToCreteHoleForPlugHousing052"
  Placement = pos=(70,19,36) rot=(0,1,0;1.5708rad)
  Shapes = -> [Cylinder062,Cylinder063]
FEATURE [Part::Cut] Cut060  label="bottom017"
  Base = -> Extrude064
  Tool = -> Fusion139
FEATURE [Part::Cut] Cut061  label="bottom019"
  Base = -> Cut060
  Tool = -> Fusion141
FEATURE [Part::MultiFuse] Fusion140  label="bottom018"
  Shapes = -> [Cut061,Cut058]
FEATURE [Part::Cut] Cut059  label="bottom020"
  Base = -> Fusion140
  Tool = -> Fillet056
FEATURE [Part::Box] Box036  label="Cube021"
  AttacherType = Attacher::AttachEngine3D
  Height = 80
  Length = 26
  Placement = pos=(0,-1,-5) rot=(0,0,1;0rad)
  Width = 11
FEATURE [Part::Cut] Cut062  label="removeFromBottom002"
  Base = -> Cut057
  Tool = -> Box036
FEATURE [Part::Cut] Cut063
  Base = -> Cut059
  Tool = -> Cut062
FEATURE [Part::Cut] Cut064  label="pcbStands"
  Base = -> Fusion095
  Tool = -> Fusion127
FEATURE [Sketcher::SketchObject] Sketch075  label="topSketch022"
  FullyConstrained = true
  sketch-geometry (6):
    g0: LineSegment StartX=19 StartY=38 StartZ=0 EndX=117 EndY=38 EndZ=0
    g1: ArcOfCircle CenterX=19 CenterY=19 CenterZ=0 NormalX=0 NormalY=0 NormalZ=1 AngleXU=0 Radius=19 StartAngle=1.5708 EndAngle=3.14159
    g2: LineSegment StartX=117 StartY=38 StartZ=0 EndX=117 EndY=19 EndZ=0
    g3: LineSegment StartX=98 StartY=1.0161e-12 StartZ=0 EndX=5.22862e-06 EndY=1.0161e-12 EndZ=0
    g4: LineSegment StartX=5.22862e-06 StartY=19 StartZ=0 EndX=5.22862e-06 EndY=1.0161e-12 EndZ=0
    g5: ArcOfCircle CenterX=98 CenterY=19 CenterZ=0 NormalX=0 NormalY=0 NormalZ=1 AngleXU=0 Radius=19 StartAngle=4.71239 EndAngle=6.28319
  constraints (16):
    c: Horizontal(g0)
    c: Distance(g0) = 98
    c: Coincident(g1,g0)
    c: Block(g1)
    c: Coincident(g2,g0)
    c: Vertical(g2)
    c: Distance(g2) = 19
    c: Horizontal(g3)
    c: Coincident(g4,g1)
    c: Vertical(g4)
    c: Coincident(g3,g4)
    c: Block(g3)
    c: Coincident(g5,g2)
    c: Coincident(g5,g3)
    c: Block(g0)
    c: Block(g5)
FEATURE [Part::Extrusion] Extrude067  label="sideB003"
  Base = -> Sketch075
  Dir = (0,0,1)
  DirMode = 2
  FaceMakerClass = Part::FaceMakerBullseye
  LengthFwd = 3
  LengthRev = 0
  Placement = pos=(0,0,71.7) rot=(0,0,1;0rad)
  Solid = true
  Symmetric = false
FEATURE [Sketcher::SketchObject] Sketch076  label="topSketch023"
  FullyConstrained = true
  sketch-geometry (6):
    g0: LineSegment StartX=19 StartY=38 StartZ=0 EndX=117 EndY=38 EndZ=0
    g1: ArcOfCircle CenterX=19 CenterY=19 CenterZ=0 NormalX=0 NormalY=0 NormalZ=1 AngleXU=0 Radius=19 StartAngle=1.5708 EndAngle=3.14159
    g2: LineSegment StartX=117 StartY=38 StartZ=0 EndX=117 EndY=19 EndZ=0
    g3: LineSegment StartX=98 StartY=1.0161e-12 StartZ=0 EndX=5.22862e-06 EndY=1.0161e-12 EndZ=0
    g4: LineSegment StartX=5.22862e-06 StartY=19 StartZ=0 EndX=5.22862e-06 EndY=1.0161e-12 EndZ=0
    g5: ArcOfCircle CenterX=98 CenterY=19 CenterZ=0 NormalX=0 NormalY=0 NormalZ=1 AngleXU=0 Radius=19 StartAngle=4.71239 EndAngle=6.28319
  constraints (16):
    c: Horizontal(g0)
    c: Distance(g0) = 98
    c: Coincident(g1,g0)
    c: Block(g1)
    c: Coincident(g2,g0)
    c: Vertical(g2)
    c: Distance(g2) = 19
    c: Horizontal(g3)
    c: Coincident(g4,g1)
    c: Vertical(g4)
    c: Coincident(g3,g4)
    c: Block(g3)
    c: Coincident(g5,g2)
    c: Coincident(g5,g3)
    c: Block(g0)
    c: Block(g5)
FEATURE [Part::Extrusion] Extrude066  label="sideA003"
  Base = -> Sketch076
  Dir = (0,0,1)
  DirMode = 2
  FaceMakerClass = Part::FaceMakerBullseye
  LengthFwd = 3
  LengthRev = 0
  Placement = pos=(0,0,-2.7) rot=(0,0,1;0rad)
  Solid = true
  Symmetric = false
FEATURE [Part::MultiFuse] Fusion142  label="removeFromBottom003"
  Placement = pos=(2,0,0) rot=(0,0,1;0rad)
  Shapes = -> [Extrude066,Extrude067]
FEATURE [Part::Cut] Cut065  label="screwRetainers002"
  Base = -> Fusion096
  Tool = -> Fusion142
FEATURE [Sketcher::SketchObject] Sketch077
  FullyConstrained = true
  Placement = pos=(117,19,0) rot=(0.57735,0.57735,0.57735;2.0944rad)
  sketch-geometry (8):
    g0: LineSegment StartX=-49.19 StartY=63.5 StartZ=0 EndX=-49.19 EndY=60.5 EndZ=0
    g1: LineSegment StartX=-49.19 StartY=11.5 StartZ=0 EndX=-49.19 EndY=8.5 EndZ=0
    g2: ArcOfCircle CenterX=-1.5 CenterY=62 CenterZ=0 NormalX=0 NormalY=0 NormalZ=1 AngleXU=0 Radius=1.5 StartAngle=4.71239 EndAngle=7.85398
    g3: ArcOfCircle CenterX=-1.5 CenterY=10 CenterZ=0 NormalX=0 NormalY=0 NormalZ=1 AngleXU=0 Radius=1.5 StartAngle=4.71239 EndAngle=7.85398
    g4: LineSegment StartX=-49.19 StartY=63.5 StartZ=0 EndX=-1.5 EndY=63.5 EndZ=0
    g5: LineSegment StartX=-49.19 StartY=60.5 StartZ=0 EndX=-1.5 EndY=60.5 EndZ=0
    g6: LineSegment StartX=-49.19 StartY=11.5 StartZ=0 EndX=-1.5 EndY=11.5 EndZ=0
    g7: LineSegment StartX=-49.19 StartY=8.5 StartZ=0 EndX=-1.5 EndY=8.5 EndZ=0
  constraints (19):
    c: Vertical(g0)
    c: Distance(g0) = 3
    c: Vertical(g1)
    c: Block(g1)
    c: Block(g2)
    c: Block(g3)
    c: Block(g0)
    c: Coincident(g4,g0)
    c: Coincident(g4,g2)
    c: Horizontal(g4)
    c: Coincident(g5,g0)
    c: Coincident(g5,g2)
    c: Horizontal(g5)
    c: Coincident(g6,g1)
    c: Coincident(g6,g3)
    c: Horizontal(g6)
    c: Coincident(g7,g1)
    c: Coincident(g7,g3)
    c: Horizontal(g7)
FEATURE [Part::Extrusion] Extrude068
  Base = -> Sketch077
  Dir = (1,0,0)
  DirMode = 2
  FaceMakerClass = Part::FaceMakerBullseye
  LengthFwd = 10
  LengthRev = 0
  Solid = true
  Symmetric = false
FEATURE [Part::Fillet] Fillet057  label="removeFromtMoreFrontCaseScrewRetainers002"
  Base = -> Extrude068
  Edges = 4 edges r=1.49: [Edge6,Edge11,Edge18,Edge23]
  Placement = pos=(-12,0,0) rot=(0,0,1;0rad)
FEATURE [Sketcher::SketchObject] Sketch078
  FullyConstrained = true
  Placement = pos=(117,19,0) rot=(0.57735,0.57735,0.57735;2.0944rad)
  sketch-geometry (8):
    g0: LineSegment StartX=-49.19 StartY=69.25 StartZ=0 EndX=-49.19 EndY=66.25 EndZ=0
    g1: LineSegment StartX=-49.19 StartY=5.75 StartZ=0 EndX=-49.19 EndY=2.75 EndZ=0
    g2: ArcOfCircle CenterX=-1.5 CenterY=67.75 CenterZ=0 NormalX=0 NormalY=0 NormalZ=1 AngleXU=0 Radius=1.5 StartAngle=4.71239 EndAngle=7.85398
    g3: ArcOfCircle CenterX=-1.5 CenterY=4.25 CenterZ=0 NormalX=0 NormalY=0 NormalZ=1 AngleXU=0 Radius=1.5 StartAngle=4.71239 EndAngle=7.85398
    g4: LineSegment StartX=-49.19 StartY=69.25 StartZ=0 EndX=-1.5 EndY=69.25 EndZ=0
    g5: LineSegment StartX=-49.19 StartY=66.25 StartZ=0 EndX=-1.5 EndY=66.25 EndZ=0
    g6: LineSegment StartX=-49.19 StartY=5.75 StartZ=0 EndX=-1.5 EndY=5.75 EndZ=0
    g7: LineSegment StartX=-49.19 StartY=2.75 StartZ=0 EndX=-1.5 EndY=2.75 EndZ=0
  constraints (19):
    c: Vertical(g0)
    c: Distance(g0) = 3
    c: Block(g0)
    c: Vertical(g1)
    c: Block(g2)
    c: Block(g3)
    c: Block(g1)
    c: Coincident(g4,g0)
    c: Coincident(g4,g2)
    c: Horizontal(g4)
    c: Coincident(g5,g0)
    c: Coincident(g5,g2)
    c: Horizontal(g5)
    c: Coincident(g6,g1)
    c: Coincident(g6,g3)
    c: Horizontal(g6)
    c: Coincident(g7,g1)
    c: Coincident(g7,g3)
    c: Horizontal(g7)
FEATURE [Part::Extrusion] Extrude069
  Base = -> Sketch078
  Dir = (1,0,0)
  DirMode = 2
  FaceMakerClass = Part::FaceMakerBullseye
  LengthFwd = 10
  LengthRev = 0
  Solid = true
  Symmetric = false
FEATURE [Part::Fillet] Fillet058  label="removeFromtMoreFrontCaseScrewRetainers003"
  Base = -> Extrude069
  Edges = 4 edges r=1.49: [Edge6,Edge11,Edge18,Edge23]
  Placement = pos=(-4,0,0) rot=(0,0,1;0rad)
FEATURE [Part::Cut] Cut066
  Base = -> Cut065
  Tool = -> Fillet058
FEATURE [Part::Cut] Cut067  label="screwPillars"
  Base = -> Cut066
  Tool = -> Fillet057
FEATURE [Part::MultiFuse] Fusion143  label="bottom021"
  Shapes = -> [Cut031,Cut063]
FEATURE [Part::Cylinder] Cylinder
  Angle = 360
  AttacherType = Attacher::AttachEngine3D
  Height = 10
  Placement = pos=(20.65,12,4.68) rot=(1,0,0;1.5708rad)
  Radius = 2
FEATURE [Part::Cylinder] Cylinder064
  Angle = 360
  AttacherType = Attacher::AttachEngine3D
  Height = 10
  Placement = pos=(20.65,12,67.38) rot=(1,0,0;1.5708rad)
  Radius = 2
FEATURE [Part::Cylinder] Cylinder065
  Angle = 360
  AttacherType = Attacher::AttachEngine3D
  Height = 10
  Placement = pos=(77.15,12,67.38) rot=(1,0,0;1.5708rad)
  Radius = 2
FEATURE [Part::Cylinder] Cylinder066
  Angle = 360
  AttacherType = Attacher::AttachEngine3D
  Height = 10
  Placement = pos=(77.15,12,4.68) rot=(1,0,0;1.5708rad)
  Radius = 2
FEATURE [Part::MultiFuse] Fusion144  label="removeFromThreadedInsertHousing"
  Shapes = -> [Cylinder065,Cylinder064,Cylinder,Cylinder066]
FEATURE [Part::Cut] Cut068  label="pcbStands001"
  Base = -> Cut064
  Tool = -> Fusion144
FEATURE [Part::MultiFuse] Fusion145
  Shapes = -> [Cut068,Fusion143]
FEATURE [Part::MultiFuse] Fusion146
  Shapes = -> [Fusion145]
FEATURE [Part::MultiFuse] Fusion147  label="bottom022"
  Shapes = -> [Cut067,Fusion146]
FEATURE [Part::MultiFuse] Fusion148  label="casePillars005"
  Shapes = -> [Cut047,Fusion092]
FEATURE [Part::MultiFuse] Fusion149  label="bottom023"
  Shapes = -> [Fusion124,Fusion113,Fusion147]
FEATURE [Part::MultiFuse] Fusion150  label="topBits"
  Shapes = -> [Cut025,Fusion148,Cut030,Fillet034]
FEATURE [Part::Feature] Face149 .. Face152  x4 (patterned run collapsed; names and placements below)
  shape: bbox 3.2 x 1.5 x 2e-07 mm, 1 faces, 0 solids (baked)
FEATURE [Part::Feature] Face153
  shape: bbox 3.6 x 3.2 x 2e-07 mm, 1 faces, 0 solids (baked)
FEATURE [Part::Feature] Face154
  shape: bbox 3.6 x 3.2 x 2e-07 mm, 1 faces, 0 solids (baked)
FEATURE [Sketcher::SketchObject] Sketch079  label="topSketch024"
  FullyConstrained = true
  sketch-geometry (6):
    g0: LineSegment StartX=19 StartY=38 StartZ=0 EndX=117 EndY=38 EndZ=0
    g1: ArcOfCircle CenterX=19 CenterY=19 CenterZ=0 NormalX=0 NormalY=0 NormalZ=1 AngleXU=0 Radius=19 StartAngle=1.5708 EndAngle=3.14159
    g2: LineSegment StartX=117 StartY=38 StartZ=0 EndX=117 EndY=19 EndZ=0
    g3: LineSegment StartX=98 StartY=1.0161e-12 StartZ=0 EndX=5.22862e-06 EndY=1.0161e-12 EndZ=0
    g4: LineSegment StartX=5.22862e-06 StartY=19 StartZ=0 EndX=5.22862e-06 EndY=1.0161e-12 EndZ=0
    g5: ArcOfCircle CenterX=98 CenterY=19 CenterZ=0 NormalX=0 NormalY=0 NormalZ=1 AngleXU=0 Radius=19 StartAngle=4.71239 EndAngle=6.28319
  constraints (16):
    c: Horizontal(g0)
    c: Distance(g0) = 98
    c: Coincident(g1,g0)
    c: Block(g1)
    c: Coincident(g2,g0)
    c: Vertical(g2)
    c: Distance(g2) = 19
    c: Horizontal(g3)
    c: Coincident(g4,g1)
    c: Vertical(g4)
    c: Coincident(g3,g4)
    c: Block(g3)
    c: Coincident(g5,g2)
    c: Coincident(g5,g3)
    c: Block(g0)
    c: Block(g5)
FEATURE [Sketcher::SketchObject] Sketch080  label="topSketch025"
  FullyConstrained = true
  sketch-geometry (6):
    g0: LineSegment StartX=19 StartY=38 StartZ=0 EndX=117 EndY=38 EndZ=0
    g1: ArcOfCircle CenterX=19 CenterY=19 CenterZ=0 NormalX=0 NormalY=0 NormalZ=1 AngleXU=0 Radius=19 StartAngle=1.5708 EndAngle=3.14159
    g2: LineSegment StartX=117 StartY=38 StartZ=0 EndX=117 EndY=19 EndZ=0
    g3: LineSegment StartX=98 StartY=1.0161e-12 StartZ=0 EndX=5.22862e-06 EndY=1.0161e-12 EndZ=0
    g4: LineSegment StartX=5.22862e-06 StartY=19 StartZ=0 EndX=5.22862e-06 EndY=1.0161e-12 EndZ=0
    g5: ArcOfCircle CenterX=98 CenterY=19 CenterZ=0 NormalX=0 NormalY=0 NormalZ=1 AngleXU=0 Radius=19 StartAngle=4.71239 EndAngle=6.28319
  constraints (16):
    c: Horizontal(g0)
    c: Distance(g0) = 98
    c: Coincident(g1,g0)
    c: Block(g1)
    c: Coincident(g2,g0)
    c: Vertical(g2)
    c: Distance(g2) = 19
    c: Horizontal(g3)
    c: Coincident(g4,g1)
    c: Vertical(g4)
    c: Coincident(g3,g4)
    c: Block(g3)
    c: Coincident(g5,g2)
    c: Coincident(g5,g3)
    c: Block(g0)
    c: Block(g5)
FEATURE [Part::Extrusion] Extrude070  label="sideA004"
  Base = -> Sketch080
  Dir = (0,0,1)
  DirMode = 2
  FaceMakerClass = Part::FaceMakerBullseye
  LengthFwd = 3
  LengthRev = 0
  Placement = pos=(0,0,-2.7) rot=(0,0,1;0rad)
  Solid = true
  Symmetric = false
FEATURE [Sketcher::SketchObject] Sketch081
  FullyConstrained = true
  Placement = pos=(117,19,0) rot=(0.57735,0.57735,0.57735;2.0944rad)
  sketch-geometry (8):
    g0: LineSegment StartX=-49.19 StartY=63.5 StartZ=0 EndX=-49.19 EndY=60.5 EndZ=0
    g1: LineSegment StartX=-49.19 StartY=11.5 StartZ=0 EndX=-49.19 EndY=8.5 EndZ=0
    g2: ArcOfCircle CenterX=-1.5 CenterY=62 CenterZ=0 NormalX=0 NormalY=0 NormalZ=1 AngleXU=0 Radius=1.5 StartAngle=4.71239 EndAngle=7.85398
    g3: ArcOfCircle CenterX=-1.5 CenterY=10 CenterZ=0 NormalX=0 NormalY=0 NormalZ=1 AngleXU=0 Radius=1.5 StartAngle=4.71239 EndAngle=7.85398
    g4: LineSegment StartX=-49.19 StartY=63.5 StartZ=0 EndX=-1.5 EndY=63.5 EndZ=0
    g5: LineSegment StartX=-49.19 StartY=60.5 StartZ=0 EndX=-1.5 EndY=60.5 EndZ=0
    g6: LineSegment StartX=-49.19 StartY=11.5 StartZ=0 EndX=-1.5 EndY=11.5 EndZ=0
    g7: LineSegment StartX=-49.19 StartY=8.5 StartZ=0 EndX=-1.5 EndY=8.5 EndZ=0
  constraints (19):
    c: Vertical(g0)
    c: Distance(g0) = 3
    c: Vertical(g1)
    c: Block(g1)
    c: Block(g2)
    c: Block(g3)
    c: Block(g0)
    c: Coincident(g4,g0)
    c: Coincident(g4,g2)
    c: Horizontal(g4)
    c: Coincident(g5,g0)
    c: Coincident(g5,g2)
    c: Horizontal(g5)
    c: Coincident(g6,g1)
    c: Coincident(g6,g3)
    c: Horizontal(g6)
    c: Coincident(g7,g1)
    c: Coincident(g7,g3)
    c: Horizontal(g7)
FEATURE [Part::Extrusion] Extrude071  label="sideB004"
  Base = -> Sketch079
  Dir = (0,0,1)
  DirMode = 2
  FaceMakerClass = Part::FaceMakerBullseye
  LengthFwd = 3
  LengthRev = 0
  Placement = pos=(0,0,71.7) rot=(0,0,1;0rad)
  Solid = true
  Symmetric = false
FEATURE [Part::MultiFuse] Fusion152  label="removeFromBottom004"
  Placement = pos=(2,0,0) rot=(0,0,1;0rad)
  Shapes = -> [Extrude070,Extrude071]
FEATURE [Part::Extrusion] Extrude072
  Base = -> Sketch081
  Dir = (1,0,0)
  DirMode = 2
  FaceMakerClass = Part::FaceMakerBullseye
  LengthFwd = 10
  LengthRev = 0
  Solid = true
  Symmetric = false
FEATURE [Part::Fillet] Fillet059  label="removeFromtMoreFrontCaseScrewRetainers004"
  Base = -> Extrude072
  Edges = 4 edges r=1.49: [Edge6,Edge11,Edge18,Edge23]
  Placement = pos=(-12,0,0) rot=(0,0,1;0rad)
FEATURE [Sketcher::SketchObject] Sketch082
  FullyConstrained = true
  Placement = pos=(117,19,0) rot=(0.57735,0.57735,0.57735;2.0944rad)
  sketch-geometry (8):
    g0: LineSegment StartX=-49.19 StartY=69.25 StartZ=0 EndX=-49.19 EndY=66.25 EndZ=0
    g1: LineSegment StartX=-49.19 StartY=5.75 StartZ=0 EndX=-49.19 EndY=2.75 EndZ=0
    g2: ArcOfCircle CenterX=-1.5 CenterY=67.75 CenterZ=0 NormalX=0 NormalY=0 NormalZ=1 AngleXU=0 Radius=1.5 StartAngle=4.71239 EndAngle=7.85398
    g3: ArcOfCircle CenterX=-1.5 CenterY=4.25 CenterZ=0 NormalX=0 NormalY=0 NormalZ=1 AngleXU=0 Radius=1.5 StartAngle=4.71239 EndAngle=7.85398
    g4: LineSegment StartX=-49.19 StartY=69.25 StartZ=0 EndX=-1.5 EndY=69.25 EndZ=0
    g5: LineSegment StartX=-49.19 StartY=66.25 StartZ=0 EndX=-1.5 EndY=66.25 EndZ=0
    g6: LineSegment StartX=-49.19 StartY=5.75 StartZ=0 EndX=-1.5 EndY=5.75 EndZ=0
    g7: LineSegment StartX=-49.19 StartY=2.75 StartZ=0 EndX=-1.5 EndY=2.75 EndZ=0
  constraints (19):
    c: Vertical(g0)
    c: Distance(g0) = 3
    c: Block(g0)
    c: Vertical(g1)
    c: Block(g2)
    c: Block(g3)
    c: Block(g1)
    c: Coincident(g4,g0)
    c: Coincident(g4,g2)
    c: Horizontal(g4)
    c: Coincident(g5,g0)
    c: Coincident(g5,g2)
    c: Horizontal(g5)
    c: Coincident(g6,g1)
    c: Coincident(g6,g3)
    c: Horizontal(g6)
    c: Coincident(g7,g1)
    c: Coincident(g7,g3)
    c: Horizontal(g7)
FEATURE [Part::Extrusion] Extrude073
  Base = -> Sketch082
  Dir = (1,0,0)
  DirMode = 2
  FaceMakerClass = Part::FaceMakerBullseye
  LengthFwd = 10
  LengthRev = 0
  Solid = true
  Symmetric = false
FEATURE [Part::Fillet] Fillet060  label="removeFromtMoreFrontCaseScrewRetainers005"
  Base = -> Extrude073
  Edges = 4 edges r=1.49: [Edge6,Edge11,Edge18,Edge23]
  Placement = pos=(-4,0,0) rot=(0,0,1;0rad)
FEATURE [Part::Revolution] Revolve163  label="backCaseScrewRetainer004"
  Angle = 360
  Axis = (0,1,0)
  Base = (0,0,0)
  FaceMakerClass = Part::FaceMakerBullseye
  Placement = pos=(12.5,3,62) rot=(0,0,1;0rad)
  Solid = false
  Source = -> Face149
  Symmetric = false
FEATURE [Part::Revolution] Revolve164  label="frontCaseScrewRetainer006"
  Angle = 360
  Axis = (0,1,0)
  Base = (0,0,0)
  FaceMakerClass = Part::FaceMakerBullseye
  Placement = pos=(89.5,3,68.5) rot=(0,0,1;0rad)
  Solid = false
  Source = -> Face151
  Symmetric = false
FEATURE [Part::Revolution] Revolve165  label="frontCaseScrewRetainer007"
  Angle = 360
  Axis = (0,1,0)
  Base = (0,0,0)
  FaceMakerClass = Part::FaceMakerBullseye
  Placement = pos=(89.5,3,3.5) rot=(0,0,1;0rad)
  Solid = false
  Source = -> Face152
  Symmetric = false
FEATURE [Part::Revolution] Revolve166  label="backCaseScrewRetainer005"
  Angle = 360
  Axis = (0,1,0)
  Base = (0,0,0)
  FaceMakerClass = Part::FaceMakerBullseye
  Placement = pos=(12.5,3,10) rot=(0,0,1;0rad)
  Solid = false
  Source = -> Face150
  Symmetric = false
FEATURE [Part::Revolution] Revolve167  label="moreFrontCaseScrewRetainer006"
  Angle = 360
  Axis = (0,1,0)
  Base = (0,0,0)
  FaceMakerClass = Part::FaceMakerBullseye
  Placement = pos=(109.5,4.5,68.5) rot=(0,0,1;0rad)
  Solid = false
  Source = -> Face153
  Symmetric = false
FEATURE [Part::Revolution] Revolve168  label="moreFrontCaseScrewRetainer007"
  Angle = 360
  Axis = (0,1,0)
  Base = (0,0,0)
  FaceMakerClass = Part::FaceMakerBullseye
  Placement = pos=(109.5,4.5,3.5) rot=(0,0,1;0rad)
  Solid = false
  Source = -> Face154
  Symmetric = false
FEATURE [Part::MultiFuse] Fusion151  label="screwRetainers003"
  Shapes = -> [Revolve168,Revolve167,Revolve166,Revolve165,Revolve164,Revolve163]
FEATURE [Part::Cut] Cut069  label="screwRetainers004"
  Base = -> Fusion151
  Tool = -> Fusion152
FEATURE [Part::Cut] Cut070
  Base = -> Cut069
  Tool = -> Fillet060
FEATURE [Part::Cut] Cut071  label="screwPillars001"
  Base = -> Cut070
  Tool = -> Fillet059
FEATURE [Part::MultiFuse] Fusion153  label="bottom024"
  Shapes = -> [Fusion149,Cut071]
FEATURE [Part::Cylinder] Cylinder067
  Angle = 360
  AttacherType = Attacher::AttachEngine3D
  Height = 10
  Placement = pos=(20.65,12,4.68) rot=(1,0,0;1.5708rad)
  Radius = 2
FEATURE [Part::Cylinder] Cylinder068
  Angle = 360
  AttacherType = Attacher::AttachEngine3D
  Height = 10
  Placement = pos=(20.65,12,67.38) rot=(1,0,0;1.5708rad)
  Radius = 2
FEATURE [Part::Cylinder] Cylinder069
  Angle = 360
  AttacherType = Attacher::AttachEngine3D
  Height = 10
  Placement = pos=(77.15,12,67.38) rot=(1,0,0;1.5708rad)
  Radius = 2
FEATURE [Part::Cylinder] Cylinder070
  Angle = 360
  AttacherType = Attacher::AttachEngine3D
  Height = 10
  Placement = pos=(77.15,12,4.68) rot=(1,0,0;1.5708rad)
  Radius = 2
FEATURE [Part::MultiFuse] Fusion154  label="removeFromThreadedInsertHousing001"
  Shapes = -> [Cylinder069,Cylinder068,Cylinder067,Cylinder070]
FEATURE [Part::Cut] Cut072  label="bottom025"
  Base = -> Fusion153
  Tool = -> Fusion154
FEATURE [Image::ImagePlane] ImagePlane
  XSize = 339
  YSize = 72
FEATURE [Sketcher::SketchObject] Sketch083
  FullyConstrained = true
  MapMode = 5
  Support = -> [XY_Plane]
  sketch-geometry (315):
    g0: LineSegment StartX=-151.619 StartY=28.8932 StartZ=0 EndX=-140.819 EndY=28.8932 EndZ=0
    g1: LineSegment StartX=-151.619 StartY=24.0313 StartZ=0 EndX=-151.619 EndY=28.8932 EndZ=0
    g2: LineSegment StartX=-140.819 StartY=17.7713 StartZ=0 EndX=-151.619 EndY=17.7713 EndZ=0
    g3: LineSegment StartX=-151.619 StartY=17.7713 StartZ=0 EndX=-151.619 EndY=22.6313 EndZ=0
    g4: LineSegment StartX=-151.619 StartY=22.6313 StartZ=0 EndX=-145.128 EndY=22.6313 EndZ=0
    g5: LineSegment StartX=-145.128 StartY=24.0313 StartZ=0 EndX=-140.819 EndY=28.8932 EndZ=0
    g6: LineSegment StartX=-145.128 StartY=22.6313 StartZ=0 EndX=-140.819 EndY=17.7713 EndZ=0
    g7: ArcOfCircle CenterX=-155.157 CenterY=23.3323 CenterZ=0 NormalX=0 NormalY=0 NormalZ=1 AngleXU=0 Radius=6.92354 StartAngle=1.03434 EndAngle=5.24885
    g8: ArcOfCircle CenterX=-155.157 CenterY=23.3323 CenterZ=0 NormalX=0 NormalY=0 NormalZ=1 AngleXU=0 Radius=12.6269 StartAngle=1.28675 EndAngle=4.99643
    g9: LineSegment StartX=-151.619 StartY=35.4532 StartZ=0 EndX=-151.619 EndY=29.2832 EndZ=0
    g10: LineSegment StartX=-151.619 StartY=17.3813 StartZ=0 EndX=-151.619 EndY=11.2113 EndZ=0
    g11-g21: Circle x11 (B-spline internal-alignment scaffolding for g22; pole/knot coordinates omitted)
    g22: BSplineCurve PolesCount=11 KnotsCount=9 Degree=3 IsPeriodic=0
    g23-g31: GeomPoint x9 (B-spline internal-alignment scaffolding for g22; pole/knot coordinates omitted)
    g32-g49: Circle x18 (B-spline internal-alignment scaffolding for g50; pole/knot coordinates omitted)
    g50: BSplineCurve PolesCount=18 KnotsCount=16 Degree=3 IsPeriodic=0
    g51-g66: GeomPoint x16 (B-spline internal-alignment scaffolding for g50; pole/knot coordinates omitted)
    g67: LineSegment StartX=-117.124 StartY=30.093 StartZ=0 EndX=-117.603 EndY=26.5272 EndZ=0
    g68: LineSegment StartX=-117.603 StartY=17.8472 StartZ=0 EndX=-117.124 EndY=14.2659 EndZ=0
    g69: Ellipse CenterX=-109.671 CenterY=20.025 CenterZ=0 NormalX=0 NormalY=0 NormalZ=1 MajorRadius=3.34798 MinorRadius=2.71052 AngleXU=-1.56793
    g70: GeomPoint X=-109.666 Y=18.0598 Z=0
    g71: GeomPoint X=-109.677 Y=21.9902 Z=0
    g72: Ellipse CenterX=-109.671 CenterY=20.0123 CenterZ=0 NormalX=0 NormalY=0 NormalZ=1 MajorRadius=6.93002 MinorRadius=6.36273 AngleXU=-3.13976
    g73: GeomPoint X=-112.417 Y=20.0073 Z=0
    g74: GeomPoint X=-106.925 Y=20.0173 Z=0
    g75: Ellipse CenterX=-51.7682 CenterY=20.1463 CenterZ=0 NormalX=0 NormalY=0 NormalZ=1 MajorRadius=3.19279 MinorRadius=2.71052 AngleXU=-1.52774
    g76: GeomPoint X=-51.6955 Y=18.4606 Z=0
    g77: GeomPoint X=-51.8408 Y=21.832 Z=0
    g78: GeomPoint X=-54.5142 Y=20.1413 Z=0
    g79: GeomPoint X=-49.0221 Y=20.1513 Z=0
    g80: Ellipse CenterX=-51.7682 CenterY=20.1463 CenterZ=0 NormalX=0 NormalY=0 NormalZ=1 MajorRadius=6.93002 MinorRadius=6.36273 AngleXU=-3.13976
    g81: Ellipse CenterX=-22.8436 CenterY=20.1783 CenterZ=0 NormalX=0 NormalY=0 NormalZ=1 MajorRadius=3.31512 MinorRadius=2.71052 AngleXU=-1.60214
    g82: GeomPoint X=-22.9034 Y=18.2706 Z=0
    g83: GeomPoint X=-22.7838 Y=22.0861 Z=0
    g84: GeomPoint X=-25.5897 Y=20.1733 Z=0
    g85: GeomPoint X=-20.0976 Y=20.1833 Z=0
    g86: Ellipse CenterX=-22.8436 CenterY=20.1783 CenterZ=0 NormalX=0 NormalY=0 NormalZ=1 MajorRadius=6.93002 MinorRadius=6.36273 AngleXU=-3.13976
    g87: LineSegment StartX=-101.889 StartY=14.1107 StartZ=0 EndX=-97.7455 EndY=14.1107 EndZ=0
    g88: LineSegment StartX=-93.8155 StartY=14.1107 StartZ=0 EndX=-89.6755 EndY=14.1107 EndZ=0
    g89: LineSegment StartX=-85.7455 StartY=14.1107 StartZ=0 EndX=-81.6055 EndY=14.1107 EndZ=0
    g90: LineSegment StartX=-101.889 StartY=14.1107 StartZ=0 EndX=-101.889 EndY=25.9907 EndZ=0
    g91: LineSegment StartX=-101.889 StartY=25.9907 StartZ=0 EndX=-97.8594 EndY=25.9907 EndZ=0
    g92: LineSegment StartX=-97.8594 StartY=25.9907 StartZ=0 EndX=-97.8594 EndY=24.0907 EndZ=0
    g93: LineSegment StartX=-97.7455 StartY=14.1107 StartZ=0 EndX=-97.7455 EndY=19.9107 EndZ=0
    g94: LineSegment StartX=-89.6755 StartY=14.1107 StartZ=0 EndX=-89.6755 EndY=19.9107 EndZ=0
    g95: LineSegment StartX=-93.8155 StartY=14.1107 StartZ=0 EndX=-93.8155 EndY=21.0107 EndZ=0
    g96-g106: Circle x11 (B-spline internal-alignment scaffolding for g107; pole/knot coordinates omitted)
    g107: BSplineCurve PolesCount=11 KnotsCount=9 Degree=3 IsPeriodic=0
    g108-g116: GeomPoint x9 (B-spline internal-alignment scaffolding for g107; pole/knot coordinates omitted)
    g117: BSplineCurve PolesCount=11 KnotsCount=9 Degree=3 IsPeriodic=0
    g118-g125: Circle x8 (B-spline internal-alignment scaffolding for g126; pole/knot coordinates omitted)
    g126: BSplineCurve PolesCount=8 KnotsCount=6 Degree=3 IsPeriodic=0
    g127-g132: GeomPoint x6 (B-spline internal-alignment scaffolding for g126; pole/knot coordinates omitted)
    g133: BSplineCurve PolesCount=8 KnotsCount=6 Degree=3 IsPeriodic=0
    g134: LineSegment StartX=-85.7455 StartY=21.0107 StartZ=0 EndX=-85.7455 EndY=14.1107 EndZ=0
    g135: LineSegment StartX=-80.0879 StartY=14.1107 StartZ=0 EndX=-75.944 EndY=14.1107 EndZ=0
    g136: LineSegment StartX=-72.014 StartY=14.1107 StartZ=0 EndX=-67.874 EndY=14.1107 EndZ=0
    g137: LineSegment StartX=-63.944 StartY=14.1107 StartZ=0 EndX=-59.804 EndY=14.1107 EndZ=0
    g138: LineSegment StartX=-80.0879 StartY=14.1107 StartZ=0 EndX=-80.0879 EndY=25.9907 EndZ=0
    g139: LineSegment StartX=-80.0879 StartY=25.9907 StartZ=0 EndX=-76.0579 EndY=25.9907 EndZ=0
    g140: LineSegment StartX=-76.0579 StartY=25.9907 StartZ=0 EndX=-76.0579 EndY=24.0907 EndZ=0
    g141: LineSegment StartX=-75.944 StartY=14.1107 StartZ=0 EndX=-75.944 EndY=19.9107 EndZ=0
    g142: LineSegment StartX=-67.874 StartY=14.1107 StartZ=0 EndX=-67.874 EndY=19.9107 EndZ=0
    g143: LineSegment StartX=-72.014 StartY=14.1107 StartZ=0 EndX=-72.014 EndY=21.0107 EndZ=0
    g144-g148: Circle x5 (B-spline internal-alignment scaffolding for g149; pole/knot coordinates omitted)
    g149: BSplineCurve PolesCount=11 KnotsCount=9 Degree=3 IsPeriodic=0
    g150-g158: GeomPoint x9 (B-spline internal-alignment scaffolding for g149; pole/knot coordinates omitted)
    g159: BSplineCurve PolesCount=11 KnotsCount=9 Degree=3 IsPeriodic=0
    g160-g167: Circle x8 (B-spline internal-alignment scaffolding for g168; pole/knot coordinates omitted)
    g168: BSplineCurve PolesCount=8 KnotsCount=6 Degree=3 IsPeriodic=0
    g169-g174: GeomPoint x6 (B-spline internal-alignment scaffolding for g168; pole/knot coordinates omitted)
    g175: BSplineCurve PolesCount=8 KnotsCount=6 Degree=3 IsPeriodic=0
    g176: LineSegment StartX=-63.944 StartY=21.0107 StartZ=0 EndX=-63.944 EndY=14.1107 EndZ=0
    g177: LineSegment StartX=-59.804 StartY=14.1107 StartZ=0 EndX=-59.804 EndY=21.5868 EndZ=0
    g178: BSplineCurve PolesCount=4 KnotsCount=2 Degree=3 IsPeriodic=0
    g179: GeomPoint X=-59.804 Y=21.5868 Z=0
    g180: GeomPoint X=-60.2379 Y=24.0907 Z=0
    g181: LineSegment StartX=-81.6055 StartY=14.1107 StartZ=0 EndX=-81.6055 EndY=21.5868 EndZ=0
    g182: LineSegment StartX=-151.619 StartY=24.0313 StartZ=0 EndX=-145.128 EndY=24.0313 EndZ=0
    g183: Circle CenterX=-82.0394 CenterY=24.0907 CenterZ=0 NormalX=0 NormalY=0 NormalZ=1 AngleXU=0 Radius=1
    g184: Circle CenterX=-81.7131 CenterY=23.2736 CenterZ=0 NormalX=0 NormalY=0 NormalZ=1 AngleXU=0 Radius=1
    g185: Circle CenterX=-81.6055 CenterY=21.5868 CenterZ=0 NormalX=0 NormalY=0 NormalZ=1 AngleXU=0 Radius=1
    g186: BSplineCurve PolesCount=3 KnotsCount=2 Degree=2 IsPeriodic=0
    g187: GeomPoint X=-82.0394 Y=24.0907 Z=0
    g188: GeomPoint X=-81.6055 Y=21.5868 Z=0
    g189: Ellipse CenterX=-37.3522 CenterY=19.9515 CenterZ=0 NormalX=0 NormalY=0 NormalZ=1 MajorRadius=2.99755 MinorRadius=2.49 AngleXU=1.5708
    g190: GeomPoint X=-37.3522 Y=21.6203 Z=0
    g191: GeomPoint X=-37.3522 Y=18.2826 Z=0
    g192: ArcOfEllipse CenterX=-38.7647 CenterY=20.06 CenterZ=0 NormalX=0 NormalY=0 NormalZ=1 MajorRadius=6.30025 MinorRadius=5.3849 AngleXU=1.57276 StartAngle=5.50632 EndAngle=10.3035
    g193: GeomPoint X=-38.7711 Y=23.3304 Z=0
    g194: GeomPoint X=-38.7583 Y=16.7895 Z=0
    g195: LineSegment StartX=-34.6109 StartY=14.1107 StartZ=0 EndX=-30.8984 EndY=14.1107 EndZ=0
    g196: LineSegment StartX=-30.8984 StartY=14.1107 StartZ=0 EndX=-30.8984 EndY=31.1784 EndZ=0
    g197: LineSegment StartX=-30.8984 StartY=31.1784 StartZ=0 EndX=-34.9984 EndY=31.1784 EndZ=0
    g198: LineSegment StartX=-34.9984 StartY=24.5602 StartZ=0 EndX=-34.9984 EndY=31.1784 EndZ=0
    g199: LineSegment StartX=-34.6109 StartY=16.0476 StartZ=0 EndX=-34.6109 EndY=14.1107 EndZ=0
    g200: LineSegment StartX=-14.8781 StartY=14.1107 StartZ=0 EndX=-10.5106 EndY=14.1107 EndZ=0
    g201: LineSegment StartX=-14.8781 StartY=14.1107 StartZ=0 EndX=-14.8781 EndY=25.8504 EndZ=0
    g202: LineSegment StartX=-14.8781 StartY=25.8504 StartZ=0 EndX=-10.8534 EndY=25.8504 EndZ=0
    g203: LineSegment StartX=-10.8534 StartY=25.8504 StartZ=0 EndX=-10.8534 EndY=24.0923 EndZ=0
    g204: LineSegment StartX=-10.5106 StartY=14.1107 StartZ=0 EndX=-10.5106 EndY=19.7752 EndZ=0
    g205: LineSegment StartX=-5.96397 StartY=25.9304 StartZ=0 EndX=-5.96397 EndY=22.574 EndZ=0
    g206-g214: Circle x9 (B-spline internal-alignment scaffolding for g215; pole/knot coordinates omitted)
    g215: BSplineCurve PolesCount=9 KnotsCount=7 Degree=3 IsPeriodic=0
    g216-g222: GeomPoint x7 (B-spline internal-alignment scaffolding for g215; pole/knot coordinates omitted)
    g223-g232: Circle x10 (B-spline internal-alignment scaffolding for g233; pole/knot coordinates omitted)
    g233: BSplineCurve PolesCount=10 KnotsCount=8 Degree=3 IsPeriodic=0
    g234-g241: GeomPoint x8 (B-spline internal-alignment scaffolding for g233; pole/knot coordinates omitted)
    g242: LineSegment StartX=-1.58923 StartY=21.0696 StartZ=0 EndX=2.62034 EndY=21.0696 EndZ=0
    g243: LineSegment StartX=-1.55856 StartY=18.7342 StartZ=0 EndX=6.45946 EndY=18.7342 EndZ=0
    g244: LineSegment StartX=5.29231 StartY=17.386 StartZ=0 EndX=5.29231 EndY=14.3674 EndZ=0
    g245-g269: Circle x25 (B-spline internal-alignment scaffolding for g270; pole/knot coordinates omitted)
    g270: BSplineCurve PolesCount=25 KnotsCount=23 Degree=3 IsPeriodic=0
    g271-g293: GeomPoint x23 (B-spline internal-alignment scaffolding for g270; pole/knot coordinates omitted)
    g294-g304: Circle x11 (B-spline internal-alignment scaffolding for g305; pole/knot coordinates omitted)
    g305: BSplineCurve PolesCount=11 KnotsCount=9 Degree=3 IsPeriodic=0
    g306-g314: GeomPoint x9 (B-spline internal-alignment scaffolding for g305; pole/knot coordinates omitted)
  constraints (245):
    c: Coincident(g1,g0)
    c: Horizontal(g0)
    c: Vertical(g1)
    c: Coincident(g2,g3)
    c: Coincident(g3,g4)
    c: Horizontal(g4)
    c: Horizontal(g2)
    c: Vertical(g3)
    c: Block(g1)
    c: Distance(g3) = 4.86
    c: Block(g4)
    c: Distance(g0) = 10.8
    c: Distance(g2) = 10.8
    c: Coincident(g5,g0)
    c: Coincident(g6,g4)
    c: Coincident(g6,g2)
    c: Block(g8)
    c: Block(g7)
    c: Coincident(g9,g8)
    c: Coincident(g9,g7)
    c: Vertical(g9)
    c: Coincident(g10,g7)
    c: Coincident(g10,g8)
    c: Vertical(g10)
    c: Weight(g11) = 1
    c: Equal(g11, g12-g21) x10
    c: InternalAlignment(g11-g21 -> g22) x11
    c: InternalAlignment(g23-g31 -> g22) x9
    c: Block(g22)
    c: Weight(g32) = 1
    c: Equal(g32, g33-g49) x17
    c: InternalAlignment(g32-g49 -> g50) x18
    c: InternalAlignment(g51-g66 -> g50) x16
    c: Block(g50)
    c: Coincident(g67,g50)
    c: Coincident(g67,g22)
    c: Coincident(g68,g22)
    c: Coincident(g68,g50)
    c: InternalAlignment(g70,g69)
    c: InternalAlignment(g71,g69)
    c: Block(g69)
    c: InternalAlignment(g73,g72)
    c: InternalAlignment(g74,g72)
    c: Block(g72)
    c: InternalAlignment(g76,g75)
    c: InternalAlignment(g77,g75)
    c: InternalAlignment(g78,g80)
    c: InternalAlignment(g79,g80)
    c: Block(g80)
    c: Coincident(g75,g80)
    c: Block(g75)
    c: InternalAlignment(g82,g81)
    c: InternalAlignment(g83,g81)
    c: InternalAlignment(g84,g86)
    c: InternalAlignment(g85,g86)
    c: Block(g86)
    c: Coincident(g81,g86)
    c: Block(g81)
    c: Horizontal(g87)
    c: Block(g87)
    c: Horizontal(g88)
    c: Distance(g88) = 4.14
    c: Horizontal(g89)
    c: Equal(g88,g89) = 4.14
    c: Block(g89)
    c: Block(g88)
    c: Coincident(g90,g87)
    c: Vertical(g90)
    c: Distance(g90) = 11.88
    c: Coincident(g91,g90)
    c: Horizontal(g91)
    c: Coincident(g92,g91)
    c: Vertical(g92)
    c: Distance(g91) = 4.03
    c: Distance(g92) = 1.9
    c: Coincident(g93,g87)
    c: Vertical(g93)
    c: Vertical(g94)
    c: Coincident(g94,g88)
    c: Distance(g93) = 5.8
    c: Distance(g94) = 5.8
    c: Vertical(g95)
    c: Coincident(g95,g88)
    c: Distance(g95) = 6.9
    c: Coincident(g107,g92)
    c: Weight(g96) = 1
    c: Equal(g96, g97-g106) x10
    c: InternalAlignment(g96-g106 -> g107) x11
    c: InternalAlignment(g108-g116 -> g107) x9
    c: Block(g107)
    c: Block(g117)
    c: Coincident(g126,g93)
    c: Weight(g118) = 1
    c: Equal(g118, g119-g125) x7
    c: Coincident(g126,g95)
    c: InternalAlignment(g118-g125 -> g126) x8
    c: InternalAlignment(g127-g132 -> g126) x6
    c: Coincident(g133,g94)
    c: Block(g126)
    c: Block(g133)
    c: Coincident(g134,g133)
    c: Coincident(g134,g89)
    c: Vertical(g134)
    c: Horizontal(g135)
    c: Block(g135)
    c: Horizontal(g136)
    c: Equal(g88,g136) = 4.14
    c: Horizontal(g137)
    c: Equal(g136,g137) = 4.14
    c: Block(g137)
    c: Block(g136)
    c: Coincident(g138,g135)
    c: Vertical(g138)
    c: Equal(g90,g138) = 11.88
    c: Coincident(g139,g138)
    c: Horizontal(g139)
    c: Coincident(g140,g139)
    c: Vertical(g140)
    c: Equal(g91,g139) = 4.03
    c: Equal(g92,g140) = 1.9
    c: Coincident(g141,g135)
    c: Vertical(g141)
    c: Vertical(g142)
    c: Coincident(g142,g136)
    c: Equal(g93,g141) = 5.8
    c: Equal(g94,g142) = 5.8
    c: Vertical(g143)
    c: Coincident(g143,g136)
    c: Equal(g95,g143) = 6.9
    c: Coincident(g149,g140)
    c: Equal(g96,g144) = 1
    c: Equal(g144, g145-g148) x4
    c: InternalAlignment(g144-g148 -> g149) x5
    c: InternalAlignment(g150-g158 -> g149) x9
    c: Block(g149)
    c: Block(g159)
    c: Coincident(g168,g141)
    c: Equal(g118,g160) = 1
    c: Equal(g160, g161-g167) x7
    c: Coincident(g168,g143)
    c: InternalAlignment(g160-g167 -> g168) x8
    c: InternalAlignment(g169-g174 -> g168) x6
    c: Coincident(g175,g142)
    c: Block(g168)
    c: Block(g175)
    c: Coincident(g176,g175)
    c: Coincident(g176,g137)
    c: Vertical(g176)
    c: Coincident(g177,g137)
    c: Vertical(g177)
    c: Coincident(g178,g177)
    c: Coincident(g178,g159)
    c: InternalAlignment(g179,g178)
    c: InternalAlignment(g180,g178)
    c: Block(g178)
    c: Vertical(g181)
    c: Coincident(g181,g89)
    c: Block(g5)
    c: Coincident(g182,g1)
    c: Coincident(g182,g5)
    c: Horizontal(g182)
    c: Coincident(g186,g117)
    c: Weight(g183) = 1
    c: Equal(g183,g184)
    c: Equal(g183,g185)
    c: Coincident(g186,g181)
    c: InternalAlignment(g183,g186)
    c: InternalAlignment(g184,g186)
    c: InternalAlignment(g185,g186)
    c: InternalAlignment(g187,g186)
    c: InternalAlignment(g188,g186)
    c: Block(g186)
    c: InternalAlignment(g190,g189)
    c: InternalAlignment(g191,g189)
    c: Block(g189)
    c: InternalAlignment(g193,g192)
    c: InternalAlignment(g194,g192)
    c: Block(g192)
    c: Horizontal(g195)
    c: Block(g195)
    c: Coincident(g196,g195)
    c: Vertical(g196)
    c: Block(g196)
    c: Distance(g195) = 3.71244
    c: Coincident(g197,g196)
    c: Horizontal(g197)
    c: Distance(g197) = 4.1
    c: Coincident(g198,g192)
    c: Coincident(g198,g197)
    c: Vertical(g198)
    c: Block(g198)
    c: Coincident(g199,g192)
    c: Coincident(g199,g195)
    c: Vertical(g199)
    c: Block(g199)
    c: Horizontal(g200)
    c: Block(g200)
    c: Coincident(g201,g200)
    c: Vertical(g201)
    c: Block(g201)
    c: Coincident(g202,g201)
    c: Horizontal(g202)
    c: Block(g202)
    c: Coincident(g203,g202)
    c: Vertical(g203)
    c: Block(g203)
    c: Coincident(g204,g200)
    c: Vertical(g204)
    c: Block(g204)
    c: Coincident(g215,g203)
    c: Weight(g206) = 1
    c: Equal(g206, g207-g214) x8
    c: Coincident(g215,g205)
    c: InternalAlignment(g206-g214 -> g215) x9
    c: InternalAlignment(g216-g222 -> g215) x7
    c: Coincident(g233,g204)
    c: Weight(g223) = 1
    c: Equal(g223, g224-g232) x9
    c: Coincident(g233,g205)
    c: InternalAlignment(g223-g232 -> g233) x10
    c: InternalAlignment(g234-g241 -> g233) x8
    c: Vertical(g205)
    c: Block(g205)
    c: Block(g215)
    c: Block(g233)
    c: Horizontal(g242)
    c: Horizontal(g243)
    c: Block(g242)
    c: Block(g243)
    c: Vertical(g244)
    c: Block(g244)
    c: Coincident(g270,g243)
    c: Weight(g245) = 1
    c: Equal(g245, g246-g269) x24
    c: Coincident(g270,g244)
    c: InternalAlignment(g245-g269 -> g270) x25
    c: InternalAlignment(g271-g293 -> g270) x23
    c: Block(g270)
    c: Coincident(g305,g242)
    c: Weight(g294) = 1
    c: Equal(g294, g295-g304) x10
    c: Coincident(g305,g242)
    c: InternalAlignment(g294-g304 -> g305) x11
    c: InternalAlignment(g306-g314 -> g305) x9
    c: Block(g305)
FEATURE [PartDesign::Body] Body
  Group = -> [Sketch083]
  Origin = -> Origin
FEATURE [Sketcher::SketchObject] Sketch084
  FullyConstrained = true
  MapMode = 5
  Support = -> [XY_Plane001]
FEATURE [PartDesign::Body] Body001
  Group = -> [Sketch084]
  Origin = -> Origin001
